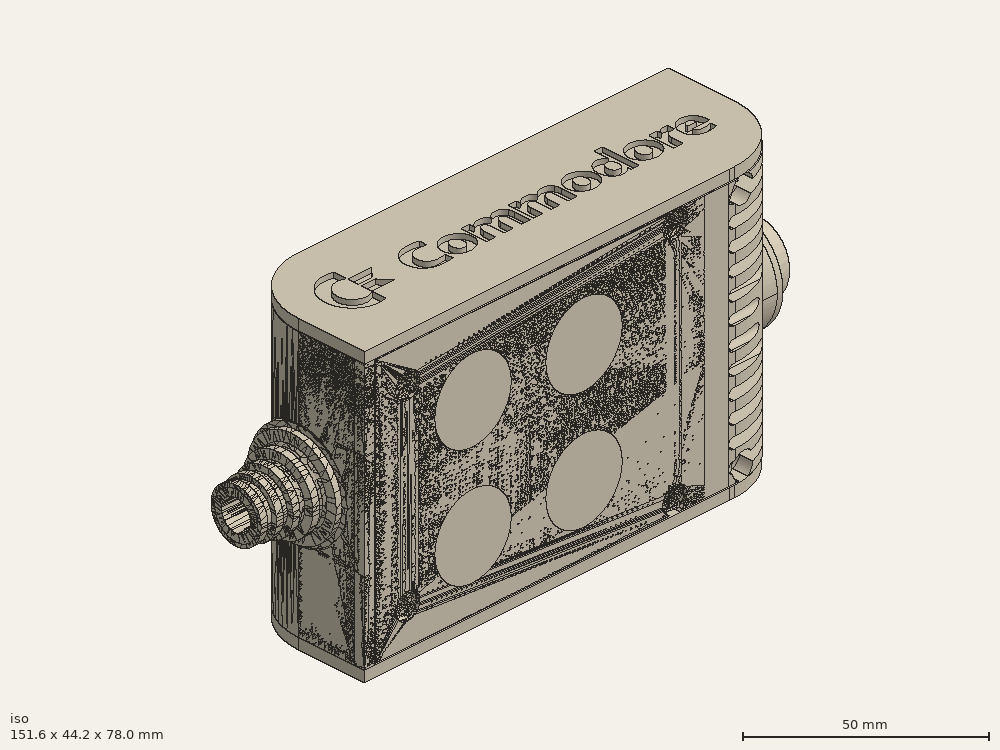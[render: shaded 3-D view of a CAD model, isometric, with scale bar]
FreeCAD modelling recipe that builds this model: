
FCSTD DOCUMENT  (FreeCAD 0.19R0.19.2)
Label: enclosure_214FCStd
License: All rights reserved
LicenseURL: http://en.wikipedia.org/wiki/All_rights_reserved
objects: Part::Revolution×152, Part::MultiFuse×146, Part::Feature×146, Sketcher::SketchObject×88, Part::Extrusion×73, Part::Cut×72, Part::Cylinder×70, Part::Fillet×58, Part::Box×36, App::MeasureDistance×4, Part::FeaturePython×2, Image::ImagePlane×1, PartDesign::Body×1, Part::Mirroring×1
note: 845 computed .brp shape members not serialized (recipe doc carries the construction recipe); baked Part::Feature solids carry a one-line shape summary decoded from their .brp

FEATURE [Sketcher::SketchObject] Sketch  label="topSketch"
  FullyConstrained = true
  sketch-geometry (20):
    g0: LineSegment StartX=5.21097e-06 StartY=3 StartZ=0 EndX=5.21097e-06 EndY=19 EndZ=0
    g1: ArcOfCircle CenterX=19 CenterY=19 CenterZ=0 NormalX=0 NormalY=0 NormalZ=1 AngleXU=0 Radius=19 StartAngle=1.5708 EndAngle=3.14159
    g2: ArcOfCircle CenterX=19 CenterY=19 CenterZ=0 NormalX=0 NormalY=0 NormalZ=1 AngleXU=0 Radius=16 StartAngle=1.5708 EndAngle=3.14159
    g3: LineSegment StartX=114 StartY=35 StartZ=0 EndX=19 EndY=35 EndZ=0
    g4: LineSegment StartX=5.21097e-06 StartY=3 StartZ=0 EndX=5.21097e-06 EndY=0 EndZ=0
    g5: LineSegment StartX=3 StartY=0 StartZ=0 EndX=5.21097e-06 EndY=0 EndZ=0
    g6: LineSegment StartX=3 StartY=19 StartZ=0 EndX=3 EndY=0 EndZ=0
    g7: LineSegment StartX=19 StartY=38 StartZ=0 EndX=124 EndY=38 EndZ=0
    g8: Circle CenterX=119 CenterY=35 CenterZ=0 NormalX=0 NormalY=0 NormalZ=1 AngleXU=0 Radius=1
    g9: Circle CenterX=121 CenterY=35 CenterZ=0 NormalX=0 NormalY=0 NormalZ=1 AngleXU=0 Radius=1
    g10: Circle CenterX=121 CenterY=33 CenterZ=0 NormalX=0 NormalY=0 NormalZ=1 AngleXU=0 Radius=1
    g11: BSplineCurve PolesCount=3 KnotsCount=2 Degree=2 IsPeriodic=0
    g12: GeomPoint X=119 Y=35 Z=0
    g13: GeomPoint X=121 Y=33 Z=0
    g14: LineSegment StartX=119 StartY=35 StartZ=0 EndX=114 EndY=35 EndZ=0
    g15: ArcOfCircle CenterX=105 CenterY=19 CenterZ=0 NormalX=0 NormalY=0 NormalZ=1 AngleXU=0 Radius=19 StartAngle=5.7297 EndAngle=6.28319
    g16: ArcOfCircle CenterX=105 CenterY=19 CenterZ=0 NormalX=0 NormalY=0 NormalZ=1 AngleXU=0 Radius=16 StartAngle=5.60905 EndAngle=6.28319
    g17: LineSegment StartX=121 StartY=33 StartZ=0 EndX=121 EndY=19 EndZ=0
    g18: LineSegment StartX=124 StartY=38 StartZ=0 EndX=124 EndY=19 EndZ=0
    g19: LineSegment StartX=117.5 StartY=9.01251 StartZ=0 EndX=121.163 EndY=9.0125 EndZ=0
  constraints (46):
    c: Vertical(g0)
    c: Block(g0)
    c: Coincident(g1,g0)
    c: Block(g1)
    c: Coincident(g2,g1)
    c: Block(g2)
    c: Coincident(g3,g2)
    c: Horizontal(g3)
    c: Tangent(g3,g2)
    c: Coincident(g4,g0)
    c: Distance(g4) = 3
    c: Vertical(g4)
    c: Coincident(g5,g4)
    c: Horizontal(g5)
    c: Coincident(g6,g2)
    c: Coincident(g6,g5)
    c: Vertical(g6)
    c: Horizontal(g7)
    c: Distance(g7) = 105
    c: Coincident(g7,g1)
    c: Block(g3)
    c: Weight(g8) = 1
    c: Equal(g8,g9)
    c: Equal(g8,g10)
    c: InternalAlignment(g8,g11)
    c: InternalAlignment(g9,g11)
    c: InternalAlignment(g10,g11)
    c: InternalAlignment(g12,g11)
    c: InternalAlignment(g13,g11)
    c: Block(g11)
    c: Coincident(g14,g11)
    c: Coincident(g14,g3)
    c: Horizontal(g14)
    c: Block(g15)
    c: Coincident(g16,g15)
    c: Block(g16)
    c: Coincident(g17,g11)
    c: Coincident(g17,g16)
    c: Vertical(g17)
    c: Distance(g17) = 14
    c: Coincident(g18,g7)
    c: Coincident(g18,g15)
    c: Vertical(g18)
    c: Distance(g18) = 19
    c: Coincident(g19,g16)
    c: Coincident(g19,g15)
FEATURE [Sketcher::SketchObject] Sketch001  label="bottomSketch"
  FullyConstrained = true
  sketch-geometry (32):
    g0: LineSegment StartX=3.3 StartY=-6.03275e-07 StartZ=0 EndX=98 EndY=-6.03275e-07 EndZ=0
    g1: ArcOfCircle CenterX=98 CenterY=19 CenterZ=0 NormalX=0 NormalY=0 NormalZ=1 AngleXU=0 Radius=19 StartAngle=4.71239 EndAngle=5.71103
    g2: LineSegment StartX=6.3 StartY=8 StartZ=0 EndX=3.3 EndY=8 EndZ=0
    g3: LineSegment StartX=3.3 StartY=8 StartZ=0 EndX=3.3 EndY=-6.03275e-07 EndZ=0
    g4: ArcOfCircle CenterX=8.3 CenterY=5 CenterZ=0 NormalX=0 NormalY=0 NormalZ=1 AngleXU=0 Radius=2 StartAngle=3.14159 EndAngle=4.71239
    g5: LineSegment StartX=6.3 StartY=8 StartZ=0 EndX=6.3 EndY=5 EndZ=0
    g6: ArcOfCircle CenterX=98 CenterY=19 CenterZ=0 NormalX=0 NormalY=0 NormalZ=1 AngleXU=0 Radius=12.7 StartAngle=4.71239 EndAngle=6.28319
    g7: LineSegment StartX=94.7 StartY=3 StartZ=0 EndX=8.3 EndY=3 EndZ=0
    g8-g12: Circle x5 (B-spline internal-alignment scaffolding for g13; pole/knot coordinates omitted)
    g13: BSplineCurve PolesCount=5 KnotsCount=3 Degree=3 IsPeriodic=0
    g14: GeomPoint X=98 Y=6.3 Z=0
    g15: GeomPoint X=96.3938 Y=4.71946 Z=0
    g16: GeomPoint X=94.7 Y=3 Z=0
    g17-g23: Circle x7 (B-spline internal-alignment scaffolding for g24; pole/knot coordinates omitted)
    g24: BSplineCurve PolesCount=7 KnotsCount=5 Degree=3 IsPeriodic=0
    g25-g29: GeomPoint x5 (B-spline internal-alignment scaffolding for g24; pole/knot coordinates omitted)
    g30: ArcOfCircle CenterX=98 CenterY=19 CenterZ=0 NormalX=0 NormalY=0 NormalZ=1 AngleXU=0 Radius=15.7 StartAngle=5.81226 EndAngle=6.28319
    g31: LineSegment StartX=110.7 StartY=19 StartZ=0 EndX=113.7 EndY=19 EndZ=0
  constraints (41):
    c: Horizontal(g0)
    c: Coincident(g1,g0)
    c: Block(g1)
    c: Horizontal(g2)
    c: Distance(g2) = 3
    c: Coincident(g3,g2)
    c: Vertical(g3)
    c: Coincident(g3,g0)
    c: Block(g4)
    c: Block(g2)
    c: Coincident(g5,g2)
    c: Coincident(g5,g4)
    c: Vertical(g5)
    c: Coincident(g6,g1)
    c: Block(g6)
    c: Coincident(g7,g4)
    c: Horizontal(g7)
    c: Block(g0)
    c: Block(g7)
    c: Block(g3)
    c: Coincident(g13,g6)
    c: Weight(g8) = 1
    c: Equal(g8, g9-g12) x4
    c: Coincident(g13,g7)
    c: InternalAlignment(g8-g12 -> g13) x5
    c: InternalAlignment(g14,g13)
    c: InternalAlignment(g15,g13)
    c: InternalAlignment(g16,g13)
    c: Block(g13)
    c: Weight(g17) = 1
    c: Equal(g17, g18-g23) x6
    c: Coincident(g24,g1)
    c: InternalAlignment(g17-g23 -> g24) x7
    c: InternalAlignment(g25-g29 -> g24) x5
    c: Block(g24)
    c: Coincident(g30,g24)
    c: Coincident(g31,g6)
    c: Coincident(g31,g30)
    c: Horizontal(g31)
    c: Block(g31)
    c: Block(g30)
FEATURE [Part::Extrusion] Extrude  label="top"
  Base = -> Sketch
  Dir = (0,0,1)
  DirMode = 2
  FaceMakerClass = Part::FaceMakerBullseye
  LengthFwd = 72
  LengthRev = 0
  Solid = true
  Symmetric = false
FEATURE [Part::Extrusion] Extrude001  label="bottom"
  Base = -> Sketch001
  Dir = (0,0,1)
  DirMode = 2
  FaceMakerClass = Part::FaceMakerBullseye
  LengthFwd = 71.4
  LengthRev = 0
  Placement = pos=(0,0,0.3) rot=(0,0,1;0rad)
  Solid = true
  Symmetric = false
FEATURE [Sketcher::SketchObject] Sketch002  label="topSketch001"
  FullyConstrained = true
  sketch-geometry (8):
    g0: ArcOfCircle CenterX=19 CenterY=19.0975 CenterZ=0 NormalX=0 NormalY=0 NormalZ=1 AngleXU=0 Radius=18.9025 StartAngle=1.5708 EndAngle=3.14674
    g1: LineSegment StartX=0.0977805 StartY=19.0003 StartZ=0 EndX=0.0977805 EndY=0.000251602 EndZ=0
    g2: LineSegment StartX=19 StartY=38 StartZ=0 EndX=124 EndY=38 EndZ=0
    g3: LineSegment StartX=0.0977805 StartY=0.000251602 StartZ=0 EndX=105.098 EndY=0.000251602 EndZ=0
    g4: LineSegment StartX=124 StartY=38 StartZ=0 EndX=125.616 EndY=38 EndZ=0
    g5: LineSegment StartX=105.098 StartY=0.000251602 StartZ=0 EndX=106.713 EndY=0.000251602 EndZ=0
    g6: ArcOfCircle CenterX=106.616 CenterY=19 CenterZ=0 NormalX=0 NormalY=0 NormalZ=1 AngleXU=0 Radius=19 StartAngle=4.71754 EndAngle=6.28319
    g7: LineSegment StartX=125.616 StartY=38 StartZ=0 EndX=125.616 EndY=19 EndZ=0
  constraints (21):
    c: Block(g0)
    c: Coincident(g1,g0)
    c: Vertical(g1)
    c: Horizontal(g2)
    c: Distance(g2) = 105
    c: Coincident(g2,g0)
    c: Distance(g1) = 19
    c: Coincident(g3,g1)
    c: Horizontal(g3)
    c: Distance(g3) = 105
    c: Coincident(g4,g2)
    c: Horizontal(g4)
    c: Distance(g4) = 1.61553
    c: Horizontal(g5)
    c: Equal(g4,g5) = 1.61553
    c: Coincident(g5,g3)
    c: Block(g6)
    c: Coincident(g6,g5)
    c: Coincident(g7,g4)
    c: Coincident(g7,g6)
    c: Vertical(g7)
FEATURE [Part::Extrusion] Extrude002  label="sideA"
  Base = -> Sketch002
  Dir = (0,0,1)
  DirMode = 2
  FaceMakerClass = Part::FaceMakerBullseye
  LengthFwd = 3
  LengthRev = 0
  Placement = pos=(0,0,-3) rot=(0,0,1;0rad)
  Solid = true
  Symmetric = false
FEATURE [Sketcher::SketchObject] Sketch003  label="topSketch002"
  FullyConstrained = true
  sketch-geometry (6):
    g0: LineSegment StartX=19 StartY=38 StartZ=0 EndX=117 EndY=38 EndZ=0
    g1: ArcOfCircle CenterX=19 CenterY=19 CenterZ=0 NormalX=0 NormalY=0 NormalZ=1 AngleXU=0 Radius=19 StartAngle=1.5708 EndAngle=3.14159
    g2: LineSegment StartX=117 StartY=38 StartZ=0 EndX=117 EndY=19 EndZ=0
    g3: LineSegment StartX=98 StartY=1.0161e-12 StartZ=0 EndX=5.22862e-06 EndY=1.0161e-12 EndZ=0
    g4: LineSegment StartX=5.22862e-06 StartY=19 StartZ=0 EndX=5.22862e-06 EndY=1.0161e-12 EndZ=0
    g5: ArcOfCircle CenterX=98 CenterY=19 CenterZ=0 NormalX=0 NormalY=0 NormalZ=1 AngleXU=0 Radius=19 StartAngle=4.71239 EndAngle=6.28319
  constraints (16):
    c: Horizontal(g0)
    c: Distance(g0) = 98
    c: Coincident(g1,g0)
    c: Block(g1)
    c: Coincident(g2,g0)
    c: Vertical(g2)
    c: Distance(g2) = 19
    c: Horizontal(g3)
    c: Coincident(g4,g1)
    c: Vertical(g4)
    c: Coincident(g3,g4)
    c: Block(g3)
    c: Coincident(g5,g2)
    c: Coincident(g5,g3)
    c: Block(g0)
    c: Block(g5)
FEATURE [Sketcher::SketchObject] Sketch004
  FullyConstrained = true
  MapMode = 3
  Placement = pos=(0,0,0) rot=(1,0,0;1.5708rad)
  Support = -> [Extrude]
  sketch-geometry (8):
    g0: Circle CenterX=80.351 CenterY=-67.6202 CenterZ=0 NormalX=0 NormalY=0 NormalZ=1 AngleXU=0 Radius=2
    g1: Circle CenterX=80.351 CenterY=-67.6202 CenterZ=0 NormalX=0 NormalY=0 NormalZ=1 AngleXU=0 Radius=3
    g2: Circle CenterX=80.351 CenterY=-4.92017 CenterZ=0 NormalX=0 NormalY=0 NormalZ=1 AngleXU=0 Radius=2
    g3: Circle CenterX=80.351 CenterY=-4.92017 CenterZ=0 NormalX=0 NormalY=0 NormalZ=1 AngleXU=0 Radius=3
    g4: Circle CenterX=23.851 CenterY=-4.92017 CenterZ=0 NormalX=0 NormalY=0 NormalZ=1 AngleXU=0 Radius=2
    g5: Circle CenterX=23.851 CenterY=-4.92017 CenterZ=0 NormalX=0 NormalY=0 NormalZ=1 AngleXU=0 Radius=3
    g6: Circle CenterX=23.851 CenterY=-67.6202 CenterZ=0 NormalX=0 NormalY=0 NormalZ=1 AngleXU=0 Radius=2
    g7: Circle CenterX=23.851 CenterY=-67.6202 CenterZ=0 NormalX=0 NormalY=0 NormalZ=1 AngleXU=0 Radius=3
  constraints (8):
    c: Block(g3)
    c: Block(g2)
    c: Block(g1)
    c: Block(g0)
    c: Block(g6)
    c: Block(g7)
    c: Block(g4)
    c: Block(g5)
FEATURE [Part::Extrusion] Extrude004
  Base = -> Sketch004
  Dir = (0,-1,2e-16)
  DirMode = 2
  FaceMakerClass = Part::FaceMakerBullseye
  LengthFwd = 6
  LengthRev = 0
  Placement = pos=(0,9,0) rot=(0,0,1;0rad)
  Solid = true
  Symmetric = false
FEATURE [Sketcher::SketchObject] Sketch005
  FullyConstrained = true
  MapMode = 3
  Placement = pos=(0,0,0) rot=(1,0,0;1.5708rad)
  Support = -> [Extrude]
  sketch-geometry (8):
    g0: Circle CenterX=80.351 CenterY=-67.6202 CenterZ=0 NormalX=0 NormalY=0 NormalZ=1 AngleXU=0 Radius=3
    g1: Circle CenterX=80.351 CenterY=-4.92017 CenterZ=0 NormalX=0 NormalY=0 NormalZ=1 AngleXU=0 Radius=3
    g2: Circle CenterX=23.851 CenterY=-4.92017 CenterZ=0 NormalX=0 NormalY=0 NormalZ=1 AngleXU=0 Radius=3
    g3: Circle CenterX=23.851 CenterY=-67.6202 CenterZ=0 NormalX=0 NormalY=0 NormalZ=1 AngleXU=0 Radius=3
    g4: Circle CenterX=23.851 CenterY=-67.6202 CenterZ=0 NormalX=0 NormalY=0 NormalZ=1 AngleXU=0 Radius=5
    g5: Circle CenterX=80.351 CenterY=-67.6202 CenterZ=0 NormalX=0 NormalY=0 NormalZ=1 AngleXU=0 Radius=5
    g6: Circle CenterX=23.851 CenterY=-4.92017 CenterZ=0 NormalX=0 NormalY=0 NormalZ=1 AngleXU=0 Radius=5
    g7: Circle CenterX=80.351 CenterY=-4.92017 CenterZ=0 NormalX=0 NormalY=0 NormalZ=1 AngleXU=0 Radius=5
  constraints (8):
    c: Block(g1)
    c: Block(g0)
    c: Block(g3)
    c: Block(g2)
    c: Block(g5)
    c: Block(g4)
    c: Block(g6)
    c: Block(g7)
FEATURE [Part::Extrusion] Extrude005
  Base = -> Sketch005
  Dir = (0,-1,2e-16)
  DirMode = 2
  FaceMakerClass = Part::FaceMakerBullseye
  LengthFwd = 2
  LengthRev = 0
  Solid = true
  Symmetric = false
FEATURE [Sketcher::SketchObject] Sketch006
  FullyConstrained = true
  MapMode = 3
  Placement = pos=(0,0,0) rot=(1,0,0;1.5708rad)
  sketch-geometry (8):
    g0: Circle CenterX=80.351 CenterY=-67.6202 CenterZ=0 NormalX=0 NormalY=0 NormalZ=1 AngleXU=0 Radius=3
    g1: Circle CenterX=80.351 CenterY=-4.92017 CenterZ=0 NormalX=0 NormalY=0 NormalZ=1 AngleXU=0 Radius=3
    g2: Circle CenterX=23.851 CenterY=-4.92017 CenterZ=0 NormalX=0 NormalY=0 NormalZ=1 AngleXU=0 Radius=3
    g3: Circle CenterX=23.851 CenterY=-67.6202 CenterZ=0 NormalX=0 NormalY=0 NormalZ=1 AngleXU=0 Radius=3
    g4: Circle CenterX=23.851 CenterY=-67.6202 CenterZ=0 NormalX=0 NormalY=0 NormalZ=1 AngleXU=0 Radius=5
    g5: Circle CenterX=80.351 CenterY=-67.6202 CenterZ=0 NormalX=0 NormalY=0 NormalZ=1 AngleXU=0 Radius=5
    g6: Circle CenterX=23.851 CenterY=-4.92017 CenterZ=0 NormalX=0 NormalY=0 NormalZ=1 AngleXU=0 Radius=5
    g7: Circle CenterX=80.351 CenterY=-4.92017 CenterZ=0 NormalX=0 NormalY=0 NormalZ=1 AngleXU=0 Radius=5
  constraints (8):
    c: Block(g1)
    c: Block(g0)
    c: Block(g3)
    c: Block(g2)
    c: Block(g5)
    c: Block(g4)
    c: Block(g6)
    c: Block(g7)
FEATURE [Part::Extrusion] Extrude007
  Base = -> Sketch006
  Dir = (0,-1,2e-16)
  DirMode = 2
  FaceMakerClass = Part::FaceMakerBullseye
  LengthFwd = 2
  LengthRev = 0
  Solid = true
  Symmetric = false
FEATURE [Part::Fillet] Fillet
  Base = -> Extrude007
  Edges = 4 edges r=1.99: [Edge6,Edge12,Edge18,Edge24]
FEATURE [Part::Cut] Cut
  Base = -> Extrude005
  Placement = pos=(0,5,0) rot=(0,0,1;0rad)
  Tool = -> Fillet
FEATURE [Part::MultiFuse] Fusion  label="pCBScrews"
  Placement = pos=(-2.5,0,72.3) rot=(0,0,1;0rad)
  Shapes = -> [Extrude004,Cut]
FEATURE [App::MeasureDistance] Distance  label="Distance: 0.69 mm"
  Distance = 0.685967
  P1 = (24.0138,2.9647,0.3)
  P2 = (23.8901,3,-0.373787)
FEATURE [App::MeasureDistance] Distance001  label="Distance: 0.53 mm"
  Distance = 0.533607
  P1 = (80.2939,3,72.2334)
  P2 = (80.281,2.99661,71.7)
FEATURE [Part::Fillet] Fillet001
  Base = -> Extrude001
  Edges = 1 edges r=2.4: [Edge17]
FEATURE [Part::Fillet] Fillet002  label="bottom001"
  Base = -> Fillet001
  Edges = 1 edges r=2.4: [Edge36]
FEATURE [Part::Fillet] Fillet003  label="top001"
  Base = -> Extrude
  Edges = 1 edges r=2: [Edge1]
FEATURE [Sketcher::SketchObject] Sketch007
  FullyConstrained = true
  sketch-geometry (16):
    g0: LineSegment StartX=4 StartY=0 StartZ=0 EndX=4 EndY=2.4 EndZ=0
    g1: LineSegment StartX=4 StartY=2.4 StartZ=0 EndX=7 EndY=2.4 EndZ=0
    g2: LineSegment StartX=4 StartY=0 StartZ=0 EndX=5.7 EndY=0 EndZ=0
    g3: LineSegment StartX=5.7 StartY=0 StartZ=0 EndX=5.7 EndY=-5.6 EndZ=0
    g4-g8: Circle x5 (B-spline internal-alignment scaffolding for g9; pole/knot coordinates omitted)
    g9: BSplineCurve PolesCount=5 KnotsCount=3 Degree=3 IsPeriodic=0
    g10: GeomPoint X=7 Y=2.4 Z=0
    g11: GeomPoint X=10.4582 Y=-1.55472 Z=0
    g12: GeomPoint X=14 Y=-5.6 Z=0
    g13: LineSegment StartX=14 StartY=-5.6 StartZ=0 EndX=14 EndY=-14.1 EndZ=0
    g14: LineSegment StartX=14 StartY=-14.1 StartZ=0 EndX=6.5 EndY=-14.1 EndZ=0
    g15: LineSegment StartX=5.7 StartY=-5.6 StartZ=0 EndX=6.5 EndY=-14.1 EndZ=0
  constraints (28):
    c: Distance(g0) = 2.4
    c: Vertical(g0)
    c: Block(g0)
    c: Coincident(g1,g0)
    c: Horizontal(g1)
    c: Distance(g1) = 3
    c: Coincident(g2,g0)
    c: Horizontal(g2)
    c: Distance(g2) = 1.7
    c: Coincident(g3,g2)
    c: Vertical(g3)
    c: Distance(g3) = 5.6
    c: Coincident(g9,g1)
    c: Weight(g4) = 1
    c: Equal(g4, g5-g8) x4
    c: InternalAlignment(g4-g8 -> g9) x5
    c: InternalAlignment(g10,g9)
    c: InternalAlignment(g11,g9)
    c: InternalAlignment(g12,g9)
    c: Block(g9)
    c: Coincident(g13,g9)
    c: Vertical(g13)
    c: Distance(g13) = 8.5
    c: Coincident(g14,g13)
    c: Horizontal(g14)
    c: Distance(g14) = 7.5
    c: Coincident(g15,g3)
    c: Coincident(g15,g14)
FEATURE [Part::Feature] Face
  shape: bbox 10 x 16.5 x 2e-07 mm, 1 faces, 0 solids (baked)
FEATURE [Part::Revolution] Revolve  label="plugHousing"
  Angle = 360
  Axis = (0,1,0)
  Base = (0,0,0)
  FaceMakerClass = Part::FaceMakerBullseye
  Placement = pos=(0,0,36.15) rot=(0,0,1;0rad)
  Solid = false
  Source = -> Face
  Symmetric = false
FEATURE [Part::Feature] Face001
  shape: bbox 10 x 16.5 x 2e-07 mm, 1 faces, 0 solids (baked)
FEATURE [Part::Revolution] Revolve001  label="plugHousing001"
  Angle = 360
  Axis = (0,1,0)
  Base = (0,0,0)
  FaceMakerClass = Part::FaceMakerBullseye
  Placement = pos=(0,0,36.15) rot=(0,0,1;0rad)
  Solid = false
  Source = -> Face001
  Symmetric = false
FEATURE [Part::MultiFuse] Fusion001  label="plugHousing002"
  Placement = pos=(0,0,0) rot=(0,0,1;1.5708rad)
  Shapes = -> [Revolve001,Revolve]
FEATURE [Part::Feature] Face002
  shape: bbox 10 x 16.5 x 2e-07 mm, 1 faces, 0 solids (baked)
FEATURE [Part::Revolution] Revolve003  label="plugHousing005"
  Angle = 360
  Axis = (0,1,0)
  Base = (0,0,0)
  FaceMakerClass = Part::FaceMakerBullseye
  Placement = pos=(0,0,36.15) rot=(0,0,1;0rad)
  Solid = false
  Source = -> Face002
  Symmetric = false
FEATURE [Part::Feature] Face003
  shape: bbox 10 x 16.5 x 2e-07 mm, 1 faces, 0 solids (baked)
FEATURE [Part::Revolution] Revolve002  label="plugHousing003"
  Angle = 360
  Axis = (0,1,0)
  Base = (0,0,0)
  FaceMakerClass = Part::FaceMakerBullseye
  Placement = pos=(0,0,36.15) rot=(0,0,1;0rad)
  Solid = false
  Source = -> Face003
  Symmetric = false
FEATURE [Part::MultiFuse] Fusion002  label="plugHousing004"
  Placement = pos=(0,0,0) rot=(0,0,1;1.5708rad)
  Shapes = -> [Revolve002,Revolve003]
FEATURE [Part::MultiFuse] Fusion003  label="plugHousing006"
  Placement = pos=(0,19,0) rot=(0,0,1;3.14159rad)
  Shapes = -> [Fusion002,Fusion001]
FEATURE [Part::Feature] Face004
  shape: bbox 10 x 16.5 x 2e-07 mm, 1 faces, 0 solids (baked)
FEATURE [Part::Revolution] Revolve006  label="plugHousing010"
  Angle = 360
  Axis = (0,1,0)
  Base = (0,0,0)
  FaceMakerClass = Part::FaceMakerBullseye
  Placement = pos=(0,0,36.15) rot=(0,0,1;0rad)
  Solid = false
  Source = -> Face004
  Symmetric = false
FEATURE [Part::Feature] Face005
  shape: bbox 10 x 16.5 x 2e-07 mm, 1 faces, 0 solids (baked)
FEATURE [Part::Revolution] Revolve007  label="plugHousing011"
  Angle = 360
  Axis = (0,1,0)
  Base = (0,0,0)
  FaceMakerClass = Part::FaceMakerBullseye
  Placement = pos=(0,0,36.15) rot=(0,0,1;0rad)
  Solid = false
  Source = -> Face005
  Symmetric = false
FEATURE [Part::Feature] Face006
  shape: bbox 10 x 16.5 x 2e-07 mm, 1 faces, 0 solids (baked)
FEATURE [Part::Revolution] Revolve004  label="plugHousing007"
  Angle = 360
  Axis = (0,1,0)
  Base = (0,0,0)
  FaceMakerClass = Part::FaceMakerBullseye
  Placement = pos=(0,0,36.15) rot=(0,0,1;0rad)
  Solid = false
  Source = -> Face006
  Symmetric = false
FEATURE [Part::MultiFuse] Fusion004  label="plugHousing009"
  Placement = pos=(0,0,0) rot=(0,0,1;1.5708rad)
  Shapes = -> [Revolve004,Revolve007]
FEATURE [Part::Feature] Face007
  shape: bbox 10 x 16.5 x 2e-07 mm, 1 faces, 0 solids (baked)
FEATURE [Part::Revolution] Revolve005  label="plugHousing008"
  Angle = 360
  Axis = (0,1,0)
  Base = (0,0,0)
  FaceMakerClass = Part::FaceMakerBullseye
  Placement = pos=(0,0,36.15) rot=(0,0,1;0rad)
  Solid = false
  Source = -> Face007
  Symmetric = false
FEATURE [Part::MultiFuse] Fusion005  label="plugHousing012"
  Placement = pos=(0,0,0) rot=(0,0,1;1.5708rad)
  Shapes = -> [Revolve006,Revolve005]
FEATURE [Part::MultiFuse] Fusion006  label="plugHousing013"
  Placement = pos=(0,19,0) rot=(0,0,1;3.14159rad)
  Shapes = -> [Fusion005,Fusion004]
FEATURE [Part::MultiFuse] Fusion007  label="plugHousing014"
  Placement = pos=(122.621,0,-0.15) rot=(0,0,1;0rad)
  Shapes = -> [Fusion003,Fusion006]
FEATURE [Part::Cylinder] Cylinder002
  Angle = 360
  AttacherType = Attacher::AttachEngine3D
  Height = 20
  Placement = pos=(0,0,36.15) rot=(0,0,1;0rad)
  Radius = 4
FEATURE [Part::Cylinder] Cylinder003
  Angle = 360
  AttacherType = Attacher::AttachEngine3D
  Height = 10
  Placement = pos=(0,0,36.15) rot=(0,0,1;0rad)
  Radius = 4
FEATURE [Part::MultiFuse] Fusion009  label="removeToCreateHoleForPlugHousing"
  Placement = pos=(70,19,36.15) rot=(0,1,0;1.5708rad)
  Shapes = -> [Cylinder002,Cylinder003]
FEATURE [Part::Cylinder] Cylinder004
  Angle = 360
  AttacherType = Attacher::AttachEngine3D
  Height = 20
  Placement = pos=(0,0,36.15) rot=(0,0,1;0rad)
  Radius = 4
FEATURE [Part::Cylinder] Cylinder005
  Angle = 360
  AttacherType = Attacher::AttachEngine3D
  Height = 10
  Placement = pos=(0,0,36.15) rot=(0,0,1;0rad)
  Radius = 4
FEATURE [Part::MultiFuse] Fusion010  label="removeToCreateHoleForPlugHousing001"
  Placement = pos=(70,19,36.15) rot=(0,1,0;1.5708rad)
  Shapes = -> [Cylinder004,Cylinder005]
FEATURE [Part::Cut] Cut001
  Base = -> Fillet003
  Tool = -> Fusion010
FEATURE [Part::Cut] Cut002  label="Bottom"
  Base = -> Fillet002
  Tool = -> Fusion009
FEATURE [Part::Feature] Face008
  shape: bbox 10 x 16.5 x 2e-07 mm, 1 faces, 0 solids (baked)
FEATURE [Part::Revolution] Revolve011  label="plugHousing021"
  Angle = 360
  Axis = (0,1,0)
  Base = (0,0,0)
  FaceMakerClass = Part::FaceMakerBullseye
  Placement = pos=(0,0,36.15) rot=(0,0,1;0rad)
  Solid = false
  Source = -> Face008
  Symmetric = false
FEATURE [Part::Feature] Face009
  shape: bbox 10 x 16.5 x 2e-07 mm, 1 faces, 0 solids (baked)
FEATURE [Part::Revolution] Revolve012  label="plugHousing022"
  Angle = 360
  Axis = (0,1,0)
  Base = (0,0,0)
  FaceMakerClass = Part::FaceMakerBullseye
  Placement = pos=(0,0,36.15) rot=(0,0,1;0rad)
  Solid = false
  Source = -> Face009
  Symmetric = false
FEATURE [Part::Feature] Face010 .. Face013  x4 (patterned run collapsed; names and placements below)
  shape: bbox 10 x 16.5 x 2e-07 mm, 1 faces, 0 solids (baked)
FEATURE [Part::Revolution] Revolve015  label="plugHousing027"
  Angle = 360
  Axis = (0,1,0)
  Base = (0,0,0)
  FaceMakerClass = Part::FaceMakerBullseye
  Placement = pos=(0,0,36.15) rot=(0,0,1;0rad)
  Solid = false
  Source = -> Face013
  Symmetric = false
FEATURE [Part::Feature] Face014
  shape: bbox 10 x 16.5 x 2e-07 mm, 1 faces, 0 solids (baked)
FEATURE [Part::Feature] Face015
  shape: bbox 10 x 16.5 x 2e-07 mm, 1 faces, 0 solids (baked)
FEATURE [Part::Feature] Face016
  shape: bbox 10 x 16.5 x 2e-07 mm, 1 faces, 0 solids (baked)
FEATURE [Part::Revolution] Revolve019  label="plugHousing033"
  Angle = 360
  Axis = (0,1,0)
  Base = (0,0,0)
  FaceMakerClass = Part::FaceMakerBullseye
  Placement = pos=(0,0,36.15) rot=(0,0,1;0rad)
  Solid = false
  Source = -> Face016
  Symmetric = false
FEATURE [Part::Feature] Face017
  shape: bbox 10 x 16.5 x 2e-07 mm, 1 faces, 0 solids (baked)
FEATURE [Part::Revolution] Revolve020  label="plugHousing034"
  Angle = 360
  Axis = (0,1,0)
  Base = (0,0,0)
  FaceMakerClass = Part::FaceMakerBullseye
  Placement = pos=(0,0,36.15) rot=(0,0,1;0rad)
  Solid = false
  Source = -> Face017
  Symmetric = false
FEATURE [Part::Feature] Face018
  shape: bbox 10 x 16.5 x 2e-07 mm, 1 faces, 0 solids (baked)
FEATURE [Part::Revolution] Revolve016  label="plugHousing030"
  Angle = 360
  Axis = (0,1,0)
  Base = (0,0,0)
  FaceMakerClass = Part::FaceMakerBullseye
  Placement = pos=(0,0,36.15) rot=(0,0,1;0rad)
  Solid = false
  Source = -> Face018
  Symmetric = false
FEATURE [Part::MultiFuse] Fusion020  label="plugHousing038"
  Placement = pos=(0,0,0) rot=(0,0,1;1.5708rad)
  Shapes = -> [Revolve016,Revolve020]
FEATURE [Part::Feature] Face019
  shape: bbox 10 x 16.5 x 2e-07 mm, 1 faces, 0 solids (baked)
FEATURE [Part::Feature] Face020
  shape: bbox 10 x 16.5 x 2e-07 mm, 1 faces, 0 solids (baked)
FEATURE [Part::Revolution] Revolve017  label="plugHousing031"
  Angle = 360
  Axis = (0,1,0)
  Base = (0,0,0)
  FaceMakerClass = Part::FaceMakerBullseye
  Placement = pos=(0,0,36.15) rot=(0,0,1;0rad)
  Solid = false
  Source = -> Face020
  Symmetric = false
FEATURE [Part::MultiFuse] Fusion021  label="plugHousing039"
  Placement = pos=(0,0,0) rot=(0,0,1;1.5708rad)
  Shapes = -> [Revolve019,Revolve017]
FEATURE [Part::MultiFuse] Fusion023  label="plugHousing041"
  Placement = pos=(0,19,0) rot=(0,0,1;3.14159rad)
  Shapes = -> [Fusion021,Fusion020]
FEATURE [Part::Revolution] Revolve022  label="plugHousing043"
  Angle = 360
  Axis = (0,1,0)
  Base = (0,0,0)
  FaceMakerClass = Part::FaceMakerBullseye
  Placement = pos=(0,0,36.15) rot=(0,0,1;0rad)
  Solid = false
  Source = -> Face019
  Symmetric = false
FEATURE [Part::Feature] Face021
  shape: bbox 10 x 16.5 x 2e-07 mm, 1 faces, 0 solids (baked)
FEATURE [Part::Revolution] Revolve023  label="plugHousing044"
  Angle = 360
  Axis = (0,1,0)
  Base = (0,0,0)
  FaceMakerClass = Part::FaceMakerBullseye
  Placement = pos=(0,0,36.15) rot=(0,0,1;0rad)
  Solid = false
  Source = -> Face021
  Symmetric = false
FEATURE [Part::Feature] Face022
  shape: bbox 10 x 16.5 x 2e-07 mm, 1 faces, 0 solids (baked)
FEATURE [Part::Revolution] Revolve018  label="plugHousing032"
  Angle = 360
  Axis = (0,1,0)
  Base = (0,0,0)
  FaceMakerClass = Part::FaceMakerBullseye
  Placement = pos=(0,0,36.15) rot=(0,0,1;0rad)
  Solid = false
  Source = -> Face022
  Symmetric = false
FEATURE [Part::MultiFuse] Fusion022  label="plugHousing040"
  Placement = pos=(0,0,0) rot=(0,0,1;1.5708rad)
  Shapes = -> [Revolve018,Revolve023]
FEATURE [Part::Feature] Face023
  shape: bbox 10 x 16.5 x 2e-07 mm, 1 faces, 0 solids (baked)
FEATURE [Part::Revolution] Revolve021  label="plugHousing035"
  Angle = 360
  Axis = (0,1,0)
  Base = (0,0,0)
  FaceMakerClass = Part::FaceMakerBullseye
  Placement = pos=(0,0,36.15) rot=(0,0,1;0rad)
  Solid = false
  Source = -> Face023
  Symmetric = false
FEATURE [Part::MultiFuse] Fusion018  label="plugHousing036"
  Placement = pos=(0,0,0) rot=(0,0,1;1.5708rad)
  Shapes = -> [Revolve022,Revolve021]
FEATURE [Part::MultiFuse] Fusion019  label="plugHousing037"
  Placement = pos=(0,19,0) rot=(0,0,1;3.14159rad)
  Shapes = -> [Fusion018,Fusion022]
FEATURE [Part::MultiFuse] Fusion024  label="plugHousing042"
  Placement = pos=(122.621,0,-0.15) rot=(0,0,1;0rad)
  Shapes = -> [Fusion023,Fusion019]
FEATURE [Part::Cylinder] Cylinder006
  Angle = 360
  AttacherType = Attacher::AttachEngine3D
  Height = 20
  Placement = pos=(0,0,36.15) rot=(0,0,1;0rad)
  Radius = 14.3
FEATURE [Part::Cylinder] Cylinder007
  Angle = 360
  AttacherType = Attacher::AttachEngine3D
  Height = 10
  Placement = pos=(0,0,36.15) rot=(0,0,1;0rad)
  Radius = 4
FEATURE [Part::MultiFuse] Fusion026  label="removeToCreteHoleForPlugHousing"
  Placement = pos=(70,19,36) rot=(0,1,0;1.5708rad)
  Shapes = -> [Cylinder006,Cylinder007]
FEATURE [Part::Box] Box001  label="Cube001"
  AttacherType = Attacher::AttachEngine3D
  Height = 28
  Length = 3
  Placement = pos=(110.7,19,22) rot=(0,0,1;0rad)
  Width = 15.7
FEATURE [Part::Cut] Cut003  label="top002"
  Base = -> Cut001
  Tool = -> Fusion007
FEATURE [Part::Revolution] Revolve008  label="plugHousing015"
  Angle = 360
  Axis = (0,1,0)
  Base = (0,0,0)
  FaceMakerClass = Part::FaceMakerBullseye
  Placement = pos=(0,0,36.15) rot=(0,0,1;0rad)
  Solid = false
  Source = -> Face010
  Symmetric = false
FEATURE [Part::MultiFuse] Fusion013  label="plugHousing020"
  Placement = pos=(0,0,0) rot=(0,0,1;1.5708rad)
  Shapes = -> [Revolve008,Revolve012]
FEATURE [Part::Cut] Cut004  label="top003"
  Base = -> Cut003
  Placement = pos=(1,0,0) rot=(0,0,1;0rad)
  Tool = -> Fusion026
FEATURE [Part::Cylinder] Cylinder008
  Angle = 360
  AttacherType = Attacher::AttachEngine3D
  Height = 20
  Placement = pos=(0,0,36.15) rot=(0,0,1;0rad)
  Radius = 10.3
FEATURE [Part::Cylinder] Cylinder009
  Angle = 360
  AttacherType = Attacher::AttachEngine3D
  Height = 10
  Placement = pos=(0,0,36.15) rot=(0,0,1;0rad)
  Radius = 4
FEATURE [Part::MultiFuse] Fusion027  label="removeToCreteHoleForPlugHousing001"
  Placement = pos=(70,19,36) rot=(0,1,0;1.5708rad)
  Shapes = -> [Cylinder008,Cylinder009]
FEATURE [Part::Cut] Cut005  label="plugHousingTab"
  Base = -> Box001
  Tool = -> Fusion027
FEATURE [Part::MultiFuse] Fusion028  label="plugHousing045"
  Shapes = -> [Fusion024,Cut005]
FEATURE [Part::Box] Box002  label="Cube002"
  AttacherType = Attacher::AttachEngine3D
  Height = 28.8
  Length = 3
  Placement = pos=(107.3,28,21.6) rot=(0,0,1;0rad)
  Width = 7
FEATURE [Part::Box] Box003  label="Cube003"
  AttacherType = Attacher::AttachEngine3D
  Height = 3
  Length = 6.4
  Placement = pos=(107.3,28,18.6) rot=(0,0,1;0rad)
  Width = 7
FEATURE [Part::Box] Box004  label="Cube004"
  AttacherType = Attacher::AttachEngine3D
  Height = 3
  Length = 6.4
  Placement = pos=(107.3,28,50.4) rot=(0,0,1;0rad)
  Width = 7
FEATURE [Part::MultiFuse] Fusion029  label="plugHousingBracketHolder"
  Shapes = -> [Box004,Box002,Box003]
FEATURE [Part::Cylinder] Cylinder010
  Angle = 360
  AttacherType = Attacher::AttachEngine3D
  Height = 20
  Placement = pos=(0,0,36.15) rot=(0,0,1;0rad)
  Radius = 14.3
FEATURE [Part::Cylinder] Cylinder011
  Angle = 360
  AttacherType = Attacher::AttachEngine3D
  Height = 10
  Placement = pos=(0,0,36.15) rot=(0,0,1;0rad)
  Radius = 4
FEATURE [Part::MultiFuse] Fusion030  label="removeToCreteHoleForPlugHousing002"
  Placement = pos=(70,19,36) rot=(0,1,0;1.5708rad)
  Shapes = -> [Cylinder010,Cylinder011]
FEATURE [Part::Cut] Cut006  label="plugHousingBracketHolder001"
  Base = -> Fusion029
  Tool = -> Fusion030
FEATURE [Part::Cylinder] Cylinder012
  Angle = 360
  AttacherType = Attacher::AttachEngine3D
  Height = 20
  Placement = pos=(0,0,36.15) rot=(0,0,1;0rad)
  Radius = 7
FEATURE [Part::Cylinder] Cylinder013
  Angle = 360
  AttacherType = Attacher::AttachEngine3D
  Height = 10
  Placement = pos=(0,0,36.15) rot=(0,0,1;0rad)
  Radius = 4
FEATURE [Part::MultiFuse] Fusion032  label="removeToCreteHoleForPlugHousing003"
  Placement = pos=(70,19,36) rot=(0,1,0;1.5708rad)
  Shapes = -> [Cylinder012,Cylinder013]
FEATURE [Part::Cut] Cut007  label="bottom002"
  Base = -> Cut002
  Tool = -> Fusion032
FEATURE [Sketcher::SketchObject] Sketch008
  FullyConstrained = true
  sketch-geometry (54):
    g0: LineSegment StartX=-4.2 StartY=0 StartZ=0 EndX=-6.2 EndY=0 EndZ=0
    g1: LineSegment StartX=-14 StartY=-18 StartZ=0 EndX=-14 EndY=-26.5 EndZ=0
    g2: LineSegment StartX=-4.2 StartY=0 StartZ=0 EndX=-4.2 EndY=-13.4877 EndZ=0
    g3: Circle CenterX=-4.2 CenterY=-13.4877 CenterZ=0 NormalX=0 NormalY=0 NormalZ=1 AngleXU=0 Radius=1
    g4: Circle CenterX=-4.2 CenterY=-26.5 CenterZ=0 NormalX=0 NormalY=0 NormalZ=1 AngleXU=0 Radius=1
    g5: Circle CenterX=-8.2 CenterY=-26.5 CenterZ=0 NormalX=0 NormalY=0 NormalZ=1 AngleXU=0 Radius=1
    g6: BSplineCurve PolesCount=3 KnotsCount=2 Degree=2 IsPeriodic=0
    g7: GeomPoint X=-4.2 Y=-13.4877 Z=0
    g8: GeomPoint X=-8.2 Y=-26.5 Z=0
    g9: LineSegment StartX=-14 StartY=-26.5 StartZ=0 EndX=-8.2 EndY=-26.5 EndZ=0
    g10: LineSegment StartX=-10.15 StartY=-12 StartZ=0 EndX=-10.15 EndY=-14 EndZ=0
    g11: LineSegment StartX=-12.8401 StartY=-16 StartZ=0 EndX=-10.1571 EndY=-16 EndZ=0
    g12: LineSegment StartX=-10.15 StartY=-14 StartZ=0 EndX=-8.70761 EndY=-14 EndZ=0
    g13: LineSegment StartX=-12.8401 StartY=-16 StartZ=0 EndX=-12.8401 EndY=-17.6958 EndZ=0
    g14: LineSegment StartX=-10.15 StartY=-12 StartZ=0 EndX=-7.79258 EndY=-12 EndZ=0
    g15: Circle CenterX=-6.2215 CenterY=-2 CenterZ=0 NormalX=0 NormalY=0 NormalZ=1 AngleXU=0 Radius=1
    g16: Circle CenterX=-6.22762 CenterY=-2.58724 CenterZ=0 NormalX=0 NormalY=0 NormalZ=1 AngleXU=0 Radius=1
    g17: Circle CenterX=-6.32538 CenterY=-4 CenterZ=0 NormalX=0 NormalY=0 NormalZ=1 AngleXU=0 Radius=1
    g18: BSplineCurve PolesCount=3 KnotsCount=2 Degree=2 IsPeriodic=0
    g19: GeomPoint X=-6.2215 Y=-2 Z=0
    g20: GeomPoint X=-6.32538 Y=-4 Z=0
    g21: Circle CenterX=-6.48644 CenterY=-5.99526 CenterZ=0 NormalX=0 NormalY=0 NormalZ=1 AngleXU=0 Radius=1
    g22: Circle CenterX=-6.58486 CenterY=-6.99526 CenterZ=0 NormalX=0 NormalY=0 NormalZ=1 AngleXU=0 Radius=1
    g23: Circle CenterX=-6.77343 CenterY=-8 CenterZ=0 NormalX=0 NormalY=0 NormalZ=1 AngleXU=0 Radius=1
    g24: BSplineCurve PolesCount=3 KnotsCount=2 Degree=2 IsPeriodic=0
    g25: GeomPoint X=-6.48644 Y=-5.99526 Z=0
    g26: GeomPoint X=-6.77343 Y=-8 Z=0
    g27: Circle CenterX=-7.19003 CenterY=-10 CenterZ=0 NormalX=0 NormalY=0 NormalZ=1 AngleXU=0 Radius=1
    g28: Circle CenterX=-7.44407 CenterY=-11.0915 CenterZ=0 NormalX=0 NormalY=0 NormalZ=1 AngleXU=0 Radius=1
    g29: Circle CenterX=-7.79258 CenterY=-12 CenterZ=0 NormalX=0 NormalY=0 NormalZ=1 AngleXU=0 Radius=1
    g30: BSplineCurve PolesCount=3 KnotsCount=2 Degree=2 IsPeriodic=0
    g31: GeomPoint X=-7.19003 Y=-10 Z=0
    g32: GeomPoint X=-7.79258 Y=-12 Z=0
    g33: Circle CenterX=-8.70761 CenterY=-14 CenterZ=0 NormalX=0 NormalY=0 NormalZ=1 AngleXU=0 Radius=1
    g34: Circle CenterX=-9.33087 CenterY=-15.1837 CenterZ=0 NormalX=0 NormalY=0 NormalZ=1 AngleXU=0 Radius=1
    g35: Circle CenterX=-10.1571 CenterY=-16 CenterZ=0 NormalX=0 NormalY=0 NormalZ=1 AngleXU=0 Radius=1
    g36: BSplineCurve PolesCount=3 KnotsCount=2 Degree=2 IsPeriodic=0
    g37: GeomPoint X=-8.70761 Y=-14 Z=0
    g38: GeomPoint X=-10.1571 Y=-16 Z=0
    g39: Circle CenterX=-12.8401 CenterY=-17.6958 CenterZ=0 NormalX=0 NormalY=0 NormalZ=1 AngleXU=0 Radius=1
    g40: Circle CenterX=-13.3521 CenterY=-17.9027 CenterZ=0 NormalX=0 NormalY=0 NormalZ=1 AngleXU=0 Radius=1
    g41: Circle CenterX=-14 CenterY=-18 CenterZ=0 NormalX=0 NormalY=0 NormalZ=1 AngleXU=0 Radius=1
    g42: BSplineCurve PolesCount=3 KnotsCount=2 Degree=2 IsPeriodic=0
    g43: GeomPoint X=-12.8401 Y=-17.6958 Z=0
    g44: GeomPoint X=-14 Y=-18 Z=0
    g45: LineSegment StartX=-6.2 StartY=0 StartZ=0 EndX=-7.2 EndY=0 EndZ=0
    g46: LineSegment StartX=-7.2 StartY=0 StartZ=0 EndX=-7.2 EndY=-2 EndZ=0
    g47: LineSegment StartX=-7.2 StartY=-2 StartZ=0 EndX=-6.2215 EndY=-2 EndZ=0
    g48: LineSegment StartX=-6.32538 StartY=-4 StartZ=0 EndX=-7.65538 EndY=-4 EndZ=0
    g49: LineSegment StartX=-7.65538 StartY=-4 StartZ=0 EndX=-7.65538 EndY=-5.99526 EndZ=0
    g50: LineSegment StartX=-7.65538 StartY=-5.99526 StartZ=0 EndX=-6.48644 EndY=-5.99526 EndZ=0
    g51: LineSegment StartX=-6.77343 StartY=-8 StartZ=0 EndX=-8.43343 EndY=-8 EndZ=0
    g52: LineSegment StartX=-8.43343 StartY=-8 StartZ=0 EndX=-8.43343 EndY=-10 EndZ=0
    g53: LineSegment StartX=-8.43343 StartY=-10 StartZ=0 EndX=-7.19003 EndY=-10 EndZ=0
  constraints (112):
    c: Horizontal(g0)
    c: Distance(g0) = 2
    c: Block(g0)
    c: Vertical(g1)
    c: Coincident(g2,g0)
    c: Vertical(g2)
    c: Block(g2)
    c: Coincident(g6,g2)
    c: Weight(g3) = 1
    c: Equal(g3,g4)
    c: Equal(g3,g5)
    c: InternalAlignment(g3,g6)
    c: InternalAlignment(g4,g6)
    c: InternalAlignment(g5,g6)
    c: InternalAlignment(g7,g6)
    c: InternalAlignment(g8,g6)
    c: Block(g6)
    c: Coincident(g9,g1)
    c: Coincident(g9,g6)
    c: Horizontal(g9)
    c: Vertical(g10)
    c: Block(g10)
    c: Horizontal(g11)
    c: Block(g11)
    c: Coincident(g12,g10)
    c: Horizontal(g12)
    c: Block(g12)
    c: Coincident(g13,g11)
    c: Vertical(g13)
    c: Block(g13)
    c: Coincident(g14,g10)
    c: Horizontal(g14)
    c: Block(g14)
    c: Block(g9)
    c: Block(g1)
    c: Weight(g15) = 1
    c: Equal(g15,g16)
    c: Equal(g15,g17)
    c: InternalAlignment(g15,g18)
    c: InternalAlignment(g16,g18)
    c: InternalAlignment(g17,g18)
    c: InternalAlignment(g19,g18)
    c: InternalAlignment(g20,g18)
    c: Weight(g21) = 1
    c: Equal(g21,g22)
    c: Equal(g21,g23)
    c: InternalAlignment(g21,g24)
    c: InternalAlignment(g22,g24)
    c: InternalAlignment(g23,g24)
    c: InternalAlignment(g25,g24)
    c: InternalAlignment(g26,g24)
    c: Weight(g27) = 1
    c: Equal(g27,g28)
    c: Equal(g27,g29)
    c: Coincident(g30,g14)
    c: InternalAlignment(g27,g30)
    c: InternalAlignment(g28,g30)
    c: InternalAlignment(g29,g30)
    c: InternalAlignment(g31,g30)
    c: InternalAlignment(g32,g30)
    c: Coincident(g36,g12)
    c: Weight(g33) = 1
    c: Equal(g33,g34)
    c: Equal(g33,g35)
    c: Coincident(g36,g11)
    c: InternalAlignment(g33,g36)
    c: InternalAlignment(g34,g36)
    c: InternalAlignment(g35,g36)
    c: InternalAlignment(g37,g36)
    c: InternalAlignment(g38,g36)
    c: Coincident(g42,g13)
    c: Weight(g39) = 1
    c: Equal(g39,g40)
    c: Equal(g39,g41)
    c: Coincident(g42,g1)
    c: InternalAlignment(g39,g42)
    c: InternalAlignment(g40,g42)
    c: InternalAlignment(g41,g42)
    c: InternalAlignment(g43,g42)
    c: InternalAlignment(g44,g42)
    c: Block(g18)
    c: Block(g24)
    c: Block(g30)
    c: Block(g36)
    c: Block(g42)
    c: Horizontal(g45)
    c: Coincident(g45,g0)
    c: Vertical(g46)
    c: Coincident(g46,g45)
    c: Coincident(g47,g46)
    c: Coincident(g47,g18)
    c: Horizontal(g47)
    c: Block(g46)
    c: Coincident(g48,g18)
    c: Horizontal(g48)
    c: Distance(g48) = 1.33
    c: Vertical(g49)
    c: Coincident(g49,g48)
    c: Coincident(g50,g49)
    c: Coincident(g50,g24)
    c: Horizontal(g50)
    c: Tangent(g50,g22)
    c: Horizontal(g51)
    c: Coincident(g51,g24)
    c: Block(g51)
    c: Vertical(g52)
    c: Block(g52)
    c: Coincident(g52,g51)
    c: Coincident(g53,g52)
    c: Coincident(g53,g30)
    c: Horizontal(g53)
    c: Distance(g1) = 8.5
FEATURE [Part::Feature] Face024
  shape: bbox 9.8 x 26.5 x 2e-07 mm, 1 faces, 0 solids (baked)
FEATURE [Part::Revolution] Revolve024
  Angle = 360
  Axis = (0,1,0)
  Base = (0,0,0)
  FaceMakerClass = Part::FaceMakerBullseye
  Placement = pos=(0,0,0) rot=(0,0,1;1.5708rad)
  Solid = false
  Source = -> Face024
  Symmetric = false
FEATURE [Part::Feature] Face025
  shape: bbox 9.8 x 26.5 x 2e-07 mm, 1 faces, 0 solids (baked)
FEATURE [Part::Revolution] Revolve025
  Angle = 360
  Axis = (0,1,0)
  Base = (0,0,0)
  FaceMakerClass = Part::FaceMakerBullseye
  Placement = pos=(0,0,0) rot=(0,0,1;1.5708rad)
  Solid = false
  Source = -> Face025
  Symmetric = false
FEATURE [Part::MultiFuse] Fusion033
  Placement = pos=(-18,19,36) rot=(0,0,1;0rad)
  Shapes = -> [Revolve025,Revolve024]
FEATURE [Part::Cylinder] Cylinder014
  Angle = 360
  AttacherType = Attacher::AttachEngine3D
  Height = 20
  Placement = pos=(0,0,36.15) rot=(0,0,1;0rad)
  Radius = 14.3
FEATURE [Part::Cylinder] Cylinder015
  Angle = 360
  AttacherType = Attacher::AttachEngine3D
  Height = 10
  Placement = pos=(0,0,36.15) rot=(0,0,1;0rad)
  Radius = 4
FEATURE [Part::MultiFuse] Fusion034  label="removeToCreteHoleForPlugHousing004"
  Placement = pos=(-42,19,36) rot=(0,1,0;1.5708rad)
  Shapes = -> [Cylinder014,Cylinder015]
FEATURE [Part::Cut] Cut008  label="top004"
  Base = -> Cut004
  Placement = pos=(-1,0,0) rot=(0,0,1;0rad)
  Tool = -> Fusion034
FEATURE [Part::Box] Box005  label="Cube005"
  AttacherType = Attacher::AttachEngine3D
  Height = 28
  Length = 3
  Placement = pos=(110.7,19,22) rot=(0,0,1;0rad)
  Width = 15.7
FEATURE [Part::Cylinder] Cylinder016
  Angle = 360
  AttacherType = Attacher::AttachEngine3D
  Height = 10
  Placement = pos=(0,0,36.15) rot=(0,0,1;0rad)
  Radius = 4
FEATURE [Part::Cylinder] Cylinder017
  Angle = 360
  AttacherType = Attacher::AttachEngine3D
  Height = 20
  Placement = pos=(0,0,36.15) rot=(0,0,1;0rad)
  Radius = 10.3
FEATURE [Part::MultiFuse] Fusion035  label="removeToCreteHoleForPlugHousing005"
  Placement = pos=(70,19,36) rot=(0,1,0;1.5708rad)
  Shapes = -> [Cylinder017,Cylinder016]
FEATURE [Part::Cut] Cut009  label="plugHousingTab001"
  Base = -> Box005
  Placement = pos=(-107.4,-14,0) rot=(0,0,1;0rad)
  Tool = -> Fusion035
FEATURE [Part::Box] Box006  label="Cube006"
  AttacherType = Attacher::AttachEngine3D
  Height = 28
  Length = 3
  Placement = pos=(110.7,19,22) rot=(0,0,1;0rad)
  Width = 15.7
FEATURE [Part::Cylinder] Cylinder018
  Angle = 360
  AttacherType = Attacher::AttachEngine3D
  Height = 10
  Placement = pos=(0,0,36.15) rot=(0,0,1;0rad)
  Radius = 4
FEATURE [Part::Cylinder] Cylinder019
  Angle = 360
  AttacherType = Attacher::AttachEngine3D
  Height = 20
  Placement = pos=(0,0,36.15) rot=(0,0,1;0rad)
  Radius = 10.3
FEATURE [Part::MultiFuse] Fusion036  label="removeToCreteHoleForPlugHousing006"
  Placement = pos=(70,19,36) rot=(0,1,0;1.5708rad)
  Shapes = -> [Cylinder019,Cylinder018]
FEATURE [Part::Cut] Cut010  label="plugHousingTab002"
  Base = -> Box006
  Placement = pos=(-107.4,-14,0) rot=(0,0,1;0rad)
  Tool = -> Fusion036
FEATURE [Part::MultiFuse] Fusion037
  Placement = pos=(9.6,23,0) rot=(0,0,1;3.14159rad)
  Shapes = -> [Cut009,Cut010]
FEATURE [Part::Box] Box  label="Cube"
  AttacherType = Attacher::AttachEngine3D
  Height = 10
  Length = 3
  Placement = pos=(3.3,4,12) rot=(0,0,1;0rad)
  Width = 10
FEATURE [Part::Fillet] Fillet004
  Base = -> Fusion028
  Edges = 1 edges r=2: [Edge25]
FEATURE [Part::Fillet] Fillet005  label="plugHousing046"
  Base = -> Fillet004
  Edges = 1 edges r=2: [Edge8]
FEATURE [Part::Fillet] Fillet006
  Base = -> Box
  Edges = 1 edges r=2: [Edge11]
FEATURE [Part::Box] Box007  label="Cube007"
  AttacherType = Attacher::AttachEngine3D
  Height = 10
  Length = 3
  Placement = pos=(3.3,4,50) rot=(0,0,1;0rad)
  Width = 10
FEATURE [Part::Fillet] Fillet007
  Base = -> Box007
  Edges = 1 edges r=2: [Edge12]
FEATURE [Part::Box] Box008  label="Cube008"
  AttacherType = Attacher::AttachEngine3D
  Height = 28
  Length = 4
  Placement = pos=(5,0,22) rot=(0,0,1;0rad)
  Width = 10
FEATURE [Part::Fillet] Fillet008
  Base = -> Box008
  Edges = 1 edges r=1: [Edge7]
FEATURE [Part::Fillet] Fillet009
  Base = -> Fillet008
  Edges = 1 edges r=2: [Edge5]
FEATURE [Part::Fillet] Fillet010
  Base = -> Fillet009
  Edges = 1 edges r=2: [Edge2]
FEATURE [Sketcher::SketchObject] Sketch009  label="topSketch003"
  FullyConstrained = true
  sketch-geometry (4):
    g0: LineSegment StartX=16.8446 StartY=31.512 StartZ=0 EndX=16.3251 EndY=34.4666 EndZ=0
    g1: ArcOfCircle CenterX=19 CenterY=19.2524 CenterZ=0 NormalX=0 NormalY=0 NormalZ=1 AngleXU=0 Radius=15.4476 StartAngle=1.74483 EndAngle=2.72717
    g2: ArcOfCircle CenterX=19 CenterY=19.2524 CenterZ=0 NormalX=0 NormalY=0 NormalZ=1 AngleXU=0 Radius=12.4476 StartAngle=1.74483 EndAngle=2.73189
    g3: LineSegment StartX=4.86004 StartY=25.4725 StartZ=0 EndX=7.58253 EndY=24.2107 EndZ=0
  constraints (7):
    c: Block(g0)
    c: Coincident(g1,g0)
    c: Coincident(g2,g0)
    c: Coincident(g3,g1)
    c: Coincident(g3,g2)
    c: Block(g1)
    c: Block(g2)
FEATURE [Part::Extrusion] Extrude008
  Base = -> Sketch009
  Dir = (0,0,1)
  DirMode = 2
  FaceMakerClass = Part::FaceMakerBullseye
  LengthFwd = 10
  LengthRev = 0
  Placement = pos=(0,0,31) rot=(0,0,1;0rad)
  Solid = true
  Symmetric = false
FEATURE [Part::Cylinder] Cylinder020
  Angle = 360
  AttacherType = Attacher::AttachEngine3D
  Height = 20
  Placement = pos=(0,0,36.15) rot=(0,0,1;0rad)
  Radius = 8.2
FEATURE [Part::Cylinder] Cylinder021
  Angle = 360
  AttacherType = Attacher::AttachEngine3D
  Height = 10
  Placement = pos=(0,0,36.15) rot=(0,0,1;0rad)
  Radius = 4
FEATURE [Part::MultiFuse] Fusion038  label="removeToCreteHoleForPlugHousing007"
  Placement = pos=(-42,19,36) rot=(0,1,0;1.5708rad)
  Shapes = -> [Cylinder020,Cylinder021]
FEATURE [Part::Cut] Cut011
  Base = -> Extrude008
  Tool = -> Fusion038
FEATURE [Part::Fillet] Fillet011
  Base = -> Cut011
  Edges = 1 edges r=2: [Edge1]
FEATURE [Part::Fillet] Fillet012
  Base = -> Fillet011
  Edges = 1 edges r=2.5: [Edge1]
FEATURE [Part::Fillet] Fillet013
  Base = -> Fillet012
  Edges = 1 edges r=2.5: [Edge2]
FEATURE [Part::Box] Box010  label="Cube010"
  AttacherType = Attacher::AttachEngine3D
  Height = 16
  Length = 8
  Placement = pos=(12.7,31.52,28) rot=(0,0,1;0rad)
  Width = 4
FEATURE [Sketcher::SketchObject] Sketch010  label="topSketch004"
  FullyConstrained = true
  sketch-geometry (4):
    g0: LineSegment StartX=16.8446 StartY=31.512 StartZ=0 EndX=16.3251 EndY=34.4666 EndZ=0
    g1: ArcOfCircle CenterX=19 CenterY=19.2524 CenterZ=0 NormalX=0 NormalY=0 NormalZ=1 AngleXU=0 Radius=15.4476 StartAngle=1.74483 EndAngle=2.72717
    g2: ArcOfCircle CenterX=19 CenterY=19.2524 CenterZ=0 NormalX=0 NormalY=0 NormalZ=1 AngleXU=0 Radius=12.4476 StartAngle=1.74483 EndAngle=2.73189
    g3: LineSegment StartX=4.86004 StartY=25.4725 StartZ=0 EndX=7.58253 EndY=24.2107 EndZ=0
  constraints (7):
    c: Block(g0)
    c: Coincident(g1,g0)
    c: Coincident(g2,g0)
    c: Coincident(g3,g1)
    c: Coincident(g3,g2)
    c: Block(g1)
    c: Block(g2)
FEATURE [Part::Cylinder] Cylinder022
  Angle = 360
  AttacherType = Attacher::AttachEngine3D
  Height = 10
  Placement = pos=(0,0,36.15) rot=(0,0,1;0rad)
  Radius = 4
FEATURE [Sketcher::SketchObject] Sketch011  label="topSketch005"
  FullyConstrained = true
  sketch-geometry (4):
    g0: LineSegment StartX=16.8446 StartY=31.512 StartZ=0 EndX=16.3251 EndY=34.4666 EndZ=0
    g1: ArcOfCircle CenterX=19 CenterY=19.2524 CenterZ=0 NormalX=0 NormalY=0 NormalZ=1 AngleXU=0 Radius=15.4476 StartAngle=1.74483 EndAngle=2.72717
    g2: ArcOfCircle CenterX=19 CenterY=19.2524 CenterZ=0 NormalX=0 NormalY=0 NormalZ=1 AngleXU=0 Radius=12.4476 StartAngle=1.74483 EndAngle=2.73189
    g3: LineSegment StartX=4.86004 StartY=25.4725 StartZ=0 EndX=7.58253 EndY=24.2107 EndZ=0
  constraints (7):
    c: Block(g0)
    c: Coincident(g1,g0)
    c: Coincident(g2,g0)
    c: Coincident(g3,g1)
    c: Coincident(g3,g2)
    c: Block(g1)
    c: Block(g2)
FEATURE [Part::Extrusion] Extrude010
  Base = -> Sketch011
  Dir = (0,0,1)
  DirMode = 2
  FaceMakerClass = Part::FaceMakerBullseye
  LengthFwd = 10.6
  LengthRev = 0
  Placement = pos=(0,0,31) rot=(0,0,1;0rad)
  Solid = true
  Symmetric = false
FEATURE [Part::Cylinder] Cylinder023
  Angle = 360
  AttacherType = Attacher::AttachEngine3D
  Height = 20
  Placement = pos=(0,0,36.15) rot=(0,0,1;0rad)
  Radius = 8.2
FEATURE [Part::MultiFuse] Fusion039  label="removeToCreteHoleForPlugHousing008"
  Placement = pos=(-42,19,36) rot=(0,1,0;1.5708rad)
  Shapes = -> [Cylinder023,Cylinder022]
FEATURE [Part::Cut] Cut012
  Base = -> Extrude010
  Placement = pos=(0,0,-0.3) rot=(0,0,1;0rad)
  Tool = -> Fusion039
FEATURE [Part::Cut] Cut013
  Base = -> Box010
  Tool = -> Cut012
FEATURE [Part::Fillet] Fillet014
  Base = -> Cut013
  Edges = 1 edges r=0.7: [Edge13]
FEATURE [Part::Fillet] Fillet015
  Base = -> Fillet014
  Edges = 1 edges r=0.7: [Edge13]
FEATURE [Part::Fillet] Fillet016
  Base = -> Fillet015
  Edges = 1 edges r=0.7: [Edge16]
FEATURE [Part::Fillet] Fillet017
  Base = -> Fillet016
  Edges = 1 edges r=0.7: [Edge11]
FEATURE [Part::Fillet] Fillet018
  Base = -> Fillet017
  Edges = 1 edges r=0.7: [Edge10]
FEATURE [Part::Fillet] Fillet019
  Base = -> Fillet018
  Edges = 1 edges r=1.2: [Edge5]
FEATURE [Part::Fillet] Fillet020
  Base = -> Fillet019
  Edges = 1 edges r=1.2: [Edge12]
FEATURE [Part::Fillet] Fillet021
  Base = -> Fillet020
  Edges = 1 edges r=2: [Edge1]
  Placement = pos=(0.3,0,0) rot=(0,0,1;0rad)
FEATURE [Part::MultiFuse] Fusion040  label="top005"
  Shapes = -> [Cut008,Fillet021]
FEATURE [Part::MultiFuse] Fusion041  label="wireHolder"
  Shapes = -> [Fusion033,Fillet013]
FEATURE [Part::MultiFuse] Fusion042
  Shapes = -> [Fillet007,Fusion041]
FEATURE [Part::MultiFuse] Fusion043  label="wireHolder001"
  Shapes = -> [Fusion042,Fillet010]
FEATURE [Part::MultiFuse] Fusion044  label="wireHolder002"
  Shapes = -> [Fillet006,Fusion037,Fusion043]
FEATURE [Part::Feature] Face026
  shape: bbox 11 x 6 x 2e-07 mm, 1 faces, 0 solids (baked)
FEATURE [Part::Revolution] Revolve026
  Angle = 360
  Axis = (0,1,0)
  Base = (0,0,0)
  FaceMakerClass = Part::FaceMakerBullseye
  Placement = pos=(30.3,-1,19.7) rot=(0,0,1;0rad)
  Solid = false
  Source = -> Face026
  Symmetric = false
FEATURE [Sketcher::SketchObject] Sketch013  label="topSketch006"
  FullyConstrained = true
  sketch-geometry (13):
    g0: LineSegment StartX=117 StartY=19 StartZ=0 EndX=117 EndY=38 EndZ=0
    g1: ArcOfCircle CenterX=98 CenterY=19 CenterZ=0 NormalX=0 NormalY=0 NormalZ=1 AngleXU=0 Radius=19 StartAngle=5.7297 EndAngle=6.28319
    g2: LineSegment StartX=0 StartY=3 StartZ=0 EndX=0 EndY=19 EndZ=0
    g3: LineSegment StartX=19 StartY=38 StartZ=0 EndX=117 EndY=38 EndZ=0
    g4: ArcOfCircle CenterX=19 CenterY=19 CenterZ=0 NormalX=0 NormalY=0 NormalZ=1 AngleXU=0 Radius=19 StartAngle=1.5708 EndAngle=3.14159
    g5: ArcOfCircle CenterX=19 CenterY=19 CenterZ=0 NormalX=0 NormalY=0 NormalZ=1 AngleXU=0 Radius=16 StartAngle=1.5708 EndAngle=3.14159
    g6: ArcOfCircle CenterX=98 CenterY=19 CenterZ=0 NormalX=0 NormalY=0 NormalZ=1 AngleXU=0 Radius=16 StartAngle=5.60905 EndAngle=6.28319
    g7: LineSegment StartX=114 StartY=19 StartZ=0 EndX=114 EndY=35 EndZ=0
    g8: LineSegment StartX=110.5 StartY=9.01251 StartZ=0 EndX=114.163 EndY=9.01251 EndZ=0
    g9: LineSegment StartX=114 StartY=35 StartZ=0 EndX=19 EndY=35 EndZ=0
    g10: LineSegment StartX=0 StartY=3 StartZ=0 EndX=0 EndY=0 EndZ=0
    g11: LineSegment StartX=3 StartY=0 StartZ=0 EndX=0 EndY=0 EndZ=0
    g12: LineSegment StartX=3 StartY=19 StartZ=0 EndX=3 EndY=0 EndZ=0
  constraints (33):
    c: Vertical(g0)
    c: Distance(g0) = 19
    c: Block(g0)
    c: Coincident(g1,g0)
    c: Block(g1)
    c: Vertical(g2)
    c: Block(g2)
    c: Coincident(g3,g0)
    c: Horizontal(g3)
    c: Distance(g3) = 98
    c: Coincident(g4,g3)
    c: Coincident(g4,g2)
    c: Block(g4)
    c: Coincident(g5,g4)
    c: Coincident(g6,g1)
    c: Block(g6)
    c: Block(g5)
    c: Coincident(g7,g6)
    c: Vertical(g7)
    c: Coincident(g8,g6)
    c: Coincident(g8,g1)
    c: Coincident(g9,g7)
    c: Coincident(g9,g5)
    c: Horizontal(g9)
    c: Tangent(g9,g5)
    c: Coincident(g10,g2)
    c: Distance(g10) = 3
    c: Vertical(g10)
    c: Coincident(g11,g10)
    c: Horizontal(g11)
    c: Coincident(g12,g5)
    c: Coincident(g12,g11)
    c: Vertical(g12)
FEATURE [Part::Extrusion] Extrude011  label="top006"
  Base = -> Sketch013
  Dir = (0,0,1)
  DirMode = 2
  FaceMakerClass = Part::FaceMakerBullseye
  LengthFwd = 72
  LengthRev = 0
  Solid = true
  Symmetric = false
FEATURE [Sketcher::SketchObject] Sketch014
  FullyConstrained = true
  MapMode = 3
  Placement = pos=(0,0,0) rot=(1,0,0;1.5708rad)
  Support = -> [Extrude011]
  sketch-geometry (8):
    g0: Circle CenterX=80.351 CenterY=-67.6202 CenterZ=0 NormalX=0 NormalY=0 NormalZ=1 AngleXU=0 Radius=2
    g1: Circle CenterX=80.351 CenterY=-67.6202 CenterZ=0 NormalX=0 NormalY=0 NormalZ=1 AngleXU=0 Radius=3
    g2: Circle CenterX=80.351 CenterY=-4.92017 CenterZ=0 NormalX=0 NormalY=0 NormalZ=1 AngleXU=0 Radius=2
    g3: Circle CenterX=80.351 CenterY=-4.92017 CenterZ=0 NormalX=0 NormalY=0 NormalZ=1 AngleXU=0 Radius=3
    g4: Circle CenterX=23.851 CenterY=-4.92017 CenterZ=0 NormalX=0 NormalY=0 NormalZ=1 AngleXU=0 Radius=2
    g5: Circle CenterX=23.851 CenterY=-4.92017 CenterZ=0 NormalX=0 NormalY=0 NormalZ=1 AngleXU=0 Radius=3
    g6: Circle CenterX=23.851 CenterY=-67.6202 CenterZ=0 NormalX=0 NormalY=0 NormalZ=1 AngleXU=0 Radius=2
    g7: Circle CenterX=23.851 CenterY=-67.6202 CenterZ=0 NormalX=0 NormalY=0 NormalZ=1 AngleXU=0 Radius=3
  constraints (8):
    c: Block(g3)
    c: Block(g2)
    c: Block(g1)
    c: Block(g0)
    c: Block(g6)
    c: Block(g7)
    c: Block(g4)
    c: Block(g5)
FEATURE [Part::Feature] Face027
  shape: bbox 11 x 6 x 2e-07 mm, 1 faces, 0 solids (baked)
FEATURE [Part::Revolution] Revolve027
  Angle = 360
  Axis = (0,1,0)
  Base = (0,0,0)
  FaceMakerClass = Part::FaceMakerBullseye
  Placement = pos=(30.3,-1,51.7) rot=(0,0,1;0rad)
  Solid = false
  Source = -> Face027
  Symmetric = false
FEATURE [Part::Feature] Face028
  shape: bbox 11 x 6 x 2e-07 mm, 1 faces, 0 solids (baked)
FEATURE [Part::Revolution] Revolve028
  Angle = 360
  Axis = (0,1,0)
  Base = (0,0,0)
  FaceMakerClass = Part::FaceMakerBullseye
  Placement = pos=(62.3,-1,19.7) rot=(0,0,1;0rad)
  Solid = false
  Source = -> Face028
  Symmetric = false
FEATURE [Part::Feature] Face029
  shape: bbox 11 x 6 x 2e-07 mm, 1 faces, 0 solids (baked)
FEATURE [Part::Revolution] Revolve029
  Angle = 360
  Axis = (0,1,0)
  Base = (0,0,0)
  FaceMakerClass = Part::FaceMakerBullseye
  Placement = pos=(62.3,-1,51.7) rot=(0,0,1;0rad)
  Solid = false
  Source = -> Face029
  Symmetric = false
FEATURE [Part::Feature] Wire
  shape: bbox 11 x 5.2 x 2e-07 mm, 0 faces, 0 solids (baked)
FEATURE [Part::Revolution] Revolve030
  Angle = 360
  Axis = (0,1,0)
  Base = (0,0,0)
  FaceMakerClass = Part::FaceMakerBullseye
  Placement = pos=(30.3,38,19.7) rot=(0,0,1;0rad)
  Solid = true
  Source = -> Wire
  Symmetric = false
FEATURE [Part::Feature] Wire001
  shape: bbox 11 x 5.2 x 2e-07 mm, 0 faces, 0 solids (baked)
FEATURE [Part::Revolution] Revolve031
  Angle = 360
  Axis = (0,1,0)
  Base = (0,0,0)
  FaceMakerClass = Part::FaceMakerBullseye
  Placement = pos=(30.3,38,51.7) rot=(0,0,1;0rad)
  Solid = true
  Source = -> Wire001
  Symmetric = false
FEATURE [Part::Feature] Wire002
  shape: bbox 11 x 5.2 x 2e-07 mm, 0 faces, 0 solids (baked)
FEATURE [Part::Revolution] Revolve032
  Angle = 360
  Axis = (0,1,0)
  Base = (0,0,0)
  FaceMakerClass = Part::FaceMakerBullseye
  Placement = pos=(62.3,38,51.7) rot=(0,0,1;0rad)
  Solid = true
  Source = -> Wire002
  Symmetric = false
FEATURE [Part::Feature] Wire003
  shape: bbox 11 x 5.2 x 2e-07 mm, 0 faces, 0 solids (baked)
FEATURE [Part::Revolution] Revolve033
  Angle = 360
  Axis = (0,1,0)
  Base = (0,0,0)
  FaceMakerClass = Part::FaceMakerBullseye
  Placement = pos=(62.3,38,19.7) rot=(0,0,1;0rad)
  Solid = true
  Source = -> Wire003
  Symmetric = false
FEATURE [Part::MultiFuse] Fusion045  label="altRandScrewHousing"
  Shapes = -> [Revolve029,Revolve027,Revolve028,Revolve026]
FEATURE [Part::MultiFuse] Fusion046  label="fanScrewHousing"
  Shapes = -> [Revolve033,Revolve032,Revolve031,Revolve030]
FEATURE [Sketcher::SketchObject] Sketch015
  FullyConstrained = true
  sketch-geometry (17):
    g0: Circle CenterX=-3.5 CenterY=23.5 CenterZ=0 NormalX=0 NormalY=0 NormalZ=1 AngleXU=0 Radius=1
    g1: Circle CenterX=-1 CenterY=15.25 CenterZ=0 NormalX=0 NormalY=0 NormalZ=1 AngleXU=0 Radius=1
    g2: Circle CenterX=-3.5 CenterY=7 CenterZ=0 NormalX=0 NormalY=0 NormalZ=1 AngleXU=0 Radius=1
    g3: BSplineCurve PolesCount=3 KnotsCount=2 Degree=2 IsPeriodic=0
    g4: GeomPoint X=-3.5 Y=23.5 Z=0
    g5: GeomPoint X=-3.5 Y=7 Z=0
    g6: Circle CenterX=-4.8 CenterY=30.5 CenterZ=0 NormalX=0 NormalY=0 NormalZ=1 AngleXU=0 Radius=1
    g7: Circle CenterX=-3.5 CenterY=30.5 CenterZ=0 NormalX=0 NormalY=0 NormalZ=1 AngleXU=0 Radius=1
    g8: Circle CenterX=-3.5 CenterY=29.2 CenterZ=0 NormalX=0 NormalY=0 NormalZ=1 AngleXU=0 Radius=1
    g9: BSplineCurve PolesCount=3 KnotsCount=2 Degree=2 IsPeriodic=0
    g10: GeomPoint X=-4.8 Y=30.5 Z=0
    g11: GeomPoint X=-3.5 Y=29.2 Z=0
    g12: LineSegment StartX=-3.5 StartY=29.2 StartZ=0 EndX=-3.5 EndY=23.5 EndZ=0
    g13: LineSegment StartX=-4.8 StartY=30.5 StartZ=0 EndX=0 EndY=30.5 EndZ=0
    g14: LineSegment StartX=-3.5 StartY=0.3 StartZ=0 EndX=0 EndY=0.3 EndZ=0
    g15: LineSegment StartX=-3.5 StartY=0.3 StartZ=0 EndX=-3.5 EndY=7 EndZ=0
    g16: LineSegment StartX=0 StartY=0.3 StartZ=0 EndX=0 EndY=30.5 EndZ=0
  constraints (34):
    c: Weight(g0) = 1
    c: Equal(g0,g1)
    c: Equal(g0,g2)
    c: InternalAlignment(g0,g3)
    c: InternalAlignment(g1,g3)
    c: InternalAlignment(g2,g3)
    c: InternalAlignment(g4,g3)
    c: InternalAlignment(g5,g3)
    c: Block(g3)
    c: Weight(g6) = 1
    c: Equal(g6,g7)
    c: Equal(g6,g8)
    c: InternalAlignment(g6,g9)
    c: InternalAlignment(g7,g9)
    c: InternalAlignment(g8,g9)
    c: InternalAlignment(g10,g9)
    c: InternalAlignment(g11,g9)
    c: Block(g9)
    c: Coincident(g12,g9)
    c: Coincident(g12,g3)
    c: Vertical(g12)
    c: Coincident(g13,g9)
    c: Horizontal(g13)
    c: Distance(g13) = 4.8
    c: Horizontal(g14)
    c: Block(g14)
    c: Coincident(g15,g14)
    c: Coincident(g15,g3)
    c: Vertical(g15)
    c: Coincident(g16,g14)
    c: Coincident(g16,g13)
    c: Vertical(g16)
    c: Tangent(g16,g1)
    c: Distance(g14) = 3.5
FEATURE [Sketcher::SketchObject] Sketch016
  FullyConstrained = true
  sketch-geometry (16):
    g0: Circle CenterX=-3.5 CenterY=23.5 CenterZ=0 NormalX=0 NormalY=0 NormalZ=1 AngleXU=0 Radius=1
    g1: Circle CenterX=-1 CenterY=15.25 CenterZ=0 NormalX=0 NormalY=0 NormalZ=1 AngleXU=0 Radius=1
    g2: Circle CenterX=-3.5 CenterY=7 CenterZ=0 NormalX=0 NormalY=0 NormalZ=1 AngleXU=0 Radius=1
    g3: BSplineCurve PolesCount=3 KnotsCount=2 Degree=2 IsPeriodic=0
    g4: GeomPoint X=-3.5 Y=23.5 Z=0
    g5: GeomPoint X=-3.5 Y=7 Z=0
    g6: LineSegment StartX=-3.5 StartY=28.2 StartZ=0 EndX=-3.5 EndY=23.5 EndZ=0
    g7: LineSegment StartX=0 StartY=29.5 StartZ=0 EndX=0 EndY=30 EndZ=0
    g8: LineSegment StartX=-3.5 StartY=28.2 StartZ=0 EndX=-3.5 EndY=30 EndZ=0
    g9: LineSegment StartX=0 StartY=30 StartZ=0 EndX=0 EndY=30.5 EndZ=0
    g10: LineSegment StartX=0 StartY=30.5 StartZ=0 EndX=-3.5 EndY=30.5 EndZ=0
    g11: LineSegment StartX=-3.5 StartY=30.5 StartZ=0 EndX=-3.5 EndY=30 EndZ=0
    g12: LineSegment StartX=0 StartY=29.5 StartZ=0 EndX=0 EndY=5 EndZ=0
    g13: LineSegment StartX=-3.5 StartY=0.3 StartZ=0 EndX=-3.5 EndY=7 EndZ=0
    g14: LineSegment StartX=-3.5 StartY=0.3 StartZ=0 EndX=0 EndY=0.3 EndZ=0
    g15: LineSegment StartX=0 StartY=5 StartZ=0 EndX=0 EndY=0.3 EndZ=0
  constraints (39):
    c: Weight(g0) = 1
    c: Equal(g0,g1)
    c: Equal(g0,g2)
    c: InternalAlignment(g0,g3)
    c: InternalAlignment(g1,g3)
    c: InternalAlignment(g2,g3)
    c: InternalAlignment(g4,g3)
    c: InternalAlignment(g5,g3)
    c: Block(g3)
    c: Coincident(g6,g3)
    c: Vertical(g6)
    c: Vertical(g7)
    c: Distance(g7) = 0.5
    c: Coincident(g8,g6)
    c: Vertical(g8)
    c: Block(g6)
    c: Block(g7)
    c: Vertical(g9)
    c: Equal(g7,g9) = 0.5
    c: Block(g9)
    c: Coincident(g9,g7)
    c: Horizontal(g10)
    c: Coincident(g10,g9)
    c: Coincident(g11,g10)
    c: Coincident(g11,g8)
    c: Vertical(g11)
    c: Block(g11)
    c: Coincident(g12,g7)
    c: Vertical(g12)
    c: Coincident(g13,g3)
    c: Vertical(g13)
    c: Distance(g13) = 6.7
    c: Coincident(g14,g13)
    c: Horizontal(g14)
    c: Block(g14)
    c: Coincident(g15,g12)
    c: Coincident(g15,g14)
    c: Vertical(g15)
    c: Block(g15)
FEATURE [Sketcher::SketchObject] Sketch017
  FullyConstrained = true
  sketch-geometry (11):
    g0: LineSegment StartX=-3.5 StartY=1e-16 StartZ=0 EndX=-1.6 EndY=1e-16 EndZ=0
    g1: LineSegment StartX=-1.6 StartY=1e-16 StartZ=0 EndX=-1.6 EndY=1.5 EndZ=0
    g2: LineSegment StartX=-3.5 StartY=1.5 StartZ=0 EndX=-1.6 EndY=1.5 EndZ=0
    g3: LineSegment StartX=-3.5 StartY=1e-16 StartZ=0 EndX=-4.8 EndY=1e-16 EndZ=0
    g4: Circle CenterX=-3.5 CenterY=1.3 CenterZ=0 NormalX=0 NormalY=0 NormalZ=1 AngleXU=0 Radius=1
    g5: Circle CenterX=-3.5 CenterY=1e-16 CenterZ=0 NormalX=0 NormalY=0 NormalZ=1 AngleXU=0 Radius=1
    g6: Circle CenterX=-4.8 CenterY=1e-16 CenterZ=0 NormalX=0 NormalY=0 NormalZ=1 AngleXU=0 Radius=1
    g7: BSplineCurve PolesCount=3 KnotsCount=2 Degree=2 IsPeriodic=0
    g8: GeomPoint X=-3.5 Y=1.3 Z=0
    g9: GeomPoint X=-4.8 Y=1e-16 Z=0
    g10: LineSegment StartX=-3.5 StartY=1.3 StartZ=0 EndX=-3.5 EndY=1.5 EndZ=0
  constraints (24):
    c: Horizontal(g0)
    c: Distance(g0) = 1.9
    c: Block(g0)
    c: Coincident(g1,g0)
    c: Vertical(g1)
    c: Coincident(g2,g1)
    c: Horizontal(g2)
    c: Coincident(g3,g0)
    c: Horizontal(g3)
    c: Distance(g3) = 1.3
    c: Weight(g4) = 1
    c: Equal(g4,g5)
    c: Coincident(g5,g0)
    c: Equal(g4,g6)
    c: Coincident(g7,g3)
    c: InternalAlignment(g4,g7)
    c: InternalAlignment(g5,g7)
    c: InternalAlignment(g6,g7)
    c: InternalAlignment(g8,g7)
    c: InternalAlignment(g9,g7)
    c: Coincident(g10,g7)
    c: Coincident(g10,g2)
    c: Vertical(g10)
    c: Block(g10)
FEATURE [Part::Feature] Face035
  shape: bbox 3.2 x 1.5 x 2e-07 mm, 1 faces, 0 solids (baked)
FEATURE [Part::Revolution] Revolve039  label="backCaseScrewRetainer"
  Angle = 360
  Axis = (0,1,0)
  Base = (0,0,0)
  FaceMakerClass = Part::FaceMakerBullseye
  Placement = pos=(12.5,3,62) rot=(0,0,1;0rad)
  Solid = false
  Source = -> Face035
  Symmetric = false
FEATURE [Part::Feature] Face036
  shape: bbox 3.2 x 1.5 x 2e-07 mm, 1 faces, 0 solids (baked)
FEATURE [Part::Feature] Face039
  shape: bbox 4.8 x 30.2 x 2e-07 mm, 1 faces, 0 solids (baked)
FEATURE [Part::Revolution] Revolve043  label="frontCaseScrewPost002"
  Angle = 360
  Axis = (0,1,0)
  Base = (0,0,0)
  FaceMakerClass = Part::FaceMakerBullseye
  Placement = pos=(89.5,4.5,3.5) rot=(0,0,1;0rad)
  Solid = false
  Source = -> Face039
  Symmetric = false
FEATURE [Part::Feature] Face042
  shape: bbox 4.8 x 30.2 x 2e-07 mm, 1 faces, 0 solids (baked)
FEATURE [Part::Revolution] Revolve046  label="frontCaseScrewPost003"
  Angle = 360
  Axis = (0,1,0)
  Base = (0,0,0)
  FaceMakerClass = Part::FaceMakerBullseye
  Placement = pos=(89.5,4.5,68.5) rot=(0,0,1;0rad)
  Solid = false
  Source = -> Face042
  Symmetric = false
FEATURE [Part::Feature] Face043
  shape: bbox 3.2 x 1.5 x 2e-07 mm, 1 faces, 0 solids (baked)
FEATURE [Part::Revolution] Revolve047  label="frontCaseScrewRetainer002"
  Angle = 360
  Axis = (0,1,0)
  Base = (0,0,0)
  FaceMakerClass = Part::FaceMakerBullseye
  Placement = pos=(89.5,3,68.5) rot=(0,0,1;0rad)
  Solid = false
  Source = -> Face043
  Symmetric = false
FEATURE [Part::Feature] Face044
  shape: bbox 3.2 x 1.5 x 2e-07 mm, 1 faces, 0 solids (baked)
FEATURE [Part::Revolution] Revolve048  label="frontCaseScrewRetainer003"
  Angle = 360
  Axis = (0,1,0)
  Base = (0,0,0)
  FaceMakerClass = Part::FaceMakerBullseye
  Placement = pos=(89.5,3,3.5) rot=(0,0,1;0rad)
  Solid = false
  Source = -> Face044
  Symmetric = false
FEATURE [App::MeasureDistance] Distance002  label="Distance: 1.67 mm"
  Distance = 1.66921
  P1 = (99.2361,4.7524,71.7)
  P2 = (99.2347,6.42161,71.7)
FEATURE [Sketcher::SketchObject] Sketch018
  FullyConstrained = true
  sketch-geometry (7):
    g0: LineSegment StartX=0 StartY=0 StartZ=0 EndX=0 EndY=6 EndZ=0
    g1: Circle CenterX=0 CenterY=0 CenterZ=0 NormalX=0 NormalY=0 NormalZ=1 AngleXU=0 Radius=1
    g2: Circle CenterX=8 CenterY=6 CenterZ=0 NormalX=0 NormalY=0 NormalZ=1 AngleXU=0 Radius=1
    g3: BSplineCurve PolesCount=3 KnotsCount=2 Degree=2 IsPeriodic=0
    g4: GeomPoint X=0 Y=0 Z=0
    g5: GeomPoint X=8 Y=6 Z=0
    g6: LineSegment StartX=0 StartY=6 StartZ=0 EndX=8 EndY=6 EndZ=0
  constraints (14):
    c: Coincident(g0,g-1)
    c: Distance(g0) = 6
    c: Vertical(g0)
    c: Coincident(g3,g0)
    c: Weight(g1) = 1
    c: Equal(g1,g2)
    c: InternalAlignment(g1,g3)
    c: InternalAlignment(g2,g3)
    c: InternalAlignment(g4,g3)
    c: InternalAlignment(g5,g3)
    c: Block(g3)
    c: Coincident(g6,g0)
    c: Coincident(g6,g3)
    c: Horizontal(g6)
FEATURE [Part::Extrusion] Extrude012  label="caseScrewPillarBracket"
  Base = -> Sketch018
  Dir = (0,0,1)
  DirMode = 2
  FaceMakerClass = Part::FaceMakerBullseye
  LengthFwd = 2.4
  LengthRev = 0
  Placement = pos=(15.76,29,8.8) rot=(0,1,0;0rad)
  Solid = true
  Symmetric = false
FEATURE [Sketcher::SketchObject] Sketch019
  FullyConstrained = true
  sketch-geometry (7):
    g0: LineSegment StartX=0 StartY=0 StartZ=0 EndX=0 EndY=6 EndZ=0
    g1: Circle CenterX=0 CenterY=0 CenterZ=0 NormalX=0 NormalY=0 NormalZ=1 AngleXU=0 Radius=1
    g2: Circle CenterX=8 CenterY=6 CenterZ=0 NormalX=0 NormalY=0 NormalZ=1 AngleXU=0 Radius=1
    g3: BSplineCurve PolesCount=3 KnotsCount=2 Degree=2 IsPeriodic=0
    g4: GeomPoint X=0 Y=0 Z=0
    g5: GeomPoint X=8 Y=6 Z=0
    g6: LineSegment StartX=0 StartY=6 StartZ=0 EndX=8 EndY=6 EndZ=0
  constraints (14):
    c: Coincident(g0,g-1)
    c: Distance(g0) = 6
    c: Vertical(g0)
    c: Coincident(g3,g0)
    c: Weight(g1) = 1
    c: Equal(g1,g2)
    c: InternalAlignment(g1,g3)
    c: InternalAlignment(g2,g3)
    c: InternalAlignment(g4,g3)
    c: InternalAlignment(g5,g3)
    c: Block(g3)
    c: Coincident(g6,g0)
    c: Coincident(g6,g3)
    c: Horizontal(g6)
FEATURE [Part::Extrusion] Extrude013  label="caseScrewPillarBracket001"
  Base = -> Sketch019
  Dir = (0,0,1)
  DirMode = 2
  FaceMakerClass = Part::FaceMakerBullseye
  LengthFwd = 2.4
  LengthRev = 0
  Placement = pos=(15.76,29,60.8) rot=(0,0,1;0rad)
  Solid = true
  Symmetric = false
FEATURE [Sketcher::SketchObject] Sketch020
  FullyConstrained = true
  sketch-geometry (7):
    g0: LineSegment StartX=0 StartY=0 StartZ=0 EndX=0 EndY=6 EndZ=0
    g1: Circle CenterX=0 CenterY=0 CenterZ=0 NormalX=0 NormalY=0 NormalZ=1 AngleXU=0 Radius=1
    g2: Circle CenterX=8 CenterY=6 CenterZ=0 NormalX=0 NormalY=0 NormalZ=1 AngleXU=0 Radius=1
    g3: BSplineCurve PolesCount=3 KnotsCount=2 Degree=2 IsPeriodic=0
    g4: GeomPoint X=0 Y=0 Z=0
    g5: GeomPoint X=8 Y=6 Z=0
    g6: LineSegment StartX=0 StartY=6 StartZ=0 EndX=8 EndY=6 EndZ=0
  constraints (14):
    c: Coincident(g0,g-1)
    c: Distance(g0) = 6
    c: Vertical(g0)
    c: Coincident(g3,g0)
    c: Weight(g1) = 1
    c: Equal(g1,g2)
    c: InternalAlignment(g1,g3)
    c: InternalAlignment(g2,g3)
    c: InternalAlignment(g4,g3)
    c: InternalAlignment(g5,g3)
    c: Block(g3)
    c: Coincident(g6,g0)
    c: Coincident(g6,g3)
    c: Horizontal(g6)
FEATURE [Part::Extrusion] Extrude014  label="caseScrewPillarBracket002"
  Base = -> Sketch020
  Dir = (0,0,1)
  DirMode = 2
  FaceMakerClass = Part::FaceMakerBullseye
  LengthFwd = 2.4
  LengthRev = 0
  Placement = pos=(13.7,29,13.26) rot=(0,-1,0;1.5708rad)
  Solid = true
  Symmetric = false
FEATURE [Sketcher::SketchObject] Sketch021
  FullyConstrained = true
  sketch-geometry (7):
    g0: LineSegment StartX=0 StartY=0 StartZ=0 EndX=0 EndY=6 EndZ=0
    g1: Circle CenterX=0 CenterY=0 CenterZ=0 NormalX=0 NormalY=0 NormalZ=1 AngleXU=0 Radius=1
    g2: Circle CenterX=8 CenterY=6 CenterZ=0 NormalX=0 NormalY=0 NormalZ=1 AngleXU=0 Radius=1
    g3: BSplineCurve PolesCount=3 KnotsCount=2 Degree=2 IsPeriodic=0
    g4: GeomPoint X=0 Y=0 Z=0
    g5: GeomPoint X=8 Y=6 Z=0
    g6: LineSegment StartX=0 StartY=6 StartZ=0 EndX=8 EndY=6 EndZ=0
  constraints (14):
    c: Coincident(g0,g-1)
    c: Distance(g0) = 6
    c: Vertical(g0)
    c: Coincident(g3,g0)
    c: Weight(g1) = 1
    c: Equal(g1,g2)
    c: InternalAlignment(g1,g3)
    c: InternalAlignment(g2,g3)
    c: InternalAlignment(g4,g3)
    c: InternalAlignment(g5,g3)
    c: Block(g3)
    c: Coincident(g6,g0)
    c: Coincident(g6,g3)
    c: Horizontal(g6)
FEATURE [Part::Extrusion] Extrude015  label="caseScrewPillarBracket003"
  Base = -> Sketch021
  Dir = (0,0,1)
  DirMode = 2
  FaceMakerClass = Part::FaceMakerBullseye
  LengthFwd = 2.4
  LengthRev = 0
  Placement = pos=(11.3,29,58.74) rot=(0,1,0;1.5708rad)
  Solid = true
  Symmetric = false
FEATURE [Sketcher::SketchObject] Sketch022
  FullyConstrained = true
  sketch-geometry (7):
    g0: LineSegment StartX=0 StartY=0 StartZ=0 EndX=0 EndY=6 EndZ=0
    g1: Circle CenterX=0 CenterY=0 CenterZ=0 NormalX=0 NormalY=0 NormalZ=1 AngleXU=0 Radius=1
    g2: Circle CenterX=8 CenterY=6 CenterZ=0 NormalX=0 NormalY=0 NormalZ=1 AngleXU=0 Radius=1
    g3: BSplineCurve PolesCount=3 KnotsCount=2 Degree=2 IsPeriodic=0
    g4: GeomPoint X=0 Y=0 Z=0
    g5: GeomPoint X=8 Y=6 Z=0
    g6: LineSegment StartX=0 StartY=6 StartZ=0 EndX=8 EndY=6 EndZ=0
  constraints (14):
    c: Coincident(g0,g-1)
    c: Distance(g0) = 6
    c: Vertical(g0)
    c: Coincident(g3,g0)
    c: Weight(g1) = 1
    c: Equal(g1,g2)
    c: InternalAlignment(g1,g3)
    c: InternalAlignment(g2,g3)
    c: InternalAlignment(g4,g3)
    c: InternalAlignment(g5,g3)
    c: Block(g3)
    c: Coincident(g6,g0)
    c: Coincident(g6,g3)
    c: Horizontal(g6)
FEATURE [Part::Extrusion] Extrude016  label="caseScrewPillarBracket004"
  Base = -> Sketch022
  Dir = (0,0,1)
  DirMode = 2
  FaceMakerClass = Part::FaceMakerBullseye
  LengthFwd = 2.4
  LengthRev = 0
  Placement = pos=(88.3,29,65.23) rot=(0,1,0;1.5708rad)
  Solid = true
  Symmetric = false
FEATURE [Sketcher::SketchObject] Sketch023
  FullyConstrained = true
  sketch-geometry (7):
    g0: LineSegment StartX=0 StartY=0 StartZ=0 EndX=0 EndY=6 EndZ=0
    g1: Circle CenterX=0 CenterY=0 CenterZ=0 NormalX=0 NormalY=0 NormalZ=1 AngleXU=0 Radius=1
    g2: Circle CenterX=8 CenterY=6 CenterZ=0 NormalX=0 NormalY=0 NormalZ=1 AngleXU=0 Radius=1
    g3: BSplineCurve PolesCount=3 KnotsCount=2 Degree=2 IsPeriodic=0
    g4: GeomPoint X=0 Y=0 Z=0
    g5: GeomPoint X=8 Y=6 Z=0
    g6: LineSegment StartX=0 StartY=6 StartZ=0 EndX=8 EndY=6 EndZ=0
  constraints (14):
    c: Coincident(g0,g-1)
    c: Distance(g0) = 6
    c: Vertical(g0)
    c: Coincident(g3,g0)
    c: Weight(g1) = 1
    c: Equal(g1,g2)
    c: InternalAlignment(g1,g3)
    c: InternalAlignment(g2,g3)
    c: InternalAlignment(g4,g3)
    c: InternalAlignment(g5,g3)
    c: Block(g3)
    c: Coincident(g6,g0)
    c: Coincident(g6,g3)
    c: Horizontal(g6)
FEATURE [Part::Extrusion] Extrude017  label="caseScrewPillarBracket005"
  Base = -> Sketch023
  Dir = (0,0,1)
  DirMode = 2
  FaceMakerClass = Part::FaceMakerBullseye
  LengthFwd = 2.4
  LengthRev = 0
  Placement = pos=(90.7,29,6.77) rot=(0,-1,0;1.5708rad)
  Solid = true
  Symmetric = false
FEATURE [Sketcher::SketchObject] Sketch024
  FullyConstrained = true
  sketch-geometry (7):
    g0: LineSegment StartX=0 StartY=0 StartZ=0 EndX=0 EndY=6 EndZ=0
    g1: Circle CenterX=0 CenterY=0 CenterZ=0 NormalX=0 NormalY=0 NormalZ=1 AngleXU=0 Radius=1
    g2: Circle CenterX=8 CenterY=6 CenterZ=0 NormalX=0 NormalY=0 NormalZ=1 AngleXU=0 Radius=1
    g3: BSplineCurve PolesCount=3 KnotsCount=2 Degree=2 IsPeriodic=0
    g4: GeomPoint X=0 Y=0 Z=0
    g5: GeomPoint X=8 Y=6 Z=0
    g6: LineSegment StartX=0 StartY=6 StartZ=0 EndX=8 EndY=6 EndZ=0
  constraints (14):
    c: Coincident(g0,g-1)
    c: Distance(g0) = 6
    c: Vertical(g0)
    c: Coincident(g3,g0)
    c: Weight(g1) = 1
    c: Equal(g1,g2)
    c: InternalAlignment(g1,g3)
    c: InternalAlignment(g2,g3)
    c: InternalAlignment(g4,g3)
    c: InternalAlignment(g5,g3)
    c: Block(g3)
    c: Coincident(g6,g0)
    c: Coincident(g6,g3)
    c: Horizontal(g6)
FEATURE [Part::Extrusion] Extrude018  label="caseScrewPillarBracket006"
  Base = -> Sketch024
  Dir = (0,0,1)
  DirMode = 2
  FaceMakerClass = Part::FaceMakerBullseye
  LengthFwd = 2.4
  LengthRev = 0
  Placement = pos=(103.7,29,6.77) rot=(0,-1,0;1.5708rad)
  Solid = true
  Symmetric = false
FEATURE [Sketcher::SketchObject] Sketch025
  FullyConstrained = true
  sketch-geometry (7):
    g0: LineSegment StartX=0 StartY=0 StartZ=0 EndX=0 EndY=6 EndZ=0
    g1: Circle CenterX=0 CenterY=0 CenterZ=0 NormalX=0 NormalY=0 NormalZ=1 AngleXU=0 Radius=1
    g2: Circle CenterX=8 CenterY=6 CenterZ=0 NormalX=0 NormalY=0 NormalZ=1 AngleXU=0 Radius=1
    g3: BSplineCurve PolesCount=3 KnotsCount=2 Degree=2 IsPeriodic=0
    g4: GeomPoint X=0 Y=0 Z=0
    g5: GeomPoint X=8 Y=6 Z=0
    g6: LineSegment StartX=0 StartY=6 StartZ=0 EndX=8 EndY=6 EndZ=0
  constraints (14):
    c: Coincident(g0,g-1)
    c: Distance(g0) = 6
    c: Vertical(g0)
    c: Coincident(g3,g0)
    c: Weight(g1) = 1
    c: Equal(g1,g2)
    c: InternalAlignment(g1,g3)
    c: InternalAlignment(g2,g3)
    c: InternalAlignment(g4,g3)
    c: InternalAlignment(g5,g3)
    c: Block(g3)
    c: Coincident(g6,g0)
    c: Coincident(g6,g3)
    c: Horizontal(g6)
FEATURE [Part::Extrusion] Extrude019  label="caseScrewPillarBracket007"
  Base = -> Sketch025
  Dir = (0,0,1)
  DirMode = 2
  FaceMakerClass = Part::FaceMakerBullseye
  LengthFwd = 2.4
  LengthRev = 0
  Placement = pos=(101.3,29,65.23) rot=(0,1,0;1.5708rad)
  Solid = true
  Symmetric = false
FEATURE [Part::Box] Box011  label="frontCaseScrewPillarBracket"
  AttacherType = Attacher::AttachEngine3D
  Height = 2.4
  Length = 16
  Placement = pos=(87,28,2.3) rot=(0,0,1;0rad)
  Width = 7
FEATURE [Part::Box] Box012  label="frontCaseScrewPillarBracket001"
  AttacherType = Attacher::AttachEngine3D
  Height = 2.4
  Length = 16
  Placement = pos=(87,28,67.3) rot=(0,0,1;0rad)
  Width = 7
FEATURE [Sketcher::SketchObject] Sketch026
  FullyConstrained = true
  sketch-geometry (17):
    g0: Circle CenterX=-3.5 CenterY=23.5 CenterZ=0 NormalX=0 NormalY=0 NormalZ=1 AngleXU=0 Radius=1
    g1: Circle CenterX=-1 CenterY=15.25 CenterZ=0 NormalX=0 NormalY=0 NormalZ=1 AngleXU=0 Radius=1
    g2: Circle CenterX=-3.5 CenterY=7 CenterZ=0 NormalX=0 NormalY=0 NormalZ=1 AngleXU=0 Radius=1
    g3: BSplineCurve PolesCount=3 KnotsCount=2 Degree=2 IsPeriodic=0
    g4: GeomPoint X=-3.5 Y=23.5 Z=0
    g5: GeomPoint X=-3.5 Y=7 Z=0
    g6: Circle CenterX=-4.8 CenterY=30.5 CenterZ=0 NormalX=0 NormalY=0 NormalZ=1 AngleXU=0 Radius=1
    g7: Circle CenterX=-3.5 CenterY=30.5 CenterZ=0 NormalX=0 NormalY=0 NormalZ=1 AngleXU=0 Radius=1
    g8: Circle CenterX=-3.5 CenterY=29.2 CenterZ=0 NormalX=0 NormalY=0 NormalZ=1 AngleXU=0 Radius=1
    g9: BSplineCurve PolesCount=3 KnotsCount=2 Degree=2 IsPeriodic=0
    g10: GeomPoint X=-4.8 Y=30.5 Z=0
    g11: GeomPoint X=-3.5 Y=29.2 Z=0
    g12: LineSegment StartX=-3.5 StartY=29.2 StartZ=0 EndX=-3.5 EndY=23.5 EndZ=0
    g13: LineSegment StartX=-4.8 StartY=30.5 StartZ=0 EndX=0 EndY=30.5 EndZ=0
    g14: LineSegment StartX=-3.5 StartY=5 StartZ=0 EndX=-3.5 EndY=7 EndZ=0
    g15: LineSegment StartX=0 StartY=5 StartZ=0 EndX=0 EndY=30.5 EndZ=0
    g16: LineSegment StartX=-3.5 StartY=5 StartZ=0 EndX=0 EndY=5 EndZ=0
  constraints (33):
    c: Weight(g0) = 1
    c: Equal(g0,g1)
    c: Equal(g0,g2)
    c: InternalAlignment(g0,g3)
    c: InternalAlignment(g1,g3)
    c: InternalAlignment(g2,g3)
    c: InternalAlignment(g4,g3)
    c: InternalAlignment(g5,g3)
    c: Block(g3)
    c: Weight(g6) = 1
    c: Equal(g6,g7)
    c: Equal(g6,g8)
    c: InternalAlignment(g6,g9)
    c: InternalAlignment(g7,g9)
    c: InternalAlignment(g8,g9)
    c: InternalAlignment(g10,g9)
    c: InternalAlignment(g11,g9)
    c: Block(g9)
    c: Coincident(g12,g9)
    c: Coincident(g12,g3)
    c: Vertical(g12)
    c: Coincident(g13,g9)
    c: Horizontal(g13)
    c: Distance(g13) = 4.8
    c: Coincident(g14,g3)
    c: Vertical(g14)
    c: Coincident(g15,g13)
    c: Vertical(g15)
    c: Tangent(g15,g1)
    c: Distance(g14) = 2
    c: Coincident(g16,g14)
    c: Horizontal(g16)
    c: Coincident(g15,g16)
FEATURE [Part::Feature] Face050
  shape: bbox 4.8 x 25.5 x 2e-07 mm, 1 faces, 0 solids (baked)
FEATURE [Part::Revolution] Revolve054  label="moreFrontCaseScrewPost001"
  Angle = 360
  Axis = (0,1,0)
  Base = (0,0,0)
  FaceMakerClass = Part::FaceMakerBullseye
  Placement = pos=(102.5,4.5,3.5) rot=(0,0,1;0rad)
  Solid = false
  Source = -> Face050
  Symmetric = false
FEATURE [Part::Feature] Face051
  shape: bbox 4.8 x 25.5 x 2e-07 mm, 1 faces, 0 solids (baked)
FEATURE [Part::Revolution] Revolve055  label="moreFrontCaseScrewPost002"
  Angle = 360
  Axis = (0,1,0)
  Base = (0,0,0)
  FaceMakerClass = Part::FaceMakerBullseye
  Placement = pos=(102.5,4.5,68.5) rot=(0,0,1;0rad)
  Solid = false
  Source = -> Face051
  Symmetric = false
FEATURE [Sketcher::SketchObject] Sketch027
  FullyConstrained = true
  sketch-geometry (10):
    g0: LineSegment StartX=-1.6 StartY=4.7 StartZ=0 EndX=-1.6 EndY=1.7 EndZ=0
    g1: LineSegment StartX=-3.5 StartY=4.7 StartZ=0 EndX=-1.6 EndY=4.7 EndZ=0
    g2: LineSegment StartX=-1.6 StartY=1.7 StartZ=0 EndX=-1.6 EndY=1.5 EndZ=0
    g3: LineSegment StartX=-1.6 StartY=1.5 StartZ=0 EndX=-5.2 EndY=1.5 EndZ=0
    g4: Circle CenterX=-3.5 CenterY=4.7 CenterZ=0 NormalX=0 NormalY=0 NormalZ=1 AngleXU=0 Radius=1
    g5: Circle CenterX=-3.59627 CenterY=2.99743 CenterZ=0 NormalX=0 NormalY=0 NormalZ=1 AngleXU=0 Radius=1
    g6: Circle CenterX=-5.2 CenterY=1.5 CenterZ=0 NormalX=0 NormalY=0 NormalZ=1 AngleXU=0 Radius=1
    g7: BSplineCurve PolesCount=3 KnotsCount=2 Degree=2 IsPeriodic=0
    g8: GeomPoint X=-3.5 Y=4.7 Z=0
    g9: GeomPoint X=-5.2 Y=1.5 Z=0
  constraints (23):
    c: Vertical(g0)
    c: Distance(g0) = 3
    c: Coincident(g1,g0)
    c: Horizontal(g1)
    c: Block(g0)
    c: Block(g1)
    c: Coincident(g2,g0)
    c: Vertical(g2)
    c: Distance(g2) = 0.2
    c: Coincident(g3,g2)
    c: Horizontal(g3)
    c: Block(g3)
    c: Coincident(g7,g1)
    c: Weight(g4) = 1
    c: Equal(g4,g5)
    c: Equal(g4,g6)
    c: Coincident(g7,g3)
    c: InternalAlignment(g4,g7)
    c: InternalAlignment(g5,g7)
    c: InternalAlignment(g6,g7)
    c: InternalAlignment(g8,g7)
    c: InternalAlignment(g9,g7)
    c: Block(g7)
FEATURE [Sketcher::SketchObject] Sketch028
  FullyConstrained = true
  sketch-geometry (18):
    g0: LineSegment StartX=0 StartY=3e-16 StartZ=0 EndX=0 EndY=1.7 EndZ=0
    g1: LineSegment StartX=-3.5 StartY=0 StartZ=0 EndX=-3.5 EndY=0.9 EndZ=0
    g2: Circle CenterX=-2.7 CenterY=1.7 CenterZ=0 NormalX=0 NormalY=0 NormalZ=1 AngleXU=0 Radius=1
    g3: Circle CenterX=-3.5 CenterY=1.7 CenterZ=0 NormalX=0 NormalY=0 NormalZ=1 AngleXU=0 Radius=1
    g4: Circle CenterX=-3.5 CenterY=0.9 CenterZ=0 NormalX=0 NormalY=0 NormalZ=1 AngleXU=0 Radius=1
    g5: BSplineCurve PolesCount=3 KnotsCount=2 Degree=2 IsPeriodic=0
    g6: GeomPoint X=-2.7 Y=1.7 Z=0
    g7: GeomPoint X=-3.5 Y=0.9 Z=0
    g8: LineSegment StartX=-3.5 StartY=0 StartZ=0 EndX=-3.5 EndY=-7 EndZ=0
    g9: LineSegment StartX=0 StartY=3e-16 StartZ=0 EndX=0 EndY=-7 EndZ=0
    g10: LineSegment StartX=-3.5 StartY=-7 StartZ=0 EndX=0 EndY=-7 EndZ=0
    g11: LineSegment StartX=-2.7 StartY=1.7 StartZ=0 EndX=-1.6 EndY=1.7 EndZ=0
    g12: LineSegment StartX=0 StartY=1.7 StartZ=0 EndX=0 EndY=4.5 EndZ=0
    g13: LineSegment StartX=0 StartY=4.5 StartZ=0 EndX=0 EndY=10.8 EndZ=0
    g14: LineSegment StartX=0 StartY=10.8 StartZ=0 EndX=-2 EndY=10.8 EndZ=0
    g15: LineSegment StartX=-1.6 StartY=4.7 StartZ=0 EndX=-1.6 EndY=1.7 EndZ=0
    g16: LineSegment StartX=-1.6 StartY=4.7 StartZ=0 EndX=-2 EndY=4.7 EndZ=0
    g17: LineSegment StartX=-2 StartY=4.7 StartZ=0 EndX=-2 EndY=10.8 EndZ=0
  constraints (44):
    c: Vertical(g0)
    c: Vertical(g1)
    c: Distance(g1) = 0.9
    c: Block(g0)
    c: Distance(g0) = 1.7
    c: Weight(g2) = 1
    c: Equal(g2,g3)
    c: Equal(g2,g4)
    c: Coincident(g5,g1)
    c: InternalAlignment(g2,g5)
    c: InternalAlignment(g3,g5)
    c: InternalAlignment(g4,g5)
    c: InternalAlignment(g6,g5)
    c: InternalAlignment(g7,g5)
    c: Block(g5)
    c: Coincident(g8,g1)
    c: Vertical(g8)
    c: Distance(g8) = 7
    c: Vertical(g9)
    c: Equal(g8,g9) = 7
    c: Coincident(g9,g0)
    c: Coincident(g10,g8)
    c: Coincident(g10,g9)
    c: Horizontal(g10)
    c: Coincident(g11,g5)
    c: Horizontal(g11)
    c: Coincident(g12,g0)
    c: Vertical(g12)
    c: Distance(g12) = 2.8
    c: Coincident(g13,g12)
    c: Vertical(g13)
    c: Distance(g13) = 6.3
    c: Coincident(g14,g13)
    c: Horizontal(g14)
    c: Distance(g14) = 2
    c: Vertical(g15)
    c: Distance(g15) = 3
    c: Block(g11)
    c: Coincident(g15,g11)
    c: Coincident(g16,g15)
    c: Horizontal(g16)
    c: Coincident(g17,g16)
    c: Coincident(g17,g14)
    c: Vertical(g17)
FEATURE [Part::Revolution] Revolve040  label="backCaseScrewRetainer001"
  Angle = 360
  Axis = (0,1,0)
  Base = (0,0,0)
  FaceMakerClass = Part::FaceMakerBullseye
  Placement = pos=(12.5,3,10) rot=(0,0,1;0rad)
  Solid = false
  Source = -> Face036
  Symmetric = false
FEATURE [Part::Feature] Face055
  shape: bbox 3.5 x 30.2 x 2e-07 mm, 1 faces, 0 solids (baked)
FEATURE [Part::Revolution] Revolve059  label="backCaseScrewPost"
  Angle = 360
  Axis = (0,1,0)
  Base = (0,0,0)
  FaceMakerClass = Part::FaceMakerBullseye
  Placement = pos=(12.5,4.5,10) rot=(0,0,1;0rad)
  Solid = false
  Source = -> Face055
  Symmetric = false
FEATURE [Part::Feature] Face056
  shape: bbox 3.5 x 30.2 x 2e-07 mm, 1 faces, 0 solids (baked)
FEATURE [Part::Revolution] Revolve060  label="backCaseScrewPost001"
  Angle = 360
  Axis = (0,1,0)
  Base = (0,0,0)
  FaceMakerClass = Part::FaceMakerBullseye
  Placement = pos=(12.5,4.5,62) rot=(0,0,1;0rad)
  Solid = false
  Source = -> Face056
  Symmetric = false
FEATURE [Part::Feature] Face057
  shape: bbox 3.5 x 17.8 x 2e-07 mm, 1 faces, 0 solids (baked)
FEATURE [Part::Revolution] Revolve061  label="removeToCreateScrewAndThreadedInsertHole"
  Angle = 360
  Axis = (0,1,0)
  Base = (0,0,0)
  FaceMakerClass = Part::FaceMakerBullseye
  Placement = pos=(12.5,0,10) rot=(0,0,1;0rad)
  Solid = false
  Source = -> Face057
  Symmetric = false
FEATURE [Part::Feature] Face058
  shape: bbox 3.5 x 17.8 x 2e-07 mm, 1 faces, 0 solids (baked)
FEATURE [Part::Revolution] Revolve062  label="removeToCreateScrewAndThreadedInsertHole001"
  Angle = 360
  Axis = (0,1,0)
  Base = (0,0,0)
  FaceMakerClass = Part::FaceMakerBullseye
  Placement = pos=(12.5,0,62) rot=(0,0,1;0rad)
  Solid = false
  Source = -> Face058
  Symmetric = false
FEATURE [Part::Feature] Face059
  shape: bbox 3.5 x 17.8 x 2e-07 mm, 1 faces, 0 solids (baked)
FEATURE [Part::Revolution] Revolve063  label="removeToCreateScrewAndThreadedInsertHole002"
  Angle = 360
  Axis = (0,1,0)
  Base = (0,0,0)
  FaceMakerClass = Part::FaceMakerBullseye
  Placement = pos=(89.5,0,68.5) rot=(0,0,1;0rad)
  Solid = false
  Source = -> Face059
  Symmetric = false
FEATURE [Part::Feature] Face060
  shape: bbox 3.5 x 17.8 x 2e-07 mm, 1 faces, 0 solids (baked)
FEATURE [Part::Revolution] Revolve064  label="removeToCreateScrewAndThreadedInsertHole003"
  Angle = 360
  Axis = (0,1,0)
  Base = (0,0,0)
  FaceMakerClass = Part::FaceMakerBullseye
  Placement = pos=(89.5,0,3.5) rot=(0,0,1;0rad)
  Solid = false
  Source = -> Face060
  Symmetric = false
FEATURE [Part::Feature] Face061
  shape: bbox 3.5 x 17.8 x 2e-07 mm, 1 faces, 0 solids (baked)
FEATURE [Part::Revolution] Revolve065  label="removeToCreateScrewAndThreadedInsertHole004"
  Angle = 360
  Axis = (0,1,0)
  Base = (0,0,0)
  FaceMakerClass = Part::FaceMakerBullseye
  Placement = pos=(102.5,4.7,3.5) rot=(0,0,1;0rad)
  Solid = false
  Source = -> Face061
  Symmetric = false
FEATURE [Part::Feature] Face062
  shape: bbox 3.5 x 17.8 x 2e-07 mm, 1 faces, 0 solids (baked)
FEATURE [Part::Revolution] Revolve066  label="removeToCreateScrewAndThreadedInsertHole005"
  Angle = 360
  Axis = (0,1,0)
  Base = (0,0,0)
  FaceMakerClass = Part::FaceMakerBullseye
  Placement = pos=(102.5,4.7,68.5) rot=(0,0,1;0rad)
  Solid = false
  Source = -> Face062
  Symmetric = false
FEATURE [Part::MultiFuse] Fusion047  label="makeHoles"
  Shapes = -> [Revolve066,Revolve065,Revolve064,Revolve063,Revolve062,Revolve061]
FEATURE [Part::Feature] Face063
  shape: bbox 3.6 x 3.2 x 2e-07 mm, 1 faces, 0 solids (baked)
FEATURE [Part::Revolution] Revolve067  label="moreFrontCaseScrewRetainer002"
  Angle = 360
  Axis = (0,1,0)
  Base = (0,0,0)
  FaceMakerClass = Part::FaceMakerBullseye
  Placement = pos=(102.5,4.5,68.5) rot=(0,0,1;0rad)
  Solid = false
  Source = -> Face063
  Symmetric = false
FEATURE [Part::Feature] Face064
  shape: bbox 3.6 x 3.2 x 2e-07 mm, 1 faces, 0 solids (baked)
FEATURE [Part::Revolution] Revolve068  label="moreFrontCaseScrewRetainer003"
  Angle = 360
  Axis = (0,1,0)
  Base = (0,0,0)
  FaceMakerClass = Part::FaceMakerBullseye
  Placement = pos=(102.5,4.5,3.5) rot=(0,0,1;0rad)
  Solid = false
  Source = -> Face064
  Symmetric = false
FEATURE [Part::Feature] Face065
  shape: bbox 3.5 x 17.8 x 2e-07 mm, 1 faces, 0 solids (baked)
FEATURE [Part::Revolution] Revolve069  label="removeToCreateScrewAndThreadedInsertHole006"
  Angle = 360
  Axis = (0,1,0)
  Base = (0,0,0)
  FaceMakerClass = Part::FaceMakerBullseye
  Placement = pos=(12.5,0,10) rot=(0,0,1;0rad)
  Solid = false
  Source = -> Face065
  Symmetric = false
FEATURE [Part::Feature] Face066
  shape: bbox 3.5 x 17.8 x 2e-07 mm, 1 faces, 0 solids (baked)
FEATURE [Part::Revolution] Revolve070  label="removeToCreateScrewAndThreadedInsertHole007"
  Angle = 360
  Axis = (0,1,0)
  Base = (0,0,0)
  FaceMakerClass = Part::FaceMakerBullseye
  Placement = pos=(12.5,0,62) rot=(0,0,1;0rad)
  Solid = false
  Source = -> Face066
  Symmetric = false
FEATURE [Part::Feature] Face067
  shape: bbox 3.5 x 17.8 x 2e-07 mm, 1 faces, 0 solids (baked)
FEATURE [Part::Revolution] Revolve071  label="removeToCreateScrewAndThreadedInsertHole008"
  Angle = 360
  Axis = (0,1,0)
  Base = (0,0,0)
  FaceMakerClass = Part::FaceMakerBullseye
  Placement = pos=(89.5,0,68.5) rot=(0,0,1;0rad)
  Solid = false
  Source = -> Face067
  Symmetric = false
FEATURE [Part::Feature] Face068
  shape: bbox 3.5 x 17.8 x 2e-07 mm, 1 faces, 0 solids (baked)
FEATURE [Part::Revolution] Revolve072  label="removeToCreateScrewAndThreadedInsertHole009"
  Angle = 360
  Axis = (0,1,0)
  Base = (0,0,0)
  FaceMakerClass = Part::FaceMakerBullseye
  Placement = pos=(89.5,0,3.5) rot=(0,0,1;0rad)
  Solid = false
  Source = -> Face068
  Symmetric = false
FEATURE [Part::Feature] Face069
  shape: bbox 3.5 x 17.8 x 2e-07 mm, 1 faces, 0 solids (baked)
FEATURE [Part::Feature] Face070
  shape: bbox 3.5 x 17.8 x 2e-07 mm, 1 faces, 0 solids (baked)
FEATURE [Part::Revolution] Revolve073  label="removeToCreateScrewAndThreadedInsertHole010"
  Angle = 360
  Axis = (0,1,0)
  Base = (0,0,0)
  FaceMakerClass = Part::FaceMakerBullseye
  Placement = pos=(102.5,4.7,3.5) rot=(0,0,1;0rad)
  Solid = false
  Source = -> Face069
  Symmetric = false
FEATURE [Part::Revolution] Revolve074  label="removeToCreateScrewAndThreadedInsertHole011"
  Angle = 360
  Axis = (0,1,0)
  Base = (0,0,0)
  FaceMakerClass = Part::FaceMakerBullseye
  Placement = pos=(102.5,4.7,68.5) rot=(0,0,1;0rad)
  Solid = false
  Source = -> Face070
  Symmetric = false
FEATURE [Part::MultiFuse] Fusion048  label="makeHoles001"
  Shapes = -> [Revolve074,Revolve073,Revolve072,Revolve071,Revolve070,Revolve069]
FEATURE [Part::MultiFuse] Fusion049  label="caseScrewRetainers"
  Shapes = -> [Revolve067,Revolve068,Revolve048,Revolve047,Revolve039,Revolve040]
FEATURE [Part::Cut] Cut015  label="caseScrewRetainers001"
  Base = -> Fusion049
  Tool = -> Fusion048
FEATURE [Part::MultiFuse] Fusion050  label="casePillars"
  Shapes = -> [Revolve055,Revolve054,Revolve043,Revolve046,Revolve059,Revolve060]
FEATURE [Part::Feature] Face071 .. Face076  x6 (patterned run collapsed; names and placements below)
  shape: bbox 3.5 x 17.8 x 2e-07 mm, 1 faces, 0 solids (baked)
FEATURE [Part::Revolution] Revolve075  label="removeToCreateScrewAndThreadedInsertHole012"
  Angle = 360
  Axis = (0,1,0)
  Base = (0,0,0)
  FaceMakerClass = Part::FaceMakerBullseye
  Placement = pos=(12.5,0,10) rot=(0,0,1;0rad)
  Solid = false
  Source = -> Face071
  Symmetric = false
FEATURE [Part::Revolution] Revolve076  label="removeToCreateScrewAndThreadedInsertHole013"
  Angle = 360
  Axis = (0,1,0)
  Base = (0,0,0)
  FaceMakerClass = Part::FaceMakerBullseye
  Placement = pos=(12.5,0,62) rot=(0,0,1;0rad)
  Solid = false
  Source = -> Face072
  Symmetric = false
FEATURE [Part::Revolution] Revolve077  label="removeToCreateScrewAndThreadedInsertHole014"
  Angle = 360
  Axis = (0,1,0)
  Base = (0,0,0)
  FaceMakerClass = Part::FaceMakerBullseye
  Placement = pos=(89.5,0,68.5) rot=(0,0,1;0rad)
  Solid = false
  Source = -> Face073
  Symmetric = false
FEATURE [Part::Revolution] Revolve078  label="removeToCreateScrewAndThreadedInsertHole015"
  Angle = 360
  Axis = (0,1,0)
  Base = (0,0,0)
  FaceMakerClass = Part::FaceMakerBullseye
  Placement = pos=(89.5,0,3.5) rot=(0,0,1;0rad)
  Solid = false
  Source = -> Face074
  Symmetric = false
FEATURE [Part::Revolution] Revolve079  label="removeToCreateScrewAndThreadedInsertHole016"
  Angle = 360
  Axis = (0,1,0)
  Base = (0,0,0)
  FaceMakerClass = Part::FaceMakerBullseye
  Placement = pos=(102.5,4.7,3.5) rot=(0,0,1;0rad)
  Solid = false
  Source = -> Face075
  Symmetric = false
FEATURE [Part::Revolution] Revolve080  label="removeToCreateScrewAndThreadedInsertHole017"
  Angle = 360
  Axis = (0,1,0)
  Base = (0,0,0)
  FaceMakerClass = Part::FaceMakerBullseye
  Placement = pos=(102.5,4.7,68.5) rot=(0,0,1;0rad)
  Solid = false
  Source = -> Face076
  Symmetric = false
FEATURE [Part::MultiFuse] Fusion051  label="makeHoles002"
  Shapes = -> [Revolve080,Revolve079,Revolve078,Revolve077,Revolve076,Revolve075]
FEATURE [Part::Cut] Cut016  label="caesPillars"
  Base = -> Fusion050
  Tool = -> Fusion051
FEATURE [Part::Revolution] Revolve009  label="plugHousing016"
  Angle = 360
  Axis = (0,1,0)
  Base = (0,0,0)
  FaceMakerClass = Part::FaceMakerBullseye
  Placement = pos=(0,0,36.15) rot=(0,0,1;0rad)
  Solid = false
  Source = -> Face012
  Symmetric = false
FEATURE [Part::MultiFuse] Fusion014  label="plugHousing023"
  Placement = pos=(0,0,0) rot=(0,0,1;1.5708rad)
  Shapes = -> [Revolve011,Revolve009]
FEATURE [Part::Revolution] Revolve010  label="plugHousing017"
  Angle = 360
  Axis = (0,1,0)
  Base = (0,0,0)
  FaceMakerClass = Part::FaceMakerBullseye
  Placement = pos=(0,0,36.15) rot=(0,0,1;0rad)
  Solid = false
  Source = -> Face014
  Symmetric = false
FEATURE [Part::MultiFuse] Fusion015  label="plugHousing024"
  Placement = pos=(0,0,0) rot=(0,0,1;1.5708rad)
  Shapes = -> [Revolve010,Revolve015]
FEATURE [Part::Revolution] Revolve014  label="plugHousing026"
  Angle = 360
  Axis = (0,1,0)
  Base = (0,0,0)
  FaceMakerClass = Part::FaceMakerBullseye
  Placement = pos=(0,0,36.15) rot=(0,0,1;0rad)
  Solid = false
  Source = -> Face011
  Symmetric = false
FEATURE [Part::Revolution] Revolve013  label="plugHousing025"
  Angle = 360
  Axis = (0,1,0)
  Base = (0,0,0)
  FaceMakerClass = Part::FaceMakerBullseye
  Placement = pos=(0,0,36.15) rot=(0,0,1;0rad)
  Solid = false
  Source = -> Face015
  Symmetric = false
FEATURE [Part::MultiFuse] Fusion016  label="plugHousing028"
  Placement = pos=(0,19,0) rot=(0,0,1;3.14159rad)
  Shapes = -> [Fusion014,Fusion013]
FEATURE [Part::MultiFuse] Fusion011  label="plugHousing018"
  Placement = pos=(0,0,0) rot=(0,0,1;1.5708rad)
  Shapes = -> [Revolve014,Revolve013]
FEATURE [Part::MultiFuse] Fusion012  label="plugHousing019"
  Placement = pos=(0,19,0) rot=(0,0,1;3.14159rad)
  Shapes = -> [Fusion011,Fusion015]
FEATURE [Part::MultiFuse] Fusion017  label="plugHousing029"
  Placement = pos=(122.621,0,-0.15) rot=(0,0,1;0rad)
  Shapes = -> [Fusion016,Fusion012]
FEATURE [Part::MultiFuse] Fusion052  label="casePillarRetainers"
  Shapes = -> [Extrude012,Extrude013,Extrude014,Extrude015,Extrude016,Extrude017,Extrude018,Extrude019,Box011,Box012]
FEATURE [Part::Feature] Face077
  shape: bbox 3.5 x 17.8 x 2e-07 mm, 1 faces, 0 solids (baked)
FEATURE [Part::Revolution] Revolve081  label="removeToCreateScrewAndThreadedInsertHole018"
  Angle = 360
  Axis = (0,1,0)
  Base = (0,0,0)
  FaceMakerClass = Part::FaceMakerBullseye
  Placement = pos=(62.3,30.3,19.7) rot=(0,0,1;0rad)
  Solid = false
  Source = -> Face077
  Symmetric = false
FEATURE [Part::Feature] Face078
  shape: bbox 3.5 x 17.8 x 2e-07 mm, 1 faces, 0 solids (baked)
FEATURE [Part::Revolution] Revolve082  label="removeToCreateScrewAndThreadedInsertHole019"
  Angle = 360
  Axis = (0,1,0)
  Base = (0,0,0)
  FaceMakerClass = Part::FaceMakerBullseye
  Placement = pos=(62.3,30.3,51.7) rot=(0,0,1;0rad)
  Solid = false
  Source = -> Face078
  Symmetric = false
FEATURE [Part::Feature] Face079
  shape: bbox 3.5 x 17.8 x 2e-07 mm, 1 faces, 0 solids (baked)
FEATURE [Part::Revolution] Revolve083  label="removeToCreateScrewAndThreadedInsertHole020"
  Angle = 360
  Axis = (0,1,0)
  Base = (0,0,0)
  FaceMakerClass = Part::FaceMakerBullseye
  Placement = pos=(30.3,30.3,19.7) rot=(0,0,1;0rad)
  Solid = false
  Source = -> Face079
  Symmetric = false
FEATURE [Part::Feature] Face080
  shape: bbox 3.5 x 17.8 x 2e-07 mm, 1 faces, 0 solids (baked)
FEATURE [Part::Revolution] Revolve084  label="removeToCreateScrewAndThreadedInsertHole021"
  Angle = 360
  Axis = (0,1,0)
  Base = (0,0,0)
  FaceMakerClass = Part::FaceMakerBullseye
  Placement = pos=(30.3,30.3,51.7) rot=(0,0,1;0rad)
  Solid = false
  Source = -> Face080
  Symmetric = false
FEATURE [Part::MultiFuse] Fusion053  label="createThreadedInsertHolesForFan"
  Shapes = -> [Revolve081,Revolve082,Revolve083,Revolve084]
FEATURE [Part::Cut] Cut017  label="fanScrewHousing001"
  Base = -> Fusion046
  Tool = -> Fusion053
FEATURE [Part::Feature] Face081
  shape: bbox 3.5 x 17.8 x 2e-07 mm, 1 faces, 0 solids (baked)
FEATURE [Part::Revolution] Revolve085  label="removeToCreateScrewAndThreadedInsertHole022"
  Angle = 360
  Axis = (0,1,0)
  Base = (0,0,0)
  FaceMakerClass = Part::FaceMakerBullseye
  Placement = pos=(62.3,30.3,19.7) rot=(0,0,1;0rad)
  Solid = false
  Source = -> Face081
  Symmetric = false
FEATURE [Part::Feature] Face082
  shape: bbox 3.5 x 17.8 x 2e-07 mm, 1 faces, 0 solids (baked)
FEATURE [Part::Revolution] Revolve086  label="removeToCreateScrewAndThreadedInsertHole023"
  Angle = 360
  Axis = (0,1,0)
  Base = (0,0,0)
  FaceMakerClass = Part::FaceMakerBullseye
  Placement = pos=(62.3,30.3,51.7) rot=(0,0,1;0rad)
  Solid = false
  Source = -> Face082
  Symmetric = false
FEATURE [Part::Feature] Face083
  shape: bbox 3.5 x 17.8 x 2e-07 mm, 1 faces, 0 solids (baked)
FEATURE [Part::Revolution] Revolve087  label="removeToCreateScrewAndThreadedInsertHole024"
  Angle = 360
  Axis = (0,1,0)
  Base = (0,0,0)
  FaceMakerClass = Part::FaceMakerBullseye
  Placement = pos=(30.3,30.3,19.7) rot=(0,0,1;0rad)
  Solid = false
  Source = -> Face083
  Symmetric = false
FEATURE [Part::Feature] Face084
  shape: bbox 3.5 x 17.8 x 2e-07 mm, 1 faces, 0 solids (baked)
FEATURE [Part::Revolution] Revolve088  label="removeToCreateScrewAndThreadedInsertHole025"
  Angle = 360
  Axis = (0,1,0)
  Base = (0,0,0)
  FaceMakerClass = Part::FaceMakerBullseye
  Placement = pos=(30.3,30.3,51.7) rot=(0,0,1;0rad)
  Solid = false
  Source = -> Face084
  Symmetric = false
FEATURE [Part::MultiFuse] Fusion054  label="createThreadedInsertHolesForFan001"
  Shapes = -> [Revolve085,Revolve086,Revolve087,Revolve088]
FEATURE [Part::Cut] Cut018  label="top007"
  Base = -> Fusion040
  Tool = -> Fusion054
FEATURE [Sketcher::SketchObject] Sketch029
  FullyConstrained = false
  Placement = pos=(0,0,0) rot=(1,0,0;1.5708rad)
  sketch-geometry (24):
    g0: ArcOfCircle CenterX=-4 CenterY=-10.5 CenterZ=0 NormalX=0 NormalY=0 NormalZ=1 AngleXU=0 Radius=1.5 StartAngle=6e-16 EndAngle=3.14159
    g1: ArcOfCircle CenterX=-34.2 CenterY=-10.5 CenterZ=0 NormalX=0 NormalY=0 NormalZ=1 AngleXU=0 Radius=1.5 StartAngle=0 EndAngle=3.14159
    g2: ArcOfCircle CenterX=-34.2 CenterY=-27.7 CenterZ=0 NormalX=0 NormalY=0 NormalZ=1 AngleXU=0 Radius=1.5 StartAngle=3.14159 EndAngle=6.28319
    g3: ArcOfCircle CenterX=-4 CenterY=-27.7 CenterZ=0 NormalX=0 NormalY=0 NormalZ=1 AngleXU=0 Radius=1.5 StartAngle=3.1416 EndAngle=6.28319
    g4: ArcOfCircle CenterX=-10 CenterY=-4.3 CenterZ=0 NormalX=0 NormalY=0 NormalZ=1 AngleXU=0 Radius=1.5 StartAngle=2e-16 EndAngle=3.14159
    g5: ArcOfCircle CenterX=-16.1 CenterY=-1.8 CenterZ=0 NormalX=0 NormalY=0 NormalZ=1 AngleXU=0 Radius=1.5 StartAngle=5e-16 EndAngle=3.14159
    g6: ArcOfCircle CenterX=-22.1 CenterY=-1.8 CenterZ=0 NormalX=0 NormalY=0 NormalZ=1 AngleXU=0 Radius=1.5 StartAngle=5e-16 EndAngle=3.14159
    g7: ArcOfCircle CenterX=-28.2 CenterY=-4.3 CenterZ=0 NormalX=0 NormalY=0 NormalZ=1 AngleXU=0 Radius=1.5 StartAngle=2e-16 EndAngle=3.14159
    g8: ArcOfCircle CenterX=-10 CenterY=-33.9 CenterZ=0 NormalX=0 NormalY=0 NormalZ=1 AngleXU=0 Radius=1.5 StartAngle=3.14159 EndAngle=6.28319
    g9: ArcOfCircle CenterX=-16.1 CenterY=-36.4 CenterZ=0 NormalX=0 NormalY=0 NormalZ=1 AngleXU=0 Radius=1.5 StartAngle=3.14159 EndAngle=6.28319
    g10: ArcOfCircle CenterX=-22.1 CenterY=-36.4 CenterZ=0 NormalX=0 NormalY=0 NormalZ=1 AngleXU=0 Radius=1.5 StartAngle=3.14159 EndAngle=6.28319
    g11: ArcOfCircle CenterX=-28.2 CenterY=-33.9 CenterZ=0 NormalX=0 NormalY=0 NormalZ=1 AngleXU=0 Radius=1.5 StartAngle=3.14159 EndAngle=6.28319
    g12: LineSegment StartX=-35.7 StartY=-10.5 StartZ=0 EndX=-35.7 EndY=-27.7 EndZ=0
    g13: LineSegment StartX=-32.7 StartY=-10.5 StartZ=0 EndX=-32.7 EndY=-27.7 EndZ=0
    g14: LineSegment StartX=-29.7 StartY=-33.9 StartZ=0 EndX=-29.7 EndY=-4.3 EndZ=0
    g15: LineSegment StartX=-26.7 StartY=-33.9 StartZ=0 EndX=-26.7 EndY=-4.3 EndZ=0
    g16: LineSegment StartX=-2.5 StartY=-10.5 StartZ=0 EndX=-2.5 EndY=-27.7 EndZ=0
    g17: LineSegment StartX=-8.5 StartY=-4.3 StartZ=0 EndX=-8.5 EndY=-33.9 EndZ=0
    g18: LineSegment StartX=-5.5 StartY=-10.5 StartZ=0 EndX=-5.5 EndY=-27.7 EndZ=0
    g19: LineSegment StartX=-11.5 StartY=-4.3 StartZ=0 EndX=-11.5 EndY=-33.9 EndZ=0
    g20: LineSegment StartX=-14.6 StartY=-1.8 StartZ=0 EndX=-14.6 EndY=-36.4 EndZ=0
    g21: LineSegment StartX=-17.6 StartY=-1.8 StartZ=0 EndX=-17.6 EndY=-36.4 EndZ=0
    g22: LineSegment StartX=-20.6 StartY=-36.4 StartZ=0 EndX=-20.6 EndY=-1.8 EndZ=0
    g23: LineSegment StartX=-23.6 StartY=-1.8 StartZ=0 EndX=-23.6 EndY=-36.4 EndZ=0
  constraints (48):
    c: Block(g0)
    c: Block(g1)
    c: Block(g2)
    c: Block(g3)
    c: Block(g4)
    c: Block(g5)
    c: Block(g6)
    c: Block(g7)
    c: Block(g8)
    c: Block(g9)
    c: Block(g10)
    c: Block(g11)
    c: Coincident(g12,g1)
    c: Coincident(g12,g2)
    c: Vertical(g12)
    c: Coincident(g13,g1)
    c: Coincident(g13,g2)
    c: Vertical(g13)
    c: Coincident(g14,g11)
    c: Coincident(g14,g7)
    c: Vertical(g14)
    c: Coincident(g15,g11)
    c: Coincident(g15,g7)
    c: Vertical(g15)
    c: Coincident(g16,g0)
    c: Coincident(g16,g3)
    c: Vertical(g16)
    c: Coincident(g17,g4)
    c: Coincident(g17,g8)
    c: Vertical(g17)
    c: Coincident(g18,g0)
    c: Coincident(g18,g3)
    c: Vertical(g18)
    c: Coincident(g19,g4)
    c: Coincident(g19,g8)
    c: Vertical(g19)
    c: Coincident(g20,g5)
    c: Coincident(g20,g9)
    c: Vertical(g20)
    c: Coincident(g21,g5)
    c: Coincident(g21,g9)
    c: Vertical(g21)
    c: Coincident(g22,g10)
    c: Coincident(g22,g6)
    c: Vertical(g22)
    c: Coincident(g23,g6)
    c: Coincident(g23,g10)
    c: Vertical(g23)
FEATURE [Part::Extrusion] Extrude020  label="removeToCreateFanGrillHoles"
  Base = -> Sketch029
  Dir = (0,-1,6e-16)
  DirMode = 2
  FaceMakerClass = Part::FaceMakerBullseye
  LengthFwd = 10
  LengthRev = 0
  Placement = pos=(65.4,44,54.82) rot=(0,0,1;0rad)
  Solid = true
  Symmetric = false
FEATURE [Part::MultiFuse] Fusion055  label="top008"
  Shapes = -> [Cut017,Cut018]
FEATURE [Part::Cut] Cut019  label="top009"
  Base = -> Fusion055
  Tool = -> Extrude020
FEATURE [App::MeasureDistance] Distance003  label="Distance: 71.95 mm"
  Distance = 71.9513
  P1 = (117,38,72)
  P2 = (117,38,0.0487319)
FEATURE [Sketcher::SketchObject] Sketch030
  FullyConstrained = true
  Placement = pos=(117,19,0) rot=(0.57735,0.57735,0.57735;2.0944rad)
  sketch-geometry (48):
    g0: LineSegment StartX=-49.19 StartY=69.25 StartZ=0 EndX=-49.19 EndY=66.25 EndZ=0
    g1: LineSegment StartX=-49.19 StartY=63.5 StartZ=0 EndX=-49.19 EndY=60.5 EndZ=0
    g2: LineSegment StartX=-49.19 StartY=57.75 StartZ=0 EndX=-49.19 EndY=54.75 EndZ=0
    g3: LineSegment StartX=-49.19 StartY=52 StartZ=0 EndX=-49.19 EndY=49 EndZ=0
    g4: LineSegment StartX=-49.19 StartY=46.25 StartZ=0 EndX=-49.19 EndY=43.25 EndZ=0
    g5: LineSegment StartX=-49.19 StartY=40.5 StartZ=0 EndX=-49.19 EndY=37.5 EndZ=0
    g6: LineSegment StartX=-49.19 StartY=34.5 StartZ=0 EndX=-49.19 EndY=31.5 EndZ=0
    g7: LineSegment StartX=-49.19 StartY=28.75 StartZ=0 EndX=-49.19 EndY=25.75 EndZ=0
    g8: LineSegment StartX=-49.19 StartY=23 StartZ=0 EndX=-49.19 EndY=20 EndZ=0
    g9: LineSegment StartX=-49.19 StartY=17.25 StartZ=0 EndX=-49.19 EndY=14.25 EndZ=0
    g10: LineSegment StartX=-49.19 StartY=11.5 StartZ=0 EndX=-49.19 EndY=8.5 EndZ=0
    g11: LineSegment StartX=-49.19 StartY=5.75 StartZ=0 EndX=-49.19 EndY=2.75 EndZ=0
    g12: ArcOfCircle CenterX=-1.5 CenterY=67.75 CenterZ=0 NormalX=0 NormalY=0 NormalZ=1 AngleXU=0 Radius=1.5 StartAngle=4.71239 EndAngle=7.85398
    g13: ArcOfCircle CenterX=-1.5 CenterY=62 CenterZ=0 NormalX=0 NormalY=0 NormalZ=1 AngleXU=0 Radius=1.5 StartAngle=4.71239 EndAngle=7.85398
    g14: ArcOfCircle CenterX=-1.5 CenterY=56.25 CenterZ=0 NormalX=0 NormalY=0 NormalZ=1 AngleXU=0 Radius=1.5 StartAngle=4.71239 EndAngle=7.85398
    g15: ArcOfCircle CenterX=-11.49 CenterY=50.5 CenterZ=0 NormalX=0 NormalY=0 NormalZ=1 AngleXU=0 Radius=1.5 StartAngle=4.71239 EndAngle=7.85398
    g16: ArcOfCircle CenterX=-16.28 CenterY=44.75 CenterZ=0 NormalX=0 NormalY=0 NormalZ=1 AngleXU=0 Radius=1.5 StartAngle=4.71239 EndAngle=7.85398
    g17: ArcOfCircle CenterX=-18.2337 CenterY=39 CenterZ=0 NormalX=0 NormalY=0 NormalZ=1 AngleXU=0 Radius=1.5 StartAngle=4.71485 EndAngle=7.85398
    g18: ArcOfCircle CenterX=-16.2837 CenterY=27.25 CenterZ=0 NormalX=0 NormalY=0 NormalZ=1 AngleXU=0 Radius=1.5 StartAngle=4.71485 EndAngle=7.85398
    g19: ArcOfCircle CenterX=-18.2337 CenterY=33 CenterZ=0 NormalX=0 NormalY=0 NormalZ=1 AngleXU=0 Radius=1.5 StartAngle=4.71485 EndAngle=7.85398
    g20: ArcOfCircle CenterX=-11.49 CenterY=21.5 CenterZ=0 NormalX=0 NormalY=0 NormalZ=1 AngleXU=0 Radius=1.5 StartAngle=4.71239 EndAngle=7.85398
    g21: ArcOfCircle CenterX=-1.5 CenterY=4.25 CenterZ=0 NormalX=0 NormalY=0 NormalZ=1 AngleXU=0 Radius=1.5 StartAngle=4.71239 EndAngle=7.85398
    g22: ArcOfCircle CenterX=-1.5 CenterY=10 CenterZ=0 NormalX=0 NormalY=0 NormalZ=1 AngleXU=0 Radius=1.5 StartAngle=4.71239 EndAngle=7.85398
    g23: ArcOfCircle CenterX=-1.5 CenterY=15.75 CenterZ=0 NormalX=0 NormalY=0 NormalZ=1 AngleXU=0 Radius=1.5 StartAngle=4.71239 EndAngle=7.85398
    g24: LineSegment StartX=-49.19 StartY=69.25 StartZ=0 EndX=-1.5 EndY=69.25 EndZ=0
    g25: LineSegment StartX=-49.19 StartY=66.25 StartZ=0 EndX=-1.5 EndY=66.25 EndZ=0
    g26: LineSegment StartX=-49.19 StartY=63.5 StartZ=0 EndX=-1.5 EndY=63.5 EndZ=0
    g27: LineSegment StartX=-49.19 StartY=60.5 StartZ=0 EndX=-1.5 EndY=60.5 EndZ=0
    g28: LineSegment StartX=-49.19 StartY=57.75 StartZ=0 EndX=-1.5 EndY=57.75 EndZ=0
    g29: LineSegment StartX=-49.19 StartY=54.75 StartZ=0 EndX=-1.5 EndY=54.75 EndZ=0
    g30: LineSegment StartX=-49.19 StartY=52 StartZ=0 EndX=-11.49 EndY=52 EndZ=0
    g31: LineSegment StartX=-49.19 StartY=49 StartZ=0 EndX=-11.49 EndY=49 EndZ=0
    g32: LineSegment StartX=-49.19 StartY=46.25 StartZ=0 EndX=-16.28 EndY=46.25 EndZ=0
    g33: LineSegment StartX=-49.19 StartY=43.25 StartZ=0 EndX=-16.28 EndY=43.25 EndZ=0
    g34: LineSegment StartX=-49.19 StartY=40.5 StartZ=0 EndX=-18.2337 EndY=40.5 EndZ=0
    g35: LineSegment StartX=-49.19 StartY=37.5 StartZ=0 EndX=-18.23 EndY=37.5 EndZ=0
    g36: LineSegment StartX=-49.19 StartY=34.5 StartZ=0 EndX=-18.2337 EndY=34.5 EndZ=0
    g37: LineSegment StartX=-49.19 StartY=31.5 StartZ=0 EndX=-18.23 EndY=31.5 EndZ=0
    g38: LineSegment StartX=-49.19 StartY=28.75 StartZ=0 EndX=-16.2837 EndY=28.75 EndZ=0
    g39: LineSegment StartX=-49.19 StartY=25.75 StartZ=0 EndX=-16.28 EndY=25.75 EndZ=0
    g40: LineSegment StartX=-49.19 StartY=23 StartZ=0 EndX=-11.49 EndY=23 EndZ=0
    g41: LineSegment StartX=-49.19 StartY=20 StartZ=0 EndX=-11.49 EndY=20 EndZ=0
    g42: LineSegment StartX=-49.19 StartY=17.25 StartZ=0 EndX=-1.5 EndY=17.25 EndZ=0
    g43: LineSegment StartX=-49.19 StartY=14.25 StartZ=0 EndX=-1.5 EndY=14.25 EndZ=0
    g44: LineSegment StartX=-49.19 StartY=11.5 StartZ=0 EndX=-1.5 EndY=11.5 EndZ=0
    g45: LineSegment StartX=-49.19 StartY=8.5 StartZ=0 EndX=-1.5 EndY=8.5 EndZ=0
    g46: LineSegment StartX=-49.19 StartY=5.75 StartZ=0 EndX=-1.5 EndY=5.75 EndZ=0
    g47: LineSegment StartX=-49.19 StartY=2.75 StartZ=0 EndX=-1.5 EndY=2.75 EndZ=0
  constraints (120):
    c: Vertical(g0)
    c: Distance(g0) = 3
    c: Block(g0)
    c: Vertical(g1)
    c: Distance(g1) = 3
    c: Vertical(g2)
    c: Equal(g0,g2) = 3
    c: Block(g2)
    c: Vertical(g3)
    c: Equal(g1,g3) = 3
    c: Vertical(g4)
    c: Equal(g0,g4) = 3
    c: Block(g4)
    c: Vertical(g5)
    c: Equal(g1,g5) = 3
    c: Vertical(g6)
    c: Equal(g0,g6) = 3
    c: Block(g6)
    c: Vertical(g7)
    c: Equal(g1,g7) = 3
    c: Vertical(g8)
    c: Equal(g0,g8) = 3
    c: Block(g8)
    c: Vertical(g9)
    c: Equal(g1,g9) = 3
    c: Vertical(g10)
    c: Equal(g0,g10) = 3
    c: Block(g10)
    c: Vertical(g11)
    c: Equal(g1,g11) = 3
    c: Block(g12)
    c: Block(g13)
    c: Block(g14)
    c: Block(g15)
    c: Block(g16)
    c: Block(g17)
    c: Block(g18)
    c: Block(g19)
    c: Block(g20)
    c: Block(g21)
    c: Block(g22)
    c: Block(g23)
    c: Block(g11)
    c: Block(g9)
    c: Block(g7)
    c: Block(g5)
    c: Block(g3)
    c: Block(g1)
    c: Coincident(g24,g0)
    c: Coincident(g24,g12)
    c: Horizontal(g24)
    c: Coincident(g25,g0)
    c: Coincident(g25,g12)
    c: Horizontal(g25)
    c: Coincident(g26,g1)
    c: Coincident(g26,g13)
    c: Horizontal(g26)
    c: Coincident(g27,g1)
    c: Coincident(g27,g13)
    c: Horizontal(g27)
    c: Coincident(g28,g2)
    c: Coincident(g28,g14)
    c: Horizontal(g28)
    c: Coincident(g29,g2)
    c: Coincident(g29,g14)
    c: Horizontal(g29)
    c: Coincident(g30,g3)
    c: Coincident(g30,g15)
    c: Horizontal(g30)
    c: Coincident(g31,g3)
    c: Coincident(g31,g15)
    c: Horizontal(g31)
    c: Coincident(g32,g4)
    c: Coincident(g32,g16)
    c: Horizontal(g32)
    c: Coincident(g33,g4)
    c: Coincident(g33,g16)
    c: Horizontal(g33)
    c: Coincident(g34,g5)
    c: Coincident(g34,g17)
    c: Horizontal(g34)
    c: Coincident(g35,g5)
    c: Coincident(g35,g17)
    c: Horizontal(g35)
    c: Coincident(g36,g6)
    c: Coincident(g36,g19)
    c: Horizontal(g36)
    c: Coincident(g37,g6)
    c: Coincident(g37,g19)
    c: Horizontal(g37)
    c: Coincident(g38,g7)
    c: Coincident(g38,g18)
    c: Horizontal(g38)
    c: Coincident(g39,g7)
    c: Coincident(g39,g18)
    c: Horizontal(g39)
    c: Coincident(g40,g8)
    c: Coincident(g40,g20)
    c: Horizontal(g40)
    c: Coincident(g41,g8)
    c: Coincident(g41,g20)
    c: Horizontal(g41)
    c: Coincident(g42,g9)
    c: Coincident(g42,g23)
    c: Horizontal(g42)
    c: Coincident(g43,g9)
    c: Coincident(g43,g23)
    c: Horizontal(g43)
    c: Coincident(g44,g10)
    c: Coincident(g44,g22)
    c: Horizontal(g44)
    c: Coincident(g45,g10)
    c: Coincident(g45,g22)
    c: Horizontal(g45)
    c: Coincident(g46,g11)
    c: Coincident(g46,g21)
    c: Horizontal(g46)
    c: Coincident(g47,g11)
    c: Coincident(g47,g21)
    c: Horizontal(g47)
FEATURE [Sketcher::SketchObject] Sketch031
  FullyConstrained = true
  Placement = pos=(117,19,0) rot=(0.57735,0.57735,0.57735;2.0944rad)
  sketch-geometry (24):
    g0: ArcOfCircle CenterX=-49.19 CenterY=67.75 CenterZ=0 NormalX=0 NormalY=0 NormalZ=1 AngleXU=0 Radius=1.5 StartAngle=1.5708 EndAngle=4.71239
    g1: ArcOfCircle CenterX=-49.19 CenterY=62 CenterZ=0 NormalX=0 NormalY=0 NormalZ=1 AngleXU=0 Radius=1.5 StartAngle=1.5708 EndAngle=4.71239
    g2: ArcOfCircle CenterX=-49.19 CenterY=56.25 CenterZ=0 NormalX=0 NormalY=0 NormalZ=1 AngleXU=0 Radius=1.5 StartAngle=1.5708 EndAngle=4.71239
    g3: ArcOfCircle CenterX=-49.19 CenterY=50.5 CenterZ=0 NormalX=0 NormalY=0 NormalZ=1 AngleXU=0 Radius=1.5 StartAngle=1.5708 EndAngle=4.71239
    g4: ArcOfCircle CenterX=-49.19 CenterY=44.75 CenterZ=0 NormalX=0 NormalY=0 NormalZ=1 AngleXU=0 Radius=1.5 StartAngle=1.5708 EndAngle=4.71239
    g5: ArcOfCircle CenterX=-49.19 CenterY=39 CenterZ=0 NormalX=0 NormalY=0 NormalZ=1 AngleXU=0 Radius=1.5 StartAngle=1.5708 EndAngle=4.71239
    g6: ArcOfCircle CenterX=-49.19 CenterY=33 CenterZ=0 NormalX=0 NormalY=0 NormalZ=1 AngleXU=0 Radius=1.5 StartAngle=1.5708 EndAngle=4.71239
    g7: ArcOfCircle CenterX=-49.19 CenterY=27.25 CenterZ=0 NormalX=0 NormalY=0 NormalZ=1 AngleXU=0 Radius=1.5 StartAngle=1.5708 EndAngle=4.71239
    g8: ArcOfCircle CenterX=-49.19 CenterY=21.5 CenterZ=0 NormalX=0 NormalY=0 NormalZ=1 AngleXU=0 Radius=1.5 StartAngle=1.5708 EndAngle=4.71239
    g9: ArcOfCircle CenterX=-49.19 CenterY=15.75 CenterZ=0 NormalX=0 NormalY=0 NormalZ=1 AngleXU=0 Radius=1.5 StartAngle=1.5708 EndAngle=4.71239
    g10: ArcOfCircle CenterX=-49.19 CenterY=10 CenterZ=0 NormalX=0 NormalY=0 NormalZ=1 AngleXU=0 Radius=1.5 StartAngle=1.5708 EndAngle=4.71239
    g11: ArcOfCircle CenterX=-49.19 CenterY=4.25 CenterZ=0 NormalX=0 NormalY=0 NormalZ=1 AngleXU=0 Radius=1.5 StartAngle=1.5708 EndAngle=4.71239
    g12: LineSegment StartX=-49.19 StartY=69.25 StartZ=0 EndX=-49.19 EndY=66.25 EndZ=0
    g13: LineSegment StartX=-49.19 StartY=63.5 StartZ=0 EndX=-49.19 EndY=60.5 EndZ=0
    g14: LineSegment StartX=-49.19 StartY=57.75 StartZ=0 EndX=-49.19 EndY=54.75 EndZ=0
    g15: LineSegment StartX=-49.19 StartY=52 StartZ=0 EndX=-49.19 EndY=49 EndZ=0
    g16: LineSegment StartX=-49.19 StartY=46.25 StartZ=0 EndX=-49.19 EndY=43.25 EndZ=0
    g17: LineSegment StartX=-49.19 StartY=40.5 StartZ=0 EndX=-49.19 EndY=37.5 EndZ=0
    g18: LineSegment StartX=-49.19 StartY=34.5 StartZ=0 EndX=-49.19 EndY=31.5 EndZ=0
    g19: LineSegment StartX=-49.19 StartY=28.75 StartZ=0 EndX=-49.19 EndY=25.75 EndZ=0
    g20: LineSegment StartX=-49.19 StartY=23 StartZ=0 EndX=-49.19 EndY=20 EndZ=0
    g21: LineSegment StartX=-49.19 StartY=17.25 StartZ=0 EndX=-49.19 EndY=14.25 EndZ=0
    g22: LineSegment StartX=-49.19 StartY=11.5 StartZ=0 EndX=-49.19 EndY=8.5 EndZ=0
    g23: LineSegment StartX=-49.19 StartY=5.75 StartZ=0 EndX=-49.19 EndY=2.75 EndZ=0
  constraints (48):
    c: Block(g0)
    c: Block(g1)
    c: Block(g2)
    c: Block(g3)
    c: Block(g4)
    c: Block(g5)
    c: Block(g6)
    c: Block(g7)
    c: Block(g8)
    c: Block(g9)
    c: Block(g10)
    c: Block(g11)
    c: Coincident(g12,g0)
    c: Coincident(g12,g0)
    c: Vertical(g12)
    c: Vertical(g13)
    c: Coincident(g13,g1)
    c: Vertical(g14)
    c: Coincident(g14,g2)
    c: Vertical(g15)
    c: Coincident(g15,g3)
    c: Vertical(g16)
    c: Coincident(g16,g4)
    c: Vertical(g17)
    c: Coincident(g17,g5)
    c: Vertical(g18)
    c: Coincident(g18,g6)
    c: Vertical(g19)
    c: Coincident(g19,g7)
    c: Vertical(g20)
    c: Coincident(g20,g8)
    c: Vertical(g21)
    c: Coincident(g21,g9)
    c: Vertical(g22)
    c: Coincident(g22,g10)
    c: Vertical(g23)
    c: Coincident(g23,g11)
    c: Block(g23)
    c: Block(g22)
    c: Block(g21)
    c: Block(g20)
    c: Block(g13)
    c: Block(g14)
    c: Block(g15)
    c: Block(g16)
    c: Block(g17)
    c: Block(g18)
    c: Block(g19)
FEATURE [Part::Extrusion] Extrude022
  Base = -> Sketch030
  Dir = (1,-2e-16,2e-16)
  DirMode = 2
  FaceMakerClass = Part::FaceMakerBullseye
  LengthFwd = 19
  LengthRev = 0
  Placement = pos=(-19,0,0) rot=(0,0,1;0rad)
  Solid = true
  Symmetric = false
FEATURE [Part::Fillet] Fillet022
  Base = -> Extrude022
  Edges = 24 edges r=1.49: [Edge6,Edge11,Edge18,Edge23,Edge30,Edge35,Edge42,Edge47,Edge54,Edge59,Edge66,Edge71,Edge78,Edge83,Edge90,Edge95,Edge102,Edge107,Edge114,Edge119,Edge126,Edge131,Edge138,Edge143]
FEATURE [Part::Cut] Cut020  label="top010"
  Base = -> Cut019
  Tool = -> Fillet022
FEATURE [Sketcher::SketchObject] Sketch032
  FullyConstrained = true
  Placement = pos=(117,19,0) rot=(0.57735,0.57735,0.57735;2.0944rad)
  sketch-geometry (48):
    g0: LineSegment StartX=-49.19 StartY=69.25 StartZ=0 EndX=-49.19 EndY=66.25 EndZ=0
    g1: LineSegment StartX=-49.19 StartY=63.5 StartZ=0 EndX=-49.19 EndY=60.5 EndZ=0
    g2: LineSegment StartX=-49.19 StartY=57.75 StartZ=0 EndX=-49.19 EndY=54.75 EndZ=0
    g3: LineSegment StartX=-49.19 StartY=52 StartZ=0 EndX=-49.19 EndY=49 EndZ=0
    g4: LineSegment StartX=-49.19 StartY=46.25 StartZ=0 EndX=-49.19 EndY=43.25 EndZ=0
    g5: LineSegment StartX=-49.19 StartY=40.5 StartZ=0 EndX=-49.19 EndY=37.5 EndZ=0
    g6: LineSegment StartX=-49.19 StartY=34.5 StartZ=0 EndX=-49.19 EndY=31.5 EndZ=0
    g7: LineSegment StartX=-49.19 StartY=28.75 StartZ=0 EndX=-49.19 EndY=25.75 EndZ=0
    g8: LineSegment StartX=-49.19 StartY=23 StartZ=0 EndX=-49.19 EndY=20 EndZ=0
    g9: LineSegment StartX=-49.19 StartY=17.25 StartZ=0 EndX=-49.19 EndY=14.25 EndZ=0
    g10: LineSegment StartX=-49.19 StartY=11.5 StartZ=0 EndX=-49.19 EndY=8.5 EndZ=0
    g11: LineSegment StartX=-49.19 StartY=5.75 StartZ=0 EndX=-49.19 EndY=2.75 EndZ=0
    g12: ArcOfCircle CenterX=-1.5 CenterY=67.75 CenterZ=0 NormalX=0 NormalY=0 NormalZ=1 AngleXU=0 Radius=1.5 StartAngle=4.71239 EndAngle=7.85398
    g13: ArcOfCircle CenterX=-1.5 CenterY=62 CenterZ=0 NormalX=0 NormalY=0 NormalZ=1 AngleXU=0 Radius=1.5 StartAngle=4.71239 EndAngle=7.85398
    g14: ArcOfCircle CenterX=-1.5 CenterY=56.25 CenterZ=0 NormalX=0 NormalY=0 NormalZ=1 AngleXU=0 Radius=1.5 StartAngle=4.71239 EndAngle=7.85398
    g15: ArcOfCircle CenterX=-11.49 CenterY=50.5 CenterZ=0 NormalX=0 NormalY=0 NormalZ=1 AngleXU=0 Radius=1.5 StartAngle=4.71239 EndAngle=7.85398
    g16: ArcOfCircle CenterX=-16.28 CenterY=44.75 CenterZ=0 NormalX=0 NormalY=0 NormalZ=1 AngleXU=0 Radius=1.5 StartAngle=4.71239 EndAngle=7.85398
    g17: ArcOfCircle CenterX=-18.2337 CenterY=39 CenterZ=0 NormalX=0 NormalY=0 NormalZ=1 AngleXU=0 Radius=1.5 StartAngle=4.71485 EndAngle=7.85398
    g18: ArcOfCircle CenterX=-16.2837 CenterY=27.25 CenterZ=0 NormalX=0 NormalY=0 NormalZ=1 AngleXU=0 Radius=1.5 StartAngle=4.71485 EndAngle=7.85398
    g19: ArcOfCircle CenterX=-18.2337 CenterY=33 CenterZ=0 NormalX=0 NormalY=0 NormalZ=1 AngleXU=0 Radius=1.5 StartAngle=4.71485 EndAngle=7.85398
    g20: ArcOfCircle CenterX=-11.49 CenterY=21.5 CenterZ=0 NormalX=0 NormalY=0 NormalZ=1 AngleXU=0 Radius=1.5 StartAngle=4.71239 EndAngle=7.85398
    g21: ArcOfCircle CenterX=-1.5 CenterY=4.25 CenterZ=0 NormalX=0 NormalY=0 NormalZ=1 AngleXU=0 Radius=1.5 StartAngle=4.71239 EndAngle=7.85398
    g22: ArcOfCircle CenterX=-1.5 CenterY=10 CenterZ=0 NormalX=0 NormalY=0 NormalZ=1 AngleXU=0 Radius=1.5 StartAngle=4.71239 EndAngle=7.85398
    g23: ArcOfCircle CenterX=-1.5 CenterY=15.75 CenterZ=0 NormalX=0 NormalY=0 NormalZ=1 AngleXU=0 Radius=1.5 StartAngle=4.71239 EndAngle=7.85398
    g24: LineSegment StartX=-49.19 StartY=69.25 StartZ=0 EndX=-1.5 EndY=69.25 EndZ=0
    g25: LineSegment StartX=-49.19 StartY=66.25 StartZ=0 EndX=-1.5 EndY=66.25 EndZ=0
    g26: LineSegment StartX=-49.19 StartY=63.5 StartZ=0 EndX=-1.5 EndY=63.5 EndZ=0
    g27: LineSegment StartX=-49.19 StartY=60.5 StartZ=0 EndX=-1.5 EndY=60.5 EndZ=0
    g28: LineSegment StartX=-49.19 StartY=57.75 StartZ=0 EndX=-1.5 EndY=57.75 EndZ=0
    g29: LineSegment StartX=-49.19 StartY=54.75 StartZ=0 EndX=-1.5 EndY=54.75 EndZ=0
    g30: LineSegment StartX=-49.19 StartY=52 StartZ=0 EndX=-11.49 EndY=52 EndZ=0
    g31: LineSegment StartX=-49.19 StartY=49 StartZ=0 EndX=-11.49 EndY=49 EndZ=0
    g32: LineSegment StartX=-49.19 StartY=46.25 StartZ=0 EndX=-16.28 EndY=46.25 EndZ=0
    g33: LineSegment StartX=-49.19 StartY=43.25 StartZ=0 EndX=-16.28 EndY=43.25 EndZ=0
    g34: LineSegment StartX=-49.19 StartY=40.5 StartZ=0 EndX=-18.2337 EndY=40.5 EndZ=0
    g35: LineSegment StartX=-49.19 StartY=37.5 StartZ=0 EndX=-18.23 EndY=37.5 EndZ=0
    g36: LineSegment StartX=-49.19 StartY=34.5 StartZ=0 EndX=-18.2337 EndY=34.5 EndZ=0
    g37: LineSegment StartX=-49.19 StartY=31.5 StartZ=0 EndX=-18.23 EndY=31.5 EndZ=0
    g38: LineSegment StartX=-49.19 StartY=28.75 StartZ=0 EndX=-16.2837 EndY=28.75 EndZ=0
    g39: LineSegment StartX=-49.19 StartY=25.75 StartZ=0 EndX=-16.28 EndY=25.75 EndZ=0
    g40: LineSegment StartX=-49.19 StartY=23 StartZ=0 EndX=-11.49 EndY=23 EndZ=0
    g41: LineSegment StartX=-49.19 StartY=20 StartZ=0 EndX=-11.49 EndY=20 EndZ=0
    g42: LineSegment StartX=-49.19 StartY=17.25 StartZ=0 EndX=-1.5 EndY=17.25 EndZ=0
    g43: LineSegment StartX=-49.19 StartY=14.25 StartZ=0 EndX=-1.5 EndY=14.25 EndZ=0
    g44: LineSegment StartX=-49.19 StartY=11.5 StartZ=0 EndX=-1.5 EndY=11.5 EndZ=0
    g45: LineSegment StartX=-49.19 StartY=8.5 StartZ=0 EndX=-1.5 EndY=8.5 EndZ=0
    g46: LineSegment StartX=-49.19 StartY=5.75 StartZ=0 EndX=-1.5 EndY=5.75 EndZ=0
    g47: LineSegment StartX=-49.19 StartY=2.75 StartZ=0 EndX=-1.5 EndY=2.75 EndZ=0
  constraints (120):
    c: Vertical(g0)
    c: Distance(g0) = 3
    c: Block(g0)
    c: Vertical(g1)
    c: Distance(g1) = 3
    c: Vertical(g2)
    c: Equal(g0,g2) = 3
    c: Block(g2)
    c: Vertical(g3)
    c: Equal(g1,g3) = 3
    c: Vertical(g4)
    c: Equal(g0,g4) = 3
    c: Block(g4)
    c: Vertical(g5)
    c: Equal(g1,g5) = 3
    c: Vertical(g6)
    c: Equal(g0,g6) = 3
    c: Block(g6)
    c: Vertical(g7)
    c: Equal(g1,g7) = 3
    c: Vertical(g8)
    c: Equal(g0,g8) = 3
    c: Block(g8)
    c: Vertical(g9)
    c: Equal(g1,g9) = 3
    c: Vertical(g10)
    c: Equal(g0,g10) = 3
    c: Block(g10)
    c: Vertical(g11)
    c: Equal(g1,g11) = 3
    c: Block(g12)
    c: Block(g13)
    c: Block(g14)
    c: Block(g15)
    c: Block(g16)
    c: Block(g17)
    c: Block(g18)
    c: Block(g19)
    c: Block(g20)
    c: Block(g21)
    c: Block(g22)
    c: Block(g23)
    c: Block(g11)
    c: Block(g9)
    c: Block(g7)
    c: Block(g5)
    c: Block(g3)
    c: Block(g1)
    c: Coincident(g24,g0)
    c: Coincident(g24,g12)
    c: Horizontal(g24)
    c: Coincident(g25,g0)
    c: Coincident(g25,g12)
    c: Horizontal(g25)
    c: Coincident(g26,g1)
    c: Coincident(g26,g13)
    c: Horizontal(g26)
    c: Coincident(g27,g1)
    c: Coincident(g27,g13)
    c: Horizontal(g27)
    c: Coincident(g28,g2)
    c: Coincident(g28,g14)
    c: Horizontal(g28)
    c: Coincident(g29,g2)
    c: Coincident(g29,g14)
    c: Horizontal(g29)
    c: Coincident(g30,g3)
    c: Coincident(g30,g15)
    c: Horizontal(g30)
    c: Coincident(g31,g3)
    c: Coincident(g31,g15)
    c: Horizontal(g31)
    c: Coincident(g32,g4)
    c: Coincident(g32,g16)
    c: Horizontal(g32)
    c: Coincident(g33,g4)
    c: Coincident(g33,g16)
    c: Horizontal(g33)
    c: Coincident(g34,g5)
    c: Coincident(g34,g17)
    c: Horizontal(g34)
    c: Coincident(g35,g5)
    c: Coincident(g35,g17)
    c: Horizontal(g35)
    c: Coincident(g36,g6)
    c: Coincident(g36,g19)
    c: Horizontal(g36)
    c: Coincident(g37,g6)
    c: Coincident(g37,g19)
    c: Horizontal(g37)
    c: Coincident(g38,g7)
    c: Coincident(g38,g18)
    c: Horizontal(g38)
    c: Coincident(g39,g7)
    c: Coincident(g39,g18)
    c: Horizontal(g39)
    c: Coincident(g40,g8)
    c: Coincident(g40,g20)
    c: Horizontal(g40)
    c: Coincident(g41,g8)
    c: Coincident(g41,g20)
    c: Horizontal(g41)
    c: Coincident(g42,g9)
    c: Coincident(g42,g23)
    c: Horizontal(g42)
    c: Coincident(g43,g9)
    c: Coincident(g43,g23)
    c: Horizontal(g43)
    c: Coincident(g44,g10)
    c: Coincident(g44,g22)
    c: Horizontal(g44)
    c: Coincident(g45,g10)
    c: Coincident(g45,g22)
    c: Horizontal(g45)
    c: Coincident(g46,g11)
    c: Coincident(g46,g21)
    c: Horizontal(g46)
    c: Coincident(g47,g11)
    c: Coincident(g47,g21)
    c: Horizontal(g47)
FEATURE [Part::Extrusion] Extrude023
  Base = -> Sketch032
  Dir = (1,-2e-16,2e-16)
  DirMode = 2
  FaceMakerClass = Part::FaceMakerBullseye
  LengthFwd = 19
  LengthRev = 0
  Placement = pos=(-19,0,0) rot=(0,0,1;0rad)
  Solid = true
  Symmetric = false
FEATURE [Part::Fillet] Fillet023
  Base = -> Extrude023
  Edges = <same value as first occurrence — deduplicated (x6 in doc)>
  Placement = pos=(0,0.05,0) rot=(0,0,1;0rad)
FEATURE [Part::Cut] Cut014  label="bottom003"
  Base = -> Cut007
  Tool = -> Fusion047
FEATURE [Part::Cut] Cut021  label="bottom004"
  Base = -> Cut014
  Tool = -> Fillet023
FEATURE [Sketcher::SketchObject] Sketch033
  FullyConstrained = true
  Placement = pos=(117,19,0) rot=(0.57735,0.57735,0.57735;2.0944rad)
  sketch-geometry (8):
    g0: LineSegment StartX=-49.19 StartY=69.25 StartZ=0 EndX=-49.19 EndY=66.25 EndZ=0
    g1: LineSegment StartX=-49.19 StartY=5.75 StartZ=0 EndX=-49.19 EndY=2.75 EndZ=0
    g2: ArcOfCircle CenterX=-1.5 CenterY=67.75 CenterZ=0 NormalX=0 NormalY=0 NormalZ=1 AngleXU=0 Radius=1.5 StartAngle=4.71239 EndAngle=7.85398
    g3: ArcOfCircle CenterX=-1.5 CenterY=4.25 CenterZ=0 NormalX=0 NormalY=0 NormalZ=1 AngleXU=0 Radius=1.5 StartAngle=4.71239 EndAngle=7.85398
    g4: LineSegment StartX=-49.19 StartY=69.25 StartZ=0 EndX=-1.5 EndY=69.25 EndZ=0
    g5: LineSegment StartX=-49.19 StartY=66.25 StartZ=0 EndX=-1.5 EndY=66.25 EndZ=0
    g6: LineSegment StartX=-49.19 StartY=5.75 StartZ=0 EndX=-1.5 EndY=5.75 EndZ=0
    g7: LineSegment StartX=-49.19 StartY=2.75 StartZ=0 EndX=-1.5 EndY=2.75 EndZ=0
  constraints (19):
    c: Vertical(g0)
    c: Distance(g0) = 3
    c: Block(g0)
    c: Vertical(g1)
    c: Block(g2)
    c: Block(g3)
    c: Block(g1)
    c: Coincident(g4,g0)
    c: Coincident(g4,g2)
    c: Horizontal(g4)
    c: Coincident(g5,g0)
    c: Coincident(g5,g2)
    c: Horizontal(g5)
    c: Coincident(g6,g1)
    c: Coincident(g6,g3)
    c: Horizontal(g6)
    c: Coincident(g7,g1)
    c: Coincident(g7,g3)
    c: Horizontal(g7)
FEATURE [Sketcher::SketchObject] Sketch034
  FullyConstrained = true
  Placement = pos=(117,19,0) rot=(0.57735,0.57735,0.57735;2.0944rad)
  sketch-geometry (8):
    g0: LineSegment StartX=-49.19 StartY=63.5 StartZ=0 EndX=-49.19 EndY=60.5 EndZ=0
    g1: LineSegment StartX=-49.19 StartY=11.5 StartZ=0 EndX=-49.19 EndY=8.5 EndZ=0
    g2: ArcOfCircle CenterX=-1.5 CenterY=62 CenterZ=0 NormalX=0 NormalY=0 NormalZ=1 AngleXU=0 Radius=1.5 StartAngle=4.71239 EndAngle=7.85398
    g3: ArcOfCircle CenterX=-1.5 CenterY=10 CenterZ=0 NormalX=0 NormalY=0 NormalZ=1 AngleXU=0 Radius=1.5 StartAngle=4.71239 EndAngle=7.85398
    g4: LineSegment StartX=-49.19 StartY=63.5 StartZ=0 EndX=-1.5 EndY=63.5 EndZ=0
    g5: LineSegment StartX=-49.19 StartY=60.5 StartZ=0 EndX=-1.5 EndY=60.5 EndZ=0
    g6: LineSegment StartX=-49.19 StartY=11.5 StartZ=0 EndX=-1.5 EndY=11.5 EndZ=0
    g7: LineSegment StartX=-49.19 StartY=8.5 StartZ=0 EndX=-1.5 EndY=8.5 EndZ=0
  constraints (19):
    c: Vertical(g0)
    c: Distance(g0) = 3
    c: Vertical(g1)
    c: Block(g1)
    c: Block(g2)
    c: Block(g3)
    c: Block(g0)
    c: Coincident(g4,g0)
    c: Coincident(g4,g2)
    c: Horizontal(g4)
    c: Coincident(g5,g0)
    c: Coincident(g5,g2)
    c: Horizontal(g5)
    c: Coincident(g6,g1)
    c: Coincident(g6,g3)
    c: Horizontal(g6)
    c: Coincident(g7,g1)
    c: Coincident(g7,g3)
    c: Horizontal(g7)
FEATURE [Part::Extrusion] Extrude024
  Base = -> Sketch033
  Dir = (1,0,0)
  DirMode = 2
  FaceMakerClass = Part::FaceMakerBullseye
  LengthFwd = 10
  LengthRev = 0
  Solid = true
  Symmetric = false
FEATURE [Part::Extrusion] Extrude025
  Base = -> Sketch034
  Dir = (1,0,0)
  DirMode = 2
  FaceMakerClass = Part::FaceMakerBullseye
  LengthFwd = 10
  LengthRev = 0
  Solid = true
  Symmetric = false
FEATURE [Part::Fillet] Fillet024  label="removeFromtMoreFrontCaseScrewRetainers"
  Base = -> Extrude024
  Edges = 4 edges r=1.49: [Edge6,Edge11,Edge18,Edge23]
  Placement = pos=(-11,0,0) rot=(0,0,1;0rad)
FEATURE [Part::Fillet] Fillet025  label="removeFromtMoreFrontCaseScrewRetainers001"
  Base = -> Extrude025
  Edges = 4 edges r=1.49: [Edge6,Edge11,Edge18,Edge23]
  Placement = pos=(-19,0,0) rot=(0,0,1;0rad)
FEATURE [Part::Cut] Cut022
  Base = -> Cut015
  Tool = -> Fillet025
FEATURE [Part::Cut] Cut023  label="screwRetainers"
  Base = -> Cut022
  Tool = -> Fillet024
FEATURE [Part::MultiFuse] Fusion056  label="bottom005"
  Shapes = -> [Fusion044,Cut021]
FEATURE [Part::MultiFuse] Fusion057  label="casePillars001"
  Shapes = -> [Cut016,Fusion052]
FEATURE [Part::MultiFuse] Fusion058  label="bottom006"
  Shapes = -> [Fusion056,Cut023]
FEATURE [Part::MultiFuse] Fusion059  label="bottom007"
  Shapes = -> [Fusion058,Fillet005]
FEATURE [Part::MultiFuse] Fusion060  label="bottom008"
  Shapes = -> [Fusion059,Fusion]
FEATURE [Part::MultiFuse] Fusion061  label="top011"
  Shapes = -> [Cut006,Cut020]
FEATURE [Part::MultiFuse] Fusion062  label="top012"
  Shapes = -> [Fusion057,Fusion061]
FEATURE [Sketcher::SketchObject] Sketch035  label="topSketch007"
  FullyConstrained = true
  sketch-geometry (6):
    g0: LineSegment StartX=19 StartY=38 StartZ=0 EndX=117 EndY=38 EndZ=0
    g1: ArcOfCircle CenterX=19 CenterY=19 CenterZ=0 NormalX=0 NormalY=0 NormalZ=1 AngleXU=0 Radius=19 StartAngle=1.5708 EndAngle=3.14159
    g2: LineSegment StartX=117 StartY=38 StartZ=0 EndX=117 EndY=19 EndZ=0
    g3: LineSegment StartX=98 StartY=1.0161e-12 StartZ=0 EndX=5.22862e-06 EndY=1.0161e-12 EndZ=0
    g4: LineSegment StartX=5.22862e-06 StartY=19 StartZ=0 EndX=5.22862e-06 EndY=1.0161e-12 EndZ=0
    g5: ArcOfCircle CenterX=98 CenterY=19 CenterZ=0 NormalX=0 NormalY=0 NormalZ=1 AngleXU=0 Radius=19 StartAngle=4.71239 EndAngle=6.28319
  constraints (16):
    c: Horizontal(g0)
    c: Distance(g0) = 98
    c: Coincident(g1,g0)
    c: Block(g1)
    c: Coincident(g2,g0)
    c: Vertical(g2)
    c: Distance(g2) = 19
    c: Horizontal(g3)
    c: Coincident(g4,g1)
    c: Vertical(g4)
    c: Coincident(g3,g4)
    c: Block(g3)
    c: Coincident(g5,g2)
    c: Coincident(g5,g3)
    c: Block(g0)
    c: Block(g5)
FEATURE [Part::Extrusion] Extrude026  label="sideA001"
  Base = -> Sketch035
  Dir = (0,0,1)
  DirMode = 2
  FaceMakerClass = Part::FaceMakerBullseye
  LengthFwd = 3
  LengthRev = 0
  Placement = pos=(0,0,-2.7) rot=(0,0,1;0rad)
  Solid = true
  Symmetric = false
FEATURE [Sketcher::SketchObject] Sketch036  label="topSketch008"
  FullyConstrained = true
  sketch-geometry (6):
    g0: LineSegment StartX=19 StartY=38 StartZ=0 EndX=117 EndY=38 EndZ=0
    g1: ArcOfCircle CenterX=19 CenterY=19 CenterZ=0 NormalX=0 NormalY=0 NormalZ=1 AngleXU=0 Radius=19 StartAngle=1.5708 EndAngle=3.14159
    g2: LineSegment StartX=117 StartY=38 StartZ=0 EndX=117 EndY=19 EndZ=0
    g3: LineSegment StartX=98 StartY=1.0161e-12 StartZ=0 EndX=5.22862e-06 EndY=1.0161e-12 EndZ=0
    g4: LineSegment StartX=5.22862e-06 StartY=19 StartZ=0 EndX=5.22862e-06 EndY=1.0161e-12 EndZ=0
    g5: ArcOfCircle CenterX=98 CenterY=19 CenterZ=0 NormalX=0 NormalY=0 NormalZ=1 AngleXU=0 Radius=19 StartAngle=4.71239 EndAngle=6.28319
  constraints (16):
    c: Horizontal(g0)
    c: Distance(g0) = 98
    c: Coincident(g1,g0)
    c: Block(g1)
    c: Coincident(g2,g0)
    c: Vertical(g2)
    c: Distance(g2) = 19
    c: Horizontal(g3)
    c: Coincident(g4,g1)
    c: Vertical(g4)
    c: Coincident(g3,g4)
    c: Block(g3)
    c: Coincident(g5,g2)
    c: Coincident(g5,g3)
    c: Block(g0)
    c: Block(g5)
FEATURE [Part::Extrusion] Extrude027  label="sideB001"
  Base = -> Sketch036
  Dir = (0,0,1)
  DirMode = 2
  FaceMakerClass = Part::FaceMakerBullseye
  LengthFwd = 3
  LengthRev = 0
  Placement = pos=(0,0,71.7) rot=(0,0,1;0rad)
  Solid = true
  Symmetric = false
FEATURE [Part::MultiFuse] Fusion064  label="removeFromBottom"
  Shapes = -> [Extrude026,Extrude027]
FEATURE [Part::Cut] Cut024  label="bottom009"
  Base = -> Fusion060
  Tool = -> Fusion064
FEATURE [Sketcher::SketchObject] Sketch037  label="topSketch009"
  FullyConstrained = true
  sketch-geometry (8):
    g0: ArcOfCircle CenterX=19 CenterY=19.1201 CenterZ=0 NormalX=0 NormalY=0 NormalZ=1 AngleXU=0 Radius=18.8799 StartAngle=1.5708 EndAngle=3.14793
    g1: LineSegment StartX=0.120501 StartY=19.0004 StartZ=0 EndX=0.120501 EndY=0.000382114 EndZ=0
    g2: LineSegment StartX=19 StartY=38 StartZ=0 EndX=124 EndY=38 EndZ=0
    g3: LineSegment StartX=0.120501 StartY=0.000382114 StartZ=0 EndX=105.121 EndY=0.000382114 EndZ=0
    g4: LineSegment StartX=124 StartY=38 StartZ=0 EndX=125.616 EndY=38 EndZ=0
    g5: LineSegment StartX=105.121 StartY=0.000382114 StartZ=0 EndX=106.736 EndY=0.000382114 EndZ=0
    g6: ArcOfCircle CenterX=106.616 CenterY=19 CenterZ=0 NormalX=0 NormalY=0 NormalZ=1 AngleXU=0 Radius=19 StartAngle=4.71873 EndAngle=6.28319
    g7: LineSegment StartX=125.616 StartY=38 StartZ=0 EndX=125.616 EndY=19 EndZ=0
  constraints (21):
    c: Block(g0)
    c: Coincident(g1,g0)
    c: Vertical(g1)
    c: Horizontal(g2)
    c: Distance(g2) = 105
    c: Coincident(g2,g0)
    c: Distance(g1) = 19
    c: Coincident(g3,g1)
    c: Horizontal(g3)
    c: Distance(g3) = 105
    c: Coincident(g4,g2)
    c: Horizontal(g4)
    c: Distance(g4) = 1.61553
    c: Horizontal(g5)
    c: Equal(g4,g5) = 1.61553
    c: Coincident(g5,g3)
    c: Block(g6)
    c: Coincident(g6,g5)
    c: Coincident(g7,g4)
    c: Coincident(g7,g6)
    c: Vertical(g7)
FEATURE [Part::Extrusion] Extrude028  label="sideB"
  Base = -> Sketch037
  Dir = (0,0,1)
  DirMode = 2
  FaceMakerClass = Part::FaceMakerBullseye
  LengthFwd = 3
  LengthRev = 0
  Placement = pos=(0,0,72) rot=(0,0,1;0rad)
  Solid = true
  Symmetric = false
FEATURE [Sketcher::SketchObject] Sketch038  label="topSketch010"
  FullyConstrained = true
  sketch-geometry (22):
    g0: LineSegment StartX=5.21097e-06 StartY=3 StartZ=0 EndX=5.21097e-06 EndY=19 EndZ=0
    g1: ArcOfCircle CenterX=19 CenterY=19 CenterZ=0 NormalX=0 NormalY=0 NormalZ=1 AngleXU=0 Radius=19 StartAngle=1.5708 EndAngle=3.14159
    g2: ArcOfCircle CenterX=19 CenterY=19 CenterZ=0 NormalX=0 NormalY=0 NormalZ=1 AngleXU=0 Radius=16 StartAngle=1.5708 EndAngle=3.14159
    g3: LineSegment StartX=114 StartY=35 StartZ=0 EndX=19 EndY=35 EndZ=0
    g4: LineSegment StartX=5.21097e-06 StartY=3 StartZ=0 EndX=5.21097e-06 EndY=0 EndZ=0
    g5: LineSegment StartX=3 StartY=0 StartZ=0 EndX=5.21097e-06 EndY=0 EndZ=0
    g6: LineSegment StartX=3 StartY=19 StartZ=0 EndX=3 EndY=0 EndZ=0
    g7: LineSegment StartX=19 StartY=38 StartZ=0 EndX=124 EndY=38 EndZ=0
    g8: Circle CenterX=119 CenterY=35 CenterZ=0 NormalX=0 NormalY=0 NormalZ=1 AngleXU=0 Radius=1
    g9: Circle CenterX=121 CenterY=35 CenterZ=0 NormalX=0 NormalY=0 NormalZ=1 AngleXU=0 Radius=1
    g10: Circle CenterX=121 CenterY=33 CenterZ=0 NormalX=0 NormalY=0 NormalZ=1 AngleXU=0 Radius=1
    g11: BSplineCurve PolesCount=3 KnotsCount=2 Degree=2 IsPeriodic=0
    g12: GeomPoint X=119 Y=35 Z=0
    g13: GeomPoint X=121 Y=33 Z=0
    g14: LineSegment StartX=119 StartY=35 StartZ=0 EndX=114 EndY=35 EndZ=0
    g15: ArcOfCircle CenterX=105 CenterY=19 CenterZ=0 NormalX=0 NormalY=0 NormalZ=1 AngleXU=0 Radius=16 StartAngle=5.60905 EndAngle=6.28319
    g16: LineSegment StartX=121 StartY=33 StartZ=0 EndX=121 EndY=19 EndZ=0
    g17: LineSegment StartX=117.5 StartY=9.01251 StartZ=0 EndX=121.163 EndY=9.0125 EndZ=0
    g18: ArcOfCircle CenterX=105 CenterY=19 CenterZ=0 NormalX=0 NormalY=0 NormalZ=1 AngleXU=0 Radius=20.6155 StartAngle=5.7297 EndAngle=6.28319
    g19: LineSegment StartX=121.163 StartY=9.0125 StartZ=0 EndX=122.538 EndY=8.16329 EndZ=0
    g20: LineSegment StartX=124 StartY=38 StartZ=0 EndX=125.616 EndY=38 EndZ=0
    g21: LineSegment StartX=125.616 StartY=19 StartZ=0 EndX=125.616 EndY=38 EndZ=0
  constraints (49):
    c: Vertical(g0)
    c: Block(g0)
    c: Coincident(g1,g0)
    c: Block(g1)
    c: Coincident(g2,g1)
    c: Block(g2)
    c: Coincident(g3,g2)
    c: Horizontal(g3)
    c: Tangent(g3,g2)
    c: Coincident(g4,g0)
    c: Distance(g4) = 3
    c: Vertical(g4)
    c: Coincident(g5,g4)
    c: Horizontal(g5)
    c: Coincident(g6,g2)
    c: Coincident(g6,g5)
    c: Vertical(g6)
    c: Horizontal(g7)
    c: Distance(g7) = 105
    c: Coincident(g7,g1)
    c: Block(g3)
    c: Weight(g8) = 1
    c: Equal(g8,g9)
    c: Equal(g8,g10)
    c: InternalAlignment(g8,g11)
    c: InternalAlignment(g9,g11)
    c: InternalAlignment(g10,g11)
    c: InternalAlignment(g12,g11)
    c: InternalAlignment(g13,g11)
    c: Block(g11)
    c: Coincident(g14,g11)
    c: Coincident(g14,g3)
    c: Horizontal(g14)
    c: Block(g15)
    c: Coincident(g16,g11)
    c: Coincident(g16,g15)
    c: Vertical(g16)
    c: Distance(g16) = 14
    c: Coincident(g17,g15)
    c: Block(g18)
    c: Coincident(g19,g18)
    c: Coincident(g20,g7)
    c: Horizontal(g20)
    c: Vertical(g21)
    c: Coincident(g20,g21)
    c: Block(g20)
    c: Block(g21)
    c: Block(g19)
    c: Block(g17)
FEATURE [Part::Extrusion] Extrude029
  Base = -> Sketch038
  Dir = (0,0,1)
  DirMode = 2
  FaceMakerClass = Part::FaceMakerBullseye
  LengthFwd = 72
  LengthRev = 0
  Solid = true
  Symmetric = false
FEATURE [Part::Feature] Face085
  shape: bbox 4.8 x 25.5 x 2e-07 mm, 1 faces, 0 solids (baked)
FEATURE [Part::Revolution] Revolve089  label="moreFrontCaseScrewPost003"
  Angle = 360
  Axis = (0,1,0)
  Base = (0,0,0)
  FaceMakerClass = Part::FaceMakerBullseye
  Placement = pos=(109.5,4.5,3.5) rot=(0,0,1;0rad)
  Solid = false
  Source = -> Face085
  Symmetric = false
FEATURE [Part::Feature] Face086
  shape: bbox 4.8 x 25.5 x 2e-07 mm, 1 faces, 0 solids (baked)
FEATURE [Part::Revolution] Revolve090  label="moreFrontCaseScrewPost004"
  Angle = 360
  Axis = (0,1,0)
  Base = (0,0,0)
  FaceMakerClass = Part::FaceMakerBullseye
  Placement = pos=(109.5,4.5,68.5) rot=(0,0,1;0rad)
  Solid = false
  Source = -> Face086
  Symmetric = false
FEATURE [Part::Fillet] Fillet026  label="top013"
  Base = -> Extrude029
  Edges = 1 edges r=2: [Edge35]
FEATURE [Sketcher::SketchObject] Sketch039
  FullyConstrained = true
  sketch-geometry (7):
    g0: LineSegment StartX=0 StartY=0 StartZ=0 EndX=0 EndY=6 EndZ=0
    g1: Circle CenterX=0 CenterY=0 CenterZ=0 NormalX=0 NormalY=0 NormalZ=1 AngleXU=0 Radius=1
    g2: Circle CenterX=8 CenterY=6 CenterZ=0 NormalX=0 NormalY=0 NormalZ=1 AngleXU=0 Radius=1
    g3: BSplineCurve PolesCount=3 KnotsCount=2 Degree=2 IsPeriodic=0
    g4: GeomPoint X=0 Y=0 Z=0
    g5: GeomPoint X=8 Y=6 Z=0
    g6: LineSegment StartX=0 StartY=6 StartZ=0 EndX=8 EndY=6 EndZ=0
  constraints (14):
    c: Coincident(g0,g-1)
    c: Distance(g0) = 6
    c: Vertical(g0)
    c: Coincident(g3,g0)
    c: Weight(g1) = 1
    c: Equal(g1,g2)
    c: InternalAlignment(g1,g3)
    c: InternalAlignment(g2,g3)
    c: InternalAlignment(g4,g3)
    c: InternalAlignment(g5,g3)
    c: Block(g3)
    c: Coincident(g6,g0)
    c: Coincident(g6,g3)
    c: Horizontal(g6)
FEATURE [Sketcher::SketchObject] Sketch040
  FullyConstrained = true
  sketch-geometry (7):
    g0: LineSegment StartX=0 StartY=0 StartZ=0 EndX=0 EndY=6 EndZ=0
    g1: Circle CenterX=0 CenterY=0 CenterZ=0 NormalX=0 NormalY=0 NormalZ=1 AngleXU=0 Radius=1
    g2: Circle CenterX=8 CenterY=6 CenterZ=0 NormalX=0 NormalY=0 NormalZ=1 AngleXU=0 Radius=1
    g3: BSplineCurve PolesCount=3 KnotsCount=2 Degree=2 IsPeriodic=0
    g4: GeomPoint X=0 Y=0 Z=0
    g5: GeomPoint X=8 Y=6 Z=0
    g6: LineSegment StartX=0 StartY=6 StartZ=0 EndX=8 EndY=6 EndZ=0
  constraints (14):
    c: Coincident(g0,g-1)
    c: Distance(g0) = 6
    c: Vertical(g0)
    c: Coincident(g3,g0)
    c: Weight(g1) = 1
    c: Equal(g1,g2)
    c: InternalAlignment(g1,g3)
    c: InternalAlignment(g2,g3)
    c: InternalAlignment(g4,g3)
    c: InternalAlignment(g5,g3)
    c: Block(g3)
    c: Coincident(g6,g0)
    c: Coincident(g6,g3)
    c: Horizontal(g6)
FEATURE [Sketcher::SketchObject] Sketch041
  FullyConstrained = true
  sketch-geometry (7):
    g0: LineSegment StartX=0 StartY=0 StartZ=0 EndX=0 EndY=6 EndZ=0
    g1: Circle CenterX=0 CenterY=0 CenterZ=0 NormalX=0 NormalY=0 NormalZ=1 AngleXU=0 Radius=1
    g2: Circle CenterX=8 CenterY=6 CenterZ=0 NormalX=0 NormalY=0 NormalZ=1 AngleXU=0 Radius=1
    g3: BSplineCurve PolesCount=3 KnotsCount=2 Degree=2 IsPeriodic=0
    g4: GeomPoint X=0 Y=0 Z=0
    g5: GeomPoint X=8 Y=6 Z=0
    g6: LineSegment StartX=0 StartY=6 StartZ=0 EndX=8 EndY=6 EndZ=0
  constraints (14):
    c: Coincident(g0,g-1)
    c: Distance(g0) = 6
    c: Vertical(g0)
    c: Coincident(g3,g0)
    c: Weight(g1) = 1
    c: Equal(g1,g2)
    c: InternalAlignment(g1,g3)
    c: InternalAlignment(g2,g3)
    c: InternalAlignment(g4,g3)
    c: InternalAlignment(g5,g3)
    c: Block(g3)
    c: Coincident(g6,g0)
    c: Coincident(g6,g3)
    c: Horizontal(g6)
FEATURE [Sketcher::SketchObject] Sketch042
  FullyConstrained = true
  sketch-geometry (7):
    g0: LineSegment StartX=0 StartY=0 StartZ=0 EndX=0 EndY=6 EndZ=0
    g1: Circle CenterX=0 CenterY=0 CenterZ=0 NormalX=0 NormalY=0 NormalZ=1 AngleXU=0 Radius=1
    g2: Circle CenterX=8 CenterY=6 CenterZ=0 NormalX=0 NormalY=0 NormalZ=1 AngleXU=0 Radius=1
    g3: BSplineCurve PolesCount=3 KnotsCount=2 Degree=2 IsPeriodic=0
    g4: GeomPoint X=0 Y=0 Z=0
    g5: GeomPoint X=8 Y=6 Z=0
    g6: LineSegment StartX=0 StartY=6 StartZ=0 EndX=8 EndY=6 EndZ=0
  constraints (14):
    c: Coincident(g0,g-1)
    c: Distance(g0) = 6
    c: Vertical(g0)
    c: Coincident(g3,g0)
    c: Weight(g1) = 1
    c: Equal(g1,g2)
    c: InternalAlignment(g1,g3)
    c: InternalAlignment(g2,g3)
    c: InternalAlignment(g4,g3)
    c: InternalAlignment(g5,g3)
    c: Block(g3)
    c: Coincident(g6,g0)
    c: Coincident(g6,g3)
    c: Horizontal(g6)
FEATURE [Part::Extrusion] Extrude030  label="caseScrewPillarBracket008"
  Base = -> Sketch039
  Dir = (0,0,1)
  DirMode = 2
  FaceMakerClass = Part::FaceMakerBullseye
  LengthFwd = 2.4
  LengthRev = 0
  Placement = pos=(15.76,29,8.8) rot=(0,1,0;0rad)
  Solid = true
  Symmetric = false
FEATURE [Part::Extrusion] Extrude031  label="caseScrewPillarBracket009"
  Base = -> Sketch040
  Dir = (0,0,1)
  DirMode = 2
  FaceMakerClass = Part::FaceMakerBullseye
  LengthFwd = 2.4
  LengthRev = 0
  Placement = pos=(15.76,29,60.8) rot=(0,0,1;0rad)
  Solid = true
  Symmetric = false
FEATURE [Part::Extrusion] Extrude032  label="caseScrewPillarBracket010"
  Base = -> Sketch041
  Dir = (0,0,1)
  DirMode = 2
  FaceMakerClass = Part::FaceMakerBullseye
  LengthFwd = 2.4
  LengthRev = 0
  Placement = pos=(13.7,29,13.26) rot=(0,-1,0;1.5708rad)
  Solid = true
  Symmetric = false
FEATURE [Part::Extrusion] Extrude033  label="caseScrewPillarBracket011"
  Base = -> Sketch042
  Dir = (0,0,1)
  DirMode = 2
  FaceMakerClass = Part::FaceMakerBullseye
  LengthFwd = 2.4
  LengthRev = 0
  Placement = pos=(11.3,29,58.74) rot=(0,1,0;1.5708rad)
  Solid = true
  Symmetric = false
FEATURE [Sketcher::SketchObject] Sketch043
  FullyConstrained = true
  sketch-geometry (7):
    g0: LineSegment StartX=0 StartY=0 StartZ=0 EndX=0 EndY=6 EndZ=0
    g1: Circle CenterX=0 CenterY=0 CenterZ=0 NormalX=0 NormalY=0 NormalZ=1 AngleXU=0 Radius=1
    g2: Circle CenterX=8 CenterY=6 CenterZ=0 NormalX=0 NormalY=0 NormalZ=1 AngleXU=0 Radius=1
    g3: BSplineCurve PolesCount=3 KnotsCount=2 Degree=2 IsPeriodic=0
    g4: GeomPoint X=0 Y=0 Z=0
    g5: GeomPoint X=8 Y=6 Z=0
    g6: LineSegment StartX=0 StartY=6 StartZ=0 EndX=8 EndY=6 EndZ=0
  constraints (14):
    c: Coincident(g0,g-1)
    c: Distance(g0) = 6
    c: Vertical(g0)
    c: Coincident(g3,g0)
    c: Weight(g1) = 1
    c: Equal(g1,g2)
    c: InternalAlignment(g1,g3)
    c: InternalAlignment(g2,g3)
    c: InternalAlignment(g4,g3)
    c: InternalAlignment(g5,g3)
    c: Block(g3)
    c: Coincident(g6,g0)
    c: Coincident(g6,g3)
    c: Horizontal(g6)
FEATURE [Part::Extrusion] Extrude034  label="caseScrewPillarBracket012"
  Base = -> Sketch043
  Dir = (0,0,1)
  DirMode = 2
  FaceMakerClass = Part::FaceMakerBullseye
  LengthFwd = 2.4
  LengthRev = 0
  Placement = pos=(88.3,29,65.23) rot=(0,1,0;1.5708rad)
  Solid = true
  Symmetric = false
FEATURE [Sketcher::SketchObject] Sketch044
  FullyConstrained = true
  sketch-geometry (7):
    g0: LineSegment StartX=0 StartY=0 StartZ=0 EndX=0 EndY=6 EndZ=0
    g1: Circle CenterX=0 CenterY=0 CenterZ=0 NormalX=0 NormalY=0 NormalZ=1 AngleXU=0 Radius=1
    g2: Circle CenterX=8 CenterY=6 CenterZ=0 NormalX=0 NormalY=0 NormalZ=1 AngleXU=0 Radius=1
    g3: BSplineCurve PolesCount=3 KnotsCount=2 Degree=2 IsPeriodic=0
    g4: GeomPoint X=0 Y=0 Z=0
    g5: GeomPoint X=8 Y=6 Z=0
    g6: LineSegment StartX=0 StartY=6 StartZ=0 EndX=8 EndY=6 EndZ=0
  constraints (14):
    c: Coincident(g0,g-1)
    c: Distance(g0) = 6
    c: Vertical(g0)
    c: Coincident(g3,g0)
    c: Weight(g1) = 1
    c: Equal(g1,g2)
    c: InternalAlignment(g1,g3)
    c: InternalAlignment(g2,g3)
    c: InternalAlignment(g4,g3)
    c: InternalAlignment(g5,g3)
    c: Block(g3)
    c: Coincident(g6,g0)
    c: Coincident(g6,g3)
    c: Horizontal(g6)
FEATURE [Part::Extrusion] Extrude035  label="caseScrewPillarBracket013"
  Base = -> Sketch044
  Dir = (0,0,1)
  DirMode = 2
  FaceMakerClass = Part::FaceMakerBullseye
  LengthFwd = 2.4
  LengthRev = 0
  Placement = pos=(90.7,29,6.77) rot=(0,-1,0;1.5708rad)
  Solid = true
  Symmetric = false
FEATURE [Sketcher::SketchObject] Sketch045
  FullyConstrained = true
  sketch-geometry (7):
    g0: LineSegment StartX=0 StartY=0 StartZ=0 EndX=0 EndY=6 EndZ=0
    g1: Circle CenterX=0 CenterY=0 CenterZ=0 NormalX=0 NormalY=0 NormalZ=1 AngleXU=0 Radius=1
    g2: Circle CenterX=8 CenterY=6 CenterZ=0 NormalX=0 NormalY=0 NormalZ=1 AngleXU=0 Radius=1
    g3: BSplineCurve PolesCount=3 KnotsCount=2 Degree=2 IsPeriodic=0
    g4: GeomPoint X=0 Y=0 Z=0
    g5: GeomPoint X=8 Y=6 Z=0
    g6: LineSegment StartX=0 StartY=6 StartZ=0 EndX=8 EndY=6 EndZ=0
  constraints (14):
    c: Coincident(g0,g-1)
    c: Distance(g0) = 6
    c: Vertical(g0)
    c: Coincident(g3,g0)
    c: Weight(g1) = 1
    c: Equal(g1,g2)
    c: InternalAlignment(g1,g3)
    c: InternalAlignment(g2,g3)
    c: InternalAlignment(g4,g3)
    c: InternalAlignment(g5,g3)
    c: Block(g3)
    c: Coincident(g6,g0)
    c: Coincident(g6,g3)
    c: Horizontal(g6)
FEATURE [Sketcher::SketchObject] Sketch046
  FullyConstrained = true
  sketch-geometry (7):
    g0: LineSegment StartX=0 StartY=0 StartZ=0 EndX=0 EndY=6 EndZ=0
    g1: Circle CenterX=0 CenterY=0 CenterZ=0 NormalX=0 NormalY=0 NormalZ=1 AngleXU=0 Radius=1
    g2: Circle CenterX=8 CenterY=6 CenterZ=0 NormalX=0 NormalY=0 NormalZ=1 AngleXU=0 Radius=1
    g3: BSplineCurve PolesCount=3 KnotsCount=2 Degree=2 IsPeriodic=0
    g4: GeomPoint X=0 Y=0 Z=0
    g5: GeomPoint X=8 Y=6 Z=0
    g6: LineSegment StartX=0 StartY=6 StartZ=0 EndX=8 EndY=6 EndZ=0
  constraints (14):
    c: Coincident(g0,g-1)
    c: Distance(g0) = 6
    c: Vertical(g0)
    c: Coincident(g3,g0)
    c: Weight(g1) = 1
    c: Equal(g1,g2)
    c: InternalAlignment(g1,g3)
    c: InternalAlignment(g2,g3)
    c: InternalAlignment(g4,g3)
    c: InternalAlignment(g5,g3)
    c: Block(g3)
    c: Coincident(g6,g0)
    c: Coincident(g6,g3)
    c: Horizontal(g6)
FEATURE [Part::Extrusion] Extrude036  label="caseScrewPillarBracket014"
  Base = -> Sketch045
  Dir = (0,0,1)
  DirMode = 2
  FaceMakerClass = Part::FaceMakerBullseye
  LengthFwd = 2.4
  LengthRev = 0
  Placement = pos=(110.7,29,6.77) rot=(0,-1,0;1.5708rad)
  Solid = true
  Symmetric = false
FEATURE [Part::Extrusion] Extrude037  label="caseScrewPillarBracket015"
  Base = -> Sketch046
  Dir = (0,0,1)
  DirMode = 2
  FaceMakerClass = Part::FaceMakerBullseye
  LengthFwd = 2.4
  LengthRev = 0
  Placement = pos=(108.3,29,65.23) rot=(0,1,0;1.5708rad)
  Solid = true
  Symmetric = false
FEATURE [Part::Box] Box013  label="frontCaseScrewPillarBracket002"
  AttacherType = Attacher::AttachEngine3D
  Height = 2.4
  Length = 22
  Placement = pos=(87,28,2.3) rot=(0,0,1;0rad)
  Width = 7
FEATURE [Part::Box] Box014  label="frontCaseScrewPillarBracket003"
  AttacherType = Attacher::AttachEngine3D
  Height = 2.4
  Length = 22
  Placement = pos=(87,28,67.3) rot=(0,0,1;0rad)
  Width = 7
FEATURE [Part::Feature] Face087
  shape: bbox 4.8 x 30.2 x 2e-07 mm, 1 faces, 0 solids (baked)
FEATURE [Part::Revolution] Revolve091  label="frontCaseScrewPost004"
  Angle = 360
  Axis = (0,1,0)
  Base = (0,0,0)
  FaceMakerClass = Part::FaceMakerBullseye
  Placement = pos=(89.5,4.5,3.5) rot=(0,0,1;0rad)
  Solid = false
  Source = -> Face087
  Symmetric = false
FEATURE [Part::Feature] Face088
  shape: bbox 4.8 x 30.2 x 2e-07 mm, 1 faces, 0 solids (baked)
FEATURE [Part::Revolution] Revolve092  label="frontCaseScrewPost005"
  Angle = 360
  Axis = (0,1,0)
  Base = (0,0,0)
  FaceMakerClass = Part::FaceMakerBullseye
  Placement = pos=(89.5,4.5,68.5) rot=(0,0,1;0rad)
  Solid = false
  Source = -> Face088
  Symmetric = false
FEATURE [Part::Feature] Face089
  shape: bbox 3.5 x 30.2 x 2e-07 mm, 1 faces, 0 solids (baked)
FEATURE [Part::Revolution] Revolve093  label="backCaseScrewPost002"
  Angle = 360
  Axis = (0,1,0)
  Base = (0,0,0)
  FaceMakerClass = Part::FaceMakerBullseye
  Placement = pos=(12.5,4.5,10) rot=(0,0,1;0rad)
  Solid = false
  Source = -> Face089
  Symmetric = false
FEATURE [Part::Feature] Face090
  shape: bbox 3.5 x 30.2 x 2e-07 mm, 1 faces, 0 solids (baked)
FEATURE [Part::Revolution] Revolve094  label="backCaseScrewPost003"
  Angle = 360
  Axis = (0,1,0)
  Base = (0,0,0)
  FaceMakerClass = Part::FaceMakerBullseye
  Placement = pos=(12.5,4.5,62) rot=(0,0,1;0rad)
  Solid = false
  Source = -> Face090
  Symmetric = false
FEATURE [Part::Box] Box015  label="Cube011"
  AttacherType = Attacher::AttachEngine3D
  Height = 28.8
  Length = 3
  Placement = pos=(107.3,28,21.6) rot=(0,0,1;0rad)
  Width = 7
FEATURE [Part::Box] Box016  label="Cube012"
  AttacherType = Attacher::AttachEngine3D
  Height = 3
  Length = 7.4
  Placement = pos=(107.3,28,18.6) rot=(0,0,1;0rad)
  Width = 7
FEATURE [Part::Box] Box017  label="Cube013"
  AttacherType = Attacher::AttachEngine3D
  Height = 3
  Length = 7.4
  Placement = pos=(107.3,28,50.4) rot=(0,0,1;0rad)
  Width = 7
FEATURE [Part::Cylinder] Cylinder024
  Angle = 360
  AttacherType = Attacher::AttachEngine3D
  Height = 20
  Placement = pos=(0,0,36.15) rot=(0,0,1;0rad)
  Radius = 14.3
FEATURE [Part::Cylinder] Cylinder025
  Angle = 360
  AttacherType = Attacher::AttachEngine3D
  Height = 10
  Placement = pos=(0,0,36.15) rot=(0,0,1;0rad)
  Radius = 4
FEATURE [Part::MultiFuse] Fusion066  label="removeToCreteHoleForPlugHousing009"
  Placement = pos=(70,19,36) rot=(0,1,0;1.5708rad)
  Shapes = -> [Cylinder024,Cylinder025]
FEATURE [Part::MultiFuse] Fusion065  label="plugHousingBracketHolder002"
  Shapes = -> [Box017,Box015,Box016]
FEATURE [Part::Cut] Cut025  label="plugHousingBracketHolder003"
  Base = -> Fusion065
  Placement = pos=(7,0,0) rot=(0,0,1;0rad)
  Tool = -> Fusion066
FEATURE [Sketcher::SketchObject] Sketch047
  FullyConstrained = false
  Placement = pos=(0,0,0) rot=(1,0,0;1.5708rad)
  sketch-geometry (24):
    g0: ArcOfCircle CenterX=-4 CenterY=-10.5 CenterZ=0 NormalX=0 NormalY=0 NormalZ=1 AngleXU=0 Radius=1.5 StartAngle=6e-16 EndAngle=3.14159
    g1: ArcOfCircle CenterX=-34.2 CenterY=-10.5 CenterZ=0 NormalX=0 NormalY=0 NormalZ=1 AngleXU=0 Radius=1.5 StartAngle=0 EndAngle=3.14159
    g2: ArcOfCircle CenterX=-34.2 CenterY=-27.7 CenterZ=0 NormalX=0 NormalY=0 NormalZ=1 AngleXU=0 Radius=1.5 StartAngle=3.14159 EndAngle=6.28319
    g3: ArcOfCircle CenterX=-4 CenterY=-27.7 CenterZ=0 NormalX=0 NormalY=0 NormalZ=1 AngleXU=0 Radius=1.5 StartAngle=3.1416 EndAngle=6.28319
    g4: ArcOfCircle CenterX=-10 CenterY=-4.3 CenterZ=0 NormalX=0 NormalY=0 NormalZ=1 AngleXU=0 Radius=1.5 StartAngle=2e-16 EndAngle=3.14159
    g5: ArcOfCircle CenterX=-16.1 CenterY=-1.8 CenterZ=0 NormalX=0 NormalY=0 NormalZ=1 AngleXU=0 Radius=1.5 StartAngle=5e-16 EndAngle=3.14159
    g6: ArcOfCircle CenterX=-22.1 CenterY=-1.8 CenterZ=0 NormalX=0 NormalY=0 NormalZ=1 AngleXU=0 Radius=1.5 StartAngle=5e-16 EndAngle=3.14159
    g7: ArcOfCircle CenterX=-28.2 CenterY=-4.3 CenterZ=0 NormalX=0 NormalY=0 NormalZ=1 AngleXU=0 Radius=1.5 StartAngle=2e-16 EndAngle=3.14159
    g8: ArcOfCircle CenterX=-10 CenterY=-33.9 CenterZ=0 NormalX=0 NormalY=0 NormalZ=1 AngleXU=0 Radius=1.5 StartAngle=3.14159 EndAngle=6.28319
    g9: ArcOfCircle CenterX=-16.1 CenterY=-36.4 CenterZ=0 NormalX=0 NormalY=0 NormalZ=1 AngleXU=0 Radius=1.5 StartAngle=3.14159 EndAngle=6.28319
    g10: ArcOfCircle CenterX=-22.1 CenterY=-36.4 CenterZ=0 NormalX=0 NormalY=0 NormalZ=1 AngleXU=0 Radius=1.5 StartAngle=3.14159 EndAngle=6.28319
    g11: ArcOfCircle CenterX=-28.2 CenterY=-33.9 CenterZ=0 NormalX=0 NormalY=0 NormalZ=1 AngleXU=0 Radius=1.5 StartAngle=3.14159 EndAngle=6.28319
    g12: LineSegment StartX=-35.7 StartY=-10.5 StartZ=0 EndX=-35.7 EndY=-27.7 EndZ=0
    g13: LineSegment StartX=-32.7 StartY=-10.5 StartZ=0 EndX=-32.7 EndY=-27.7 EndZ=0
    g14: LineSegment StartX=-29.7 StartY=-33.9 StartZ=0 EndX=-29.7 EndY=-4.3 EndZ=0
    g15: LineSegment StartX=-26.7 StartY=-33.9 StartZ=0 EndX=-26.7 EndY=-4.3 EndZ=0
    g16: LineSegment StartX=-2.5 StartY=-10.5 StartZ=0 EndX=-2.5 EndY=-27.7 EndZ=0
    g17: LineSegment StartX=-8.5 StartY=-4.3 StartZ=0 EndX=-8.5 EndY=-33.9 EndZ=0
    g18: LineSegment StartX=-5.5 StartY=-10.5 StartZ=0 EndX=-5.5 EndY=-27.7 EndZ=0
    g19: LineSegment StartX=-11.5 StartY=-4.3 StartZ=0 EndX=-11.5 EndY=-33.9 EndZ=0
    g20: LineSegment StartX=-14.6 StartY=-1.8 StartZ=0 EndX=-14.6 EndY=-36.4 EndZ=0
    g21: LineSegment StartX=-17.6 StartY=-1.8 StartZ=0 EndX=-17.6 EndY=-36.4 EndZ=0
    g22: LineSegment StartX=-20.6 StartY=-36.4 StartZ=0 EndX=-20.6 EndY=-1.8 EndZ=0
    g23: LineSegment StartX=-23.6 StartY=-1.8 StartZ=0 EndX=-23.6 EndY=-36.4 EndZ=0
  constraints (48):
    c: Block(g0)
    c: Block(g1)
    c: Block(g2)
    c: Block(g3)
    c: Block(g4)
    c: Block(g5)
    c: Block(g6)
    c: Block(g7)
    c: Block(g8)
    c: Block(g9)
    c: Block(g10)
    c: Block(g11)
    c: Coincident(g12,g1)
    c: Coincident(g12,g2)
    c: Vertical(g12)
    c: Coincident(g13,g1)
    c: Coincident(g13,g2)
    c: Vertical(g13)
    c: Coincident(g14,g11)
    c: Coincident(g14,g7)
    c: Vertical(g14)
    c: Coincident(g15,g11)
    c: Coincident(g15,g7)
    c: Vertical(g15)
    c: Coincident(g16,g0)
    c: Coincident(g16,g3)
    c: Vertical(g16)
    c: Coincident(g17,g4)
    c: Coincident(g17,g8)
    c: Vertical(g17)
    c: Coincident(g18,g0)
    c: Coincident(g18,g3)
    c: Vertical(g18)
    c: Coincident(g19,g4)
    c: Coincident(g19,g8)
    c: Vertical(g19)
    c: Coincident(g20,g5)
    c: Coincident(g20,g9)
    c: Vertical(g20)
    c: Coincident(g21,g5)
    c: Coincident(g21,g9)
    c: Vertical(g21)
    c: Coincident(g22,g10)
    c: Coincident(g22,g6)
    c: Vertical(g22)
    c: Coincident(g23,g6)
    c: Coincident(g23,g10)
    c: Vertical(g23)
FEATURE [Part::Extrusion] Extrude038  label="removeToCreateFanGrillHoles001"
  Base = -> Sketch047
  Dir = (0,-1,6e-16)
  DirMode = 2
  FaceMakerClass = Part::FaceMakerBullseye
  LengthFwd = 10
  LengthRev = 0
  Placement = pos=(65.4,44,54.82) rot=(0,0,1;0rad)
  Solid = true
  Symmetric = false
FEATURE [Part::Feature] Wire004
  shape: bbox 11 x 5.2 x 2e-07 mm, 0 faces, 0 solids (baked)
FEATURE [Part::Revolution] Revolve095
  Angle = 360
  Axis = (0,1,0)
  Base = (0,0,0)
  FaceMakerClass = Part::FaceMakerBullseye
  Placement = pos=(30.3,38,19.7) rot=(0,0,1;0rad)
  Solid = true
  Source = -> Wire004
  Symmetric = false
FEATURE [Part::Feature] Wire005
  shape: bbox 11 x 5.2 x 2e-07 mm, 0 faces, 0 solids (baked)
FEATURE [Part::Revolution] Revolve096
  Angle = 360
  Axis = (0,1,0)
  Base = (0,0,0)
  FaceMakerClass = Part::FaceMakerBullseye
  Placement = pos=(30.3,38,51.7) rot=(0,0,1;0rad)
  Solid = true
  Source = -> Wire005
  Symmetric = false
FEATURE [Part::Feature] Wire006
  shape: bbox 11 x 5.2 x 2e-07 mm, 0 faces, 0 solids (baked)
FEATURE [Part::Revolution] Revolve097
  Angle = 360
  Axis = (0,1,0)
  Base = (0,0,0)
  FaceMakerClass = Part::FaceMakerBullseye
  Placement = pos=(62.3,38,51.7) rot=(0,0,1;0rad)
  Solid = true
  Source = -> Wire006
  Symmetric = false
FEATURE [Part::Feature] Wire007
  shape: bbox 11 x 5.2 x 2e-07 mm, 0 faces, 0 solids (baked)
FEATURE [Part::Revolution] Revolve098
  Angle = 360
  Axis = (0,1,0)
  Base = (0,0,0)
  FaceMakerClass = Part::FaceMakerBullseye
  Placement = pos=(62.3,38,19.7) rot=(0,0,1;0rad)
  Solid = true
  Source = -> Wire007
  Symmetric = false
FEATURE [Part::MultiFuse] Fusion067  label="fanScrewHousing002"
  Shapes = -> [Revolve098,Revolve097,Revolve096,Revolve095]
FEATURE [Part::Feature] Face091 .. Face094  x4 (patterned run collapsed; names and placements below)
  shape: bbox 3.5 x 17.8 x 2e-07 mm, 1 faces, 0 solids (baked)
FEATURE [Part::Revolution] Revolve099  label="removeToCreateScrewAndThreadedInsertHole026"
  Angle = 360
  Axis = (0,1,0)
  Base = (0,0,0)
  FaceMakerClass = Part::FaceMakerBullseye
  Placement = pos=(62.3,30.3,19.7) rot=(0,0,1;0rad)
  Solid = false
  Source = -> Face091
  Symmetric = false
FEATURE [Part::Revolution] Revolve100  label="removeToCreateScrewAndThreadedInsertHole027"
  Angle = 360
  Axis = (0,1,0)
  Base = (0,0,0)
  FaceMakerClass = Part::FaceMakerBullseye
  Placement = pos=(62.3,30.3,51.7) rot=(0,0,1;0rad)
  Solid = false
  Source = -> Face092
  Symmetric = false
FEATURE [Part::Revolution] Revolve101  label="removeToCreateScrewAndThreadedInsertHole028"
  Angle = 360
  Axis = (0,1,0)
  Base = (0,0,0)
  FaceMakerClass = Part::FaceMakerBullseye
  Placement = pos=(30.3,30.3,19.7) rot=(0,0,1;0rad)
  Solid = false
  Source = -> Face093
  Symmetric = false
FEATURE [Part::Revolution] Revolve102  label="removeToCreateScrewAndThreadedInsertHole029"
  Angle = 360
  Axis = (0,1,0)
  Base = (0,0,0)
  FaceMakerClass = Part::FaceMakerBullseye
  Placement = pos=(30.3,30.3,51.7) rot=(0,0,1;0rad)
  Solid = false
  Source = -> Face094
  Symmetric = false
FEATURE [Part::MultiFuse] Fusion068  label="createThreadedInsertHolesForFan002"
  Shapes = -> [Revolve099,Revolve100,Revolve101,Revolve102]
FEATURE [Part::Cut] Cut026  label="fanScrewHousing003"
  Base = -> Fusion067
  Tool = -> Fusion068
FEATURE [Sketcher::SketchObject] Sketch048
  FullyConstrained = false
  Placement = pos=(0,0,0) rot=(1,0,0;1.5708rad)
  sketch-geometry (24):
    g0: ArcOfCircle CenterX=-4 CenterY=-10.5 CenterZ=0 NormalX=0 NormalY=0 NormalZ=1 AngleXU=0 Radius=1.5 StartAngle=6e-16 EndAngle=3.14159
    g1: ArcOfCircle CenterX=-34.2 CenterY=-10.5 CenterZ=0 NormalX=0 NormalY=0 NormalZ=1 AngleXU=0 Radius=1.5 StartAngle=0 EndAngle=3.14159
    g2: ArcOfCircle CenterX=-34.2 CenterY=-27.7 CenterZ=0 NormalX=0 NormalY=0 NormalZ=1 AngleXU=0 Radius=1.5 StartAngle=3.14159 EndAngle=6.28319
    g3: ArcOfCircle CenterX=-4 CenterY=-27.7 CenterZ=0 NormalX=0 NormalY=0 NormalZ=1 AngleXU=0 Radius=1.5 StartAngle=3.1416 EndAngle=6.28319
    g4: ArcOfCircle CenterX=-10 CenterY=-4.3 CenterZ=0 NormalX=0 NormalY=0 NormalZ=1 AngleXU=0 Radius=1.5 StartAngle=2e-16 EndAngle=3.14159
    g5: ArcOfCircle CenterX=-16.1 CenterY=-1.8 CenterZ=0 NormalX=0 NormalY=0 NormalZ=1 AngleXU=0 Radius=1.5 StartAngle=5e-16 EndAngle=3.14159
    g6: ArcOfCircle CenterX=-22.1 CenterY=-1.8 CenterZ=0 NormalX=0 NormalY=0 NormalZ=1 AngleXU=0 Radius=1.5 StartAngle=5e-16 EndAngle=3.14159
    g7: ArcOfCircle CenterX=-28.2 CenterY=-4.3 CenterZ=0 NormalX=0 NormalY=0 NormalZ=1 AngleXU=0 Radius=1.5 StartAngle=2e-16 EndAngle=3.14159
    g8: ArcOfCircle CenterX=-10 CenterY=-33.9 CenterZ=0 NormalX=0 NormalY=0 NormalZ=1 AngleXU=0 Radius=1.5 StartAngle=3.14159 EndAngle=6.28319
    g9: ArcOfCircle CenterX=-16.1 CenterY=-36.4 CenterZ=0 NormalX=0 NormalY=0 NormalZ=1 AngleXU=0 Radius=1.5 StartAngle=3.14159 EndAngle=6.28319
    g10: ArcOfCircle CenterX=-22.1 CenterY=-36.4 CenterZ=0 NormalX=0 NormalY=0 NormalZ=1 AngleXU=0 Radius=1.5 StartAngle=3.14159 EndAngle=6.28319
    g11: ArcOfCircle CenterX=-28.2 CenterY=-33.9 CenterZ=0 NormalX=0 NormalY=0 NormalZ=1 AngleXU=0 Radius=1.5 StartAngle=3.14159 EndAngle=6.28319
    g12: LineSegment StartX=-35.7 StartY=-10.5 StartZ=0 EndX=-35.7 EndY=-27.7 EndZ=0
    g13: LineSegment StartX=-32.7 StartY=-10.5 StartZ=0 EndX=-32.7 EndY=-27.7 EndZ=0
    g14: LineSegment StartX=-29.7 StartY=-33.9 StartZ=0 EndX=-29.7 EndY=-4.3 EndZ=0
    g15: LineSegment StartX=-26.7 StartY=-33.9 StartZ=0 EndX=-26.7 EndY=-4.3 EndZ=0
    g16: LineSegment StartX=-2.5 StartY=-10.5 StartZ=0 EndX=-2.5 EndY=-27.7 EndZ=0
    g17: LineSegment StartX=-8.5 StartY=-4.3 StartZ=0 EndX=-8.5 EndY=-33.9 EndZ=0
    g18: LineSegment StartX=-5.5 StartY=-10.5 StartZ=0 EndX=-5.5 EndY=-27.7 EndZ=0
    g19: LineSegment StartX=-11.5 StartY=-4.3 StartZ=0 EndX=-11.5 EndY=-33.9 EndZ=0
    g20: LineSegment StartX=-14.6 StartY=-1.8 StartZ=0 EndX=-14.6 EndY=-36.4 EndZ=0
    g21: LineSegment StartX=-17.6 StartY=-1.8 StartZ=0 EndX=-17.6 EndY=-36.4 EndZ=0
    g22: LineSegment StartX=-20.6 StartY=-36.4 StartZ=0 EndX=-20.6 EndY=-1.8 EndZ=0
    g23: LineSegment StartX=-23.6 StartY=-1.8 StartZ=0 EndX=-23.6 EndY=-36.4 EndZ=0
  constraints (48):
    c: Block(g0)
    c: Block(g1)
    c: Block(g2)
    c: Block(g3)
    c: Block(g4)
    c: Block(g5)
    c: Block(g6)
    c: Block(g7)
    c: Block(g8)
    c: Block(g9)
    c: Block(g10)
    c: Block(g11)
    c: Coincident(g12,g1)
    c: Coincident(g12,g2)
    c: Vertical(g12)
    c: Coincident(g13,g1)
    c: Coincident(g13,g2)
    c: Vertical(g13)
    c: Coincident(g14,g11)
    c: Coincident(g14,g7)
    c: Vertical(g14)
    c: Coincident(g15,g11)
    c: Coincident(g15,g7)
    c: Vertical(g15)
    c: Coincident(g16,g0)
    c: Coincident(g16,g3)
    c: Vertical(g16)
    c: Coincident(g17,g4)
    c: Coincident(g17,g8)
    c: Vertical(g17)
    c: Coincident(g18,g0)
    c: Coincident(g18,g3)
    c: Vertical(g18)
    c: Coincident(g19,g4)
    c: Coincident(g19,g8)
    c: Vertical(g19)
    c: Coincident(g20,g5)
    c: Coincident(g20,g9)
    c: Vertical(g20)
    c: Coincident(g21,g5)
    c: Coincident(g21,g9)
    c: Vertical(g21)
    c: Coincident(g22,g10)
    c: Coincident(g22,g6)
    c: Vertical(g22)
    c: Coincident(g23,g6)
    c: Coincident(g23,g10)
    c: Vertical(g23)
FEATURE [Part::Extrusion] Extrude039  label="removeToCreateFanGrillHoles002"
  Base = -> Sketch048
  Dir = (0,-1,6e-16)
  DirMode = 2
  FaceMakerClass = Part::FaceMakerBullseye
  LengthFwd = 10
  LengthRev = 0
  Placement = pos=(65.4,44,54.82) rot=(0,0,1;0rad)
  Solid = true
  Symmetric = false
FEATURE [Part::Cut] Cut027  label="fanScrewHousing004"
  Base = -> Cut026
  Tool = -> Extrude038
FEATURE [Part::Cut] Cut028  label="top014"
  Base = -> Fillet026
  Tool = -> Extrude039
FEATURE [Part::Feature] Face095 .. Face098  x4 (patterned run collapsed; names and placements below)
  shape: bbox 3.5 x 17.8 x 2e-07 mm, 1 faces, 0 solids (baked)
FEATURE [Part::Revolution] Revolve103  label="removeToCreateScrewAndThreadedInsertHole030"
  Angle = 360
  Axis = (0,1,0)
  Base = (0,0,0)
  FaceMakerClass = Part::FaceMakerBullseye
  Placement = pos=(62.3,30.3,19.7) rot=(0,0,1;0rad)
  Solid = false
  Source = -> Face095
  Symmetric = false
FEATURE [Part::Revolution] Revolve104  label="removeToCreateScrewAndThreadedInsertHole031"
  Angle = 360
  Axis = (0,1,0)
  Base = (0,0,0)
  FaceMakerClass = Part::FaceMakerBullseye
  Placement = pos=(62.3,30.3,51.7) rot=(0,0,1;0rad)
  Solid = false
  Source = -> Face096
  Symmetric = false
FEATURE [Part::Revolution] Revolve105  label="removeToCreateScrewAndThreadedInsertHole032"
  Angle = 360
  Axis = (0,1,0)
  Base = (0,0,0)
  FaceMakerClass = Part::FaceMakerBullseye
  Placement = pos=(30.3,30.3,19.7) rot=(0,0,1;0rad)
  Solid = false
  Source = -> Face097
  Symmetric = false
FEATURE [Part::Revolution] Revolve106  label="removeToCreateScrewAndThreadedInsertHole033"
  Angle = 360
  Axis = (0,1,0)
  Base = (0,0,0)
  FaceMakerClass = Part::FaceMakerBullseye
  Placement = pos=(30.3,30.3,51.7) rot=(0,0,1;0rad)
  Solid = false
  Source = -> Face098
  Symmetric = false
FEATURE [Part::MultiFuse] Fusion069  label="createThreadedInsertHolesForFan003"
  Shapes = -> [Revolve103,Revolve104,Revolve105,Revolve106]
FEATURE [Part::Cut] Cut029  label="top015"
  Base = -> Cut028
  Tool = -> Fusion054
FEATURE [Part::Cut] Cut030  label="fanScrewHousing005"
  Base = -> Cut027
  Tool = -> Fusion069
FEATURE [Part::Cylinder] Cylinder026  label="removeToCreteHoleForPlugHousing010"
  Angle = 360
  AttacherType = Attacher::AttachEngine3D
  Height = 20
  Placement = pos=(-2,19,36) rot=(0,1,0;1.5708rad)
  Radius = 14.3
FEATURE [Part::Box] Box018  label="removeToCreteHoleForPlugHousing011"
  AttacherType = Attacher::AttachEngine3D
  Height = 28.6
  Length = 10
  Placement = pos=(-2,0,21.7) rot=(0,0,1;0rad)
  Width = 19
FEATURE [Part::Box] Box019  label="wireHolderBottomCaseBit"
  AttacherType = Attacher::AttachEngine3D
  Height = 28
  Length = 3
  Placement = pos=(0,0,22) rot=(0,0,1;0rad)
  Width = 21
FEATURE [Part::Cylinder] Cylinder027  label="removeToCreteHoleForPlugHousing012"
  Angle = 360
  AttacherType = Attacher::AttachEngine3D
  Height = 20
  Placement = pos=(-2,19,36) rot=(0,1,0;1.5708rad)
  Radius = 14.3
FEATURE [Part::Cut] Cut031  label="wireHolderBottomCaseBit001"
  Base = -> Box019
  Tool = -> Cylinder027
FEATURE [Part::MultiFuse] Fusion070  label="removeToCreteHoleForPlugHousing013"
  Shapes = -> [Box018,Cylinder026]
FEATURE [Part::Cut] Cut032  label="top016"
  Base = -> Cut029
  Tool = -> Fusion070
FEATURE [Part::Cylinder] Cylinder028
  Angle = 360
  AttacherType = Attacher::AttachEngine3D
  Height = 20
  Placement = pos=(0,0,36.15) rot=(0,0,1;0rad)
  Radius = 14.3
FEATURE [Part::Cylinder] Cylinder029
  Angle = 360
  AttacherType = Attacher::AttachEngine3D
  Height = 10
  Placement = pos=(0,0,36.15) rot=(0,0,1;0rad)
  Radius = 4
FEATURE [Part::MultiFuse] Fusion071  label="removeToCreteHoleForPlugHousing014"
  Placement = pos=(70,19,36) rot=(0,1,0;1.5708rad)
  Shapes = -> [Cylinder028,Cylinder029]
FEATURE [Sketcher::SketchObject] Sketch049  label="topSketch011"
  FullyConstrained = true
  sketch-geometry (4):
    g0: ArcOfCircle CenterX=105 CenterY=19 CenterZ=0 NormalX=0 NormalY=0 NormalZ=1 AngleXU=0 Radius=20.6155 StartAngle=5.54125 EndAngle=6.28319
    g1: ArcOfCircle CenterX=105 CenterY=19 CenterZ=0 NormalX=0 NormalY=0 NormalZ=1 AngleXU=0 Radius=13 StartAngle=5.54125 EndAngle=6.28319
    g2: LineSegment StartX=118 StartY=19 StartZ=0 EndX=125.616 EndY=19 EndZ=0
    g3: LineSegment StartX=114.583 StartY=10.2157 StartZ=0 EndX=120.197 EndY=5.06982 EndZ=0
  constraints (7):
    c: Block(g0)
    c: Block(g1)
    c: Coincident(g2,g1)
    c: Coincident(g2,g0)
    c: Horizontal(g2)
    c: Coincident(g3,g1)
    c: Coincident(g3,g0)
FEATURE [Part::Box] Box020  label="removeToCreteHoleForPlugHousing015"
  AttacherType = Attacher::AttachEngine3D
  Height = 28.6
  Length = 20
  Placement = pos=(106.15,0,21.7) rot=(0,0,1;0rad)
  Width = 19
FEATURE [Part::MultiFuse] Fusion072  label="removeToCreteHoleForPlugHousing016"
  Shapes = -> [Box020,Fusion071]
FEATURE [Part::Cut] Cut033  label="removeToCreteHoleForPlugHousing017"
  Base = -> Cut032
  Tool = -> Fusion072
FEATURE [Part::Cylinder] Cylinder030
  Angle = 360
  AttacherType = Attacher::AttachEngine3D
  Height = 20
  Placement = pos=(0,0,36.15) rot=(0,0,1;0rad)
  Radius = 14.3
FEATURE [Part::Cylinder] Cylinder031
  Angle = 360
  AttacherType = Attacher::AttachEngine3D
  Height = 10
  Placement = pos=(0,0,36.15) rot=(0,0,1;0rad)
  Radius = 4
FEATURE [Part::Box] Box021  label="removeToCreteHoleForPlugHousing019"
  AttacherType = Attacher::AttachEngine3D
  Height = 28.6
  Length = 20
  Placement = pos=(106.15,0,21.7) rot=(0,0,1;0rad)
  Width = 19
FEATURE [Part::MultiFuse] Fusion074  label="removeToCreteHoleForPlugHousing020"
  Placement = pos=(70,19,36) rot=(0,1,0;1.5708rad)
  Shapes = -> [Cylinder030,Cylinder031]
FEATURE [Part::MultiFuse] Fusion073  label="removeToCreteHoleForPlugHousing018"
  Placement = pos=(0,0,28.3) rot=(0,0,1;0rad)
  Shapes = -> [Box021,Fusion074]
FEATURE [Part::Cylinder] Cylinder032
  Angle = 360
  AttacherType = Attacher::AttachEngine3D
  Height = 20
  Placement = pos=(0,0,36.15) rot=(0,0,1;0rad)
  Radius = 14.3
FEATURE [Part::Cylinder] Cylinder033
  Angle = 360
  AttacherType = Attacher::AttachEngine3D
  Height = 10
  Placement = pos=(0,0,36.15) rot=(0,0,1;0rad)
  Radius = 4
FEATURE [Part::Box] Box022  label="removeToCreteHoleForPlugHousing021"
  AttacherType = Attacher::AttachEngine3D
  Height = 28.6
  Length = 20
  Placement = pos=(106.15,0,21.7) rot=(0,0,1;0rad)
  Width = 19
FEATURE [Part::MultiFuse] Fusion076  label="removeToCreteHoleForPlugHousing023"
  Placement = pos=(70,19,36) rot=(0,1,0;1.5708rad)
  Shapes = -> [Cylinder032,Cylinder033]
FEATURE [Part::MultiFuse] Fusion075  label="removeToCreteHoleForPlugHousing022"
  Placement = pos=(0,0,-28.3) rot=(0,0,1;0rad)
  Shapes = -> [Box022,Fusion076]
FEATURE [Part::MultiFuse] Fusion077  label="removeToCreatePlugHousingBottomBit"
  Shapes = -> [Fusion075,Fusion073]
FEATURE [Part::Cylinder] Cylinder034
  Angle = 360
  AttacherType = Attacher::AttachEngine3D
  Height = 20
  Placement = pos=(0,0,36.15) rot=(0,0,1;0rad)
  Radius = 14
FEATURE [Part::Cylinder] Cylinder035
  Angle = 360
  AttacherType = Attacher::AttachEngine3D
  Height = 10
  Placement = pos=(0,0,36.15) rot=(0,0,1;0rad)
  Radius = 4
FEATURE [Part::MultiFuse] Fusion078  label="removeToCreteHoleForPlugHousing024"
  Placement = pos=(70,19,36) rot=(0,1,0;1.5708rad)
  Shapes = -> [Cylinder034,Cylinder035]
FEATURE [Part::MultiFuse] Fusion079  label="removeToCreatePlugHousingBottomBit001"
  Shapes = -> [Fusion078,Fusion077]
FEATURE [Part::Extrusion] Extrude040  label="bottomPlugHousingBit"
  Base = -> Sketch049
  Dir = (0,0,1)
  DirMode = 2
  FaceMakerClass = Part::FaceMakerBullseye
  LengthFwd = 72
  LengthRev = 0
  Solid = true
  Symmetric = false
FEATURE [Part::Cut] Cut034  label="bottomPlugHousingBit001"
  Base = -> Extrude040
  Placement = pos=(-0.09,0,0) rot=(0,0,1;0rad)
  Tool = -> Fusion079
FEATURE [Part::Box] Box023  label="Cube014"
  AttacherType = Attacher::AttachEngine3D
  Height = 16
  Length = 8
  Placement = pos=(12.7,31.52,28) rot=(0,0,1;0rad)
  Width = 4
FEATURE [Part::Cylinder] Cylinder036
  Angle = 360
  AttacherType = Attacher::AttachEngine3D
  Height = 10
  Placement = pos=(0,0,36.15) rot=(0,0,1;0rad)
  Radius = 4
FEATURE [Part::Cylinder] Cylinder037
  Angle = 360
  AttacherType = Attacher::AttachEngine3D
  Height = 20
  Placement = pos=(0,0,36.15) rot=(0,0,1;0rad)
  Radius = 8.2
FEATURE [Part::MultiFuse] Fusion080  label="removeToCreteHoleForPlugHousing025"
  Placement = pos=(-42,19,36) rot=(0,1,0;1.5708rad)
  Shapes = -> [Cylinder037,Cylinder036]
FEATURE [Sketcher::SketchObject] Sketch050  label="topSketch012"
  FullyConstrained = true
  sketch-geometry (4):
    g0: LineSegment StartX=16.8446 StartY=31.512 StartZ=0 EndX=16.3251 EndY=34.4666 EndZ=0
    g1: ArcOfCircle CenterX=19 CenterY=19.2524 CenterZ=0 NormalX=0 NormalY=0 NormalZ=1 AngleXU=0 Radius=15.4476 StartAngle=1.74483 EndAngle=2.72717
    g2: ArcOfCircle CenterX=19 CenterY=19.2524 CenterZ=0 NormalX=0 NormalY=0 NormalZ=1 AngleXU=0 Radius=12.4476 StartAngle=1.74483 EndAngle=2.73189
    g3: LineSegment StartX=4.86004 StartY=25.4725 StartZ=0 EndX=7.58253 EndY=24.2107 EndZ=0
  constraints (7):
    c: Block(g0)
    c: Coincident(g1,g0)
    c: Coincident(g2,g0)
    c: Coincident(g3,g1)
    c: Coincident(g3,g2)
    c: Block(g1)
    c: Block(g2)
FEATURE [Part::Extrusion] Extrude041
  Base = -> Sketch050
  Dir = (0,0,1)
  DirMode = 2
  FaceMakerClass = Part::FaceMakerBullseye
  LengthFwd = 10.6
  LengthRev = 0
  Placement = pos=(0,0,31) rot=(0,0,1;0rad)
  Solid = true
  Symmetric = false
FEATURE [Part::Cut] Cut035
  Base = -> Extrude041
  Placement = pos=(0,0,-0.3) rot=(0,0,1;0rad)
  Tool = -> Fusion080
FEATURE [Part::Cut] Cut036
  Base = -> Box023
  Tool = -> Cut035
FEATURE [Part::Fillet] Fillet027
  Base = -> Cut036
  Edges = 1 edges r=0.7: [Edge13]
FEATURE [Part::Fillet] Fillet028
  Base = -> Fillet027
  Edges = 1 edges r=0.7: [Edge13]
FEATURE [Part::Fillet] Fillet029
  Base = -> Fillet028
  Edges = 1 edges r=0.7: [Edge16]
FEATURE [Part::Fillet] Fillet030
  Base = -> Fillet029
  Edges = 1 edges r=0.7: [Edge11]
FEATURE [Part::Fillet] Fillet031
  Base = -> Fillet030
  Edges = 1 edges r=0.7: [Edge10]
FEATURE [Part::Fillet] Fillet032
  Base = -> Fillet031
  Edges = 1 edges r=1.2: [Edge5]
FEATURE [Part::Fillet] Fillet033
  Base = -> Fillet032
  Edges = 1 edges r=1.2: [Edge12]
FEATURE [Part::Fillet] Fillet034  label="wireHousingRetainer"
  Base = -> Fillet033
  Edges = 1 edges r=2: [Edge1]
  Placement = pos=(0.3,0,0) rot=(0,0,1;0rad)
FEATURE [Part::Feature] Face099
  shape: bbox 3.5 x 17.8 x 2e-07 mm, 1 faces, 0 solids (baked)
FEATURE [Part::Revolution] Revolve107  label="removeToCreateScrewAndThreadedInsertHole034"
  Angle = 360
  Axis = (0,1,0)
  Base = (0,0,0)
  FaceMakerClass = Part::FaceMakerBullseye
  Placement = pos=(12.5,0,10) rot=(0,0,1;0rad)
  Solid = false
  Source = -> Face099
  Symmetric = false
FEATURE [Part::Feature] Face100
  shape: bbox 3.5 x 17.8 x 2e-07 mm, 1 faces, 0 solids (baked)
FEATURE [Part::Revolution] Revolve108  label="removeToCreateScrewAndThreadedInsertHole035"
  Angle = 360
  Axis = (0,1,0)
  Base = (0,0,0)
  FaceMakerClass = Part::FaceMakerBullseye
  Placement = pos=(12.5,0,62) rot=(0,0,1;0rad)
  Solid = false
  Source = -> Face100
  Symmetric = false
FEATURE [Part::Feature] Face101
  shape: bbox 3.5 x 17.8 x 2e-07 mm, 1 faces, 0 solids (baked)
FEATURE [Part::Revolution] Revolve109  label="removeToCreateScrewAndThreadedInsertHole036"
  Angle = 360
  Axis = (0,1,0)
  Base = (0,0,0)
  FaceMakerClass = Part::FaceMakerBullseye
  Placement = pos=(89.5,0,68.5) rot=(0,0,1;0rad)
  Solid = false
  Source = -> Face101
  Symmetric = false
FEATURE [Part::Feature] Face102
  shape: bbox 3.5 x 17.8 x 2e-07 mm, 1 faces, 0 solids (baked)
FEATURE [Part::Revolution] Revolve110  label="removeToCreateScrewAndThreadedInsertHole037"
  Angle = 360
  Axis = (0,1,0)
  Base = (0,0,0)
  FaceMakerClass = Part::FaceMakerBullseye
  Placement = pos=(89.5,0,3.5) rot=(0,0,1;0rad)
  Solid = false
  Source = -> Face102
  Symmetric = false
FEATURE [Part::Feature] Face103
  shape: bbox 3.5 x 17.8 x 2e-07 mm, 1 faces, 0 solids (baked)
FEATURE [Part::Revolution] Revolve111  label="removeToCreateScrewAndThreadedInsertHole038"
  Angle = 360
  Axis = (0,1,0)
  Base = (0,0,0)
  FaceMakerClass = Part::FaceMakerBullseye
  Placement = pos=(109.5,4.7,3.5) rot=(0,0,1;0rad)
  Solid = false
  Source = -> Face103
  Symmetric = false
FEATURE [Part::Feature] Face104
  shape: bbox 3.5 x 17.8 x 2e-07 mm, 1 faces, 0 solids (baked)
FEATURE [Part::Revolution] Revolve112  label="removeToCreateScrewAndThreadedInsertHole039"
  Angle = 360
  Axis = (0,1,0)
  Base = (0,0,0)
  FaceMakerClass = Part::FaceMakerBullseye
  Placement = pos=(109.5,4.7,68.5) rot=(0,0,1;0rad)
  Solid = false
  Source = -> Face104
  Symmetric = false
FEATURE [Part::MultiFuse] Fusion081  label="removeToCreateScrewAndThreadedInsertHole040"
  Shapes = -> [Revolve107,Revolve108,Revolve109,Revolve110,Revolve111,Revolve112]
FEATURE [Part::MultiFuse] Fusion082  label="casePillars002"
  Shapes = -> [Revolve094,Revolve092,Revolve090,Revolve089,Revolve091,Revolve093]
FEATURE [Part::Cut] Cut037  label="casePillars003"
  Base = -> Fusion082
  Tool = -> Fusion081
FEATURE [Sketcher::SketchObject] Sketch051
  FullyConstrained = true
  Placement = pos=(117,19,0) rot=(0.57735,0.57735,0.57735;2.0944rad)
  sketch-geometry (48):
    g0: LineSegment StartX=-49.19 StartY=69.25 StartZ=0 EndX=-49.19 EndY=66.25 EndZ=0
    g1: LineSegment StartX=-49.19 StartY=63.5 StartZ=0 EndX=-49.19 EndY=60.5 EndZ=0
    g2: LineSegment StartX=-49.19 StartY=57.75 StartZ=0 EndX=-49.19 EndY=54.75 EndZ=0
    g3: LineSegment StartX=-49.19 StartY=52 StartZ=0 EndX=-49.19 EndY=49 EndZ=0
    g4: LineSegment StartX=-49.19 StartY=46.25 StartZ=0 EndX=-49.19 EndY=43.25 EndZ=0
    g5: LineSegment StartX=-49.19 StartY=40.5 StartZ=0 EndX=-49.19 EndY=37.5 EndZ=0
    g6: LineSegment StartX=-49.19 StartY=34.5 StartZ=0 EndX=-49.19 EndY=31.5 EndZ=0
    g7: LineSegment StartX=-49.19 StartY=28.75 StartZ=0 EndX=-49.19 EndY=25.75 EndZ=0
    g8: LineSegment StartX=-49.19 StartY=23 StartZ=0 EndX=-49.19 EndY=20 EndZ=0
    g9: LineSegment StartX=-49.19 StartY=17.25 StartZ=0 EndX=-49.19 EndY=14.25 EndZ=0
    g10: LineSegment StartX=-49.19 StartY=11.5 StartZ=0 EndX=-49.19 EndY=8.5 EndZ=0
    g11: LineSegment StartX=-49.19 StartY=5.75 StartZ=0 EndX=-49.19 EndY=2.75 EndZ=0
    g12: ArcOfCircle CenterX=-1.5 CenterY=67.75 CenterZ=0 NormalX=0 NormalY=0 NormalZ=1 AngleXU=0 Radius=1.5 StartAngle=4.71239 EndAngle=7.85398
    g13: ArcOfCircle CenterX=-1.5 CenterY=62 CenterZ=0 NormalX=0 NormalY=0 NormalZ=1 AngleXU=0 Radius=1.5 StartAngle=4.71239 EndAngle=7.85398
    g14: ArcOfCircle CenterX=-1.5 CenterY=56.25 CenterZ=0 NormalX=0 NormalY=0 NormalZ=1 AngleXU=0 Radius=1.5 StartAngle=4.71239 EndAngle=7.85398
    g15: ArcOfCircle CenterX=-11.49 CenterY=50.5 CenterZ=0 NormalX=0 NormalY=0 NormalZ=1 AngleXU=0 Radius=1.5 StartAngle=4.71239 EndAngle=7.85398
    g16: ArcOfCircle CenterX=-16.28 CenterY=44.75 CenterZ=0 NormalX=0 NormalY=0 NormalZ=1 AngleXU=0 Radius=1.5 StartAngle=4.71239 EndAngle=7.85398
    g17: ArcOfCircle CenterX=-18.2337 CenterY=39 CenterZ=0 NormalX=0 NormalY=0 NormalZ=1 AngleXU=0 Radius=1.5 StartAngle=4.71485 EndAngle=7.85398
    g18: ArcOfCircle CenterX=-16.2837 CenterY=27.25 CenterZ=0 NormalX=0 NormalY=0 NormalZ=1 AngleXU=0 Radius=1.5 StartAngle=4.71485 EndAngle=7.85398
    g19: ArcOfCircle CenterX=-18.2337 CenterY=33 CenterZ=0 NormalX=0 NormalY=0 NormalZ=1 AngleXU=0 Radius=1.5 StartAngle=4.71485 EndAngle=7.85398
    g20: ArcOfCircle CenterX=-11.49 CenterY=21.5 CenterZ=0 NormalX=0 NormalY=0 NormalZ=1 AngleXU=0 Radius=1.5 StartAngle=4.71239 EndAngle=7.85398
    g21: ArcOfCircle CenterX=-1.5 CenterY=4.25 CenterZ=0 NormalX=0 NormalY=0 NormalZ=1 AngleXU=0 Radius=1.5 StartAngle=4.71239 EndAngle=7.85398
    g22: ArcOfCircle CenterX=-1.5 CenterY=10 CenterZ=0 NormalX=0 NormalY=0 NormalZ=1 AngleXU=0 Radius=1.5 StartAngle=4.71239 EndAngle=7.85398
    g23: ArcOfCircle CenterX=-1.5 CenterY=15.75 CenterZ=0 NormalX=0 NormalY=0 NormalZ=1 AngleXU=0 Radius=1.5 StartAngle=4.71239 EndAngle=7.85398
    g24: LineSegment StartX=-49.19 StartY=69.25 StartZ=0 EndX=-1.5 EndY=69.25 EndZ=0
    g25: LineSegment StartX=-49.19 StartY=66.25 StartZ=0 EndX=-1.5 EndY=66.25 EndZ=0
    g26: LineSegment StartX=-49.19 StartY=63.5 StartZ=0 EndX=-1.5 EndY=63.5 EndZ=0
    g27: LineSegment StartX=-49.19 StartY=60.5 StartZ=0 EndX=-1.5 EndY=60.5 EndZ=0
    g28: LineSegment StartX=-49.19 StartY=57.75 StartZ=0 EndX=-1.5 EndY=57.75 EndZ=0
    g29: LineSegment StartX=-49.19 StartY=54.75 StartZ=0 EndX=-1.5 EndY=54.75 EndZ=0
    g30: LineSegment StartX=-49.19 StartY=52 StartZ=0 EndX=-11.49 EndY=52 EndZ=0
    g31: LineSegment StartX=-49.19 StartY=49 StartZ=0 EndX=-11.49 EndY=49 EndZ=0
    g32: LineSegment StartX=-49.19 StartY=46.25 StartZ=0 EndX=-16.28 EndY=46.25 EndZ=0
    g33: LineSegment StartX=-49.19 StartY=43.25 StartZ=0 EndX=-16.28 EndY=43.25 EndZ=0
    g34: LineSegment StartX=-49.19 StartY=40.5 StartZ=0 EndX=-18.2337 EndY=40.5 EndZ=0
    g35: LineSegment StartX=-49.19 StartY=37.5 StartZ=0 EndX=-18.23 EndY=37.5 EndZ=0
    g36: LineSegment StartX=-49.19 StartY=34.5 StartZ=0 EndX=-18.2337 EndY=34.5 EndZ=0
    g37: LineSegment StartX=-49.19 StartY=31.5 StartZ=0 EndX=-18.23 EndY=31.5 EndZ=0
    g38: LineSegment StartX=-49.19 StartY=28.75 StartZ=0 EndX=-16.2837 EndY=28.75 EndZ=0
    g39: LineSegment StartX=-49.19 StartY=25.75 StartZ=0 EndX=-16.28 EndY=25.75 EndZ=0
    g40: LineSegment StartX=-49.19 StartY=23 StartZ=0 EndX=-11.49 EndY=23 EndZ=0
    g41: LineSegment StartX=-49.19 StartY=20 StartZ=0 EndX=-11.49 EndY=20 EndZ=0
    g42: LineSegment StartX=-49.19 StartY=17.25 StartZ=0 EndX=-1.5 EndY=17.25 EndZ=0
    g43: LineSegment StartX=-49.19 StartY=14.25 StartZ=0 EndX=-1.5 EndY=14.25 EndZ=0
    g44: LineSegment StartX=-49.19 StartY=11.5 StartZ=0 EndX=-1.5 EndY=11.5 EndZ=0
    g45: LineSegment StartX=-49.19 StartY=8.5 StartZ=0 EndX=-1.5 EndY=8.5 EndZ=0
    g46: LineSegment StartX=-49.19 StartY=5.75 StartZ=0 EndX=-1.5 EndY=5.75 EndZ=0
    g47: LineSegment StartX=-49.19 StartY=2.75 StartZ=0 EndX=-1.5 EndY=2.75 EndZ=0
  constraints (120):
    c: Vertical(g0)
    c: Distance(g0) = 3
    c: Block(g0)
    c: Vertical(g1)
    c: Distance(g1) = 3
    c: Vertical(g2)
    c: Equal(g0,g2) = 3
    c: Block(g2)
    c: Vertical(g3)
    c: Equal(g1,g3) = 3
    c: Vertical(g4)
    c: Equal(g0,g4) = 3
    c: Block(g4)
    c: Vertical(g5)
    c: Equal(g1,g5) = 3
    c: Vertical(g6)
    c: Equal(g0,g6) = 3
    c: Block(g6)
    c: Vertical(g7)
    c: Equal(g1,g7) = 3
    c: Vertical(g8)
    c: Equal(g0,g8) = 3
    c: Block(g8)
    c: Vertical(g9)
    c: Equal(g1,g9) = 3
    c: Vertical(g10)
    c: Equal(g0,g10) = 3
    c: Block(g10)
    c: Vertical(g11)
    c: Equal(g1,g11) = 3
    c: Block(g12)
    c: Block(g13)
    c: Block(g14)
    c: Block(g15)
    c: Block(g16)
    c: Block(g17)
    c: Block(g18)
    c: Block(g19)
    c: Block(g20)
    c: Block(g21)
    c: Block(g22)
    c: Block(g23)
    c: Block(g11)
    c: Block(g9)
    c: Block(g7)
    c: Block(g5)
    c: Block(g3)
    c: Block(g1)
    c: Coincident(g24,g0)
    c: Coincident(g24,g12)
    c: Horizontal(g24)
    c: Coincident(g25,g0)
    c: Coincident(g25,g12)
    c: Horizontal(g25)
    c: Coincident(g26,g1)
    c: Coincident(g26,g13)
    c: Horizontal(g26)
    c: Coincident(g27,g1)
    c: Coincident(g27,g13)
    c: Horizontal(g27)
    c: Coincident(g28,g2)
    c: Coincident(g28,g14)
    c: Horizontal(g28)
    c: Coincident(g29,g2)
    c: Coincident(g29,g14)
    c: Horizontal(g29)
    c: Coincident(g30,g3)
    c: Coincident(g30,g15)
    c: Horizontal(g30)
    c: Coincident(g31,g3)
    c: Coincident(g31,g15)
    c: Horizontal(g31)
    c: Coincident(g32,g4)
    c: Coincident(g32,g16)
    c: Horizontal(g32)
    c: Coincident(g33,g4)
    c: Coincident(g33,g16)
    c: Horizontal(g33)
    c: Coincident(g34,g5)
    c: Coincident(g34,g17)
    c: Horizontal(g34)
    c: Coincident(g35,g5)
    c: Coincident(g35,g17)
    c: Horizontal(g35)
    c: Coincident(g36,g6)
    c: Coincident(g36,g19)
    c: Horizontal(g36)
    c: Coincident(g37,g6)
    c: Coincident(g37,g19)
    c: Horizontal(g37)
    c: Coincident(g38,g7)
    c: Coincident(g38,g18)
    c: Horizontal(g38)
    c: Coincident(g39,g7)
    c: Coincident(g39,g18)
    c: Horizontal(g39)
    c: Coincident(g40,g8)
    c: Coincident(g40,g20)
    c: Horizontal(g40)
    c: Coincident(g41,g8)
    c: Coincident(g41,g20)
    c: Horizontal(g41)
    c: Coincident(g42,g9)
    c: Coincident(g42,g23)
    c: Horizontal(g42)
    c: Coincident(g43,g9)
    c: Coincident(g43,g23)
    c: Horizontal(g43)
    c: Coincident(g44,g10)
    c: Coincident(g44,g22)
    c: Horizontal(g44)
    c: Coincident(g45,g10)
    c: Coincident(g45,g22)
    c: Horizontal(g45)
    c: Coincident(g46,g11)
    c: Coincident(g46,g21)
    c: Horizontal(g46)
    c: Coincident(g47,g11)
    c: Coincident(g47,g21)
    c: Horizontal(g47)
FEATURE [Part::Extrusion] Extrude042
  Base = -> Sketch051
  Dir = (1,-2e-16,2e-16)
  DirMode = 2
  FaceMakerClass = Part::FaceMakerBullseye
  LengthFwd = 19
  LengthRev = 0
  Placement = pos=(-19,0,0) rot=(0,0,1;0rad)
  Solid = true
  Symmetric = false
FEATURE [Part::Fillet] Fillet035  label="removeToCreateVentalationHoles"
  Base = -> Extrude042
  Edges = <same value as first occurrence — deduplicated (x6 in doc)>
  Placement = pos=(7,0,0) rot=(0,0,1;0rad)
FEATURE [Part::Cut] Cut038  label="top017"
  Base = -> Cut033
  Tool = -> Fillet035
FEATURE [Sketcher::SketchObject] Sketch052  label="bottomSketch001"
  FullyConstrained = true
  sketch-geometry (45):
    g0: LineSegment StartX=6.29999 StartY=8 StartZ=0 EndX=3.29999 EndY=8 EndZ=0
    g1: LineSegment StartX=3.29999 StartY=8 StartZ=0 EndX=3.29999 EndY=-6.03275e-07 EndZ=0
    g2: ArcOfCircle CenterX=8.29999 CenterY=5 CenterZ=0 NormalX=0 NormalY=0 NormalZ=1 AngleXU=0 Radius=2 StartAngle=3.14159 EndAngle=4.71239
    g3: LineSegment StartX=6.29999 StartY=8 StartZ=0 EndX=6.29999 EndY=5 EndZ=0
    g4: ArcOfCircle CenterX=105 CenterY=19 CenterZ=0 NormalX=0 NormalY=0 NormalZ=1 AngleXU=0 Radius=12.7 StartAngle=4.71239 EndAngle=5.94289
    g5-g11: Circle x7 (B-spline internal-alignment scaffolding for g12; pole/knot coordinates omitted)
    g12: BSplineCurve PolesCount=7 KnotsCount=5 Degree=3 IsPeriodic=0
    g13-g17: GeomPoint x5 (B-spline internal-alignment scaffolding for g12; pole/knot coordinates omitted)
    g18: ArcOfCircle CenterX=105 CenterY=19 CenterZ=0 NormalX=0 NormalY=0 NormalZ=1 AngleXU=0 Radius=15.7 StartAngle=5.81226 EndAngle=6.28319
    g19: BSplineCurve PolesCount=5 KnotsCount=3 Degree=3 IsPeriodic=0
    g20: LineSegment StartX=8.29999 StartY=3 StartZ=0 EndX=101.7 EndY=3 EndZ=0
    g21: LineSegment StartX=3.29999 StartY=-6.03275e-07 StartZ=0 EndX=105 EndY=-6.03275e-07 EndZ=0
    g22: LineSegment StartX=120.974 StartY=8.71251 StartZ=0 EndX=122.332 EndY=7.83778 EndZ=0
    g23: LineSegment StartX=105 StartY=-6.03274e-07 StartZ=0 EndX=113 EndY=-6.03274e-07 EndZ=0
    g24: ArcOfCircle CenterX=105 CenterY=19 CenterZ=0 NormalX=0 NormalY=0 NormalZ=1 AngleXU=0 Radius=20.6155 StartAngle=5.11091 EndAngle=5.71103
    g25: ArcOfCircle CenterX=117.7 CenterY=19 CenterZ=0 NormalX=0 NormalY=0 NormalZ=1 AngleXU=0 Radius=3 StartAngle=1.2e-15 EndAngle=2.10468
    g26: Circle CenterX=116.345 CenterY=16.3232 CenterZ=0 NormalX=0 NormalY=0 NormalZ=1 AngleXU=0 Radius=1
    g27: Circle CenterX=117.24 CenterY=15.7584 CenterZ=0 NormalX=0 NormalY=0 NormalZ=1 AngleXU=0 Radius=1
    g28: Circle CenterX=116.972 CenterY=14.7612 CenterZ=0 NormalX=0 NormalY=0 NormalZ=1 AngleXU=0 Radius=1
    g29: BSplineCurve PolesCount=3 KnotsCount=2 Degree=2 IsPeriodic=0
    g30: GeomPoint X=116.345 Y=16.3232 Z=0
    g31: GeomPoint X=116.972 Y=14.7612 Z=0
    g32: Circle CenterX=115.828 CenterY=17.157 CenterZ=0 NormalX=0 NormalY=0 NormalZ=1 AngleXU=0 Radius=1
    g33: Circle CenterX=115.841 CenterY=16.639 CenterZ=0 NormalX=0 NormalY=0 NormalZ=1 AngleXU=0 Radius=1
    g34: Circle CenterX=116.345 CenterY=16.3232 CenterZ=0 NormalX=0 NormalY=0 NormalZ=1 AngleXU=0 Radius=1
    g35: BSplineCurve PolesCount=3 KnotsCount=2 Degree=2 IsPeriodic=0
    g36: GeomPoint X=115.828 Y=17.157 Z=0
    g37: GeomPoint X=116.345 Y=16.3232 Z=0
    g38: LineSegment StartX=115.828 StartY=17.157 StartZ=0 EndX=115.828 EndY=20.8307 EndZ=0
    g39: Circle CenterX=115.828 CenterY=20.8307 CenterZ=0 NormalX=0 NormalY=0 NormalZ=1 AngleXU=0 Radius=1
    g40: Circle CenterX=115.831 CenterY=21.3396 CenterZ=0 NormalX=0 NormalY=0 NormalZ=1 AngleXU=0 Radius=1
    g41: Circle CenterX=116.173 CenterY=21.5825 CenterZ=0 NormalX=0 NormalY=0 NormalZ=1 AngleXU=0 Radius=1
    g42: BSplineCurve PolesCount=3 KnotsCount=2 Degree=2 IsPeriodic=0
    g43: GeomPoint X=115.828 Y=20.8307 Z=0
    g44: GeomPoint X=116.173 Y=21.5825 Z=0
  constraints (70):
    c: Horizontal(g0)
    c: Distance(g0) = 3
    c: Coincident(g1,g0)
    c: Vertical(g1)
    c: Block(g2)
    c: Block(g0)
    c: Coincident(g3,g0)
    c: Coincident(g3,g2)
    c: Vertical(g3)
    c: Block(g1)
    c: Block(g4)
    c: Coincident(g19,g4)
    c: Block(g19)
    c: Equal(g5, g6-g11) x6
    c: InternalAlignment(g5-g11 -> g12) x7
    c: InternalAlignment(g13-g17 -> g12) x5
    c: Block(g12)
    c: Coincident(g18,g12)
    c: Block(g18)
    c: Coincident(g20,g2)
    c: Coincident(g20,g19)
    c: Horizontal(g20)
    c: Distance(g20) = 93.4
    c: Coincident(g21,g1)
    c: Horizontal(g21)
    c: Distance(g21) = 101.7
    c: Horizontal(g23)
    c: Distance(g23) = 8
    c: Coincident(g24,g23)
    c: Block(g23)
    c: Coincident(g22,g24)
    c: Block(g24)
    c: Block(g22)
    c: Distance(g22) = 1.61553
    c: Coincident(g25,g18)
    c: Block(g25)
    c: Weight(g26) = 1
    c: Equal(g26,g27)
    c: Equal(g26,g28)
    c: Coincident(g29,g4)
    c: InternalAlignment(g26,g29)
    c: InternalAlignment(g27,g29)
    c: InternalAlignment(g28,g29)
    c: InternalAlignment(g30,g29)
    c: InternalAlignment(g31,g29)
    c: Block(g29)
    c: Weight(g32) = 1
    c: Equal(g32,g33)
    c: Equal(g32,g34)
    c: Coincident(g35,g29)
    c: InternalAlignment(g32,g35)
    c: InternalAlignment(g33,g35)
    c: InternalAlignment(g34,g35)
    c: InternalAlignment(g36,g35)
    c: InternalAlignment(g37,g35)
    c: Block(g35)
    c: Coincident(g38,g35)
    c: Vertical(g38)
    c: Block(g38)
    c: Coincident(g42,g38)
    c: Weight(g39) = 1
    c: Equal(g39,g40)
    c: Equal(g39,g41)
    c: Coincident(g42,g25)
    c: InternalAlignment(g39,g42)
    c: InternalAlignment(g40,g42)
    c: InternalAlignment(g41,g42)
    c: InternalAlignment(g43,g42)
    c: InternalAlignment(g44,g42)
    c: Block(g42)
FEATURE [Part::Extrusion] Extrude043  label="bottom010"
  Base = -> Sketch052
  Dir = (0,0,1)
  DirMode = 2
  FaceMakerClass = Part::FaceMakerBullseye
  LengthFwd = 71.4
  LengthRev = 0
  Placement = pos=(0,0,0.3) rot=(0,0,1;0rad)
  Solid = true
  Symmetric = false
FEATURE [Sketcher::SketchObject] Sketch053  label="topSketch013"
  FullyConstrained = true
  sketch-geometry (22):
    g0: LineSegment StartX=5.21097e-06 StartY=3 StartZ=0 EndX=5.21097e-06 EndY=19 EndZ=0
    g1: ArcOfCircle CenterX=19 CenterY=19 CenterZ=0 NormalX=0 NormalY=0 NormalZ=1 AngleXU=0 Radius=19 StartAngle=1.5708 EndAngle=3.14159
    g2: ArcOfCircle CenterX=19 CenterY=19 CenterZ=0 NormalX=0 NormalY=0 NormalZ=1 AngleXU=0 Radius=16 StartAngle=1.5708 EndAngle=3.14159
    g3: LineSegment StartX=114 StartY=35 StartZ=0 EndX=19 EndY=35 EndZ=0
    g4: LineSegment StartX=5.21097e-06 StartY=3 StartZ=0 EndX=5.21097e-06 EndY=0 EndZ=0
    g5: LineSegment StartX=3 StartY=0 StartZ=0 EndX=5.21097e-06 EndY=0 EndZ=0
    g6: LineSegment StartX=3 StartY=19 StartZ=0 EndX=3 EndY=0 EndZ=0
    g7: LineSegment StartX=19 StartY=38 StartZ=0 EndX=124 EndY=38 EndZ=0
    g8: Circle CenterX=119 CenterY=35 CenterZ=0 NormalX=0 NormalY=0 NormalZ=1 AngleXU=0 Radius=1
    g9: Circle CenterX=121 CenterY=35 CenterZ=0 NormalX=0 NormalY=0 NormalZ=1 AngleXU=0 Radius=1
    g10: Circle CenterX=121 CenterY=33 CenterZ=0 NormalX=0 NormalY=0 NormalZ=1 AngleXU=0 Radius=1
    g11: BSplineCurve PolesCount=3 KnotsCount=2 Degree=2 IsPeriodic=0
    g12: GeomPoint X=119 Y=35 Z=0
    g13: GeomPoint X=121 Y=33 Z=0
    g14: LineSegment StartX=119 StartY=35 StartZ=0 EndX=114 EndY=35 EndZ=0
    g15: ArcOfCircle CenterX=105 CenterY=19 CenterZ=0 NormalX=0 NormalY=0 NormalZ=1 AngleXU=0 Radius=16 StartAngle=5.60905 EndAngle=6.28319
    g16: LineSegment StartX=121 StartY=33 StartZ=0 EndX=121 EndY=19 EndZ=0
    g17: LineSegment StartX=117.5 StartY=9.01251 StartZ=0 EndX=121.163 EndY=9.0125 EndZ=0
    g18: ArcOfCircle CenterX=105 CenterY=19 CenterZ=0 NormalX=0 NormalY=0 NormalZ=1 AngleXU=0 Radius=20.6155 StartAngle=5.7297 EndAngle=6.28319
    g19: LineSegment StartX=121.163 StartY=9.0125 StartZ=0 EndX=122.538 EndY=8.16329 EndZ=0
    g20: LineSegment StartX=124 StartY=38 StartZ=0 EndX=125.616 EndY=38 EndZ=0
    g21: LineSegment StartX=125.616 StartY=19 StartZ=0 EndX=125.616 EndY=38 EndZ=0
  constraints (50):
    c: Vertical(g0)
    c: Block(g0)
    c: Coincident(g1,g0)
    c: Block(g1)
    c: Coincident(g2,g1)
    c: Block(g2)
    c: Coincident(g3,g2)
    c: Horizontal(g3)
    c: Tangent(g3,g2)
    c: Coincident(g4,g0)
    c: Distance(g4) = 3
    c: Vertical(g4)
    c: Coincident(g5,g4)
    c: Horizontal(g5)
    c: Coincident(g6,g2)
    c: Coincident(g6,g5)
    c: Vertical(g6)
    c: Horizontal(g7)
    c: Distance(g7) = 105
    c: Coincident(g7,g1)
    c: Block(g3)
    c: Weight(g8) = 1
    c: Equal(g8,g9)
    c: Equal(g8,g10)
    c: InternalAlignment(g8,g11)
    c: InternalAlignment(g9,g11)
    c: InternalAlignment(g10,g11)
    c: InternalAlignment(g12,g11)
    c: InternalAlignment(g13,g11)
    c: Block(g11)
    c: Coincident(g14,g11)
    c: Coincident(g14,g3)
    c: Horizontal(g14)
    c: Block(g15)
    c: Coincident(g16,g11)
    c: Coincident(g16,g15)
    c: Vertical(g16)
    c: Distance(g16) = 14
    c: Coincident(g17,g15)
    c: Block(g18)
    c: Coincident(g19,g18)
    c: Coincident(g20,g7)
    c: Horizontal(g20)
    c: Vertical(g21)
    c: Coincident(g20,g21)
    c: Block(g20)
    c: Block(g21)
    c: Block(g19)
    c: Block(g17)
    c: Distance(g20) = 1.61553
FEATURE [Part::Extrusion] Extrude044
  Base = -> Sketch053
  Dir = (0,0,1)
  DirMode = 2
  FaceMakerClass = Part::FaceMakerBullseye
  LengthFwd = 72
  LengthRev = 0
  Solid = true
  Symmetric = false
FEATURE [Part::Fillet] Fillet036  label="top018"
  Base = -> Extrude044
  Edges = 1 edges r=2: [Edge41]
FEATURE [Sketcher::SketchObject] Sketch054
  FullyConstrained = false
  Placement = pos=(0,0,0) rot=(1,0,0;1.5708rad)
  sketch-geometry (24):
    g0: ArcOfCircle CenterX=-4 CenterY=-10.5 CenterZ=0 NormalX=0 NormalY=0 NormalZ=1 AngleXU=0 Radius=1.5 StartAngle=6e-16 EndAngle=3.14159
    g1: ArcOfCircle CenterX=-34.2 CenterY=-10.5 CenterZ=0 NormalX=0 NormalY=0 NormalZ=1 AngleXU=0 Radius=1.5 StartAngle=0 EndAngle=3.14159
    g2: ArcOfCircle CenterX=-34.2 CenterY=-27.7 CenterZ=0 NormalX=0 NormalY=0 NormalZ=1 AngleXU=0 Radius=1.5 StartAngle=3.14159 EndAngle=6.28319
    g3: ArcOfCircle CenterX=-4 CenterY=-27.7 CenterZ=0 NormalX=0 NormalY=0 NormalZ=1 AngleXU=0 Radius=1.5 StartAngle=3.1416 EndAngle=6.28319
    g4: ArcOfCircle CenterX=-10 CenterY=-4.3 CenterZ=0 NormalX=0 NormalY=0 NormalZ=1 AngleXU=0 Radius=1.5 StartAngle=2e-16 EndAngle=3.14159
    g5: ArcOfCircle CenterX=-16.1 CenterY=-1.8 CenterZ=0 NormalX=0 NormalY=0 NormalZ=1 AngleXU=0 Radius=1.5 StartAngle=5e-16 EndAngle=3.14159
    g6: ArcOfCircle CenterX=-22.1 CenterY=-1.8 CenterZ=0 NormalX=0 NormalY=0 NormalZ=1 AngleXU=0 Radius=1.5 StartAngle=5e-16 EndAngle=3.14159
    g7: ArcOfCircle CenterX=-28.2 CenterY=-4.3 CenterZ=0 NormalX=0 NormalY=0 NormalZ=1 AngleXU=0 Radius=1.5 StartAngle=2e-16 EndAngle=3.14159
    g8: ArcOfCircle CenterX=-10 CenterY=-33.9 CenterZ=0 NormalX=0 NormalY=0 NormalZ=1 AngleXU=0 Radius=1.5 StartAngle=3.14159 EndAngle=6.28319
    g9: ArcOfCircle CenterX=-16.1 CenterY=-36.4 CenterZ=0 NormalX=0 NormalY=0 NormalZ=1 AngleXU=0 Radius=1.5 StartAngle=3.14159 EndAngle=6.28319
    g10: ArcOfCircle CenterX=-22.1 CenterY=-36.4 CenterZ=0 NormalX=0 NormalY=0 NormalZ=1 AngleXU=0 Radius=1.5 StartAngle=3.14159 EndAngle=6.28319
    g11: ArcOfCircle CenterX=-28.2 CenterY=-33.9 CenterZ=0 NormalX=0 NormalY=0 NormalZ=1 AngleXU=0 Radius=1.5 StartAngle=3.14159 EndAngle=6.28319
    g12: LineSegment StartX=-35.7 StartY=-10.5 StartZ=0 EndX=-35.7 EndY=-27.7 EndZ=0
    g13: LineSegment StartX=-32.7 StartY=-10.5 StartZ=0 EndX=-32.7 EndY=-27.7 EndZ=0
    g14: LineSegment StartX=-29.7 StartY=-33.9 StartZ=0 EndX=-29.7 EndY=-4.3 EndZ=0
    g15: LineSegment StartX=-26.7 StartY=-33.9 StartZ=0 EndX=-26.7 EndY=-4.3 EndZ=0
    g16: LineSegment StartX=-2.5 StartY=-10.5 StartZ=0 EndX=-2.5 EndY=-27.7 EndZ=0
    g17: LineSegment StartX=-8.5 StartY=-4.3 StartZ=0 EndX=-8.5 EndY=-33.9 EndZ=0
    g18: LineSegment StartX=-5.5 StartY=-10.5 StartZ=0 EndX=-5.5 EndY=-27.7 EndZ=0
    g19: LineSegment StartX=-11.5 StartY=-4.3 StartZ=0 EndX=-11.5 EndY=-33.9 EndZ=0
    g20: LineSegment StartX=-14.6 StartY=-1.8 StartZ=0 EndX=-14.6 EndY=-36.4 EndZ=0
    g21: LineSegment StartX=-17.6 StartY=-1.8 StartZ=0 EndX=-17.6 EndY=-36.4 EndZ=0
    g22: LineSegment StartX=-20.6 StartY=-36.4 StartZ=0 EndX=-20.6 EndY=-1.8 EndZ=0
    g23: LineSegment StartX=-23.6 StartY=-1.8 StartZ=0 EndX=-23.6 EndY=-36.4 EndZ=0
  constraints (48):
    c: Block(g0)
    c: Block(g1)
    c: Block(g2)
    c: Block(g3)
    c: Block(g4)
    c: Block(g5)
    c: Block(g6)
    c: Block(g7)
    c: Block(g8)
    c: Block(g9)
    c: Block(g10)
    c: Block(g11)
    c: Coincident(g12,g1)
    c: Coincident(g12,g2)
    c: Vertical(g12)
    c: Coincident(g13,g1)
    c: Coincident(g13,g2)
    c: Vertical(g13)
    c: Coincident(g14,g11)
    c: Coincident(g14,g7)
    c: Vertical(g14)
    c: Coincident(g15,g11)
    c: Coincident(g15,g7)
    c: Vertical(g15)
    c: Coincident(g16,g0)
    c: Coincident(g16,g3)
    c: Vertical(g16)
    c: Coincident(g17,g4)
    c: Coincident(g17,g8)
    c: Vertical(g17)
    c: Coincident(g18,g0)
    c: Coincident(g18,g3)
    c: Vertical(g18)
    c: Coincident(g19,g4)
    c: Coincident(g19,g8)
    c: Vertical(g19)
    c: Coincident(g20,g5)
    c: Coincident(g20,g9)
    c: Vertical(g20)
    c: Coincident(g21,g5)
    c: Coincident(g21,g9)
    c: Vertical(g21)
    c: Coincident(g22,g10)
    c: Coincident(g22,g6)
    c: Vertical(g22)
    c: Coincident(g23,g6)
    c: Coincident(g23,g10)
    c: Vertical(g23)
FEATURE [Part::Extrusion] Extrude045  label="removeToCreateFanGrillHoles003"
  Base = -> Sketch054
  Dir = (0,-1,6e-16)
  DirMode = 2
  FaceMakerClass = Part::FaceMakerBullseye
  LengthFwd = 10
  LengthRev = 0
  Placement = pos=(65.4,44,54.82) rot=(0,0,1;0rad)
  Solid = true
  Symmetric = false
FEATURE [Part::Feature] Face105 .. Face108  x4 (patterned run collapsed; names and placements below)
  shape: bbox 3.5 x 17.8 x 2e-07 mm, 1 faces, 0 solids (baked)
FEATURE [Part::Revolution] Revolve113  label="removeToCreateScrewAndThreadedInsertHole041"
  Angle = 360
  Axis = (0,1,0)
  Base = (0,0,0)
  FaceMakerClass = Part::FaceMakerBullseye
  Placement = pos=(62.3,30.3,19.7) rot=(0,0,1;0rad)
  Solid = false
  Source = -> Face105
  Symmetric = false
FEATURE [Part::Revolution] Revolve114  label="removeToCreateScrewAndThreadedInsertHole042"
  Angle = 360
  Axis = (0,1,0)
  Base = (0,0,0)
  FaceMakerClass = Part::FaceMakerBullseye
  Placement = pos=(62.3,30.3,51.7) rot=(0,0,1;0rad)
  Solid = false
  Source = -> Face106
  Symmetric = false
FEATURE [Part::Revolution] Revolve115  label="removeToCreateScrewAndThreadedInsertHole043"
  Angle = 360
  Axis = (0,1,0)
  Base = (0,0,0)
  FaceMakerClass = Part::FaceMakerBullseye
  Placement = pos=(30.3,30.3,19.7) rot=(0,0,1;0rad)
  Solid = false
  Source = -> Face107
  Symmetric = false
FEATURE [Part::Revolution] Revolve116  label="removeToCreateScrewAndThreadedInsertHole044"
  Angle = 360
  Axis = (0,1,0)
  Base = (0,0,0)
  FaceMakerClass = Part::FaceMakerBullseye
  Placement = pos=(30.3,30.3,51.7) rot=(0,0,1;0rad)
  Solid = false
  Source = -> Face108
  Symmetric = false
FEATURE [Part::MultiFuse] Fusion083  label="createThreadedInsertHolesForFan004"
  Shapes = -> [Revolve113,Revolve114,Revolve115,Revolve116]
FEATURE [Part::Box] Box024  label="removeToCreteHoleForPlugHousing026"
  AttacherType = Attacher::AttachEngine3D
  Height = 28.6
  Length = 10
  Placement = pos=(-2,0,21.7) rot=(0,0,1;0rad)
  Width = 19
FEATURE [Part::Cylinder] Cylinder038  label="removeToCreteHoleForPlugHousing027"
  Angle = 360
  AttacherType = Attacher::AttachEngine3D
  Height = 20
  Placement = pos=(-2,19,36) rot=(0,1,0;1.5708rad)
  Radius = 14.3
FEATURE [Part::MultiFuse] Fusion084  label="removeToCreteHoleForPlugHousing028"
  Shapes = -> [Box024,Cylinder038]
FEATURE [Part::Cylinder] Cylinder039
  Angle = 360
  AttacherType = Attacher::AttachEngine3D
  Height = 20
  Placement = pos=(0,0,36.15) rot=(0,0,1;0rad)
  Radius = 14.3
FEATURE [Part::Cylinder] Cylinder040
  Angle = 360
  AttacherType = Attacher::AttachEngine3D
  Height = 10
  Placement = pos=(0,0,36.15) rot=(0,0,1;0rad)
  Radius = 4
FEATURE [Part::Box] Box025  label="removeToCreteHoleForPlugHousing030"
  AttacherType = Attacher::AttachEngine3D
  Height = 28.6
  Length = 20
  Placement = pos=(106.15,0,21.7) rot=(0,0,1;0rad)
  Width = 19
FEATURE [Part::MultiFuse] Fusion086  label="removeToCreteHoleForPlugHousing031"
  Placement = pos=(70,19,36) rot=(0,1,0;1.5708rad)
  Shapes = -> [Cylinder039,Cylinder040]
FEATURE [Part::MultiFuse] Fusion085  label="removeToCreteHoleForPlugHousing029"
  Shapes = -> [Box025,Fusion086]
FEATURE [Sketcher::SketchObject] Sketch055
  FullyConstrained = true
  Placement = pos=(117,19,0) rot=(0.57735,0.57735,0.57735;2.0944rad)
  sketch-geometry (48):
    g0: LineSegment StartX=-49.19 StartY=69.25 StartZ=0 EndX=-49.19 EndY=66.25 EndZ=0
    g1: LineSegment StartX=-49.19 StartY=63.5 StartZ=0 EndX=-49.19 EndY=60.5 EndZ=0
    g2: LineSegment StartX=-49.19 StartY=57.75 StartZ=0 EndX=-49.19 EndY=54.75 EndZ=0
    g3: LineSegment StartX=-49.19 StartY=52 StartZ=0 EndX=-49.19 EndY=49 EndZ=0
    g4: LineSegment StartX=-49.19 StartY=46.25 StartZ=0 EndX=-49.19 EndY=43.25 EndZ=0
    g5: LineSegment StartX=-49.19 StartY=40.5 StartZ=0 EndX=-49.19 EndY=37.5 EndZ=0
    g6: LineSegment StartX=-49.19 StartY=34.5 StartZ=0 EndX=-49.19 EndY=31.5 EndZ=0
    g7: LineSegment StartX=-49.19 StartY=28.75 StartZ=0 EndX=-49.19 EndY=25.75 EndZ=0
    g8: LineSegment StartX=-49.19 StartY=23 StartZ=0 EndX=-49.19 EndY=20 EndZ=0
    g9: LineSegment StartX=-49.19 StartY=17.25 StartZ=0 EndX=-49.19 EndY=14.25 EndZ=0
    g10: LineSegment StartX=-49.19 StartY=11.5 StartZ=0 EndX=-49.19 EndY=8.5 EndZ=0
    g11: LineSegment StartX=-49.19 StartY=5.75 StartZ=0 EndX=-49.19 EndY=2.75 EndZ=0
    g12: ArcOfCircle CenterX=-1.5 CenterY=67.75 CenterZ=0 NormalX=0 NormalY=0 NormalZ=1 AngleXU=0 Radius=1.5 StartAngle=4.71239 EndAngle=7.85398
    g13: ArcOfCircle CenterX=-1.5 CenterY=62 CenterZ=0 NormalX=0 NormalY=0 NormalZ=1 AngleXU=0 Radius=1.5 StartAngle=4.71239 EndAngle=7.85398
    g14: ArcOfCircle CenterX=-1.5 CenterY=56.25 CenterZ=0 NormalX=0 NormalY=0 NormalZ=1 AngleXU=0 Radius=1.5 StartAngle=4.71239 EndAngle=7.85398
    g15: ArcOfCircle CenterX=-11.49 CenterY=50.5 CenterZ=0 NormalX=0 NormalY=0 NormalZ=1 AngleXU=0 Radius=1.5 StartAngle=4.71239 EndAngle=7.85398
    g16: ArcOfCircle CenterX=-16.28 CenterY=44.75 CenterZ=0 NormalX=0 NormalY=0 NormalZ=1 AngleXU=0 Radius=1.5 StartAngle=4.71239 EndAngle=7.85398
    g17: ArcOfCircle CenterX=-18.2337 CenterY=39 CenterZ=0 NormalX=0 NormalY=0 NormalZ=1 AngleXU=0 Radius=1.5 StartAngle=4.71485 EndAngle=7.85398
    g18: ArcOfCircle CenterX=-16.2837 CenterY=27.25 CenterZ=0 NormalX=0 NormalY=0 NormalZ=1 AngleXU=0 Radius=1.5 StartAngle=4.71485 EndAngle=7.85398
    g19: ArcOfCircle CenterX=-18.2337 CenterY=33 CenterZ=0 NormalX=0 NormalY=0 NormalZ=1 AngleXU=0 Radius=1.5 StartAngle=4.71485 EndAngle=7.85398
    g20: ArcOfCircle CenterX=-11.49 CenterY=21.5 CenterZ=0 NormalX=0 NormalY=0 NormalZ=1 AngleXU=0 Radius=1.5 StartAngle=4.71239 EndAngle=7.85398
    g21: ArcOfCircle CenterX=-1.5 CenterY=4.25 CenterZ=0 NormalX=0 NormalY=0 NormalZ=1 AngleXU=0 Radius=1.5 StartAngle=4.71239 EndAngle=7.85398
    g22: ArcOfCircle CenterX=-1.5 CenterY=10 CenterZ=0 NormalX=0 NormalY=0 NormalZ=1 AngleXU=0 Radius=1.5 StartAngle=4.71239 EndAngle=7.85398
    g23: ArcOfCircle CenterX=-1.5 CenterY=15.75 CenterZ=0 NormalX=0 NormalY=0 NormalZ=1 AngleXU=0 Radius=1.5 StartAngle=4.71239 EndAngle=7.85398
    g24: LineSegment StartX=-49.19 StartY=69.25 StartZ=0 EndX=-1.5 EndY=69.25 EndZ=0
    g25: LineSegment StartX=-49.19 StartY=66.25 StartZ=0 EndX=-1.5 EndY=66.25 EndZ=0
    g26: LineSegment StartX=-49.19 StartY=63.5 StartZ=0 EndX=-1.5 EndY=63.5 EndZ=0
    g27: LineSegment StartX=-49.19 StartY=60.5 StartZ=0 EndX=-1.5 EndY=60.5 EndZ=0
    g28: LineSegment StartX=-49.19 StartY=57.75 StartZ=0 EndX=-1.5 EndY=57.75 EndZ=0
    g29: LineSegment StartX=-49.19 StartY=54.75 StartZ=0 EndX=-1.5 EndY=54.75 EndZ=0
    g30: LineSegment StartX=-49.19 StartY=52 StartZ=0 EndX=-11.49 EndY=52 EndZ=0
    g31: LineSegment StartX=-49.19 StartY=49 StartZ=0 EndX=-11.49 EndY=49 EndZ=0
    g32: LineSegment StartX=-49.19 StartY=46.25 StartZ=0 EndX=-16.28 EndY=46.25 EndZ=0
    g33: LineSegment StartX=-49.19 StartY=43.25 StartZ=0 EndX=-16.28 EndY=43.25 EndZ=0
    g34: LineSegment StartX=-49.19 StartY=40.5 StartZ=0 EndX=-18.2337 EndY=40.5 EndZ=0
    g35: LineSegment StartX=-49.19 StartY=37.5 StartZ=0 EndX=-18.23 EndY=37.5 EndZ=0
    g36: LineSegment StartX=-49.19 StartY=34.5 StartZ=0 EndX=-18.2337 EndY=34.5 EndZ=0
    g37: LineSegment StartX=-49.19 StartY=31.5 StartZ=0 EndX=-18.23 EndY=31.5 EndZ=0
    g38: LineSegment StartX=-49.19 StartY=28.75 StartZ=0 EndX=-16.2837 EndY=28.75 EndZ=0
    g39: LineSegment StartX=-49.19 StartY=25.75 StartZ=0 EndX=-16.28 EndY=25.75 EndZ=0
    g40: LineSegment StartX=-49.19 StartY=23 StartZ=0 EndX=-11.49 EndY=23 EndZ=0
    g41: LineSegment StartX=-49.19 StartY=20 StartZ=0 EndX=-11.49 EndY=20 EndZ=0
    g42: LineSegment StartX=-49.19 StartY=17.25 StartZ=0 EndX=-1.5 EndY=17.25 EndZ=0
    g43: LineSegment StartX=-49.19 StartY=14.25 StartZ=0 EndX=-1.5 EndY=14.25 EndZ=0
    g44: LineSegment StartX=-49.19 StartY=11.5 StartZ=0 EndX=-1.5 EndY=11.5 EndZ=0
    g45: LineSegment StartX=-49.19 StartY=8.5 StartZ=0 EndX=-1.5 EndY=8.5 EndZ=0
    g46: LineSegment StartX=-49.19 StartY=5.75 StartZ=0 EndX=-1.5 EndY=5.75 EndZ=0
    g47: LineSegment StartX=-49.19 StartY=2.75 StartZ=0 EndX=-1.5 EndY=2.75 EndZ=0
  constraints (120):
    c: Vertical(g0)
    c: Distance(g0) = 3
    c: Block(g0)
    c: Vertical(g1)
    c: Distance(g1) = 3
    c: Vertical(g2)
    c: Equal(g0,g2) = 3
    c: Block(g2)
    c: Vertical(g3)
    c: Equal(g1,g3) = 3
    c: Vertical(g4)
    c: Equal(g0,g4) = 3
    c: Block(g4)
    c: Vertical(g5)
    c: Equal(g1,g5) = 3
    c: Vertical(g6)
    c: Equal(g0,g6) = 3
    c: Block(g6)
    c: Vertical(g7)
    c: Equal(g1,g7) = 3
    c: Vertical(g8)
    c: Equal(g0,g8) = 3
    c: Block(g8)
    c: Vertical(g9)
    c: Equal(g1,g9) = 3
    c: Vertical(g10)
    c: Equal(g0,g10) = 3
    c: Block(g10)
    c: Vertical(g11)
    c: Equal(g1,g11) = 3
    c: Block(g12)
    c: Block(g13)
    c: Block(g14)
    c: Block(g15)
    c: Block(g16)
    c: Block(g17)
    c: Block(g18)
    c: Block(g19)
    c: Block(g20)
    c: Block(g21)
    c: Block(g22)
    c: Block(g23)
    c: Block(g11)
    c: Block(g9)
    c: Block(g7)
    c: Block(g5)
    c: Block(g3)
    c: Block(g1)
    c: Coincident(g24,g0)
    c: Coincident(g24,g12)
    c: Horizontal(g24)
    c: Coincident(g25,g0)
    c: Coincident(g25,g12)
    c: Horizontal(g25)
    c: Coincident(g26,g1)
    c: Coincident(g26,g13)
    c: Horizontal(g26)
    c: Coincident(g27,g1)
    c: Coincident(g27,g13)
    c: Horizontal(g27)
    c: Coincident(g28,g2)
    c: Coincident(g28,g14)
    c: Horizontal(g28)
    c: Coincident(g29,g2)
    c: Coincident(g29,g14)
    c: Horizontal(g29)
    c: Coincident(g30,g3)
    c: Coincident(g30,g15)
    c: Horizontal(g30)
    c: Coincident(g31,g3)
    c: Coincident(g31,g15)
    c: Horizontal(g31)
    c: Coincident(g32,g4)
    c: Coincident(g32,g16)
    c: Horizontal(g32)
    c: Coincident(g33,g4)
    c: Coincident(g33,g16)
    c: Horizontal(g33)
    c: Coincident(g34,g5)
    c: Coincident(g34,g17)
    c: Horizontal(g34)
    c: Coincident(g35,g5)
    c: Coincident(g35,g17)
    c: Horizontal(g35)
    c: Coincident(g36,g6)
    c: Coincident(g36,g19)
    c: Horizontal(g36)
    c: Coincident(g37,g6)
    c: Coincident(g37,g19)
    c: Horizontal(g37)
    c: Coincident(g38,g7)
    c: Coincident(g38,g18)
    c: Horizontal(g38)
    c: Coincident(g39,g7)
    c: Coincident(g39,g18)
    c: Horizontal(g39)
    c: Coincident(g40,g8)
    c: Coincident(g40,g20)
    c: Horizontal(g40)
    c: Coincident(g41,g8)
    c: Coincident(g41,g20)
    c: Horizontal(g41)
    c: Coincident(g42,g9)
    c: Coincident(g42,g23)
    c: Horizontal(g42)
    c: Coincident(g43,g9)
    c: Coincident(g43,g23)
    c: Horizontal(g43)
    c: Coincident(g44,g10)
    c: Coincident(g44,g22)
    c: Horizontal(g44)
    c: Coincident(g45,g10)
    c: Coincident(g45,g22)
    c: Horizontal(g45)
    c: Coincident(g46,g11)
    c: Coincident(g46,g21)
    c: Horizontal(g46)
    c: Coincident(g47,g11)
    c: Coincident(g47,g21)
    c: Horizontal(g47)
FEATURE [Part::Extrusion] Extrude046
  Base = -> Sketch055
  Dir = (1,0,0)
  DirMode = 2
  FaceMakerClass = Part::FaceMakerBullseye
  LengthFwd = 23
  LengthRev = 0
  Placement = pos=(-19,0,0) rot=(0,0,1;0rad)
  Solid = true
  Symmetric = false
FEATURE [Part::Fillet] Fillet038  label="removeToCreateVentalationHoles001"
  Base = -> Extrude046
  Edges = <same value as first occurrence — deduplicated (x6 in doc)>
  Placement = pos=(7,0,0) rot=(0,0,1;0rad)
FEATURE [Sketcher::SketchObject] Sketch056  label="topSketch014"
  FullyConstrained = true
  sketch-geometry (22):
    g0: LineSegment StartX=5.21097e-06 StartY=3 StartZ=0 EndX=5.21097e-06 EndY=19 EndZ=0
    g1: ArcOfCircle CenterX=19 CenterY=19 CenterZ=0 NormalX=0 NormalY=0 NormalZ=1 AngleXU=0 Radius=19 StartAngle=1.5708 EndAngle=3.14159
    g2: ArcOfCircle CenterX=19 CenterY=19 CenterZ=0 NormalX=0 NormalY=0 NormalZ=1 AngleXU=0 Radius=16 StartAngle=1.5708 EndAngle=3.14159
    g3: LineSegment StartX=114 StartY=35 StartZ=0 EndX=19 EndY=35 EndZ=0
    g4: LineSegment StartX=5.21097e-06 StartY=3 StartZ=0 EndX=5.21097e-06 EndY=0 EndZ=0
    g5: LineSegment StartX=3 StartY=0 StartZ=0 EndX=5.21097e-06 EndY=0 EndZ=0
    g6: LineSegment StartX=3 StartY=19 StartZ=0 EndX=3 EndY=0 EndZ=0
    g7: LineSegment StartX=19 StartY=38 StartZ=0 EndX=124 EndY=38 EndZ=0
    g8: Circle CenterX=119 CenterY=35 CenterZ=0 NormalX=0 NormalY=0 NormalZ=1 AngleXU=0 Radius=1
    g9: Circle CenterX=121 CenterY=35 CenterZ=0 NormalX=0 NormalY=0 NormalZ=1 AngleXU=0 Radius=1
    g10: Circle CenterX=121 CenterY=33 CenterZ=0 NormalX=0 NormalY=0 NormalZ=1 AngleXU=0 Radius=1
    g11: BSplineCurve PolesCount=3 KnotsCount=2 Degree=2 IsPeriodic=0
    g12: GeomPoint X=119 Y=35 Z=0
    g13: GeomPoint X=121 Y=33 Z=0
    g14: LineSegment StartX=119 StartY=35 StartZ=0 EndX=114 EndY=35 EndZ=0
    g15: ArcOfCircle CenterX=105 CenterY=19 CenterZ=0 NormalX=0 NormalY=0 NormalZ=1 AngleXU=0 Radius=16 StartAngle=5.60905 EndAngle=6.28319
    g16: LineSegment StartX=121 StartY=33 StartZ=0 EndX=121 EndY=19 EndZ=0
    g17: LineSegment StartX=117.5 StartY=9.01251 StartZ=0 EndX=121.163 EndY=9.0125 EndZ=0
    g18: ArcOfCircle CenterX=105 CenterY=19 CenterZ=0 NormalX=0 NormalY=0 NormalZ=1 AngleXU=0 Radius=20.6155 StartAngle=5.7297 EndAngle=6.28319
    g19: LineSegment StartX=121.163 StartY=9.0125 StartZ=0 EndX=122.538 EndY=8.16329 EndZ=0
    g20: LineSegment StartX=124 StartY=38 StartZ=0 EndX=125.616 EndY=38 EndZ=0
    g21: LineSegment StartX=125.616 StartY=19 StartZ=0 EndX=125.616 EndY=38 EndZ=0
  constraints (49):
    c: Vertical(g0)
    c: Block(g0)
    c: Coincident(g1,g0)
    c: Block(g1)
    c: Coincident(g2,g1)
    c: Block(g2)
    c: Coincident(g3,g2)
    c: Horizontal(g3)
    c: Tangent(g3,g2)
    c: Coincident(g4,g0)
    c: Distance(g4) = 3
    c: Vertical(g4)
    c: Coincident(g5,g4)
    c: Horizontal(g5)
    c: Coincident(g6,g2)
    c: Coincident(g6,g5)
    c: Vertical(g6)
    c: Horizontal(g7)
    c: Distance(g7) = 105
    c: Coincident(g7,g1)
    c: Block(g3)
    c: Weight(g8) = 1
    c: Equal(g8,g9)
    c: Equal(g8,g10)
    c: InternalAlignment(g8,g11)
    c: InternalAlignment(g9,g11)
    c: InternalAlignment(g10,g11)
    c: InternalAlignment(g12,g11)
    c: InternalAlignment(g13,g11)
    c: Block(g11)
    c: Coincident(g14,g11)
    c: Coincident(g14,g3)
    c: Horizontal(g14)
    c: Block(g15)
    c: Coincident(g16,g11)
    c: Coincident(g16,g15)
    c: Vertical(g16)
    c: Distance(g16) = 14
    c: Coincident(g17,g15)
    c: Block(g18)
    c: Coincident(g19,g18)
    c: Coincident(g20,g7)
    c: Horizontal(g20)
    c: Vertical(g21)
    c: Coincident(g20,g21)
    c: Block(g20)
    c: Block(g21)
    c: Block(g19)
    c: Block(g17)
FEATURE [Part::Box] Box026  label="removeToCreteHoleForPlugHousing032"
  AttacherType = Attacher::AttachEngine3D
  Height = 28.6
  Length = 10
  Placement = pos=(-2,0,21.7) rot=(0,0,1;0rad)
  Width = 19
FEATURE [Part::Feature] Face109 .. Face112  x4 (patterned run collapsed; names and placements below)
  shape: bbox 3.5 x 17.8 x 2e-07 mm, 1 faces, 0 solids (baked)
FEATURE [Part::Revolution] Revolve117  label="removeToCreateScrewAndThreadedInsertHole045"
  Angle = 360
  Axis = (0,1,0)
  Base = (0,0,0)
  FaceMakerClass = Part::FaceMakerBullseye
  Placement = pos=(62.3,30.3,19.7) rot=(0,0,1;0rad)
  Solid = false
  Source = -> Face109
  Symmetric = false
FEATURE [Part::Revolution] Revolve118  label="removeToCreateScrewAndThreadedInsertHole046"
  Angle = 360
  Axis = (0,1,0)
  Base = (0,0,0)
  FaceMakerClass = Part::FaceMakerBullseye
  Placement = pos=(62.3,30.3,51.7) rot=(0,0,1;0rad)
  Solid = false
  Source = -> Face110
  Symmetric = false
FEATURE [Part::Revolution] Revolve119  label="removeToCreateScrewAndThreadedInsertHole047"
  Angle = 360
  Axis = (0,1,0)
  Base = (0,0,0)
  FaceMakerClass = Part::FaceMakerBullseye
  Placement = pos=(30.3,30.3,19.7) rot=(0,0,1;0rad)
  Solid = false
  Source = -> Face111
  Symmetric = false
FEATURE [Part::Revolution] Revolve120  label="removeToCreateScrewAndThreadedInsertHole048"
  Angle = 360
  Axis = (0,1,0)
  Base = (0,0,0)
  FaceMakerClass = Part::FaceMakerBullseye
  Placement = pos=(30.3,30.3,51.7) rot=(0,0,1;0rad)
  Solid = false
  Source = -> Face112
  Symmetric = false
FEATURE [Part::MultiFuse] Fusion087  label="createThreadedInsertHolesForFan005"
  Shapes = -> [Revolve117,Revolve118,Revolve119,Revolve120]
FEATURE [Part::Extrusion] Extrude047
  Base = -> Sketch056
  Dir = (0,0,1)
  DirMode = 2
  FaceMakerClass = Part::FaceMakerBullseye
  LengthFwd = 72
  LengthRev = 0
  Solid = true
  Symmetric = false
FEATURE [Part::Fillet] Fillet039  label="top019"
  Base = -> Extrude047
  Edges = 1 edges r=2: [Edge35]
FEATURE [Sketcher::SketchObject] Sketch057
  FullyConstrained = false
  Placement = pos=(0,0,0) rot=(1,0,0;1.5708rad)
  sketch-geometry (24):
    g0: ArcOfCircle CenterX=-4 CenterY=-10.5 CenterZ=0 NormalX=0 NormalY=0 NormalZ=1 AngleXU=0 Radius=1.5 StartAngle=6e-16 EndAngle=3.14159
    g1: ArcOfCircle CenterX=-34.2 CenterY=-10.5 CenterZ=0 NormalX=0 NormalY=0 NormalZ=1 AngleXU=0 Radius=1.5 StartAngle=0 EndAngle=3.14159
    g2: ArcOfCircle CenterX=-34.2 CenterY=-27.7 CenterZ=0 NormalX=0 NormalY=0 NormalZ=1 AngleXU=0 Radius=1.5 StartAngle=3.14159 EndAngle=6.28319
    g3: ArcOfCircle CenterX=-4 CenterY=-27.7 CenterZ=0 NormalX=0 NormalY=0 NormalZ=1 AngleXU=0 Radius=1.5 StartAngle=3.1416 EndAngle=6.28319
    g4: ArcOfCircle CenterX=-10 CenterY=-4.3 CenterZ=0 NormalX=0 NormalY=0 NormalZ=1 AngleXU=0 Radius=1.5 StartAngle=2e-16 EndAngle=3.14159
    g5: ArcOfCircle CenterX=-16.1 CenterY=-1.8 CenterZ=0 NormalX=0 NormalY=0 NormalZ=1 AngleXU=0 Radius=1.5 StartAngle=5e-16 EndAngle=3.14159
    g6: ArcOfCircle CenterX=-22.1 CenterY=-1.8 CenterZ=0 NormalX=0 NormalY=0 NormalZ=1 AngleXU=0 Radius=1.5 StartAngle=5e-16 EndAngle=3.14159
    g7: ArcOfCircle CenterX=-28.2 CenterY=-4.3 CenterZ=0 NormalX=0 NormalY=0 NormalZ=1 AngleXU=0 Radius=1.5 StartAngle=2e-16 EndAngle=3.14159
    g8: ArcOfCircle CenterX=-10 CenterY=-33.9 CenterZ=0 NormalX=0 NormalY=0 NormalZ=1 AngleXU=0 Radius=1.5 StartAngle=3.14159 EndAngle=6.28319
    g9: ArcOfCircle CenterX=-16.1 CenterY=-36.4 CenterZ=0 NormalX=0 NormalY=0 NormalZ=1 AngleXU=0 Radius=1.5 StartAngle=3.14159 EndAngle=6.28319
    g10: ArcOfCircle CenterX=-22.1 CenterY=-36.4 CenterZ=0 NormalX=0 NormalY=0 NormalZ=1 AngleXU=0 Radius=1.5 StartAngle=3.14159 EndAngle=6.28319
    g11: ArcOfCircle CenterX=-28.2 CenterY=-33.9 CenterZ=0 NormalX=0 NormalY=0 NormalZ=1 AngleXU=0 Radius=1.5 StartAngle=3.14159 EndAngle=6.28319
    g12: LineSegment StartX=-35.7 StartY=-10.5 StartZ=0 EndX=-35.7 EndY=-27.7 EndZ=0
    g13: LineSegment StartX=-32.7 StartY=-10.5 StartZ=0 EndX=-32.7 EndY=-27.7 EndZ=0
    g14: LineSegment StartX=-29.7 StartY=-33.9 StartZ=0 EndX=-29.7 EndY=-4.3 EndZ=0
    g15: LineSegment StartX=-26.7 StartY=-33.9 StartZ=0 EndX=-26.7 EndY=-4.3 EndZ=0
    g16: LineSegment StartX=-2.5 StartY=-10.5 StartZ=0 EndX=-2.5 EndY=-27.7 EndZ=0
    g17: LineSegment StartX=-8.5 StartY=-4.3 StartZ=0 EndX=-8.5 EndY=-33.9 EndZ=0
    g18: LineSegment StartX=-5.5 StartY=-10.5 StartZ=0 EndX=-5.5 EndY=-27.7 EndZ=0
    g19: LineSegment StartX=-11.5 StartY=-4.3 StartZ=0 EndX=-11.5 EndY=-33.9 EndZ=0
    g20: LineSegment StartX=-14.6 StartY=-1.8 StartZ=0 EndX=-14.6 EndY=-36.4 EndZ=0
    g21: LineSegment StartX=-17.6 StartY=-1.8 StartZ=0 EndX=-17.6 EndY=-36.4 EndZ=0
    g22: LineSegment StartX=-20.6 StartY=-36.4 StartZ=0 EndX=-20.6 EndY=-1.8 EndZ=0
    g23: LineSegment StartX=-23.6 StartY=-1.8 StartZ=0 EndX=-23.6 EndY=-36.4 EndZ=0
  constraints (48):
    c: Block(g0)
    c: Block(g1)
    c: Block(g2)
    c: Block(g3)
    c: Block(g4)
    c: Block(g5)
    c: Block(g6)
    c: Block(g7)
    c: Block(g8)
    c: Block(g9)
    c: Block(g10)
    c: Block(g11)
    c: Coincident(g12,g1)
    c: Coincident(g12,g2)
    c: Vertical(g12)
    c: Coincident(g13,g1)
    c: Coincident(g13,g2)
    c: Vertical(g13)
    c: Coincident(g14,g11)
    c: Coincident(g14,g7)
    c: Vertical(g14)
    c: Coincident(g15,g11)
    c: Coincident(g15,g7)
    c: Vertical(g15)
    c: Coincident(g16,g0)
    c: Coincident(g16,g3)
    c: Vertical(g16)
    c: Coincident(g17,g4)
    c: Coincident(g17,g8)
    c: Vertical(g17)
    c: Coincident(g18,g0)
    c: Coincident(g18,g3)
    c: Vertical(g18)
    c: Coincident(g19,g4)
    c: Coincident(g19,g8)
    c: Vertical(g19)
    c: Coincident(g20,g5)
    c: Coincident(g20,g9)
    c: Vertical(g20)
    c: Coincident(g21,g5)
    c: Coincident(g21,g9)
    c: Vertical(g21)
    c: Coincident(g22,g10)
    c: Coincident(g22,g6)
    c: Vertical(g22)
    c: Coincident(g23,g6)
    c: Coincident(g23,g10)
    c: Vertical(g23)
FEATURE [Part::Extrusion] Extrude048  label="removeToCreateFanGrillHoles004"
  Base = -> Sketch057
  Dir = (0,-1,6e-16)
  DirMode = 2
  FaceMakerClass = Part::FaceMakerBullseye
  LengthFwd = 10
  LengthRev = 0
  Placement = pos=(65.4,44,54.82) rot=(0,0,1;0rad)
  Solid = true
  Symmetric = false
FEATURE [Part::Cut] Cut040  label="top021"
  Base = -> Fillet039
  Tool = -> Extrude048
FEATURE [Part::Cylinder] Cylinder041  label="removeToCreteHoleForPlugHousing034"
  Angle = 360
  AttacherType = Attacher::AttachEngine3D
  Height = 20
  Placement = pos=(-2,19,36) rot=(0,1,0;1.5708rad)
  Radius = 14.3
FEATURE [Part::MultiFuse] Fusion089  label="removeToCreteHoleForPlugHousing035"
  Shapes = -> [Box026,Cylinder041]
FEATURE [Part::Cylinder] Cylinder042
  Angle = 360
  AttacherType = Attacher::AttachEngine3D
  Height = 20
  Placement = pos=(0,0,36.15) rot=(0,0,1;0rad)
  Radius = 14.3
FEATURE [Part::Cylinder] Cylinder043
  Angle = 360
  AttacherType = Attacher::AttachEngine3D
  Height = 10
  Placement = pos=(0,0,36.15) rot=(0,0,1;0rad)
  Radius = 4
FEATURE [Part::Box] Box027  label="removeToCreteHoleForPlugHousing036"
  AttacherType = Attacher::AttachEngine3D
  Height = 28.6
  Length = 20
  Placement = pos=(106.15,0,21.7) rot=(0,0,1;0rad)
  Width = 19
FEATURE [Part::Cut] Cut041  label="top022"
  Base = -> Cut040
  Tool = -> Fusion087
FEATURE [Part::Cut] Cut039  label="top020"
  Base = -> Cut041
  Tool = -> Fusion089
FEATURE [Part::MultiFuse] Fusion090  label="removeToCreteHoleForPlugHousing037"
  Placement = pos=(70,19,36) rot=(0,1,0;1.5708rad)
  Shapes = -> [Cylinder042,Cylinder043]
FEATURE [Part::MultiFuse] Fusion088  label="removeToCreteHoleForPlugHousing033"
  Shapes = -> [Box027,Fusion090]
FEATURE [Part::Cut] Cut042  label="removeToCreteHoleForPlugHousing038"
  Base = -> Cut039
  Tool = -> Fusion088
FEATURE [Part::MultiFuse] Fusion091  label="removeFromTop"
  Shapes = -> [Fillet038,Fusion085,Fusion084,Fusion083,Extrude045]
FEATURE [Part::Cut] Cut043  label="REAL TOP ====="
  Base = -> Fillet036
  Tool = -> Fusion091
FEATURE [Part::MultiFuse] Fusion092  label="caseScrewPillarBracket016"
  Shapes = -> [Extrude030,Extrude031,Extrude032,Extrude033,Extrude034,Extrude035,Extrude036,Extrude037,Box013,Box014]
FEATURE [Sketcher::SketchObject] Sketch058  label="topSketch015"
  FullyConstrained = true
  sketch-geometry (20):
    g0: LineSegment StartX=5.21097e-06 StartY=3 StartZ=0 EndX=5.21097e-06 EndY=19 EndZ=0
    g1: ArcOfCircle CenterX=19 CenterY=19 CenterZ=0 NormalX=0 NormalY=0 NormalZ=1 AngleXU=0 Radius=19 StartAngle=1.5708 EndAngle=3.14159
    g2: ArcOfCircle CenterX=19 CenterY=19 CenterZ=0 NormalX=0 NormalY=0 NormalZ=1 AngleXU=0 Radius=16 StartAngle=1.5708 EndAngle=3.14159
    g3: LineSegment StartX=114 StartY=35 StartZ=0 EndX=19 EndY=35 EndZ=0
    g4: LineSegment StartX=5.21097e-06 StartY=3 StartZ=0 EndX=5.21097e-06 EndY=0 EndZ=0
    g5: LineSegment StartX=3 StartY=0 StartZ=0 EndX=5.21097e-06 EndY=0 EndZ=0
    g6: LineSegment StartX=3 StartY=19 StartZ=0 EndX=3 EndY=0 EndZ=0
    g7: LineSegment StartX=19 StartY=38 StartZ=0 EndX=124 EndY=38 EndZ=0
    g8: Circle CenterX=119 CenterY=35 CenterZ=0 NormalX=0 NormalY=0 NormalZ=1 AngleXU=0 Radius=1
    g9: Circle CenterX=121 CenterY=35 CenterZ=0 NormalX=0 NormalY=0 NormalZ=1 AngleXU=0 Radius=1
    g10: Circle CenterX=121 CenterY=33 CenterZ=0 NormalX=0 NormalY=0 NormalZ=1 AngleXU=0 Radius=1
    g11: BSplineCurve PolesCount=3 KnotsCount=2 Degree=2 IsPeriodic=0
    g12: GeomPoint X=119 Y=35 Z=0
    g13: GeomPoint X=121 Y=33 Z=0
    g14: LineSegment StartX=119 StartY=35 StartZ=0 EndX=114 EndY=35 EndZ=0
    g15: ArcOfCircle CenterX=105 CenterY=19 CenterZ=0 NormalX=0 NormalY=0 NormalZ=1 AngleXU=0 Radius=19 StartAngle=5.7297 EndAngle=6.28319
    g16: ArcOfCircle CenterX=105 CenterY=19 CenterZ=0 NormalX=0 NormalY=0 NormalZ=1 AngleXU=0 Radius=16 StartAngle=5.60905 EndAngle=6.28319
    g17: LineSegment StartX=121 StartY=33 StartZ=0 EndX=121 EndY=19 EndZ=0
    g18: LineSegment StartX=124 StartY=38 StartZ=0 EndX=124 EndY=19 EndZ=0
    g19: LineSegment StartX=117.5 StartY=9.01251 StartZ=0 EndX=121.163 EndY=9.0125 EndZ=0
  constraints (46):
    c: Vertical(g0)
    c: Block(g0)
    c: Coincident(g1,g0)
    c: Block(g1)
    c: Coincident(g2,g1)
    c: Block(g2)
    c: Coincident(g3,g2)
    c: Horizontal(g3)
    c: Tangent(g3,g2)
    c: Coincident(g4,g0)
    c: Distance(g4) = 3
    c: Vertical(g4)
    c: Coincident(g5,g4)
    c: Horizontal(g5)
    c: Coincident(g6,g2)
    c: Coincident(g6,g5)
    c: Vertical(g6)
    c: Horizontal(g7)
    c: Distance(g7) = 105
    c: Coincident(g7,g1)
    c: Block(g3)
    c: Weight(g8) = 1
    c: Equal(g8,g9)
    c: Equal(g8,g10)
    c: InternalAlignment(g8,g11)
    c: InternalAlignment(g9,g11)
    c: InternalAlignment(g10,g11)
    c: InternalAlignment(g12,g11)
    c: InternalAlignment(g13,g11)
    c: Block(g11)
    c: Coincident(g14,g11)
    c: Coincident(g14,g3)
    c: Horizontal(g14)
    c: Block(g15)
    c: Coincident(g16,g15)
    c: Block(g16)
    c: Coincident(g17,g11)
    c: Coincident(g17,g16)
    c: Vertical(g17)
    c: Distance(g17) = 14
    c: Coincident(g18,g7)
    c: Coincident(g18,g15)
    c: Vertical(g18)
    c: Distance(g18) = 19
    c: Coincident(g19,g16)
    c: Coincident(g19,g15)
FEATURE [Part::Extrusion] Extrude049  label="top023"
  Base = -> Sketch058
  Dir = (0,0,1)
  DirMode = 2
  FaceMakerClass = Part::FaceMakerBullseye
  LengthFwd = 72
  LengthRev = 0
  Solid = true
  Symmetric = false
FEATURE [Sketcher::SketchObject] Sketch059
  FullyConstrained = true
  MapMode = 3
  Placement = pos=(0,0,0) rot=(1,0,0;1.5708rad)
  Support = -> [Extrude049]
  sketch-geometry (8):
    g0: Circle CenterX=80.351 CenterY=-67.6202 CenterZ=0 NormalX=0 NormalY=0 NormalZ=1 AngleXU=0 Radius=2
    g1: Circle CenterX=80.351 CenterY=-67.6202 CenterZ=0 NormalX=0 NormalY=0 NormalZ=1 AngleXU=0 Radius=3
    g2: Circle CenterX=80.351 CenterY=-4.92017 CenterZ=0 NormalX=0 NormalY=0 NormalZ=1 AngleXU=0 Radius=2
    g3: Circle CenterX=80.351 CenterY=-4.92017 CenterZ=0 NormalX=0 NormalY=0 NormalZ=1 AngleXU=0 Radius=3
    g4: Circle CenterX=23.851 CenterY=-4.92017 CenterZ=0 NormalX=0 NormalY=0 NormalZ=1 AngleXU=0 Radius=2
    g5: Circle CenterX=23.851 CenterY=-4.92017 CenterZ=0 NormalX=0 NormalY=0 NormalZ=1 AngleXU=0 Radius=3
    g6: Circle CenterX=23.851 CenterY=-67.6202 CenterZ=0 NormalX=0 NormalY=0 NormalZ=1 AngleXU=0 Radius=2
    g7: Circle CenterX=23.851 CenterY=-67.6202 CenterZ=0 NormalX=0 NormalY=0 NormalZ=1 AngleXU=0 Radius=3
  constraints (8):
    c: Block(g3)
    c: Block(g2)
    c: Block(g1)
    c: Block(g0)
    c: Block(g6)
    c: Block(g7)
    c: Block(g4)
    c: Block(g5)
FEATURE [Sketcher::SketchObject] Sketch060
  FullyConstrained = true
  MapMode = 3
  Placement = pos=(0,0,0) rot=(1,0,0;1.5708rad)
  Support = -> [Extrude049]
  sketch-geometry (8):
    g0: Circle CenterX=80.351 CenterY=-67.6202 CenterZ=0 NormalX=0 NormalY=0 NormalZ=1 AngleXU=0 Radius=3
    g1: Circle CenterX=80.351 CenterY=-4.92017 CenterZ=0 NormalX=0 NormalY=0 NormalZ=1 AngleXU=0 Radius=3
    g2: Circle CenterX=23.851 CenterY=-4.92017 CenterZ=0 NormalX=0 NormalY=0 NormalZ=1 AngleXU=0 Radius=3
    g3: Circle CenterX=23.851 CenterY=-67.6202 CenterZ=0 NormalX=0 NormalY=0 NormalZ=1 AngleXU=0 Radius=3
    g4: Circle CenterX=23.851 CenterY=-67.6202 CenterZ=0 NormalX=0 NormalY=0 NormalZ=1 AngleXU=0 Radius=5
    g5: Circle CenterX=80.351 CenterY=-67.6202 CenterZ=0 NormalX=0 NormalY=0 NormalZ=1 AngleXU=0 Radius=5
    g6: Circle CenterX=23.851 CenterY=-4.92017 CenterZ=0 NormalX=0 NormalY=0 NormalZ=1 AngleXU=0 Radius=5
    g7: Circle CenterX=80.351 CenterY=-4.92017 CenterZ=0 NormalX=0 NormalY=0 NormalZ=1 AngleXU=0 Radius=5
  constraints (8):
    c: Block(g1)
    c: Block(g0)
    c: Block(g3)
    c: Block(g2)
    c: Block(g5)
    c: Block(g4)
    c: Block(g6)
    c: Block(g7)
FEATURE [Sketcher::SketchObject] Sketch061
  FullyConstrained = true
  MapMode = 3
  Placement = pos=(0,0,0) rot=(1,0,0;1.5708rad)
  sketch-geometry (8):
    g0: Circle CenterX=80.351 CenterY=-67.6202 CenterZ=0 NormalX=0 NormalY=0 NormalZ=1 AngleXU=0 Radius=3
    g1: Circle CenterX=80.351 CenterY=-4.92017 CenterZ=0 NormalX=0 NormalY=0 NormalZ=1 AngleXU=0 Radius=3
    g2: Circle CenterX=23.851 CenterY=-4.92017 CenterZ=0 NormalX=0 NormalY=0 NormalZ=1 AngleXU=0 Radius=3
    g3: Circle CenterX=23.851 CenterY=-67.6202 CenterZ=0 NormalX=0 NormalY=0 NormalZ=1 AngleXU=0 Radius=3
    g4: Circle CenterX=23.851 CenterY=-67.6202 CenterZ=0 NormalX=0 NormalY=0 NormalZ=1 AngleXU=0 Radius=5
    g5: Circle CenterX=80.351 CenterY=-67.6202 CenterZ=0 NormalX=0 NormalY=0 NormalZ=1 AngleXU=0 Radius=5
    g6: Circle CenterX=23.851 CenterY=-4.92017 CenterZ=0 NormalX=0 NormalY=0 NormalZ=1 AngleXU=0 Radius=5
    g7: Circle CenterX=80.351 CenterY=-4.92017 CenterZ=0 NormalX=0 NormalY=0 NormalZ=1 AngleXU=0 Radius=5
  constraints (8):
    c: Block(g1)
    c: Block(g0)
    c: Block(g3)
    c: Block(g2)
    c: Block(g5)
    c: Block(g4)
    c: Block(g6)
    c: Block(g7)
FEATURE [Sketcher::SketchObject] Sketch062  label="topSketch016"
  FullyConstrained = true
  sketch-geometry (20):
    g0: LineSegment StartX=5.21097e-06 StartY=3 StartZ=0 EndX=5.21097e-06 EndY=19 EndZ=0
    g1: ArcOfCircle CenterX=19 CenterY=19 CenterZ=0 NormalX=0 NormalY=0 NormalZ=1 AngleXU=0 Radius=19 StartAngle=1.5708 EndAngle=3.14159
    g2: ArcOfCircle CenterX=19 CenterY=19 CenterZ=0 NormalX=0 NormalY=0 NormalZ=1 AngleXU=0 Radius=16 StartAngle=1.5708 EndAngle=3.14159
    g3: LineSegment StartX=114 StartY=35 StartZ=0 EndX=19 EndY=35 EndZ=0
    g4: LineSegment StartX=5.21097e-06 StartY=3 StartZ=0 EndX=5.21097e-06 EndY=0 EndZ=0
    g5: LineSegment StartX=3 StartY=0 StartZ=0 EndX=5.21097e-06 EndY=0 EndZ=0
    g6: LineSegment StartX=3 StartY=19 StartZ=0 EndX=3 EndY=0 EndZ=0
    g7: LineSegment StartX=19 StartY=38 StartZ=0 EndX=124 EndY=38 EndZ=0
    g8: Circle CenterX=119 CenterY=35 CenterZ=0 NormalX=0 NormalY=0 NormalZ=1 AngleXU=0 Radius=1
    g9: Circle CenterX=121 CenterY=35 CenterZ=0 NormalX=0 NormalY=0 NormalZ=1 AngleXU=0 Radius=1
    g10: Circle CenterX=121 CenterY=33 CenterZ=0 NormalX=0 NormalY=0 NormalZ=1 AngleXU=0 Radius=1
    g11: BSplineCurve PolesCount=3 KnotsCount=2 Degree=2 IsPeriodic=0
    g12: GeomPoint X=119 Y=35 Z=0
    g13: GeomPoint X=121 Y=33 Z=0
    g14: LineSegment StartX=119 StartY=35 StartZ=0 EndX=114 EndY=35 EndZ=0
    g15: ArcOfCircle CenterX=105 CenterY=19 CenterZ=0 NormalX=0 NormalY=0 NormalZ=1 AngleXU=0 Radius=19 StartAngle=5.7297 EndAngle=6.28319
    g16: ArcOfCircle CenterX=105 CenterY=19 CenterZ=0 NormalX=0 NormalY=0 NormalZ=1 AngleXU=0 Radius=16 StartAngle=5.60905 EndAngle=6.28319
    g17: LineSegment StartX=121 StartY=33 StartZ=0 EndX=121 EndY=19 EndZ=0
    g18: LineSegment StartX=124 StartY=38 StartZ=0 EndX=124 EndY=19 EndZ=0
    g19: LineSegment StartX=117.5 StartY=9.01251 StartZ=0 EndX=121.163 EndY=9.0125 EndZ=0
  constraints (46):
    c: Vertical(g0)
    c: Block(g0)
    c: Coincident(g1,g0)
    c: Block(g1)
    c: Coincident(g2,g1)
    c: Block(g2)
    c: Coincident(g3,g2)
    c: Horizontal(g3)
    c: Tangent(g3,g2)
    c: Coincident(g4,g0)
    c: Distance(g4) = 3
    c: Vertical(g4)
    c: Coincident(g5,g4)
    c: Horizontal(g5)
    c: Coincident(g6,g2)
    c: Coincident(g6,g5)
    c: Vertical(g6)
    c: Horizontal(g7)
    c: Distance(g7) = 105
    c: Coincident(g7,g1)
    c: Block(g3)
    c: Weight(g8) = 1
    c: Equal(g8,g9)
    c: Equal(g8,g10)
    c: InternalAlignment(g8,g11)
    c: InternalAlignment(g9,g11)
    c: InternalAlignment(g10,g11)
    c: InternalAlignment(g12,g11)
    c: InternalAlignment(g13,g11)
    c: Block(g11)
    c: Coincident(g14,g11)
    c: Coincident(g14,g3)
    c: Horizontal(g14)
    c: Block(g15)
    c: Coincident(g16,g15)
    c: Block(g16)
    c: Coincident(g17,g11)
    c: Coincident(g17,g16)
    c: Vertical(g17)
    c: Distance(g17) = 14
    c: Coincident(g18,g7)
    c: Coincident(g18,g15)
    c: Vertical(g18)
    c: Distance(g18) = 19
    c: Coincident(g19,g16)
    c: Coincident(g19,g15)
FEATURE [Part::Extrusion] Extrude053  label="top024"
  Base = -> Sketch062
  Dir = (0,0,1)
  DirMode = 2
  FaceMakerClass = Part::FaceMakerBullseye
  LengthFwd = 72
  LengthRev = 0
  Solid = true
  Symmetric = false
FEATURE [Sketcher::SketchObject] Sketch063
  FullyConstrained = true
  MapMode = 3
  Placement = pos=(0,0,0) rot=(1,0,0;1.5708rad)
  Support = -> [Extrude053]
  sketch-geometry (8):
    g0: Circle CenterX=80.351 CenterY=-67.6202 CenterZ=0 NormalX=0 NormalY=0 NormalZ=1 AngleXU=0 Radius=2
    g1: Circle CenterX=80.351 CenterY=-67.6202 CenterZ=0 NormalX=0 NormalY=0 NormalZ=1 AngleXU=0 Radius=3
    g2: Circle CenterX=80.351 CenterY=-4.92017 CenterZ=0 NormalX=0 NormalY=0 NormalZ=1 AngleXU=0 Radius=2
    g3: Circle CenterX=80.351 CenterY=-4.92017 CenterZ=0 NormalX=0 NormalY=0 NormalZ=1 AngleXU=0 Radius=3
    g4: Circle CenterX=23.851 CenterY=-4.92017 CenterZ=0 NormalX=0 NormalY=0 NormalZ=1 AngleXU=0 Radius=2
    g5: Circle CenterX=23.851 CenterY=-4.92017 CenterZ=0 NormalX=0 NormalY=0 NormalZ=1 AngleXU=0 Radius=3
    g6: Circle CenterX=23.851 CenterY=-67.6202 CenterZ=0 NormalX=0 NormalY=0 NormalZ=1 AngleXU=0 Radius=2
    g7: Circle CenterX=23.851 CenterY=-67.6202 CenterZ=0 NormalX=0 NormalY=0 NormalZ=1 AngleXU=0 Radius=3
  constraints (8):
    c: Block(g3)
    c: Block(g2)
    c: Block(g1)
    c: Block(g0)
    c: Block(g6)
    c: Block(g7)
    c: Block(g4)
    c: Block(g5)
FEATURE [Part::Extrusion] Extrude054
  Base = -> Sketch063
  Dir = (0,-1,2e-16)
  DirMode = 2
  FaceMakerClass = Part::FaceMakerBullseye
  LengthFwd = 6
  LengthRev = 0
  Placement = pos=(0,9,0) rot=(0,0,1;0rad)
  Solid = true
  Symmetric = false
FEATURE [Sketcher::SketchObject] Sketch064  label="topSketch017"
  FullyConstrained = true
  sketch-geometry (20):
    g0: LineSegment StartX=5.21097e-06 StartY=3 StartZ=0 EndX=5.21097e-06 EndY=19 EndZ=0
    g1: ArcOfCircle CenterX=19 CenterY=19 CenterZ=0 NormalX=0 NormalY=0 NormalZ=1 AngleXU=0 Radius=19 StartAngle=1.5708 EndAngle=3.14159
    g2: ArcOfCircle CenterX=19 CenterY=19 CenterZ=0 NormalX=0 NormalY=0 NormalZ=1 AngleXU=0 Radius=16 StartAngle=1.5708 EndAngle=3.14159
    g3: LineSegment StartX=114 StartY=35 StartZ=0 EndX=19 EndY=35 EndZ=0
    g4: LineSegment StartX=5.21097e-06 StartY=3 StartZ=0 EndX=5.21097e-06 EndY=0 EndZ=0
    g5: LineSegment StartX=3 StartY=0 StartZ=0 EndX=5.21097e-06 EndY=0 EndZ=0
    g6: LineSegment StartX=3 StartY=19 StartZ=0 EndX=3 EndY=0 EndZ=0
    g7: LineSegment StartX=19 StartY=38 StartZ=0 EndX=124 EndY=38 EndZ=0
    g8: Circle CenterX=119 CenterY=35 CenterZ=0 NormalX=0 NormalY=0 NormalZ=1 AngleXU=0 Radius=1
    g9: Circle CenterX=121 CenterY=35 CenterZ=0 NormalX=0 NormalY=0 NormalZ=1 AngleXU=0 Radius=1
    g10: Circle CenterX=121 CenterY=33 CenterZ=0 NormalX=0 NormalY=0 NormalZ=1 AngleXU=0 Radius=1
    g11: BSplineCurve PolesCount=3 KnotsCount=2 Degree=2 IsPeriodic=0
    g12: GeomPoint X=119 Y=35 Z=0
    g13: GeomPoint X=121 Y=33 Z=0
    g14: LineSegment StartX=119 StartY=35 StartZ=0 EndX=114 EndY=35 EndZ=0
    g15: ArcOfCircle CenterX=105 CenterY=19 CenterZ=0 NormalX=0 NormalY=0 NormalZ=1 AngleXU=0 Radius=19 StartAngle=5.7297 EndAngle=6.28319
    g16: ArcOfCircle CenterX=105 CenterY=19 CenterZ=0 NormalX=0 NormalY=0 NormalZ=1 AngleXU=0 Radius=16 StartAngle=5.60905 EndAngle=6.28319
    g17: LineSegment StartX=121 StartY=33 StartZ=0 EndX=121 EndY=19 EndZ=0
    g18: LineSegment StartX=124 StartY=38 StartZ=0 EndX=124 EndY=19 EndZ=0
    g19: LineSegment StartX=117.5 StartY=9.01251 StartZ=0 EndX=121.163 EndY=9.0125 EndZ=0
  constraints (46):
    c: Vertical(g0)
    c: Block(g0)
    c: Coincident(g1,g0)
    c: Block(g1)
    c: Coincident(g2,g1)
    c: Block(g2)
    c: Coincident(g3,g2)
    c: Horizontal(g3)
    c: Tangent(g3,g2)
    c: Coincident(g4,g0)
    c: Distance(g4) = 3
    c: Vertical(g4)
    c: Coincident(g5,g4)
    c: Horizontal(g5)
    c: Coincident(g6,g2)
    c: Coincident(g6,g5)
    c: Vertical(g6)
    c: Horizontal(g7)
    c: Distance(g7) = 105
    c: Coincident(g7,g1)
    c: Block(g3)
    c: Weight(g8) = 1
    c: Equal(g8,g9)
    c: Equal(g8,g10)
    c: InternalAlignment(g8,g11)
    c: InternalAlignment(g9,g11)
    c: InternalAlignment(g10,g11)
    c: InternalAlignment(g12,g11)
    c: InternalAlignment(g13,g11)
    c: Block(g11)
    c: Coincident(g14,g11)
    c: Coincident(g14,g3)
    c: Horizontal(g14)
    c: Block(g15)
    c: Coincident(g16,g15)
    c: Block(g16)
    c: Coincident(g17,g11)
    c: Coincident(g17,g16)
    c: Vertical(g17)
    c: Distance(g17) = 14
    c: Coincident(g18,g7)
    c: Coincident(g18,g15)
    c: Vertical(g18)
    c: Distance(g18) = 19
    c: Coincident(g19,g16)
    c: Coincident(g19,g15)
FEATURE [Sketcher::SketchObject] Sketch065
  FullyConstrained = true
  MapMode = 3
  Placement = pos=(0,0,0) rot=(1,0,0;1.5708rad)
  sketch-geometry (8):
    g0: Circle CenterX=80.351 CenterY=-67.6202 CenterZ=0 NormalX=0 NormalY=0 NormalZ=1 AngleXU=0 Radius=3
    g1: Circle CenterX=80.351 CenterY=-4.92017 CenterZ=0 NormalX=0 NormalY=0 NormalZ=1 AngleXU=0 Radius=3
    g2: Circle CenterX=23.851 CenterY=-4.92017 CenterZ=0 NormalX=0 NormalY=0 NormalZ=1 AngleXU=0 Radius=3
    g3: Circle CenterX=23.851 CenterY=-67.6202 CenterZ=0 NormalX=0 NormalY=0 NormalZ=1 AngleXU=0 Radius=3
    g4: Circle CenterX=23.851 CenterY=-67.6202 CenterZ=0 NormalX=0 NormalY=0 NormalZ=1 AngleXU=0 Radius=5
    g5: Circle CenterX=80.351 CenterY=-67.6202 CenterZ=0 NormalX=0 NormalY=0 NormalZ=1 AngleXU=0 Radius=5
    g6: Circle CenterX=23.851 CenterY=-4.92017 CenterZ=0 NormalX=0 NormalY=0 NormalZ=1 AngleXU=0 Radius=5
    g7: Circle CenterX=80.351 CenterY=-4.92017 CenterZ=0 NormalX=0 NormalY=0 NormalZ=1 AngleXU=0 Radius=5
  constraints (8):
    c: Block(g1)
    c: Block(g0)
    c: Block(g3)
    c: Block(g2)
    c: Block(g5)
    c: Block(g4)
    c: Block(g6)
    c: Block(g7)
FEATURE [Part::Extrusion] Extrude056
  Base = -> Sketch065
  Dir = (0,-1,2e-16)
  DirMode = 2
  FaceMakerClass = Part::FaceMakerBullseye
  LengthFwd = 2
  LengthRev = 0
  Solid = true
  Symmetric = false
FEATURE [Part::Extrusion] Extrude057  label="top025"
  Base = -> Sketch064
  Dir = (0,0,1)
  DirMode = 2
  FaceMakerClass = Part::FaceMakerBullseye
  LengthFwd = 72
  LengthRev = 0
  Solid = true
  Symmetric = false
FEATURE [Sketcher::SketchObject] Sketch066
  FullyConstrained = true
  MapMode = 3
  Placement = pos=(0,0,0) rot=(1,0,0;1.5708rad)
  Support = -> [Extrude057]
  sketch-geometry (8):
    g0: Circle CenterX=80.351 CenterY=-67.6202 CenterZ=0 NormalX=0 NormalY=0 NormalZ=1 AngleXU=0 Radius=3
    g1: Circle CenterX=80.351 CenterY=-4.92017 CenterZ=0 NormalX=0 NormalY=0 NormalZ=1 AngleXU=0 Radius=3
    g2: Circle CenterX=23.851 CenterY=-4.92017 CenterZ=0 NormalX=0 NormalY=0 NormalZ=1 AngleXU=0 Radius=3
    g3: Circle CenterX=23.851 CenterY=-67.6202 CenterZ=0 NormalX=0 NormalY=0 NormalZ=1 AngleXU=0 Radius=3
    g4: Circle CenterX=23.851 CenterY=-67.6202 CenterZ=0 NormalX=0 NormalY=0 NormalZ=1 AngleXU=0 Radius=5
    g5: Circle CenterX=80.351 CenterY=-67.6202 CenterZ=0 NormalX=0 NormalY=0 NormalZ=1 AngleXU=0 Radius=5
    g6: Circle CenterX=23.851 CenterY=-4.92017 CenterZ=0 NormalX=0 NormalY=0 NormalZ=1 AngleXU=0 Radius=5
    g7: Circle CenterX=80.351 CenterY=-4.92017 CenterZ=0 NormalX=0 NormalY=0 NormalZ=1 AngleXU=0 Radius=5
  constraints (8):
    c: Block(g1)
    c: Block(g0)
    c: Block(g3)
    c: Block(g2)
    c: Block(g5)
    c: Block(g4)
    c: Block(g6)
    c: Block(g7)
FEATURE [Part::Extrusion] Extrude055
  Base = -> Sketch066
  Dir = (0,-1,2e-16)
  DirMode = 2
  FaceMakerClass = Part::FaceMakerBullseye
  LengthFwd = 2
  LengthRev = 0
  Solid = true
  Symmetric = false
FEATURE [Part::Fillet] Fillet041
  Base = -> Extrude056
  Edges = 4 edges r=1.99: [Edge6,Edge12,Edge18,Edge24]
FEATURE [Part::Cut] Cut045
  Base = -> Extrude055
  Placement = pos=(0,6,0) rot=(0,0,1;0rad)
  Tool = -> Fillet041
FEATURE [Part::MultiFuse] Fusion095  label="pcbScrewPillars"
  Placement = pos=(-3.2,-1,72.3) rot=(0,0,1;0rad)
  Shapes = -> [Cut045,Extrude054]
FEATURE [Part::Feature] Face113
  shape: bbox 3.2 x 1.5 x 2e-07 mm, 1 faces, 0 solids (baked)
FEATURE [Part::Revolution] Revolve121  label="backCaseScrewRetainer002"
  Angle = 360
  Axis = (0,1,0)
  Base = (0,0,0)
  FaceMakerClass = Part::FaceMakerBullseye
  Placement = pos=(12.5,3,62) rot=(0,0,1;0rad)
  Solid = false
  Source = -> Face113
  Symmetric = false
FEATURE [Part::Feature] Face114
  shape: bbox 3.2 x 1.5 x 2e-07 mm, 1 faces, 0 solids (baked)
FEATURE [Part::Feature] Face115
  shape: bbox 3.2 x 1.5 x 2e-07 mm, 1 faces, 0 solids (baked)
FEATURE [Part::Feature] Face116
  shape: bbox 3.2 x 1.5 x 2e-07 mm, 1 faces, 0 solids (baked)
FEATURE [Part::Revolution] Revolve122  label="frontCaseScrewRetainer004"
  Angle = 360
  Axis = (0,1,0)
  Base = (0,0,0)
  FaceMakerClass = Part::FaceMakerBullseye
  Placement = pos=(89.5,3,68.5) rot=(0,0,1;0rad)
  Solid = false
  Source = -> Face115
  Symmetric = false
FEATURE [Part::Revolution] Revolve123  label="frontCaseScrewRetainer005"
  Angle = 360
  Axis = (0,1,0)
  Base = (0,0,0)
  FaceMakerClass = Part::FaceMakerBullseye
  Placement = pos=(89.5,3,3.5) rot=(0,0,1;0rad)
  Solid = false
  Source = -> Face116
  Symmetric = false
FEATURE [Part::Revolution] Revolve124  label="backCaseScrewRetainer003"
  Angle = 360
  Axis = (0,1,0)
  Base = (0,0,0)
  FaceMakerClass = Part::FaceMakerBullseye
  Placement = pos=(12.5,3,10) rot=(0,0,1;0rad)
  Solid = false
  Source = -> Face114
  Symmetric = false
FEATURE [Part::Feature] Face117
  shape: bbox 3.6 x 3.2 x 2e-07 mm, 1 faces, 0 solids (baked)
FEATURE [Part::Revolution] Revolve125  label="moreFrontCaseScrewRetainer004"
  Angle = 360
  Axis = (0,1,0)
  Base = (0,0,0)
  FaceMakerClass = Part::FaceMakerBullseye
  Placement = pos=(109.5,4.5,68.5) rot=(0,0,1;0rad)
  Solid = false
  Source = -> Face117
  Symmetric = false
FEATURE [Part::Feature] Face118
  shape: bbox 3.6 x 3.2 x 2e-07 mm, 1 faces, 0 solids (baked)
FEATURE [Part::Revolution] Revolve126  label="moreFrontCaseScrewRetainer005"
  Angle = 360
  Axis = (0,1,0)
  Base = (0,0,0)
  FaceMakerClass = Part::FaceMakerBullseye
  Placement = pos=(109.5,4.5,3.5) rot=(0,0,1;0rad)
  Solid = false
  Source = -> Face118
  Symmetric = false
FEATURE [Part::MultiFuse] Fusion096  label="screwRetainers001"
  Shapes = -> [Revolve126,Revolve125,Revolve124,Revolve123,Revolve122,Revolve121]
FEATURE [Part::Feature] Face119
  shape: bbox 10 x 16.5 x 2e-07 mm, 1 faces, 0 solids (baked)
FEATURE [Part::Revolution] Revolve130  label="plugHousing050"
  Angle = 360
  Axis = (0,1,0)
  Base = (0,0,0)
  FaceMakerClass = Part::FaceMakerBullseye
  Placement = pos=(0,0,36.15) rot=(0,0,1;0rad)
  Solid = false
  Source = -> Face119
  Symmetric = false
FEATURE [Part::Feature] Face120
  shape: bbox 10 x 16.5 x 2e-07 mm, 1 faces, 0 solids (baked)
FEATURE [Part::Feature] Face121
  shape: bbox 10 x 16.5 x 2e-07 mm, 1 faces, 0 solids (baked)
FEATURE [Part::Revolution] Revolve127  label="plugHousing047"
  Angle = 360
  Axis = (0,1,0)
  Base = (0,0,0)
  FaceMakerClass = Part::FaceMakerBullseye
  Placement = pos=(0,0,36.15) rot=(0,0,1;0rad)
  Solid = false
  Source = -> Face121
  Symmetric = false
FEATURE [Part::Feature] Face122
  shape: bbox 10 x 16.5 x 2e-07 mm, 1 faces, 0 solids (baked)
FEATURE [Part::Feature] Face123
  shape: bbox 10 x 16.5 x 2e-07 mm, 1 faces, 0 solids (baked)
FEATURE [Part::Revolution] Revolve128  label="plugHousing048"
  Angle = 360
  Axis = (0,1,0)
  Base = (0,0,0)
  FaceMakerClass = Part::FaceMakerBullseye
  Placement = pos=(0,0,36.15) rot=(0,0,1;0rad)
  Solid = false
  Source = -> Face123
  Symmetric = false
FEATURE [Part::MultiFuse] Fusion100  label="plugHousing054"
  Placement = pos=(0,0,0) rot=(0,0,1;1.5708rad)
  Shapes = -> [Revolve130,Revolve128]
FEATURE [Part::Feature] Face124
  shape: bbox 10 x 16.5 x 2e-07 mm, 1 faces, 0 solids (baked)
FEATURE [Part::Feature] Face125
  shape: bbox 10 x 16.5 x 2e-07 mm, 1 faces, 0 solids (baked)
FEATURE [Part::Revolution] Revolve129  label="plugHousing049"
  Angle = 360
  Axis = (0,1,0)
  Base = (0,0,0)
  FaceMakerClass = Part::FaceMakerBullseye
  Placement = pos=(0,0,36.15) rot=(0,0,1;0rad)
  Solid = false
  Source = -> Face125
  Symmetric = false
FEATURE [Part::Feature] Face126
  shape: bbox 10 x 16.5 x 2e-07 mm, 1 faces, 0 solids (baked)
FEATURE [Part::Revolution] Revolve131  label="plugHousing058"
  Angle = 360
  Axis = (0,1,0)
  Base = (0,0,0)
  FaceMakerClass = Part::FaceMakerBullseye
  Placement = pos=(0,0,36.15) rot=(0,0,1;0rad)
  Solid = false
  Source = -> Face120
  Symmetric = false
FEATURE [Part::MultiFuse] Fusion099  label="plugHousing053"
  Placement = pos=(0,0,0) rot=(0,0,1;1.5708rad)
  Shapes = -> [Revolve127,Revolve131]
FEATURE [Part::MultiFuse] Fusion102  label="plugHousing056"
  Placement = pos=(0,19,0) rot=(0,0,1;3.14159rad)
  Shapes = -> [Fusion100,Fusion099]
FEATURE [Part::Revolution] Revolve132  label="plugHousing059"
  Angle = 360
  Axis = (0,1,0)
  Base = (0,0,0)
  FaceMakerClass = Part::FaceMakerBullseye
  Placement = pos=(0,0,36.15) rot=(0,0,1;0rad)
  Solid = false
  Source = -> Face126
  Symmetric = false
FEATURE [Part::Revolution] Revolve133  label="plugHousing060"
  Angle = 360
  Axis = (0,1,0)
  Base = (0,0,0)
  FaceMakerClass = Part::FaceMakerBullseye
  Placement = pos=(0,0,36.15) rot=(0,0,1;0rad)
  Solid = false
  Source = -> Face122
  Symmetric = false
FEATURE [Part::MultiFuse] Fusion097  label="plugHousing051"
  Placement = pos=(0,0,0) rot=(0,0,1;1.5708rad)
  Shapes = -> [Revolve133,Revolve132]
FEATURE [Part::Revolution] Revolve134  label="plugHousing061"
  Angle = 360
  Axis = (0,1,0)
  Base = (0,0,0)
  FaceMakerClass = Part::FaceMakerBullseye
  Placement = pos=(0,0,36.15) rot=(0,0,1;0rad)
  Solid = false
  Source = -> Face124
  Symmetric = false
FEATURE [Part::MultiFuse] Fusion101  label="plugHousing055"
  Placement = pos=(0,0,0) rot=(0,0,1;1.5708rad)
  Shapes = -> [Revolve129,Revolve134]
FEATURE [Part::MultiFuse] Fusion098  label="plugHousing052"
  Placement = pos=(0,19,0) rot=(0,0,1;3.14159rad)
  Shapes = -> [Fusion097,Fusion101]
FEATURE [Part::MultiFuse] Fusion103  label="plugHousing057"
  Placement = pos=(122.621,0,-0.15) rot=(0,0,1;0rad)
  Shapes = -> [Fusion102,Fusion098]
FEATURE [Part::Box] Box028  label="Cube015"
  AttacherType = Attacher::AttachEngine3D
  Height = 28
  Length = 3
  Placement = pos=(110.7,19,22) rot=(0,0,1;0rad)
  Width = 15.7
FEATURE [Part::Cylinder] Cylinder044
  Angle = 360
  AttacherType = Attacher::AttachEngine3D
  Height = 20
  Placement = pos=(0,0,36.15) rot=(0,0,1;0rad)
  Radius = 10.3
FEATURE [Part::Cylinder] Cylinder045
  Angle = 360
  AttacherType = Attacher::AttachEngine3D
  Height = 10
  Placement = pos=(0,0,36.15) rot=(0,0,1;0rad)
  Radius = 4
FEATURE [Part::MultiFuse] Fusion104  label="removeToCreteHoleForPlugHousing040"
  Placement = pos=(70,19,36) rot=(0,1,0;1.5708rad)
  Shapes = -> [Cylinder044,Cylinder045]
FEATURE [Part::Cut] Cut046  label="plugHousingTab003"
  Base = -> Box028
  Tool = -> Fusion104
FEATURE [Part::MultiFuse] Fusion105  label="plugHousing062"
  Shapes = -> [Fusion103,Cut046]
FEATURE [Part::Fillet] Fillet042
  Base = -> Fusion105
  Edges = 1 edges r=2: [Edge25]
FEATURE [Part::Fillet] Fillet043  label="plugHousing063"
  Base = -> Fillet042
  Edges = 1 edges r=2: [Edge8]
  Placement = pos=(7,0,0) rot=(0,0,1;0rad)
FEATURE [Part::Feature] Face127
  shape: bbox 10 x 16.5 x 2e-07 mm, 1 faces, 0 solids (baked)
FEATURE [Part::Feature] Face128
  shape: bbox 10 x 16.5 x 2e-07 mm, 1 faces, 0 solids (baked)
FEATURE [Part::Revolution] Revolve137  label="plugHousing070"
  Angle = 360
  Axis = (0,1,0)
  Base = (0,0,0)
  FaceMakerClass = Part::FaceMakerBullseye
  Placement = pos=(0,0,36.15) rot=(0,0,1;0rad)
  Solid = false
  Source = -> Face127
  Symmetric = false
FEATURE [Part::Revolution] Revolve140  label="plugHousing073"
  Angle = 360
  Axis = (0,1,0)
  Base = (0,0,0)
  FaceMakerClass = Part::FaceMakerBullseye
  Placement = pos=(0,0,36.15) rot=(0,0,1;0rad)
  Solid = false
  Source = -> Face128
  Symmetric = false
FEATURE [Part::Feature] Face129
  shape: bbox 10 x 16.5 x 2e-07 mm, 1 faces, 0 solids (baked)
FEATURE [Part::Revolution] Revolve138  label="plugHousing071"
  Angle = 360
  Axis = (0,1,0)
  Base = (0,0,0)
  FaceMakerClass = Part::FaceMakerBullseye
  Placement = pos=(0,0,36.15) rot=(0,0,1;0rad)
  Solid = false
  Source = -> Face129
  Symmetric = false
FEATURE [Part::Feature] Face130
  shape: bbox 10 x 16.5 x 2e-07 mm, 1 faces, 0 solids (baked)
FEATURE [Part::Revolution] Revolve139  label="plugHousing072"
  Angle = 360
  Axis = (0,1,0)
  Base = (0,0,0)
  FaceMakerClass = Part::FaceMakerBullseye
  Placement = pos=(0,0,36.15) rot=(0,0,1;0rad)
  Solid = false
  Source = -> Face130
  Symmetric = false
FEATURE [Part::Feature] Face131
  shape: bbox 10 x 16.5 x 2e-07 mm, 1 faces, 0 solids (baked)
FEATURE [Part::Revolution] Revolve135  label="plugHousing068"
  Angle = 360
  Axis = (0,1,0)
  Base = (0,0,0)
  FaceMakerClass = Part::FaceMakerBullseye
  Placement = pos=(0,0,36.15) rot=(0,0,1;0rad)
  Solid = false
  Source = -> Face131
  Symmetric = false
FEATURE [Part::MultiFuse] Fusion112  label="plugHousing078"
  Placement = pos=(0,0,0) rot=(0,0,1;1.5708rad)
  Shapes = -> [Revolve135,Revolve139]
FEATURE [Part::Feature] Face132
  shape: bbox 10 x 16.5 x 2e-07 mm, 1 faces, 0 solids (baked)
FEATURE [Part::Revolution] Revolve141  label="plugHousing074"
  Angle = 360
  Axis = (0,1,0)
  Base = (0,0,0)
  FaceMakerClass = Part::FaceMakerBullseye
  Placement = pos=(0,0,36.15) rot=(0,0,1;0rad)
  Solid = false
  Source = -> Face132
  Symmetric = false
FEATURE [Part::MultiFuse] Fusion110  label="plugHousing076"
  Placement = pos=(0,0,0) rot=(0,0,1;1.5708rad)
  Shapes = -> [Revolve141,Revolve140]
FEATURE [Part::Feature] Face133
  shape: bbox 10 x 16.5 x 2e-07 mm, 1 faces, 0 solids (baked)
FEATURE [Part::Revolution] Revolve136  label="plugHousing069"
  Angle = 360
  Axis = (0,1,0)
  Base = (0,0,0)
  FaceMakerClass = Part::FaceMakerBullseye
  Placement = pos=(0,0,36.15) rot=(0,0,1;0rad)
  Solid = false
  Source = -> Face133
  Symmetric = false
FEATURE [Part::MultiFuse] Fusion106  label="plugHousing064"
  Placement = pos=(0,0,0) rot=(0,0,1;1.5708rad)
  Shapes = -> [Revolve138,Revolve136]
FEATURE [Part::MultiFuse] Fusion108  label="plugHousing066"
  Placement = pos=(0,19,0) rot=(0,0,1;3.14159rad)
  Shapes = -> [Fusion106,Fusion112]
FEATURE [Part::Feature] Face134
  shape: bbox 10 x 16.5 x 2e-07 mm, 1 faces, 0 solids (baked)
FEATURE [Part::Revolution] Revolve142  label="plugHousing075"
  Angle = 360
  Axis = (0,1,0)
  Base = (0,0,0)
  FaceMakerClass = Part::FaceMakerBullseye
  Placement = pos=(0,0,36.15) rot=(0,0,1;0rad)
  Solid = false
  Source = -> Face134
  Symmetric = false
FEATURE [Part::MultiFuse] Fusion107  label="plugHousing065"
  Placement = pos=(0,0,0) rot=(0,0,1;1.5708rad)
  Shapes = -> [Revolve137,Revolve142]
FEATURE [Part::MultiFuse] Fusion111  label="plugHousing077"
  Placement = pos=(0,19,0) rot=(0,0,1;3.14159rad)
  Shapes = -> [Fusion110,Fusion107]
FEATURE [Part::MultiFuse] Fusion109  label="plugHousing067"
  Placement = pos=(131.236,0,-0.15) rot=(0,0,1;0rad)
  Shapes = -> [Fusion108,Fusion111]
FEATURE [Part::MultiFuse] Fusion113  label="plugHousing079"
  Shapes = -> [Fillet043,Fusion109]
FEATURE [Part::Feature] Face135
  shape: bbox 3.5 x 17.8 x 2e-07 mm, 1 faces, 0 solids (baked)
FEATURE [Part::Revolution] Revolve143  label="removeToCreateScrewAndThreadedInsertHole049"
  Angle = 360
  Axis = (0,1,0)
  Base = (0,0,0)
  FaceMakerClass = Part::FaceMakerBullseye
  Placement = pos=(12.5,0,10) rot=(0,0,1;0rad)
  Solid = false
  Source = -> Face135
  Symmetric = false
FEATURE [Part::Feature] Face136
  shape: bbox 3.5 x 17.8 x 2e-07 mm, 1 faces, 0 solids (baked)
FEATURE [Part::Revolution] Revolve144  label="removeToCreateScrewAndThreadedInsertHole050"
  Angle = 360
  Axis = (0,1,0)
  Base = (0,0,0)
  FaceMakerClass = Part::FaceMakerBullseye
  Placement = pos=(12.5,0,62) rot=(0,0,1;0rad)
  Solid = false
  Source = -> Face136
  Symmetric = false
FEATURE [Part::Feature] Face137
  shape: bbox 3.5 x 17.8 x 2e-07 mm, 1 faces, 0 solids (baked)
FEATURE [Part::Revolution] Revolve145  label="removeToCreateScrewAndThreadedInsertHole051"
  Angle = 360
  Axis = (0,1,0)
  Base = (0,0,0)
  FaceMakerClass = Part::FaceMakerBullseye
  Placement = pos=(89.5,0,68.5) rot=(0,0,1;0rad)
  Solid = false
  Source = -> Face137
  Symmetric = false
FEATURE [Part::Feature] Face138
  shape: bbox 3.5 x 17.8 x 2e-07 mm, 1 faces, 0 solids (baked)
FEATURE [Part::Revolution] Revolve146  label="removeToCreateScrewAndThreadedInsertHole052"
  Angle = 360
  Axis = (0,1,0)
  Base = (0,0,0)
  FaceMakerClass = Part::FaceMakerBullseye
  Placement = pos=(89.5,0,3.5) rot=(0,0,1;0rad)
  Solid = false
  Source = -> Face138
  Symmetric = false
FEATURE [Part::Feature] Face139
  shape: bbox 3.5 x 17.8 x 2e-07 mm, 1 faces, 0 solids (baked)
FEATURE [Part::Revolution] Revolve147  label="removeToCreateScrewAndThreadedInsertHole053"
  Angle = 360
  Axis = (0,1,0)
  Base = (0,0,0)
  FaceMakerClass = Part::FaceMakerBullseye
  Placement = pos=(109.5,4.7,3.5) rot=(0,0,1;0rad)
  Solid = false
  Source = -> Face139
  Symmetric = false
FEATURE [Part::Feature] Face140
  shape: bbox 3.5 x 17.8 x 2e-07 mm, 1 faces, 0 solids (baked)
FEATURE [Part::Revolution] Revolve148  label="removeToCreateScrewAndThreadedInsertHole054"
  Angle = 360
  Axis = (0,1,0)
  Base = (0,0,0)
  FaceMakerClass = Part::FaceMakerBullseye
  Placement = pos=(109.5,4.7,68.5) rot=(0,0,1;0rad)
  Solid = false
  Source = -> Face140
  Symmetric = false
FEATURE [Part::MultiFuse] Fusion114  label="removeToCreateScrewAndThreadedInsertHole055"
  Shapes = -> [Revolve148,Revolve147,Revolve146,Revolve145,Revolve144,Revolve143]
FEATURE [Part::Cut] Cut047  label="casePillars004"
  Base = -> Cut037
  Tool = -> Fusion114
FEATURE [Part::Feature] Face141
  shape: bbox 3.5 x 17.8 x 2e-07 mm, 1 faces, 0 solids (baked)
FEATURE [Part::Feature] Face142
  shape: bbox 3.5 x 17.8 x 2e-07 mm, 1 faces, 0 solids (baked)
FEATURE [Part::Feature] Face143
  shape: bbox 3.5 x 17.8 x 2e-07 mm, 1 faces, 0 solids (baked)
FEATURE [Part::Revolution] Revolve149  label="removeToCreateScrewAndThreadedInsertHole057"
  Angle = 360
  Axis = (0,1,0)
  Base = (0,0,0)
  FaceMakerClass = Part::FaceMakerBullseye
  Placement = pos=(12.5,0,10) rot=(0,0,1;0rad)
  Solid = false
  Source = -> Face141
  Symmetric = false
FEATURE [Part::Feature] Face144
  shape: bbox 3.5 x 17.8 x 2e-07 mm, 1 faces, 0 solids (baked)
FEATURE [Part::Feature] Face145
  shape: bbox 3.5 x 17.8 x 2e-07 mm, 1 faces, 0 solids (baked)
FEATURE [Part::Feature] Face146
  shape: bbox 3.5 x 17.8 x 2e-07 mm, 1 faces, 0 solids (baked)
FEATURE [Part::Revolution] Revolve150  label="removeToCreateScrewAndThreadedInsertHole058"
  Angle = 360
  Axis = (0,1,0)
  Base = (0,0,0)
  FaceMakerClass = Part::FaceMakerBullseye
  Placement = pos=(12.5,0,62) rot=(0,0,1;0rad)
  Solid = false
  Source = -> Face146
  Symmetric = false
FEATURE [Part::Revolution] Revolve151  label="removeToCreateScrewAndThreadedInsertHole059"
  Angle = 360
  Axis = (0,1,0)
  Base = (0,0,0)
  FaceMakerClass = Part::FaceMakerBullseye
  Placement = pos=(89.5,0,68.5) rot=(0,0,1;0rad)
  Solid = false
  Source = -> Face143
  Symmetric = false
FEATURE [Part::Revolution] Revolve152  label="removeToCreateScrewAndThreadedInsertHole060"
  Angle = 360
  Axis = (0,1,0)
  Base = (0,0,0)
  FaceMakerClass = Part::FaceMakerBullseye
  Placement = pos=(89.5,0,3.5) rot=(0,0,1;0rad)
  Solid = false
  Source = -> Face142
  Symmetric = false
FEATURE [Part::Revolution] Revolve153  label="removeToCreateScrewAndThreadedInsertHole061"
  Angle = 360
  Axis = (0,1,0)
  Base = (0,0,0)
  FaceMakerClass = Part::FaceMakerBullseye
  Placement = pos=(109.5,4.7,3.5) rot=(0,0,1;0rad)
  Solid = false
  Source = -> Face145
  Symmetric = false
FEATURE [Part::Revolution] Revolve154  label="removeToCreateScrewAndThreadedInsertHole062"
  Angle = 360
  Axis = (0,1,0)
  Base = (0,0,0)
  FaceMakerClass = Part::FaceMakerBullseye
  Placement = pos=(109.5,4.7,68.5) rot=(0,0,1;0rad)
  Solid = false
  Source = -> Face144
  Symmetric = false
FEATURE [Part::MultiFuse] Fusion115  label="removeToCreateScrewAndThreadedInsertHole056"
  Shapes = -> [Revolve154,Revolve153,Revolve152,Revolve151,Revolve150,Revolve149]
FEATURE [Part::Feature] Face147
  shape: bbox 9.8 x 26.5 x 2e-07 mm, 1 faces, 0 solids (baked)
FEATURE [Part::Revolution] Revolve155
  Angle = 360
  Axis = (0,1,0)
  Base = (0,0,0)
  FaceMakerClass = Part::FaceMakerBullseye
  Placement = pos=(0,0,0) rot=(0,0,1;1.5708rad)
  Solid = false
  Source = -> Face147
  Symmetric = false
FEATURE [Part::Feature] Face148
  shape: bbox 9.8 x 26.5 x 2e-07 mm, 1 faces, 0 solids (baked)
FEATURE [Part::Revolution] Revolve156
  Angle = 360
  Axis = (0,1,0)
  Base = (0,0,0)
  FaceMakerClass = Part::FaceMakerBullseye
  Placement = pos=(0,0,0) rot=(0,0,1;1.5708rad)
  Solid = false
  Source = -> Face148
  Symmetric = false
FEATURE [Part::MultiFuse] Fusion116
  Placement = pos=(-18,19,36) rot=(0,0,1;0rad)
  Shapes = -> [Revolve156,Revolve155]
FEATURE [Part::Box] Box029  label="Cube016"
  AttacherType = Attacher::AttachEngine3D
  Height = 28
  Length = 3
  Placement = pos=(110.7,19,22) rot=(0,0,1;0rad)
  Width = 15.7
FEATURE [Part::Cylinder] Cylinder046
  Angle = 360
  AttacherType = Attacher::AttachEngine3D
  Height = 10
  Placement = pos=(0,0,36.15) rot=(0,0,1;0rad)
  Radius = 4
FEATURE [Part::Cylinder] Cylinder047
  Angle = 360
  AttacherType = Attacher::AttachEngine3D
  Height = 20
  Placement = pos=(0,0,36.15) rot=(0,0,1;0rad)
  Radius = 10.3
FEATURE [Part::MultiFuse] Fusion117  label="removeToCreteHoleForPlugHousing041"
  Placement = pos=(70,19,36) rot=(0,1,0;1.5708rad)
  Shapes = -> [Cylinder047,Cylinder046]
FEATURE [Part::Cut] Cut049  label="plugHousingTab004"
  Base = -> Box029
  Placement = pos=(-107.4,-14,0) rot=(0,0,1;0rad)
  Tool = -> Fusion117
FEATURE [Part::Box] Box030  label="Cube017"
  AttacherType = Attacher::AttachEngine3D
  Height = 28
  Length = 3
  Placement = pos=(110.7,19,22) rot=(0,0,1;0rad)
  Width = 15.7
FEATURE [Part::Cylinder] Cylinder048
  Angle = 360
  AttacherType = Attacher::AttachEngine3D
  Height = 10
  Placement = pos=(0,0,36.15) rot=(0,0,1;0rad)
  Radius = 4
FEATURE [Part::Cylinder] Cylinder049
  Angle = 360
  AttacherType = Attacher::AttachEngine3D
  Height = 20
  Placement = pos=(0,0,36.15) rot=(0,0,1;0rad)
  Radius = 10.3
FEATURE [Part::MultiFuse] Fusion118  label="removeToCreteHoleForPlugHousing042"
  Placement = pos=(70,19,36) rot=(0,1,0;1.5708rad)
  Shapes = -> [Cylinder049,Cylinder048]
FEATURE [Part::Cut] Cut050  label="plugHousingTab005"
  Base = -> Box030
  Placement = pos=(-107.4,-14,0) rot=(0,0,1;0rad)
  Tool = -> Fusion118
FEATURE [Part::MultiFuse] Fusion119
  Placement = pos=(9.6,23,0) rot=(0,0,1;3.14159rad)
  Shapes = -> [Cut049,Cut050]
FEATURE [Part::Box] Box031  label="Cube018"
  AttacherType = Attacher::AttachEngine3D
  Height = 10
  Length = 3
  Placement = pos=(3.3,4,12) rot=(0,0,1;0rad)
  Width = 10
FEATURE [Part::Fillet] Fillet044
  Base = -> Box031
  Edges = 1 edges r=2: [Edge11]
FEATURE [Part::Box] Box032  label="Cube019"
  AttacherType = Attacher::AttachEngine3D
  Height = 10
  Length = 3
  Placement = pos=(3.3,4,50) rot=(0,0,1;0rad)
  Width = 10
FEATURE [Part::Fillet] Fillet045
  Base = -> Box032
  Edges = 1 edges r=2: [Edge12]
FEATURE [Part::Box] Box033  label="Cube020"
  AttacherType = Attacher::AttachEngine3D
  Height = 28
  Length = 4
  Placement = pos=(5,0,22) rot=(0,0,1;0rad)
  Width = 10
FEATURE [Part::Fillet] Fillet046
  Base = -> Box033
  Edges = 1 edges r=1: [Edge7]
FEATURE [Part::Fillet] Fillet047
  Base = -> Fillet046
  Edges = 1 edges r=2: [Edge5]
FEATURE [Part::Fillet] Fillet048
  Base = -> Fillet047
  Edges = 1 edges r=2: [Edge2]
FEATURE [Part::Cylinder] Cylinder050
  Angle = 360
  AttacherType = Attacher::AttachEngine3D
  Height = 20
  Placement = pos=(0,0,36.15) rot=(0,0,1;0rad)
  Radius = 8.2
FEATURE [Part::Cylinder] Cylinder051
  Angle = 360
  AttacherType = Attacher::AttachEngine3D
  Height = 10
  Placement = pos=(0,0,36.15) rot=(0,0,1;0rad)
  Radius = 4
FEATURE [Part::MultiFuse] Fusion120  label="removeToCreteHoleForPlugHousing043"
  Placement = pos=(-42,19,36) rot=(0,1,0;1.5708rad)
  Shapes = -> [Cylinder050,Cylinder051]
FEATURE [Sketcher::SketchObject] Sketch067  label="topSketch018"
  FullyConstrained = true
  sketch-geometry (4):
    g0: LineSegment StartX=16.8446 StartY=31.512 StartZ=0 EndX=16.3251 EndY=34.4666 EndZ=0
    g1: ArcOfCircle CenterX=19 CenterY=19.2524 CenterZ=0 NormalX=0 NormalY=0 NormalZ=1 AngleXU=0 Radius=15.4476 StartAngle=1.74483 EndAngle=2.72717
    g2: ArcOfCircle CenterX=19 CenterY=19.2524 CenterZ=0 NormalX=0 NormalY=0 NormalZ=1 AngleXU=0 Radius=12.4476 StartAngle=1.74483 EndAngle=2.73189
    g3: LineSegment StartX=4.86004 StartY=25.4725 StartZ=0 EndX=7.58253 EndY=24.2107 EndZ=0
  constraints (7):
    c: Block(g0)
    c: Coincident(g1,g0)
    c: Coincident(g2,g0)
    c: Coincident(g3,g1)
    c: Coincident(g3,g2)
    c: Block(g1)
    c: Block(g2)
FEATURE [Part::Extrusion] Extrude058
  Base = -> Sketch067
  Dir = (0,0,1)
  DirMode = 2
  FaceMakerClass = Part::FaceMakerBullseye
  LengthFwd = 10
  LengthRev = 0
  Placement = pos=(0,0,31) rot=(0,0,1;0rad)
  Solid = true
  Symmetric = false
FEATURE [Part::Cut] Cut051
  Base = -> Extrude058
  Tool = -> Fusion120
FEATURE [Part::Fillet] Fillet049
  Base = -> Cut051
  Edges = 1 edges r=2: [Edge1]
FEATURE [Part::Fillet] Fillet050
  Base = -> Fillet049
  Edges = 1 edges r=2.5: [Edge1]
FEATURE [Part::Fillet] Fillet051
  Base = -> Fillet050
  Edges = 1 edges r=2.5: [Edge2]
FEATURE [Part::MultiFuse] Fusion121  label="wireHolder003"
  Shapes = -> [Fusion116,Fillet051]
FEATURE [Part::MultiFuse] Fusion122
  Shapes = -> [Fillet045,Fusion121]
FEATURE [Part::MultiFuse] Fusion123  label="wireHolder004"
  Shapes = -> [Fusion122,Fillet048]
FEATURE [Part::MultiFuse] Fusion124  label="wireHolder005"
  Shapes = -> [Fillet044,Fusion119,Fusion123]
FEATURE [Sketcher::SketchObject] Sketch068  label="topSketch019"
  FullyConstrained = true
  sketch-geometry (6):
    g0: LineSegment StartX=19 StartY=38 StartZ=0 EndX=117 EndY=38 EndZ=0
    g1: ArcOfCircle CenterX=19 CenterY=19 CenterZ=0 NormalX=0 NormalY=0 NormalZ=1 AngleXU=0 Radius=19 StartAngle=1.5708 EndAngle=3.14159
    g2: LineSegment StartX=117 StartY=38 StartZ=0 EndX=117 EndY=19 EndZ=0
    g3: LineSegment StartX=98 StartY=1.0161e-12 StartZ=0 EndX=5.22862e-06 EndY=1.0161e-12 EndZ=0
    g4: LineSegment StartX=5.22862e-06 StartY=19 StartZ=0 EndX=5.22862e-06 EndY=1.0161e-12 EndZ=0
    g5: ArcOfCircle CenterX=98 CenterY=19 CenterZ=0 NormalX=0 NormalY=0 NormalZ=1 AngleXU=0 Radius=19 StartAngle=4.71239 EndAngle=6.28319
  constraints (16):
    c: Horizontal(g0)
    c: Distance(g0) = 98
    c: Coincident(g1,g0)
    c: Block(g1)
    c: Coincident(g2,g0)
    c: Vertical(g2)
    c: Distance(g2) = 19
    c: Horizontal(g3)
    c: Coincident(g4,g1)
    c: Vertical(g4)
    c: Coincident(g3,g4)
    c: Block(g3)
    c: Coincident(g5,g2)
    c: Coincident(g5,g3)
    c: Block(g0)
    c: Block(g5)
FEATURE [Part::Extrusion] Extrude059  label="sideA002"
  Base = -> Sketch068
  Dir = (0,0,1)
  DirMode = 2
  FaceMakerClass = Part::FaceMakerBullseye
  LengthFwd = 3
  LengthRev = 0
  Placement = pos=(0,0,-2.7) rot=(0,0,1;0rad)
  Solid = true
  Symmetric = false
FEATURE [Sketcher::SketchObject] Sketch069  label="topSketch020"
  FullyConstrained = true
  sketch-geometry (6):
    g0: LineSegment StartX=19 StartY=38 StartZ=0 EndX=117 EndY=38 EndZ=0
    g1: ArcOfCircle CenterX=19 CenterY=19 CenterZ=0 NormalX=0 NormalY=0 NormalZ=1 AngleXU=0 Radius=19 StartAngle=1.5708 EndAngle=3.14159
    g2: LineSegment StartX=117 StartY=38 StartZ=0 EndX=117 EndY=19 EndZ=0
    g3: LineSegment StartX=98 StartY=1.0161e-12 StartZ=0 EndX=5.22862e-06 EndY=1.0161e-12 EndZ=0
    g4: LineSegment StartX=5.22862e-06 StartY=19 StartZ=0 EndX=5.22862e-06 EndY=1.0161e-12 EndZ=0
    g5: ArcOfCircle CenterX=98 CenterY=19 CenterZ=0 NormalX=0 NormalY=0 NormalZ=1 AngleXU=0 Radius=19 StartAngle=4.71239 EndAngle=6.28319
  constraints (16):
    c: Horizontal(g0)
    c: Distance(g0) = 98
    c: Coincident(g1,g0)
    c: Block(g1)
    c: Coincident(g2,g0)
    c: Vertical(g2)
    c: Distance(g2) = 19
    c: Horizontal(g3)
    c: Coincident(g4,g1)
    c: Vertical(g4)
    c: Coincident(g3,g4)
    c: Block(g3)
    c: Coincident(g5,g2)
    c: Coincident(g5,g3)
    c: Block(g0)
    c: Block(g5)
FEATURE [Part::Extrusion] Extrude060  label="sideB002"
  Base = -> Sketch069
  Dir = (0,0,1)
  DirMode = 2
  FaceMakerClass = Part::FaceMakerBullseye
  LengthFwd = 3
  LengthRev = 0
  Placement = pos=(0,0,71.7) rot=(0,0,1;0rad)
  Solid = true
  Symmetric = false
FEATURE [Part::MultiFuse] Fusion127  label="removeFromBottom001"
  Placement = pos=(2,0,0) rot=(0,0,1;0rad)
  Shapes = -> [Extrude059,Extrude060]
FEATURE [Part::Cylinder] Cylinder052
  Angle = 360
  AttacherType = Attacher::AttachEngine3D
  Height = 20
  Placement = pos=(0,0,36.15) rot=(0,0,1;0rad)
  Radius = 14
FEATURE [Part::Cylinder] Cylinder053
  Angle = 360
  AttacherType = Attacher::AttachEngine3D
  Height = 10
  Placement = pos=(0,0,36.15) rot=(0,0,1;0rad)
  Radius = 4
FEATURE [Part::MultiFuse] Fusion128  label="removeToCreteHoleForPlugHousing044"
  Placement = pos=(70,19,36) rot=(0,1,0;1.5708rad)
  Shapes = -> [Cylinder052,Cylinder053]
FEATURE [Part::Cut] Cut052  label="bottom011"
  Base = -> Extrude043
  Tool = -> Fusion128
FEATURE [Part::Cut] Cut054  label="bottom012"
  Base = -> Cut052
  Tool = -> Fusion115
FEATURE [Sketcher::SketchObject] Sketch070
  FullyConstrained = true
  Placement = pos=(117,19,0) rot=(0.57735,0.57735,0.57735;2.0944rad)
  sketch-geometry (48):
    g0: LineSegment StartX=-49.19 StartY=69.25 StartZ=0 EndX=-49.19 EndY=66.25 EndZ=0
    g1: LineSegment StartX=-49.19 StartY=63.5 StartZ=0 EndX=-49.19 EndY=60.5 EndZ=0
    g2: LineSegment StartX=-49.19 StartY=57.75 StartZ=0 EndX=-49.19 EndY=54.75 EndZ=0
    g3: LineSegment StartX=-49.19 StartY=52 StartZ=0 EndX=-49.19 EndY=49 EndZ=0
    g4: LineSegment StartX=-49.19 StartY=46.25 StartZ=0 EndX=-49.19 EndY=43.25 EndZ=0
    g5: LineSegment StartX=-49.19 StartY=40.5 StartZ=0 EndX=-49.19 EndY=37.5 EndZ=0
    g6: LineSegment StartX=-49.19 StartY=34.5 StartZ=0 EndX=-49.19 EndY=31.5 EndZ=0
    g7: LineSegment StartX=-49.19 StartY=28.75 StartZ=0 EndX=-49.19 EndY=25.75 EndZ=0
    g8: LineSegment StartX=-49.19 StartY=23 StartZ=0 EndX=-49.19 EndY=20 EndZ=0
    g9: LineSegment StartX=-49.19 StartY=17.25 StartZ=0 EndX=-49.19 EndY=14.25 EndZ=0
    g10: LineSegment StartX=-49.19 StartY=11.5 StartZ=0 EndX=-49.19 EndY=8.5 EndZ=0
    g11: LineSegment StartX=-49.19 StartY=5.75 StartZ=0 EndX=-49.19 EndY=2.75 EndZ=0
    g12: ArcOfCircle CenterX=-1.5 CenterY=67.75 CenterZ=0 NormalX=0 NormalY=0 NormalZ=1 AngleXU=0 Radius=1.5 StartAngle=4.71239 EndAngle=7.85398
    g13: ArcOfCircle CenterX=-1.5 CenterY=62 CenterZ=0 NormalX=0 NormalY=0 NormalZ=1 AngleXU=0 Radius=1.5 StartAngle=4.71239 EndAngle=7.85398
    g14: ArcOfCircle CenterX=-1.5 CenterY=56.25 CenterZ=0 NormalX=0 NormalY=0 NormalZ=1 AngleXU=0 Radius=1.5 StartAngle=4.71239 EndAngle=7.85398
    g15: ArcOfCircle CenterX=-11.49 CenterY=50.5 CenterZ=0 NormalX=0 NormalY=0 NormalZ=1 AngleXU=0 Radius=1.5 StartAngle=4.71239 EndAngle=7.85398
    g16: ArcOfCircle CenterX=-16.28 CenterY=44.75 CenterZ=0 NormalX=0 NormalY=0 NormalZ=1 AngleXU=0 Radius=1.5 StartAngle=4.71239 EndAngle=7.85398
    g17: ArcOfCircle CenterX=-18.2337 CenterY=39 CenterZ=0 NormalX=0 NormalY=0 NormalZ=1 AngleXU=0 Radius=1.5 StartAngle=4.71485 EndAngle=7.85398
    g18: ArcOfCircle CenterX=-16.2837 CenterY=27.25 CenterZ=0 NormalX=0 NormalY=0 NormalZ=1 AngleXU=0 Radius=1.5 StartAngle=4.71485 EndAngle=7.85398
    g19: ArcOfCircle CenterX=-18.2337 CenterY=33 CenterZ=0 NormalX=0 NormalY=0 NormalZ=1 AngleXU=0 Radius=1.5 StartAngle=4.71485 EndAngle=7.85398
    g20: ArcOfCircle CenterX=-11.49 CenterY=21.5 CenterZ=0 NormalX=0 NormalY=0 NormalZ=1 AngleXU=0 Radius=1.5 StartAngle=4.71239 EndAngle=7.85398
    g21: ArcOfCircle CenterX=-1.5 CenterY=4.25 CenterZ=0 NormalX=0 NormalY=0 NormalZ=1 AngleXU=0 Radius=1.5 StartAngle=4.71239 EndAngle=7.85398
    g22: ArcOfCircle CenterX=-1.5 CenterY=10 CenterZ=0 NormalX=0 NormalY=0 NormalZ=1 AngleXU=0 Radius=1.5 StartAngle=4.71239 EndAngle=7.85398
    g23: ArcOfCircle CenterX=-1.5 CenterY=15.75 CenterZ=0 NormalX=0 NormalY=0 NormalZ=1 AngleXU=0 Radius=1.5 StartAngle=4.71239 EndAngle=7.85398
    g24: LineSegment StartX=-49.19 StartY=69.25 StartZ=0 EndX=-1.5 EndY=69.25 EndZ=0
    g25: LineSegment StartX=-49.19 StartY=66.25 StartZ=0 EndX=-1.5 EndY=66.25 EndZ=0
    g26: LineSegment StartX=-49.19 StartY=63.5 StartZ=0 EndX=-1.5 EndY=63.5 EndZ=0
    g27: LineSegment StartX=-49.19 StartY=60.5 StartZ=0 EndX=-1.5 EndY=60.5 EndZ=0
    g28: LineSegment StartX=-49.19 StartY=57.75 StartZ=0 EndX=-1.5 EndY=57.75 EndZ=0
    g29: LineSegment StartX=-49.19 StartY=54.75 StartZ=0 EndX=-1.5 EndY=54.75 EndZ=0
    g30: LineSegment StartX=-49.19 StartY=52 StartZ=0 EndX=-11.49 EndY=52 EndZ=0
    g31: LineSegment StartX=-49.19 StartY=49 StartZ=0 EndX=-11.49 EndY=49 EndZ=0
    g32: LineSegment StartX=-49.19 StartY=46.25 StartZ=0 EndX=-16.28 EndY=46.25 EndZ=0
    g33: LineSegment StartX=-49.19 StartY=43.25 StartZ=0 EndX=-16.28 EndY=43.25 EndZ=0
    g34: LineSegment StartX=-49.19 StartY=40.5 StartZ=0 EndX=-18.2337 EndY=40.5 EndZ=0
    g35: LineSegment StartX=-49.19 StartY=37.5 StartZ=0 EndX=-18.23 EndY=37.5 EndZ=0
    g36: LineSegment StartX=-49.19 StartY=34.5 StartZ=0 EndX=-18.2337 EndY=34.5 EndZ=0
    g37: LineSegment StartX=-49.19 StartY=31.5 StartZ=0 EndX=-18.23 EndY=31.5 EndZ=0
    g38: LineSegment StartX=-49.19 StartY=28.75 StartZ=0 EndX=-16.2837 EndY=28.75 EndZ=0
    g39: LineSegment StartX=-49.19 StartY=25.75 StartZ=0 EndX=-16.28 EndY=25.75 EndZ=0
    g40: LineSegment StartX=-49.19 StartY=23 StartZ=0 EndX=-11.49 EndY=23 EndZ=0
    g41: LineSegment StartX=-49.19 StartY=20 StartZ=0 EndX=-11.49 EndY=20 EndZ=0
    g42: LineSegment StartX=-49.19 StartY=17.25 StartZ=0 EndX=-1.5 EndY=17.25 EndZ=0
    g43: LineSegment StartX=-49.19 StartY=14.25 StartZ=0 EndX=-1.5 EndY=14.25 EndZ=0
    g44: LineSegment StartX=-49.19 StartY=11.5 StartZ=0 EndX=-1.5 EndY=11.5 EndZ=0
    g45: LineSegment StartX=-49.19 StartY=8.5 StartZ=0 EndX=-1.5 EndY=8.5 EndZ=0
    g46: LineSegment StartX=-49.19 StartY=5.75 StartZ=0 EndX=-1.5 EndY=5.75 EndZ=0
    g47: LineSegment StartX=-49.19 StartY=2.75 StartZ=0 EndX=-1.5 EndY=2.75 EndZ=0
  constraints (120):
    c: Vertical(g0)
    c: Distance(g0) = 3
    c: Block(g0)
    c: Vertical(g1)
    c: Distance(g1) = 3
    c: Vertical(g2)
    c: Equal(g0,g2) = 3
    c: Block(g2)
    c: Vertical(g3)
    c: Equal(g1,g3) = 3
    c: Vertical(g4)
    c: Equal(g0,g4) = 3
    c: Block(g4)
    c: Vertical(g5)
    c: Equal(g1,g5) = 3
    c: Vertical(g6)
    c: Equal(g0,g6) = 3
    c: Block(g6)
    c: Vertical(g7)
    c: Equal(g1,g7) = 3
    c: Vertical(g8)
    c: Equal(g0,g8) = 3
    c: Block(g8)
    c: Vertical(g9)
    c: Equal(g1,g9) = 3
    c: Vertical(g10)
    c: Equal(g0,g10) = 3
    c: Block(g10)
    c: Vertical(g11)
    c: Equal(g1,g11) = 3
    c: Block(g12)
    c: Block(g13)
    c: Block(g14)
    c: Block(g15)
    c: Block(g16)
    c: Block(g17)
    c: Block(g18)
    c: Block(g19)
    c: Block(g20)
    c: Block(g21)
    c: Block(g22)
    c: Block(g23)
    c: Block(g11)
    c: Block(g9)
    c: Block(g7)
    c: Block(g5)
    c: Block(g3)
    c: Block(g1)
    c: Coincident(g24,g0)
    c: Coincident(g24,g12)
    c: Horizontal(g24)
    c: Coincident(g25,g0)
    c: Coincident(g25,g12)
    c: Horizontal(g25)
    c: Coincident(g26,g1)
    c: Coincident(g26,g13)
    c: Horizontal(g26)
    c: Coincident(g27,g1)
    c: Coincident(g27,g13)
    c: Horizontal(g27)
    c: Coincident(g28,g2)
    c: Coincident(g28,g14)
    c: Horizontal(g28)
    c: Coincident(g29,g2)
    c: Coincident(g29,g14)
    c: Horizontal(g29)
    c: Coincident(g30,g3)
    c: Coincident(g30,g15)
    c: Horizontal(g30)
    c: Coincident(g31,g3)
    c: Coincident(g31,g15)
    c: Horizontal(g31)
    c: Coincident(g32,g4)
    c: Coincident(g32,g16)
    c: Horizontal(g32)
    c: Coincident(g33,g4)
    c: Coincident(g33,g16)
    c: Horizontal(g33)
    c: Coincident(g34,g5)
    c: Coincident(g34,g17)
    c: Horizontal(g34)
    c: Coincident(g35,g5)
    c: Coincident(g35,g17)
    c: Horizontal(g35)
    c: Coincident(g36,g6)
    c: Coincident(g36,g19)
    c: Horizontal(g36)
    c: Coincident(g37,g6)
    c: Coincident(g37,g19)
    c: Horizontal(g37)
    c: Coincident(g38,g7)
    c: Coincident(g38,g18)
    c: Horizontal(g38)
    c: Coincident(g39,g7)
    c: Coincident(g39,g18)
    c: Horizontal(g39)
    c: Coincident(g40,g8)
    c: Coincident(g40,g20)
    c: Horizontal(g40)
    c: Coincident(g41,g8)
    c: Coincident(g41,g20)
    c: Horizontal(g41)
    c: Coincident(g42,g9)
    c: Coincident(g42,g23)
    c: Horizontal(g42)
    c: Coincident(g43,g9)
    c: Coincident(g43,g23)
    c: Horizontal(g43)
    c: Coincident(g44,g10)
    c: Coincident(g44,g22)
    c: Horizontal(g44)
    c: Coincident(g45,g10)
    c: Coincident(g45,g22)
    c: Horizontal(g45)
    c: Coincident(g46,g11)
    c: Coincident(g46,g21)
    c: Horizontal(g46)
    c: Coincident(g47,g11)
    c: Coincident(g47,g21)
    c: Horizontal(g47)
FEATURE [Part::Extrusion] Extrude061
  Base = -> Sketch070
  Dir = (1,0,0)
  DirMode = 2
  FaceMakerClass = Part::FaceMakerBullseye
  LengthFwd = 23
  LengthRev = 0
  Placement = pos=(-19,0,0) rot=(0,0,1;0rad)
  Solid = true
  Symmetric = false
FEATURE [Part::Fillet] Fillet052  label="removeToCreateVentalationHoles002"
  Base = -> Extrude061
  Edges = <same value as first occurrence — deduplicated (x6 in doc)>
  Placement = pos=(7,0.02,0) rot=(0,0,1;0rad)
FEATURE [Part::MultiFuse] Fusion130  label="bottom013"
  Shapes = -> [Cut054,Cut034]
FEATURE [Part::Cut] Cut055
  Base = -> Fusion130
  Tool = -> Fillet052
FEATURE [Part::Cylinder] Cylinder054
  Angle = 360
  AttacherType = Attacher::AttachEngine3D
  Height = 20
  Placement = pos=(0,0,36.15) rot=(0,0,1;0rad)
  Radius = 4
FEATURE [Sketcher::SketchObject] Sketch071  label="bottomSketch002"
  FullyConstrained = true
  sketch-geometry (32):
    g0: LineSegment StartX=3.3 StartY=-6.03275e-07 StartZ=0 EndX=98 EndY=-6.03275e-07 EndZ=0
    g1: ArcOfCircle CenterX=98 CenterY=19 CenterZ=0 NormalX=0 NormalY=0 NormalZ=1 AngleXU=0 Radius=19 StartAngle=4.71239 EndAngle=5.71103
    g2: LineSegment StartX=6.3 StartY=8 StartZ=0 EndX=3.3 EndY=8 EndZ=0
    g3: LineSegment StartX=3.3 StartY=8 StartZ=0 EndX=3.3 EndY=-6.03275e-07 EndZ=0
    g4: ArcOfCircle CenterX=8.3 CenterY=5 CenterZ=0 NormalX=0 NormalY=0 NormalZ=1 AngleXU=0 Radius=2 StartAngle=3.14159 EndAngle=4.71239
    g5: LineSegment StartX=6.3 StartY=8 StartZ=0 EndX=6.3 EndY=5 EndZ=0
    g6: ArcOfCircle CenterX=98 CenterY=19 CenterZ=0 NormalX=0 NormalY=0 NormalZ=1 AngleXU=0 Radius=12.7 StartAngle=4.71239 EndAngle=6.28319
    g7: LineSegment StartX=94.7 StartY=3 StartZ=0 EndX=8.3 EndY=3 EndZ=0
    g8-g12: Circle x5 (B-spline internal-alignment scaffolding for g13; pole/knot coordinates omitted)
    g13: BSplineCurve PolesCount=5 KnotsCount=3 Degree=3 IsPeriodic=0
    g14: GeomPoint X=98 Y=6.3 Z=0
    g15: GeomPoint X=96.3938 Y=4.71946 Z=0
    g16: GeomPoint X=94.7 Y=3 Z=0
    g17-g23: Circle x7 (B-spline internal-alignment scaffolding for g24; pole/knot coordinates omitted)
    g24: BSplineCurve PolesCount=7 KnotsCount=5 Degree=3 IsPeriodic=0
    g25-g29: GeomPoint x5 (B-spline internal-alignment scaffolding for g24; pole/knot coordinates omitted)
    g30: ArcOfCircle CenterX=98 CenterY=19 CenterZ=0 NormalX=0 NormalY=0 NormalZ=1 AngleXU=0 Radius=15.7 StartAngle=5.81226 EndAngle=6.28319
    g31: LineSegment StartX=110.7 StartY=19 StartZ=0 EndX=113.7 EndY=19 EndZ=0
  constraints (41):
    c: Horizontal(g0)
    c: Coincident(g1,g0)
    c: Block(g1)
    c: Horizontal(g2)
    c: Distance(g2) = 3
    c: Coincident(g3,g2)
    c: Vertical(g3)
    c: Coincident(g3,g0)
    c: Block(g4)
    c: Block(g2)
    c: Coincident(g5,g2)
    c: Coincident(g5,g4)
    c: Vertical(g5)
    c: Coincident(g6,g1)
    c: Block(g6)
    c: Coincident(g7,g4)
    c: Horizontal(g7)
    c: Block(g0)
    c: Block(g7)
    c: Block(g3)
    c: Coincident(g13,g6)
    c: Weight(g8) = 1
    c: Equal(g8, g9-g12) x4
    c: Coincident(g13,g7)
    c: InternalAlignment(g8-g12 -> g13) x5
    c: InternalAlignment(g14,g13)
    c: InternalAlignment(g15,g13)
    c: InternalAlignment(g16,g13)
    c: Block(g13)
    c: Weight(g17) = 1
    c: Equal(g17, g18-g23) x6
    c: Coincident(g24,g1)
    c: InternalAlignment(g17-g23 -> g24) x7
    c: InternalAlignment(g25-g29 -> g24) x5
    c: Block(g24)
    c: Coincident(g30,g24)
    c: Coincident(g31,g6)
    c: Coincident(g31,g30)
    c: Horizontal(g31)
    c: Block(g31)
    c: Block(g30)
FEATURE [Part::Extrusion] Extrude062  label="bottom014"
  Base = -> Sketch071
  Dir = (0,0,1)
  DirMode = 2
  FaceMakerClass = Part::FaceMakerBullseye
  LengthFwd = 71.4
  LengthRev = 0
  Placement = pos=(0,0,0.3) rot=(0,0,1;0rad)
  Solid = true
  Symmetric = false
FEATURE [Part::Fillet] Fillet054
  Base = -> Extrude062
  Edges = 1 edges r=2.4: [Edge17]
FEATURE [Part::Fillet] Fillet055  label="bottom015"
  Base = -> Fillet054
  Edges = 1 edges r=2.4: [Edge36]
FEATURE [Part::Cylinder] Cylinder055
  Angle = 360
  AttacherType = Attacher::AttachEngine3D
  Height = 10
  Placement = pos=(0,0,36.15) rot=(0,0,1;0rad)
  Radius = 4
FEATURE [Part::MultiFuse] Fusion131  label="removeToCreateHoleForPlugHousing002"
  Placement = pos=(70,19,36.15) rot=(0,1,0;1.5708rad)
  Shapes = -> [Cylinder054,Cylinder055]
FEATURE [Part::Cut] Cut056  label="Bottom001"
  Base = -> Fillet055
  Placement = pos=(9,0,0) rot=(0,0,1;0rad)
  Tool = -> Fusion131
FEATURE [Part::Cut] Cut057
  Base = -> Cut055
  Tool = -> Cut056
FEATURE [Sketcher::SketchObject] Sketch072  label="topSketch021"
  FullyConstrained = true
  sketch-geometry (4):
    g0: ArcOfCircle CenterX=105 CenterY=19 CenterZ=0 NormalX=0 NormalY=0 NormalZ=1 AngleXU=0 Radius=20.6155 StartAngle=5.54125 EndAngle=6.28319
    g1: ArcOfCircle CenterX=105 CenterY=19 CenterZ=0 NormalX=0 NormalY=0 NormalZ=1 AngleXU=0 Radius=13 StartAngle=5.54125 EndAngle=6.28319
    g2: LineSegment StartX=118 StartY=19 StartZ=0 EndX=125.616 EndY=19 EndZ=0
    g3: LineSegment StartX=114.583 StartY=10.2157 StartZ=0 EndX=120.197 EndY=5.06982 EndZ=0
  constraints (7):
    c: Block(g0)
    c: Block(g1)
    c: Coincident(g2,g1)
    c: Coincident(g2,g0)
    c: Horizontal(g2)
    c: Coincident(g3,g1)
    c: Coincident(g3,g0)
FEATURE [Part::Extrusion] Extrude063  label="bottomPlugHousingBit003"
  Base = -> Sketch072
  Dir = (0,0,1)
  DirMode = 2
  FaceMakerClass = Part::FaceMakerBullseye
  LengthFwd = 72
  LengthRev = 0
  Solid = true
  Symmetric = false
FEATURE [Part::Cylinder] Cylinder056
  Angle = 360
  AttacherType = Attacher::AttachEngine3D
  Height = 20
  Placement = pos=(0,0,36.15) rot=(0,0,1;0rad)
  Radius = 14.3
FEATURE [Part::Cylinder] Cylinder057
  Angle = 360
  AttacherType = Attacher::AttachEngine3D
  Height = 10
  Placement = pos=(0,0,36.15) rot=(0,0,1;0rad)
  Radius = 4
FEATURE [Part::Box] Box034  label="removeToCreteHoleForPlugHousing047"
  AttacherType = Attacher::AttachEngine3D
  Height = 28.6
  Length = 20
  Placement = pos=(106.15,0,21.7) rot=(0,0,1;0rad)
  Width = 19
FEATURE [Part::Cylinder] Cylinder058
  Angle = 360
  AttacherType = Attacher::AttachEngine3D
  Height = 20
  Placement = pos=(0,0,36.15) rot=(0,0,1;0rad)
  Radius = 14.3
FEATURE [Part::Cylinder] Cylinder059
  Angle = 360
  AttacherType = Attacher::AttachEngine3D
  Height = 10
  Placement = pos=(0,0,36.15) rot=(0,0,1;0rad)
  Radius = 4
FEATURE [Part::MultiFuse] Fusion134  label="removeToCreteHoleForPlugHousing046"
  Placement = pos=(70,19,36) rot=(0,1,0;1.5708rad)
  Shapes = -> [Cylinder058,Cylinder059]
FEATURE [Part::Cylinder] Cylinder060
  Angle = 360
  AttacherType = Attacher::AttachEngine3D
  Height = 20
  Placement = pos=(0,0,36.15) rot=(0,0,1;0rad)
  Radius = 14
FEATURE [Part::Cylinder] Cylinder061
  Angle = 360
  AttacherType = Attacher::AttachEngine3D
  Height = 10
  Placement = pos=(0,0,36.15) rot=(0,0,1;0rad)
  Radius = 4
FEATURE [Part::MultiFuse] Fusion135  label="removeToCreteHoleForPlugHousing048"
  Placement = pos=(70,19,36) rot=(0,1,0;1.5708rad)
  Shapes = -> [Cylinder060,Cylinder061]
FEATURE [Part::Box] Box035  label="removeToCreteHoleForPlugHousing049"
  AttacherType = Attacher::AttachEngine3D
  Height = 28.6
  Length = 20
  Placement = pos=(106.15,0,21.7) rot=(0,0,1;0rad)
  Width = 19
FEATURE [Part::MultiFuse] Fusion133  label="removeToCreteHoleForPlugHousing045"
  Placement = pos=(0,0,-28.3) rot=(0,0,1;0rad)
  Shapes = -> [Box035,Fusion134]
FEATURE [Part::MultiFuse] Fusion138  label="removeToCreteHoleForPlugHousing051"
  Placement = pos=(70,19,36) rot=(0,1,0;1.5708rad)
  Shapes = -> [Cylinder056,Cylinder057]
FEATURE [Part::MultiFuse] Fusion137  label="removeToCreteHoleForPlugHousing050"
  Placement = pos=(0,0,28.3) rot=(0,0,1;0rad)
  Shapes = -> [Box034,Fusion138]
FEATURE [Part::MultiFuse] Fusion132  label="removeToCreatePlugHousingBottomBit002"
  Shapes = -> [Fusion133,Fusion137]
FEATURE [Part::MultiFuse] Fusion136  label="removeToCreatePlugHousingBottomBit003"
  Shapes = -> [Fusion135,Fusion132]
FEATURE [Part::Cut] Cut058  label="bottomPlugHousingBit002"
  Base = -> Extrude063
  Placement = pos=(-0.09,0,0) rot=(0,0,1;0rad)
  Tool = -> Fusion136
FEATURE [Sketcher::SketchObject] Sketch073  label="bottomSketch003"
  FullyConstrained = true
  sketch-geometry (45):
    g0: LineSegment StartX=6.29999 StartY=8 StartZ=0 EndX=3.29999 EndY=8 EndZ=0
    g1: LineSegment StartX=3.29999 StartY=8 StartZ=0 EndX=3.29999 EndY=-6.03275e-07 EndZ=0
    g2: ArcOfCircle CenterX=8.29999 CenterY=5 CenterZ=0 NormalX=0 NormalY=0 NormalZ=1 AngleXU=0 Radius=2 StartAngle=3.14159 EndAngle=4.71239
    g3: LineSegment StartX=6.29999 StartY=8 StartZ=0 EndX=6.29999 EndY=5 EndZ=0
    g4: ArcOfCircle CenterX=105 CenterY=19 CenterZ=0 NormalX=0 NormalY=0 NormalZ=1 AngleXU=0 Radius=12.7 StartAngle=4.71239 EndAngle=5.94289
    g5-g11: Circle x7 (B-spline internal-alignment scaffolding for g12; pole/knot coordinates omitted)
    g12: BSplineCurve PolesCount=7 KnotsCount=5 Degree=3 IsPeriodic=0
    g13-g17: GeomPoint x5 (B-spline internal-alignment scaffolding for g12; pole/knot coordinates omitted)
    g18: ArcOfCircle CenterX=105 CenterY=19 CenterZ=0 NormalX=0 NormalY=0 NormalZ=1 AngleXU=0 Radius=15.7 StartAngle=5.81226 EndAngle=6.28319
    g19: BSplineCurve PolesCount=5 KnotsCount=3 Degree=3 IsPeriodic=0
    g20: LineSegment StartX=8.29999 StartY=3 StartZ=0 EndX=101.7 EndY=3 EndZ=0
    g21: LineSegment StartX=3.29999 StartY=-6.03275e-07 StartZ=0 EndX=105 EndY=-6.03275e-07 EndZ=0
    g22: LineSegment StartX=120.974 StartY=8.71251 StartZ=0 EndX=122.332 EndY=7.83778 EndZ=0
    g23: LineSegment StartX=105 StartY=-6.03274e-07 StartZ=0 EndX=113 EndY=-6.03274e-07 EndZ=0
    g24: ArcOfCircle CenterX=105 CenterY=19 CenterZ=0 NormalX=0 NormalY=0 NormalZ=1 AngleXU=0 Radius=20.6155 StartAngle=5.11091 EndAngle=5.71103
    g25: ArcOfCircle CenterX=117.7 CenterY=19 CenterZ=0 NormalX=0 NormalY=0 NormalZ=1 AngleXU=0 Radius=3 StartAngle=1.2e-15 EndAngle=2.10468
    g26: Circle CenterX=116.345 CenterY=16.3232 CenterZ=0 NormalX=0 NormalY=0 NormalZ=1 AngleXU=0 Radius=1
    g27: Circle CenterX=117.24 CenterY=15.7584 CenterZ=0 NormalX=0 NormalY=0 NormalZ=1 AngleXU=0 Radius=1
    g28: Circle CenterX=116.972 CenterY=14.7612 CenterZ=0 NormalX=0 NormalY=0 NormalZ=1 AngleXU=0 Radius=1
    g29: BSplineCurve PolesCount=3 KnotsCount=2 Degree=2 IsPeriodic=0
    g30: GeomPoint X=116.345 Y=16.3232 Z=0
    g31: GeomPoint X=116.972 Y=14.7612 Z=0
    g32: Circle CenterX=115.828 CenterY=17.157 CenterZ=0 NormalX=0 NormalY=0 NormalZ=1 AngleXU=0 Radius=1
    g33: Circle CenterX=115.841 CenterY=16.639 CenterZ=0 NormalX=0 NormalY=0 NormalZ=1 AngleXU=0 Radius=1
    g34: Circle CenterX=116.345 CenterY=16.3232 CenterZ=0 NormalX=0 NormalY=0 NormalZ=1 AngleXU=0 Radius=1
    g35: BSplineCurve PolesCount=3 KnotsCount=2 Degree=2 IsPeriodic=0
    g36: GeomPoint X=115.828 Y=17.157 Z=0
    g37: GeomPoint X=116.345 Y=16.3232 Z=0
    g38: LineSegment StartX=115.828 StartY=17.157 StartZ=0 EndX=115.828 EndY=20.8307 EndZ=0
    g39: Circle CenterX=115.828 CenterY=20.8307 CenterZ=0 NormalX=0 NormalY=0 NormalZ=1 AngleXU=0 Radius=1
    g40: Circle CenterX=115.831 CenterY=21.3396 CenterZ=0 NormalX=0 NormalY=0 NormalZ=1 AngleXU=0 Radius=1
    g41: Circle CenterX=116.173 CenterY=21.5825 CenterZ=0 NormalX=0 NormalY=0 NormalZ=1 AngleXU=0 Radius=1
    g42: BSplineCurve PolesCount=3 KnotsCount=2 Degree=2 IsPeriodic=0
    g43: GeomPoint X=115.828 Y=20.8307 Z=0
    g44: GeomPoint X=116.173 Y=21.5825 Z=0
  constraints (70):
    c: Horizontal(g0)
    c: Distance(g0) = 3
    c: Coincident(g1,g0)
    c: Vertical(g1)
    c: Block(g2)
    c: Block(g0)
    c: Coincident(g3,g0)
    c: Coincident(g3,g2)
    c: Vertical(g3)
    c: Block(g1)
    c: Block(g4)
    c: Coincident(g19,g4)
    c: Block(g19)
    c: Equal(g5, g6-g11) x6
    c: InternalAlignment(g5-g11 -> g12) x7
    c: InternalAlignment(g13-g17 -> g12) x5
    c: Block(g12)
    c: Coincident(g18,g12)
    c: Block(g18)
    c: Coincident(g20,g2)
    c: Coincident(g20,g19)
    c: Horizontal(g20)
    c: Distance(g20) = 93.4
    c: Coincident(g21,g1)
    c: Horizontal(g21)
    c: Distance(g21) = 101.7
    c: Horizontal(g23)
    c: Distance(g23) = 8
    c: Coincident(g24,g23)
    c: Block(g23)
    c: Coincident(g22,g24)
    c: Block(g24)
    c: Block(g22)
    c: Distance(g22) = 1.61553
    c: Coincident(g25,g18)
    c: Block(g25)
    c: Weight(g26) = 1
    c: Equal(g26,g27)
    c: Equal(g26,g28)
    c: Coincident(g29,g4)
    c: InternalAlignment(g26,g29)
    c: InternalAlignment(g27,g29)
    c: InternalAlignment(g28,g29)
    c: InternalAlignment(g30,g29)
    c: InternalAlignment(g31,g29)
    c: Block(g29)
    c: Weight(g32) = 1
    c: Equal(g32,g33)
    c: Equal(g32,g34)
    c: Coincident(g35,g29)
    c: InternalAlignment(g32,g35)
    c: InternalAlignment(g33,g35)
    c: InternalAlignment(g34,g35)
    c: InternalAlignment(g36,g35)
    c: InternalAlignment(g37,g35)
    c: Block(g35)
    c: Coincident(g38,g35)
    c: Vertical(g38)
    c: Block(g38)
    c: Coincident(g42,g38)
    c: Weight(g39) = 1
    c: Equal(g39,g40)
    c: Equal(g39,g41)
    c: Coincident(g42,g25)
    c: InternalAlignment(g39,g42)
    c: InternalAlignment(g40,g42)
    c: InternalAlignment(g41,g42)
    c: InternalAlignment(g43,g42)
    c: InternalAlignment(g44,g42)
    c: Block(g42)
FEATURE [Part::Extrusion] Extrude064  label="bottom016"
  Base = -> Sketch073
  Dir = (0,0,1)
  DirMode = 2
  FaceMakerClass = Part::FaceMakerBullseye
  LengthFwd = 71.4
  LengthRev = 0
  Placement = pos=(0,0,0.3) rot=(0,0,1;0rad)
  Solid = true
  Symmetric = false
FEATURE [Part::Revolution] Revolve157  label="removeToCreateScrewAndThreadedInsertHole063"
  Angle = 360
  Axis = (0,1,0)
  Base = (0,0,0)
  FaceMakerClass = Part::FaceMakerBullseye
  Placement = pos=(12.5,0,10) rot=(0,0,1;0rad)
  Solid = false
  Source = -> Face141
  Symmetric = false
FEATURE [Sketcher::SketchObject] Sketch074
  FullyConstrained = true
  Placement = pos=(117,19,0) rot=(0.57735,0.57735,0.57735;2.0944rad)
  sketch-geometry (48):
    g0: LineSegment StartX=-49.19 StartY=69.25 StartZ=0 EndX=-49.19 EndY=66.25 EndZ=0
    g1: LineSegment StartX=-49.19 StartY=63.5 StartZ=0 EndX=-49.19 EndY=60.5 EndZ=0
    g2: LineSegment StartX=-49.19 StartY=57.75 StartZ=0 EndX=-49.19 EndY=54.75 EndZ=0
    g3: LineSegment StartX=-49.19 StartY=52 StartZ=0 EndX=-49.19 EndY=49 EndZ=0
    g4: LineSegment StartX=-49.19 StartY=46.25 StartZ=0 EndX=-49.19 EndY=43.25 EndZ=0
    g5: LineSegment StartX=-49.19 StartY=40.5 StartZ=0 EndX=-49.19 EndY=37.5 EndZ=0
    g6: LineSegment StartX=-49.19 StartY=34.5 StartZ=0 EndX=-49.19 EndY=31.5 EndZ=0
    g7: LineSegment StartX=-49.19 StartY=28.75 StartZ=0 EndX=-49.19 EndY=25.75 EndZ=0
    g8: LineSegment StartX=-49.19 StartY=23 StartZ=0 EndX=-49.19 EndY=20 EndZ=0
    g9: LineSegment StartX=-49.19 StartY=17.25 StartZ=0 EndX=-49.19 EndY=14.25 EndZ=0
    g10: LineSegment StartX=-49.19 StartY=11.5 StartZ=0 EndX=-49.19 EndY=8.5 EndZ=0
    g11: LineSegment StartX=-49.19 StartY=5.75 StartZ=0 EndX=-49.19 EndY=2.75 EndZ=0
    g12: ArcOfCircle CenterX=-1.5 CenterY=67.75 CenterZ=0 NormalX=0 NormalY=0 NormalZ=1 AngleXU=0 Radius=1.5 StartAngle=4.71239 EndAngle=7.85398
    g13: ArcOfCircle CenterX=-1.5 CenterY=62 CenterZ=0 NormalX=0 NormalY=0 NormalZ=1 AngleXU=0 Radius=1.5 StartAngle=4.71239 EndAngle=7.85398
    g14: ArcOfCircle CenterX=-1.5 CenterY=56.25 CenterZ=0 NormalX=0 NormalY=0 NormalZ=1 AngleXU=0 Radius=1.5 StartAngle=4.71239 EndAngle=7.85398
    g15: ArcOfCircle CenterX=-11.49 CenterY=50.5 CenterZ=0 NormalX=0 NormalY=0 NormalZ=1 AngleXU=0 Radius=1.5 StartAngle=4.71239 EndAngle=7.85398
    g16: ArcOfCircle CenterX=-16.28 CenterY=44.75 CenterZ=0 NormalX=0 NormalY=0 NormalZ=1 AngleXU=0 Radius=1.5 StartAngle=4.71239 EndAngle=7.85398
    g17: ArcOfCircle CenterX=-18.2337 CenterY=39 CenterZ=0 NormalX=0 NormalY=0 NormalZ=1 AngleXU=0 Radius=1.5 StartAngle=4.71485 EndAngle=7.85398
    g18: ArcOfCircle CenterX=-16.2837 CenterY=27.25 CenterZ=0 NormalX=0 NormalY=0 NormalZ=1 AngleXU=0 Radius=1.5 StartAngle=4.71485 EndAngle=7.85398
    g19: ArcOfCircle CenterX=-18.2337 CenterY=33 CenterZ=0 NormalX=0 NormalY=0 NormalZ=1 AngleXU=0 Radius=1.5 StartAngle=4.71485 EndAngle=7.85398
    g20: ArcOfCircle CenterX=-11.49 CenterY=21.5 CenterZ=0 NormalX=0 NormalY=0 NormalZ=1 AngleXU=0 Radius=1.5 StartAngle=4.71239 EndAngle=7.85398
    g21: ArcOfCircle CenterX=-1.5 CenterY=4.25 CenterZ=0 NormalX=0 NormalY=0 NormalZ=1 AngleXU=0 Radius=1.5 StartAngle=4.71239 EndAngle=7.85398
    g22: ArcOfCircle CenterX=-1.5 CenterY=10 CenterZ=0 NormalX=0 NormalY=0 NormalZ=1 AngleXU=0 Radius=1.5 StartAngle=4.71239 EndAngle=7.85398
    g23: ArcOfCircle CenterX=-1.5 CenterY=15.75 CenterZ=0 NormalX=0 NormalY=0 NormalZ=1 AngleXU=0 Radius=1.5 StartAngle=4.71239 EndAngle=7.85398
    g24: LineSegment StartX=-49.19 StartY=69.25 StartZ=0 EndX=-1.5 EndY=69.25 EndZ=0
    g25: LineSegment StartX=-49.19 StartY=66.25 StartZ=0 EndX=-1.5 EndY=66.25 EndZ=0
    g26: LineSegment StartX=-49.19 StartY=63.5 StartZ=0 EndX=-1.5 EndY=63.5 EndZ=0
    g27: LineSegment StartX=-49.19 StartY=60.5 StartZ=0 EndX=-1.5 EndY=60.5 EndZ=0
    g28: LineSegment StartX=-49.19 StartY=57.75 StartZ=0 EndX=-1.5 EndY=57.75 EndZ=0
    g29: LineSegment StartX=-49.19 StartY=54.75 StartZ=0 EndX=-1.5 EndY=54.75 EndZ=0
    g30: LineSegment StartX=-49.19 StartY=52 StartZ=0 EndX=-11.49 EndY=52 EndZ=0
    g31: LineSegment StartX=-49.19 StartY=49 StartZ=0 EndX=-11.49 EndY=49 EndZ=0
    g32: LineSegment StartX=-49.19 StartY=46.25 StartZ=0 EndX=-16.28 EndY=46.25 EndZ=0
    g33: LineSegment StartX=-49.19 StartY=43.25 StartZ=0 EndX=-16.28 EndY=43.25 EndZ=0
    g34: LineSegment StartX=-49.19 StartY=40.5 StartZ=0 EndX=-18.2337 EndY=40.5 EndZ=0
    g35: LineSegment StartX=-49.19 StartY=37.5 StartZ=0 EndX=-18.23 EndY=37.5 EndZ=0
    g36: LineSegment StartX=-49.19 StartY=34.5 StartZ=0 EndX=-18.2337 EndY=34.5 EndZ=0
    g37: LineSegment StartX=-49.19 StartY=31.5 StartZ=0 EndX=-18.23 EndY=31.5 EndZ=0
    g38: LineSegment StartX=-49.19 StartY=28.75 StartZ=0 EndX=-16.2837 EndY=28.75 EndZ=0
    g39: LineSegment StartX=-49.19 StartY=25.75 StartZ=0 EndX=-16.28 EndY=25.75 EndZ=0
    g40: LineSegment StartX=-49.19 StartY=23 StartZ=0 EndX=-11.49 EndY=23 EndZ=0
    g41: LineSegment StartX=-49.19 StartY=20 StartZ=0 EndX=-11.49 EndY=20 EndZ=0
    g42: LineSegment StartX=-49.19 StartY=17.25 StartZ=0 EndX=-1.5 EndY=17.25 EndZ=0
    g43: LineSegment StartX=-49.19 StartY=14.25 StartZ=0 EndX=-1.5 EndY=14.25 EndZ=0
    g44: LineSegment StartX=-49.19 StartY=11.5 StartZ=0 EndX=-1.5 EndY=11.5 EndZ=0
    g45: LineSegment StartX=-49.19 StartY=8.5 StartZ=0 EndX=-1.5 EndY=8.5 EndZ=0
    g46: LineSegment StartX=-49.19 StartY=5.75 StartZ=0 EndX=-1.5 EndY=5.75 EndZ=0
    g47: LineSegment StartX=-49.19 StartY=2.75 StartZ=0 EndX=-1.5 EndY=2.75 EndZ=0
  constraints (120):
    c: Vertical(g0)
    c: Distance(g0) = 3
    c: Block(g0)
    c: Vertical(g1)
    c: Distance(g1) = 3
    c: Vertical(g2)
    c: Equal(g0,g2) = 3
    c: Block(g2)
    c: Vertical(g3)
    c: Equal(g1,g3) = 3
    c: Vertical(g4)
    c: Equal(g0,g4) = 3
    c: Block(g4)
    c: Vertical(g5)
    c: Equal(g1,g5) = 3
    c: Vertical(g6)
    c: Equal(g0,g6) = 3
    c: Block(g6)
    c: Vertical(g7)
    c: Equal(g1,g7) = 3
    c: Vertical(g8)
    c: Equal(g0,g8) = 3
    c: Block(g8)
    c: Vertical(g9)
    c: Equal(g1,g9) = 3
    c: Vertical(g10)
    c: Equal(g0,g10) = 3
    c: Block(g10)
    c: Vertical(g11)
    c: Equal(g1,g11) = 3
    c: Block(g12)
    c: Block(g13)
    c: Block(g14)
    c: Block(g15)
    c: Block(g16)
    c: Block(g17)
    c: Block(g18)
    c: Block(g19)
    c: Block(g20)
    c: Block(g21)
    c: Block(g22)
    c: Block(g23)
    c: Block(g11)
    c: Block(g9)
    c: Block(g7)
    c: Block(g5)
    c: Block(g3)
    c: Block(g1)
    c: Coincident(g24,g0)
    c: Coincident(g24,g12)
    c: Horizontal(g24)
    c: Coincident(g25,g0)
    c: Coincident(g25,g12)
    c: Horizontal(g25)
    c: Coincident(g26,g1)
    c: Coincident(g26,g13)
    c: Horizontal(g26)
    c: Coincident(g27,g1)
    c: Coincident(g27,g13)
    c: Horizontal(g27)
    c: Coincident(g28,g2)
    c: Coincident(g28,g14)
    c: Horizontal(g28)
    c: Coincident(g29,g2)
    c: Coincident(g29,g14)
    c: Horizontal(g29)
    c: Coincident(g30,g3)
    c: Coincident(g30,g15)
    c: Horizontal(g30)
    c: Coincident(g31,g3)
    c: Coincident(g31,g15)
    c: Horizontal(g31)
    c: Coincident(g32,g4)
    c: Coincident(g32,g16)
    c: Horizontal(g32)
    c: Coincident(g33,g4)
    c: Coincident(g33,g16)
    c: Horizontal(g33)
    c: Coincident(g34,g5)
    c: Coincident(g34,g17)
    c: Horizontal(g34)
    c: Coincident(g35,g5)
    c: Coincident(g35,g17)
    c: Horizontal(g35)
    c: Coincident(g36,g6)
    c: Coincident(g36,g19)
    c: Horizontal(g36)
    c: Coincident(g37,g6)
    c: Coincident(g37,g19)
    c: Horizontal(g37)
    c: Coincident(g38,g7)
    c: Coincident(g38,g18)
    c: Horizontal(g38)
    c: Coincident(g39,g7)
    c: Coincident(g39,g18)
    c: Horizontal(g39)
    c: Coincident(g40,g8)
    c: Coincident(g40,g20)
    c: Horizontal(g40)
    c: Coincident(g41,g8)
    c: Coincident(g41,g20)
    c: Horizontal(g41)
    c: Coincident(g42,g9)
    c: Coincident(g42,g23)
    c: Horizontal(g42)
    c: Coincident(g43,g9)
    c: Coincident(g43,g23)
    c: Horizontal(g43)
    c: Coincident(g44,g10)
    c: Coincident(g44,g22)
    c: Horizontal(g44)
    c: Coincident(g45,g10)
    c: Coincident(g45,g22)
    c: Horizontal(g45)
    c: Coincident(g46,g11)
    c: Coincident(g46,g21)
    c: Horizontal(g46)
    c: Coincident(g47,g11)
    c: Coincident(g47,g21)
    c: Horizontal(g47)
FEATURE [Part::Extrusion] Extrude065
  Base = -> Sketch074
  Dir = (1,0,0)
  DirMode = 2
  FaceMakerClass = Part::FaceMakerBullseye
  LengthFwd = 23
  LengthRev = 0
  Placement = pos=(-19,0,0) rot=(0,0,1;0rad)
  Solid = true
  Symmetric = false
FEATURE [Part::Fillet] Fillet056  label="removeToCreateVentalationHoles003"
  Base = -> Extrude065
  Edges = <same value as first occurrence — deduplicated (x6 in doc)>
  Placement = pos=(7,0.02,0) rot=(0,0,1;0rad)
FEATURE [Part::Revolution] Revolve158  label="removeToCreateScrewAndThreadedInsertHole065"
  Angle = 360
  Axis = (0,1,0)
  Base = (0,0,0)
  FaceMakerClass = Part::FaceMakerBullseye
  Placement = pos=(12.5,0,62) rot=(0,0,1;0rad)
  Solid = false
  Source = -> Face146
  Symmetric = false
FEATURE [Part::Revolution] Revolve159  label="removeToCreateScrewAndThreadedInsertHole066"
  Angle = 360
  Axis = (0,1,0)
  Base = (0,0,0)
  FaceMakerClass = Part::FaceMakerBullseye
  Placement = pos=(89.5,0,68.5) rot=(0,0,1;0rad)
  Solid = false
  Source = -> Face143
  Symmetric = false
FEATURE [Part::Revolution] Revolve160  label="removeToCreateScrewAndThreadedInsertHole067"
  Angle = 360
  Axis = (0,1,0)
  Base = (0,0,0)
  FaceMakerClass = Part::FaceMakerBullseye
  Placement = pos=(89.5,0,3.5) rot=(0,0,1;0rad)
  Solid = false
  Source = -> Face142
  Symmetric = false
FEATURE [Part::Revolution] Revolve161  label="removeToCreateScrewAndThreadedInsertHole068"
  Angle = 360
  Axis = (0,1,0)
  Base = (0,0,0)
  FaceMakerClass = Part::FaceMakerBullseye
  Placement = pos=(109.5,4.7,3.5) rot=(0,0,1;0rad)
  Solid = false
  Source = -> Face145
  Symmetric = false
FEATURE [Part::Revolution] Revolve162  label="removeToCreateScrewAndThreadedInsertHole069"
  Angle = 360
  Axis = (0,1,0)
  Base = (0,0,0)
  FaceMakerClass = Part::FaceMakerBullseye
  Placement = pos=(109.5,4.7,68.5) rot=(0,0,1;0rad)
  Solid = false
  Source = -> Face144
  Symmetric = false
FEATURE [Part::MultiFuse] Fusion141  label="removeToCreateScrewAndThreadedInsertHole064"
  Shapes = -> [Revolve162,Revolve161,Revolve160,Revolve159,Revolve158,Revolve157]
FEATURE [Part::Cylinder] Cylinder062
  Angle = 360
  AttacherType = Attacher::AttachEngine3D
  Height = 20
  Placement = pos=(0,0,36.15) rot=(0,0,1;0rad)
  Radius = 14
FEATURE [Part::Cylinder] Cylinder063
  Angle = 360
  AttacherType = Attacher::AttachEngine3D
  Height = 10
  Placement = pos=(0,0,36.15) rot=(0,0,1;0rad)
  Radius = 4
FEATURE [Part::MultiFuse] Fusion139  label="removeToCreteHoleForPlugHousing052"
  Placement = pos=(70,19,36) rot=(0,1,0;1.5708rad)
  Shapes = -> [Cylinder062,Cylinder063]
FEATURE [Part::Cut] Cut060  label="bottom017"
  Base = -> Extrude064
  Tool = -> Fusion139
FEATURE [Part::Cut] Cut061  label="bottom019"
  Base = -> Cut060
  Tool = -> Fusion141
FEATURE [Part::MultiFuse] Fusion140  label="bottom018"
  Shapes = -> [Cut061,Cut058]
FEATURE [Part::Cut] Cut059  label="bottom020"
  Base = -> Fusion140
  Tool = -> Fillet056
FEATURE [Part::Box] Box036  label="Cube021"
  AttacherType = Attacher::AttachEngine3D
  Height = 80
  Length = 26
  Placement = pos=(0,-1,-5) rot=(0,0,1;0rad)
  Width = 11
FEATURE [Part::Cut] Cut062  label="removeFromBottom002"
  Base = -> Cut057
  Tool = -> Box036
FEATURE [Part::Cut] Cut063
  Base = -> Cut059
  Tool = -> Cut062
FEATURE [Part::Cut] Cut064  label="pcbStands"
  Base = -> Fusion095
  Tool = -> Fusion127
FEATURE [Sketcher::SketchObject] Sketch075  label="topSketch022"
  FullyConstrained = true
  sketch-geometry (6):
    g0: LineSegment StartX=19 StartY=38 StartZ=0 EndX=117 EndY=38 EndZ=0
    g1: ArcOfCircle CenterX=19 CenterY=19 CenterZ=0 NormalX=0 NormalY=0 NormalZ=1 AngleXU=0 Radius=19 StartAngle=1.5708 EndAngle=3.14159
    g2: LineSegment StartX=117 StartY=38 StartZ=0 EndX=117 EndY=19 EndZ=0
    g3: LineSegment StartX=98 StartY=1.0161e-12 StartZ=0 EndX=5.22862e-06 EndY=1.0161e-12 EndZ=0
    g4: LineSegment StartX=5.22862e-06 StartY=19 StartZ=0 EndX=5.22862e-06 EndY=1.0161e-12 EndZ=0
    g5: ArcOfCircle CenterX=98 CenterY=19 CenterZ=0 NormalX=0 NormalY=0 NormalZ=1 AngleXU=0 Radius=19 StartAngle=4.71239 EndAngle=6.28319
  constraints (16):
    c: Horizontal(g0)
    c: Distance(g0) = 98
    c: Coincident(g1,g0)
    c: Block(g1)
    c: Coincident(g2,g0)
    c: Vertical(g2)
    c: Distance(g2) = 19
    c: Horizontal(g3)
    c: Coincident(g4,g1)
    c: Vertical(g4)
    c: Coincident(g3,g4)
    c: Block(g3)
    c: Coincident(g5,g2)
    c: Coincident(g5,g3)
    c: Block(g0)
    c: Block(g5)
FEATURE [Part::Extrusion] Extrude067  label="sideB003"
  Base = -> Sketch075
  Dir = (0,0,1)
  DirMode = 2
  FaceMakerClass = Part::FaceMakerBullseye
  LengthFwd = 3
  LengthRev = 0
  Placement = pos=(0,0,71.7) rot=(0,0,1;0rad)
  Solid = true
  Symmetric = false
FEATURE [Sketcher::SketchObject] Sketch076  label="topSketch023"
  FullyConstrained = true
  sketch-geometry (6):
    g0: LineSegment StartX=19 StartY=38 StartZ=0 EndX=117 EndY=38 EndZ=0
    g1: ArcOfCircle CenterX=19 CenterY=19 CenterZ=0 NormalX=0 NormalY=0 NormalZ=1 AngleXU=0 Radius=19 StartAngle=1.5708 EndAngle=3.14159
    g2: LineSegment StartX=117 StartY=38 StartZ=0 EndX=117 EndY=19 EndZ=0
    g3: LineSegment StartX=98 StartY=1.0161e-12 StartZ=0 EndX=5.22862e-06 EndY=1.0161e-12 EndZ=0
    g4: LineSegment StartX=5.22862e-06 StartY=19 StartZ=0 EndX=5.22862e-06 EndY=1.0161e-12 EndZ=0
    g5: ArcOfCircle CenterX=98 CenterY=19 CenterZ=0 NormalX=0 NormalY=0 NormalZ=1 AngleXU=0 Radius=19 StartAngle=4.71239 EndAngle=6.28319
  constraints (16):
    c: Horizontal(g0)
    c: Distance(g0) = 98
    c: Coincident(g1,g0)
    c: Block(g1)
    c: Coincident(g2,g0)
    c: Vertical(g2)
    c: Distance(g2) = 19
    c: Horizontal(g3)
    c: Coincident(g4,g1)
    c: Vertical(g4)
    c: Coincident(g3,g4)
    c: Block(g3)
    c: Coincident(g5,g2)
    c: Coincident(g5,g3)
    c: Block(g0)
    c: Block(g5)
FEATURE [Part::Extrusion] Extrude066  label="sideA003"
  Base = -> Sketch076
  Dir = (0,0,1)
  DirMode = 2
  FaceMakerClass = Part::FaceMakerBullseye
  LengthFwd = 3
  LengthRev = 0
  Placement = pos=(0,0,-2.7) rot=(0,0,1;0rad)
  Solid = true
  Symmetric = false
FEATURE [Part::MultiFuse] Fusion142  label="removeFromBottom003"
  Placement = pos=(2,0,0) rot=(0,0,1;0rad)
  Shapes = -> [Extrude066,Extrude067]
FEATURE [Part::Cut] Cut065  label="screwRetainers002"
  Base = -> Fusion096
  Tool = -> Fusion142
FEATURE [Sketcher::SketchObject] Sketch077
  FullyConstrained = true
  Placement = pos=(117,19,0) rot=(0.57735,0.57735,0.57735;2.0944rad)
  sketch-geometry (8):
    g0: LineSegment StartX=-49.19 StartY=63.5 StartZ=0 EndX=-49.19 EndY=60.5 EndZ=0
    g1: LineSegment StartX=-49.19 StartY=11.5 StartZ=0 EndX=-49.19 EndY=8.5 EndZ=0
    g2: ArcOfCircle CenterX=-1.5 CenterY=62 CenterZ=0 NormalX=0 NormalY=0 NormalZ=1 AngleXU=0 Radius=1.5 StartAngle=4.71239 EndAngle=7.85398
    g3: ArcOfCircle CenterX=-1.5 CenterY=10 CenterZ=0 NormalX=0 NormalY=0 NormalZ=1 AngleXU=0 Radius=1.5 StartAngle=4.71239 EndAngle=7.85398
    g4: LineSegment StartX=-49.19 StartY=63.5 StartZ=0 EndX=-1.5 EndY=63.5 EndZ=0
    g5: LineSegment StartX=-49.19 StartY=60.5 StartZ=0 EndX=-1.5 EndY=60.5 EndZ=0
    g6: LineSegment StartX=-49.19 StartY=11.5 StartZ=0 EndX=-1.5 EndY=11.5 EndZ=0
    g7: LineSegment StartX=-49.19 StartY=8.5 StartZ=0 EndX=-1.5 EndY=8.5 EndZ=0
  constraints (19):
    c: Vertical(g0)
    c: Distance(g0) = 3
    c: Vertical(g1)
    c: Block(g1)
    c: Block(g2)
    c: Block(g3)
    c: Block(g0)
    c: Coincident(g4,g0)
    c: Coincident(g4,g2)
    c: Horizontal(g4)
    c: Coincident(g5,g0)
    c: Coincident(g5,g2)
    c: Horizontal(g5)
    c: Coincident(g6,g1)
    c: Coincident(g6,g3)
    c: Horizontal(g6)
    c: Coincident(g7,g1)
    c: Coincident(g7,g3)
    c: Horizontal(g7)
FEATURE [Part::Extrusion] Extrude068
  Base = -> Sketch077
  Dir = (1,0,0)
  DirMode = 2
  FaceMakerClass = Part::FaceMakerBullseye
  LengthFwd = 10
  LengthRev = 0
  Solid = true
  Symmetric = false
FEATURE [Part::Fillet] Fillet057  label="removeFromtMoreFrontCaseScrewRetainers002"
  Base = -> Extrude068
  Edges = 4 edges r=1.49: [Edge6,Edge11,Edge18,Edge23]
  Placement = pos=(-12,0,0) rot=(0,0,1;0rad)
FEATURE [Sketcher::SketchObject] Sketch078
  FullyConstrained = true
  Placement = pos=(117,19,0) rot=(0.57735,0.57735,0.57735;2.0944rad)
  sketch-geometry (8):
    g0: LineSegment StartX=-49.19 StartY=69.25 StartZ=0 EndX=-49.19 EndY=66.25 EndZ=0
    g1: LineSegment StartX=-49.19 StartY=5.75 StartZ=0 EndX=-49.19 EndY=2.75 EndZ=0
    g2: ArcOfCircle CenterX=-1.5 CenterY=67.75 CenterZ=0 NormalX=0 NormalY=0 NormalZ=1 AngleXU=0 Radius=1.5 StartAngle=4.71239 EndAngle=7.85398
    g3: ArcOfCircle CenterX=-1.5 CenterY=4.25 CenterZ=0 NormalX=0 NormalY=0 NormalZ=1 AngleXU=0 Radius=1.5 StartAngle=4.71239 EndAngle=7.85398
    g4: LineSegment StartX=-49.19 StartY=69.25 StartZ=0 EndX=-1.5 EndY=69.25 EndZ=0
    g5: LineSegment StartX=-49.19 StartY=66.25 StartZ=0 EndX=-1.5 EndY=66.25 EndZ=0
    g6: LineSegment StartX=-49.19 StartY=5.75 StartZ=0 EndX=-1.5 EndY=5.75 EndZ=0
    g7: LineSegment StartX=-49.19 StartY=2.75 StartZ=0 EndX=-1.5 EndY=2.75 EndZ=0
  constraints (19):
    c: Vertical(g0)
    c: Distance(g0) = 3
    c: Block(g0)
    c: Vertical(g1)
    c: Block(g2)
    c: Block(g3)
    c: Block(g1)
    c: Coincident(g4,g0)
    c: Coincident(g4,g2)
    c: Horizontal(g4)
    c: Coincident(g5,g0)
    c: Coincident(g5,g2)
    c: Horizontal(g5)
    c: Coincident(g6,g1)
    c: Coincident(g6,g3)
    c: Horizontal(g6)
    c: Coincident(g7,g1)
    c: Coincident(g7,g3)
    c: Horizontal(g7)
FEATURE [Part::Extrusion] Extrude069
  Base = -> Sketch078
  Dir = (1,0,0)
  DirMode = 2
  FaceMakerClass = Part::FaceMakerBullseye
  LengthFwd = 10
  LengthRev = 0
  Solid = true
  Symmetric = false
FEATURE [Part::Fillet] Fillet058  label="removeFromtMoreFrontCaseScrewRetainers003"
  Base = -> Extrude069
  Edges = 4 edges r=1.49: [Edge6,Edge11,Edge18,Edge23]
  Placement = pos=(-4,0,0) rot=(0,0,1;0rad)
FEATURE [Part::Cut] Cut066
  Base = -> Cut065
  Tool = -> Fillet058
FEATURE [Part::Cut] Cut067  label="screwPillars"
  Base = -> Cut066
  Tool = -> Fillet057
FEATURE [Part::MultiFuse] Fusion143  label="bottom021"
  Shapes = -> [Cut031,Cut063]
FEATURE [Part::Cylinder] Cylinder
  Angle = 360
  AttacherType = Attacher::AttachEngine3D
  Height = 10
  Placement = pos=(20.65,12,4.68) rot=(1,0,0;1.5708rad)
  Radius = 2
FEATURE [Part::Cylinder] Cylinder064
  Angle = 360
  AttacherType = Attacher::AttachEngine3D
  Height = 10
  Placement = pos=(20.65,12,67.38) rot=(1,0,0;1.5708rad)
  Radius = 2
FEATURE [Part::Cylinder] Cylinder065
  Angle = 360
  AttacherType = Attacher::AttachEngine3D
  Height = 10
  Placement = pos=(77.15,12,67.38) rot=(1,0,0;1.5708rad)
  Radius = 2
FEATURE [Part::Cylinder] Cylinder066
  Angle = 360
  AttacherType = Attacher::AttachEngine3D
  Height = 10
  Placement = pos=(77.15,12,4.68) rot=(1,0,0;1.5708rad)
  Radius = 2
FEATURE [Part::MultiFuse] Fusion144  label="removeFromThreadedInsertHousing"
  Shapes = -> [Cylinder065,Cylinder064,Cylinder,Cylinder066]
FEATURE [Part::Cut] Cut068  label="pcbStands001"
  Base = -> Cut064
  Tool = -> Fusion144
FEATURE [Part::MultiFuse] Fusion145
  Shapes = -> [Cut068,Fusion143]
FEATURE [Part::MultiFuse] Fusion146
  Shapes = -> [Fusion145]
FEATURE [Part::MultiFuse] Fusion147  label="bottom022"
  Shapes = -> [Cut067,Fusion146]
FEATURE [Part::MultiFuse] Fusion148  label="casePillars005"
  Shapes = -> [Cut047,Fusion092]
FEATURE [Part::MultiFuse] Fusion149  label="bottom023"
  Shapes = -> [Fusion124,Fusion113,Fusion147]
FEATURE [Part::MultiFuse] Fusion150  label="topBits"
  Shapes = -> [Cut025,Fusion148,Cut030,Fillet034]
FEATURE [Part::Feature] Face149 .. Face152  x4 (patterned run collapsed; names and placements below)
  shape: bbox 3.2 x 1.5 x 2e-07 mm, 1 faces, 0 solids (baked)
FEATURE [Part::Feature] Face153
  shape: bbox 3.6 x 3.2 x 2e-07 mm, 1 faces, 0 solids (baked)
FEATURE [Part::Feature] Face154
  shape: bbox 3.6 x 3.2 x 2e-07 mm, 1 faces, 0 solids (baked)
FEATURE [Sketcher::SketchObject] Sketch079  label="topSketch024"
  FullyConstrained = true
  sketch-geometry (6):
    g0: LineSegment StartX=19 StartY=38 StartZ=0 EndX=117 EndY=38 EndZ=0
    g1: ArcOfCircle CenterX=19 CenterY=19 CenterZ=0 NormalX=0 NormalY=0 NormalZ=1 AngleXU=0 Radius=19 StartAngle=1.5708 EndAngle=3.14159
    g2: LineSegment StartX=117 StartY=38 StartZ=0 EndX=117 EndY=19 EndZ=0
    g3: LineSegment StartX=98 StartY=1.0161e-12 StartZ=0 EndX=5.22862e-06 EndY=1.0161e-12 EndZ=0
    g4: LineSegment StartX=5.22862e-06 StartY=19 StartZ=0 EndX=5.22862e-06 EndY=1.0161e-12 EndZ=0
    g5: ArcOfCircle CenterX=98 CenterY=19 CenterZ=0 NormalX=0 NormalY=0 NormalZ=1 AngleXU=0 Radius=19 StartAngle=4.71239 EndAngle=6.28319
  constraints (16):
    c: Horizontal(g0)
    c: Distance(g0) = 98
    c: Coincident(g1,g0)
    c: Block(g1)
    c: Coincident(g2,g0)
    c: Vertical(g2)
    c: Distance(g2) = 19
    c: Horizontal(g3)
    c: Coincident(g4,g1)
    c: Vertical(g4)
    c: Coincident(g3,g4)
    c: Block(g3)
    c: Coincident(g5,g2)
    c: Coincident(g5,g3)
    c: Block(g0)
    c: Block(g5)
FEATURE [Sketcher::SketchObject] Sketch080  label="topSketch025"
  FullyConstrained = true
  sketch-geometry (6):
    g0: LineSegment StartX=19 StartY=38 StartZ=0 EndX=117 EndY=38 EndZ=0
    g1: ArcOfCircle CenterX=19 CenterY=19 CenterZ=0 NormalX=0 NormalY=0 NormalZ=1 AngleXU=0 Radius=19 StartAngle=1.5708 EndAngle=3.14159
    g2: LineSegment StartX=117 StartY=38 StartZ=0 EndX=117 EndY=19 EndZ=0
    g3: LineSegment StartX=98 StartY=1.0161e-12 StartZ=0 EndX=5.22862e-06 EndY=1.0161e-12 EndZ=0
    g4: LineSegment StartX=5.22862e-06 StartY=19 StartZ=0 EndX=5.22862e-06 EndY=1.0161e-12 EndZ=0
    g5: ArcOfCircle CenterX=98 CenterY=19 CenterZ=0 NormalX=0 NormalY=0 NormalZ=1 AngleXU=0 Radius=19 StartAngle=4.71239 EndAngle=6.28319
  constraints (16):
    c: Horizontal(g0)
    c: Distance(g0) = 98
    c: Coincident(g1,g0)
    c: Block(g1)
    c: Coincident(g2,g0)
    c: Vertical(g2)
    c: Distance(g2) = 19
    c: Horizontal(g3)
    c: Coincident(g4,g1)
    c: Vertical(g4)
    c: Coincident(g3,g4)
    c: Block(g3)
    c: Coincident(g5,g2)
    c: Coincident(g5,g3)
    c: Block(g0)
    c: Block(g5)
FEATURE [Part::Extrusion] Extrude070  label="sideA004"
  Base = -> Sketch080
  Dir = (0,0,1)
  DirMode = 2
  FaceMakerClass = Part::FaceMakerBullseye
  LengthFwd = 3
  LengthRev = 0
  Placement = pos=(0,0,-2.7) rot=(0,0,1;0rad)
  Solid = true
  Symmetric = false
FEATURE [Sketcher::SketchObject] Sketch081
  FullyConstrained = true
  Placement = pos=(117,19,0) rot=(0.57735,0.57735,0.57735;2.0944rad)
  sketch-geometry (8):
    g0: LineSegment StartX=-49.19 StartY=63.5 StartZ=0 EndX=-49.19 EndY=60.5 EndZ=0
    g1: LineSegment StartX=-49.19 StartY=11.5 StartZ=0 EndX=-49.19 EndY=8.5 EndZ=0
    g2: ArcOfCircle CenterX=-1.5 CenterY=62 CenterZ=0 NormalX=0 NormalY=0 NormalZ=1 AngleXU=0 Radius=1.5 StartAngle=4.71239 EndAngle=7.85398
    g3: ArcOfCircle CenterX=-1.5 CenterY=10 CenterZ=0 NormalX=0 NormalY=0 NormalZ=1 AngleXU=0 Radius=1.5 StartAngle=4.71239 EndAngle=7.85398
    g4: LineSegment StartX=-49.19 StartY=63.5 StartZ=0 EndX=-1.5 EndY=63.5 EndZ=0
    g5: LineSegment StartX=-49.19 StartY=60.5 StartZ=0 EndX=-1.5 EndY=60.5 EndZ=0
    g6: LineSegment StartX=-49.19 StartY=11.5 StartZ=0 EndX=-1.5 EndY=11.5 EndZ=0
    g7: LineSegment StartX=-49.19 StartY=8.5 StartZ=0 EndX=-1.5 EndY=8.5 EndZ=0
  constraints (19):
    c: Vertical(g0)
    c: Distance(g0) = 3
    c: Vertical(g1)
    c: Block(g1)
    c: Block(g2)
    c: Block(g3)
    c: Block(g0)
    c: Coincident(g4,g0)
    c: Coincident(g4,g2)
    c: Horizontal(g4)
    c: Coincident(g5,g0)
    c: Coincident(g5,g2)
    c: Horizontal(g5)
    c: Coincident(g6,g1)
    c: Coincident(g6,g3)
    c: Horizontal(g6)
    c: Coincident(g7,g1)
    c: Coincident(g7,g3)
    c: Horizontal(g7)
FEATURE [Part::Extrusion] Extrude071  label="sideB004"
  Base = -> Sketch079
  Dir = (0,0,1)
  DirMode = 2
  FaceMakerClass = Part::FaceMakerBullseye
  LengthFwd = 3
  LengthRev = 0
  Placement = pos=(0,0,71.7) rot=(0,0,1;0rad)
  Solid = true
  Symmetric = false
FEATURE [Part::MultiFuse] Fusion152  label="removeFromBottom004"
  Placement = pos=(2,0,0) rot=(0,0,1;0rad)
  Shapes = -> [Extrude070,Extrude071]
FEATURE [Part::Extrusion] Extrude072
  Base = -> Sketch081
  Dir = (1,0,0)
  DirMode = 2
  FaceMakerClass = Part::FaceMakerBullseye
  LengthFwd = 10
  LengthRev = 0
  Solid = true
  Symmetric = false
FEATURE [Part::Fillet] Fillet059  label="removeFromtMoreFrontCaseScrewRetainers004"
  Base = -> Extrude072
  Edges = 4 edges r=1.49: [Edge6,Edge11,Edge18,Edge23]
  Placement = pos=(-12,0,0) rot=(0,0,1;0rad)
FEATURE [Sketcher::SketchObject] Sketch082
  FullyConstrained = true
  Placement = pos=(117,19,0) rot=(0.57735,0.57735,0.57735;2.0944rad)
  sketch-geometry (8):
    g0: LineSegment StartX=-49.19 StartY=69.25 StartZ=0 EndX=-49.19 EndY=66.25 EndZ=0
    g1: LineSegment StartX=-49.19 StartY=5.75 StartZ=0 EndX=-49.19 EndY=2.75 EndZ=0
    g2: ArcOfCircle CenterX=-1.5 CenterY=67.75 CenterZ=0 NormalX=0 NormalY=0 NormalZ=1 AngleXU=0 Radius=1.5 StartAngle=4.71239 EndAngle=7.85398
    g3: ArcOfCircle CenterX=-1.5 CenterY=4.25 CenterZ=0 NormalX=0 NormalY=0 NormalZ=1 AngleXU=0 Radius=1.5 StartAngle=4.71239 EndAngle=7.85398
    g4: LineSegment StartX=-49.19 StartY=69.25 StartZ=0 EndX=-1.5 EndY=69.25 EndZ=0
    g5: LineSegment StartX=-49.19 StartY=66.25 StartZ=0 EndX=-1.5 EndY=66.25 EndZ=0
    g6: LineSegment StartX=-49.19 StartY=5.75 StartZ=0 EndX=-1.5 EndY=5.75 EndZ=0
    g7: LineSegment StartX=-49.19 StartY=2.75 StartZ=0 EndX=-1.5 EndY=2.75 EndZ=0
  constraints (19):
    c: Vertical(g0)
    c: Distance(g0) = 3
    c: Block(g0)
    c: Vertical(g1)
    c: Block(g2)
    c: Block(g3)
    c: Block(g1)
    c: Coincident(g4,g0)
    c: Coincident(g4,g2)
    c: Horizontal(g4)
    c: Coincident(g5,g0)
    c: Coincident(g5,g2)
    c: Horizontal(g5)
    c: Coincident(g6,g1)
    c: Coincident(g6,g3)
    c: Horizontal(g6)
    c: Coincident(g7,g1)
    c: Coincident(g7,g3)
    c: Horizontal(g7)
FEATURE [Part::Extrusion] Extrude073
  Base = -> Sketch082
  Dir = (1,0,0)
  DirMode = 2
  FaceMakerClass = Part::FaceMakerBullseye
  LengthFwd = 10
  LengthRev = 0
  Solid = true
  Symmetric = false
FEATURE [Part::Fillet] Fillet060  label="removeFromtMoreFrontCaseScrewRetainers005"
  Base = -> Extrude073
  Edges = 4 edges r=1.49: [Edge6,Edge11,Edge18,Edge23]
  Placement = pos=(-4,0,0) rot=(0,0,1;0rad)
FEATURE [Part::Revolution] Revolve163  label="backCaseScrewRetainer004"
  Angle = 360
  Axis = (0,1,0)
  Base = (0,0,0)
  FaceMakerClass = Part::FaceMakerBullseye
  Placement = pos=(12.5,3,62) rot=(0,0,1;0rad)
  Solid = false
  Source = -> Face149
  Symmetric = false
FEATURE [Part::Revolution] Revolve164  label="frontCaseScrewRetainer006"
  Angle = 360
  Axis = (0,1,0)
  Base = (0,0,0)
  FaceMakerClass = Part::FaceMakerBullseye
  Placement = pos=(89.5,3,68.5) rot=(0,0,1;0rad)
  Solid = false
  Source = -> Face151
  Symmetric = false
FEATURE [Part::Revolution] Revolve165  label="frontCaseScrewRetainer007"
  Angle = 360
  Axis = (0,1,0)
  Base = (0,0,0)
  FaceMakerClass = Part::FaceMakerBullseye
  Placement = pos=(89.5,3,3.5) rot=(0,0,1;0rad)
  Solid = false
  Source = -> Face152
  Symmetric = false
FEATURE [Part::Revolution] Revolve166  label="backCaseScrewRetainer005"
  Angle = 360
  Axis = (0,1,0)
  Base = (0,0,0)
  FaceMakerClass = Part::FaceMakerBullseye
  Placement = pos=(12.5,3,10) rot=(0,0,1;0rad)
  Solid = false
  Source = -> Face150
  Symmetric = false
FEATURE [Part::Revolution] Revolve167  label="moreFrontCaseScrewRetainer006"
  Angle = 360
  Axis = (0,1,0)
  Base = (0,0,0)
  FaceMakerClass = Part::FaceMakerBullseye
  Placement = pos=(109.5,4.5,68.5) rot=(0,0,1;0rad)
  Solid = false
  Source = -> Face153
  Symmetric = false
FEATURE [Part::Revolution] Revolve168  label="moreFrontCaseScrewRetainer007"
  Angle = 360
  Axis = (0,1,0)
  Base = (0,0,0)
  FaceMakerClass = Part::FaceMakerBullseye
  Placement = pos=(109.5,4.5,3.5) rot=(0,0,1;0rad)
  Solid = false
  Source = -> Face154
  Symmetric = false
FEATURE [Part::MultiFuse] Fusion151  label="screwRetainers003"
  Shapes = -> [Revolve168,Revolve167,Revolve166,Revolve165,Revolve164,Revolve163]
FEATURE [Part::Cut] Cut069  label="screwRetainers004"
  Base = -> Fusion151
  Tool = -> Fusion152
FEATURE [Part::Cut] Cut070
  Base = -> Cut069
  Tool = -> Fillet060
FEATURE [Part::Cut] Cut071  label="screwPillars001"
  Base = -> Cut070
  Tool = -> Fillet059
FEATURE [Part::MultiFuse] Fusion153  label="bottom024"
  Shapes = -> [Fusion149,Cut071]
FEATURE [Part::Cylinder] Cylinder067
  Angle = 360
  AttacherType = Attacher::AttachEngine3D
  Height = 10
  Placement = pos=(20.65,12,4.68) rot=(1,0,0;1.5708rad)
  Radius = 2
FEATURE [Part::Cylinder] Cylinder068
  Angle = 360
  AttacherType = Attacher::AttachEngine3D
  Height = 10
  Placement = pos=(20.65,12,67.38) rot=(1,0,0;1.5708rad)
  Radius = 2
FEATURE [Part::Cylinder] Cylinder069
  Angle = 360
  AttacherType = Attacher::AttachEngine3D
  Height = 10
  Placement = pos=(77.15,12,67.38) rot=(1,0,0;1.5708rad)
  Radius = 2
FEATURE [Part::Cylinder] Cylinder070
  Angle = 360
  AttacherType = Attacher::AttachEngine3D
  Height = 10
  Placement = pos=(77.15,12,4.68) rot=(1,0,0;1.5708rad)
  Radius = 2
FEATURE [Part::MultiFuse] Fusion154  label="removeFromThreadedInsertHousing001"
  Shapes = -> [Cylinder069,Cylinder068,Cylinder067,Cylinder070]
FEATURE [Part::Cut] Cut072  label="bottom025"
  Base = -> Fusion153
  Tool = -> Fusion154
FEATURE [Image::ImagePlane] ImagePlane
  XSize = 339
  YSize = 72
FEATURE [Sketcher::SketchObject] Sketch083
  FullyConstrained = true
  MapMode = 5
  Support = -> [XY_Plane]
  sketch-geometry (338):
    g0: LineSegment StartX=-151.619 StartY=28.8932 StartZ=0 EndX=-140.819 EndY=28.8932 EndZ=0
    g1: LineSegment StartX=-151.619 StartY=24.0313 StartZ=0 EndX=-151.619 EndY=28.8932 EndZ=0
    g2: LineSegment StartX=-140.819 StartY=17.7713 StartZ=0 EndX=-151.619 EndY=17.7713 EndZ=0
    g3: LineSegment StartX=-151.619 StartY=17.7713 StartZ=0 EndX=-151.619 EndY=22.6313 EndZ=0
    g4: LineSegment StartX=-151.619 StartY=22.6313 StartZ=0 EndX=-145.128 EndY=22.6313 EndZ=0
    g5: LineSegment StartX=-145.128 StartY=24.0313 StartZ=0 EndX=-140.819 EndY=28.8932 EndZ=0
    g6: LineSegment StartX=-145.128 StartY=22.6313 StartZ=0 EndX=-140.819 EndY=17.7713 EndZ=0
    g7: ArcOfCircle CenterX=-155.157 CenterY=23.3323 CenterZ=0 NormalX=0 NormalY=0 NormalZ=1 AngleXU=0 Radius=6.92354 StartAngle=1.03434 EndAngle=5.24885
    g8: ArcOfCircle CenterX=-155.157 CenterY=23.3323 CenterZ=0 NormalX=0 NormalY=0 NormalZ=1 AngleXU=0 Radius=12.6269 StartAngle=1.28675 EndAngle=4.99643
    g9: LineSegment StartX=-151.619 StartY=35.4532 StartZ=0 EndX=-151.619 EndY=29.2832 EndZ=0
    g10: LineSegment StartX=-151.619 StartY=17.3813 StartZ=0 EndX=-151.619 EndY=11.2113 EndZ=0
    g11-g21: Circle x11 (B-spline internal-alignment scaffolding for g22; pole/knot coordinates omitted)
    g22: BSplineCurve PolesCount=11 KnotsCount=9 Degree=3 IsPeriodic=0
    g23-g31: GeomPoint x9 (B-spline internal-alignment scaffolding for g22; pole/knot coordinates omitted)
    g32-g49: Circle x18 (B-spline internal-alignment scaffolding for g50; pole/knot coordinates omitted)
    g50: BSplineCurve PolesCount=18 KnotsCount=16 Degree=3 IsPeriodic=0
    g51-g66: GeomPoint x16 (B-spline internal-alignment scaffolding for g50; pole/knot coordinates omitted)
    g67: LineSegment StartX=-117.124 StartY=30.093 StartZ=0 EndX=-117.603 EndY=26.5272 EndZ=0
    g68: LineSegment StartX=-117.603 StartY=17.8472 StartZ=0 EndX=-117.124 EndY=14.2659 EndZ=0
    g69: Ellipse CenterX=-109.671 CenterY=20.025 CenterZ=0 NormalX=0 NormalY=0 NormalZ=1 MajorRadius=3.34798 MinorRadius=2.71052 AngleXU=-1.56793
    g70: GeomPoint X=-109.666 Y=18.0598 Z=0
    g71: GeomPoint X=-109.677 Y=21.9902 Z=0
    g72: Ellipse CenterX=-109.671 CenterY=20.0123 CenterZ=0 NormalX=0 NormalY=0 NormalZ=1 MajorRadius=6.93002 MinorRadius=6.36273 AngleXU=-3.13976
    g73: GeomPoint X=-112.417 Y=20.0073 Z=0
    g74: GeomPoint X=-106.925 Y=20.0173 Z=0
    g75: Ellipse CenterX=-51.7682 CenterY=20.1463 CenterZ=0 NormalX=0 NormalY=0 NormalZ=1 MajorRadius=3.19279 MinorRadius=2.71052 AngleXU=-1.52774
    g76: GeomPoint X=-51.6955 Y=18.4606 Z=0
    g77: GeomPoint X=-51.8408 Y=21.832 Z=0
    g78: GeomPoint X=-54.5142 Y=20.1413 Z=0
    g79: GeomPoint X=-49.0221 Y=20.1513 Z=0
    g80: Ellipse CenterX=-51.7682 CenterY=20.1463 CenterZ=0 NormalX=0 NormalY=0 NormalZ=1 MajorRadius=6.93002 MinorRadius=6.36273 AngleXU=-3.13976
    g81: Ellipse CenterX=-22.8436 CenterY=20.1783 CenterZ=0 NormalX=0 NormalY=0 NormalZ=1 MajorRadius=3.31512 MinorRadius=2.71052 AngleXU=-1.60214
    g82: GeomPoint X=-22.9034 Y=18.2706 Z=0
    g83: GeomPoint X=-22.7838 Y=22.0861 Z=0
    g84: GeomPoint X=-25.5897 Y=20.1733 Z=0
    g85: GeomPoint X=-20.0976 Y=20.1833 Z=0
    g86: Ellipse CenterX=-22.8436 CenterY=20.1783 CenterZ=0 NormalX=0 NormalY=0 NormalZ=1 MajorRadius=6.93002 MinorRadius=6.36273 AngleXU=-3.13976
    g87: LineSegment StartX=-101.889 StartY=14.1107 StartZ=0 EndX=-97.7455 EndY=14.1107 EndZ=0
    g88: LineSegment StartX=-93.8155 StartY=14.1107 StartZ=0 EndX=-89.6755 EndY=14.1107 EndZ=0
    g89: LineSegment StartX=-85.7455 StartY=14.1107 StartZ=0 EndX=-81.6055 EndY=14.1107 EndZ=0
    g90: LineSegment StartX=-101.889 StartY=14.1107 StartZ=0 EndX=-101.889 EndY=25.9907 EndZ=0
    g91: LineSegment StartX=-101.889 StartY=25.9907 StartZ=0 EndX=-97.8594 EndY=25.9907 EndZ=0
    g92: LineSegment StartX=-97.8594 StartY=25.9907 StartZ=0 EndX=-97.8594 EndY=24.0907 EndZ=0
    g93: LineSegment StartX=-97.7455 StartY=14.1107 StartZ=0 EndX=-97.7455 EndY=19.9107 EndZ=0
    g94: LineSegment StartX=-89.6755 StartY=14.1107 StartZ=0 EndX=-89.6755 EndY=19.9107 EndZ=0
    g95: LineSegment StartX=-93.8155 StartY=14.1107 StartZ=0 EndX=-93.8155 EndY=21.0107 EndZ=0
    g96-g106: Circle x11 (B-spline internal-alignment scaffolding for g107; pole/knot coordinates omitted)
    g107: BSplineCurve PolesCount=11 KnotsCount=9 Degree=3 IsPeriodic=0
    g108-g116: GeomPoint x9 (B-spline internal-alignment scaffolding for g107; pole/knot coordinates omitted)
    g117: BSplineCurve PolesCount=11 KnotsCount=9 Degree=3 IsPeriodic=0
    g118-g125: Circle x8 (B-spline internal-alignment scaffolding for g126; pole/knot coordinates omitted)
    g126: BSplineCurve PolesCount=8 KnotsCount=6 Degree=3 IsPeriodic=0
    g127-g132: GeomPoint x6 (B-spline internal-alignment scaffolding for g126; pole/knot coordinates omitted)
    g133: BSplineCurve PolesCount=8 KnotsCount=6 Degree=3 IsPeriodic=0
    g134: LineSegment StartX=-85.7455 StartY=21.0107 StartZ=0 EndX=-85.7455 EndY=14.1107 EndZ=0
    g135: LineSegment StartX=-80.0879 StartY=14.1107 StartZ=0 EndX=-75.944 EndY=14.1107 EndZ=0
    g136: LineSegment StartX=-72.014 StartY=14.1107 StartZ=0 EndX=-67.874 EndY=14.1107 EndZ=0
    g137: LineSegment StartX=-63.944 StartY=14.1107 StartZ=0 EndX=-59.804 EndY=14.1107 EndZ=0
    g138: LineSegment StartX=-80.0879 StartY=14.1107 StartZ=0 EndX=-80.0879 EndY=25.9907 EndZ=0
    g139: LineSegment StartX=-80.0879 StartY=25.9907 StartZ=0 EndX=-76.0579 EndY=25.9907 EndZ=0
    g140: LineSegment StartX=-76.0579 StartY=25.9907 StartZ=0 EndX=-76.0579 EndY=24.0907 EndZ=0
    g141: LineSegment StartX=-75.944 StartY=14.1107 StartZ=0 EndX=-75.944 EndY=19.9107 EndZ=0
    g142: LineSegment StartX=-67.874 StartY=14.1107 StartZ=0 EndX=-67.874 EndY=19.9107 EndZ=0
    g143: LineSegment StartX=-72.014 StartY=14.1107 StartZ=0 EndX=-72.014 EndY=21.0107 EndZ=0
    g144-g148: Circle x5 (B-spline internal-alignment scaffolding for g149; pole/knot coordinates omitted)
    g149: BSplineCurve PolesCount=11 KnotsCount=9 Degree=3 IsPeriodic=0
    g150-g158: GeomPoint x9 (B-spline internal-alignment scaffolding for g149; pole/knot coordinates omitted)
    g159: BSplineCurve PolesCount=11 KnotsCount=9 Degree=3 IsPeriodic=0
    g160-g167: Circle x8 (B-spline internal-alignment scaffolding for g168; pole/knot coordinates omitted)
    g168: BSplineCurve PolesCount=8 KnotsCount=6 Degree=3 IsPeriodic=0
    g169-g174: GeomPoint x6 (B-spline internal-alignment scaffolding for g168; pole/knot coordinates omitted)
    g175: BSplineCurve PolesCount=8 KnotsCount=6 Degree=3 IsPeriodic=0
    g176: LineSegment StartX=-63.944 StartY=21.0107 StartZ=0 EndX=-63.944 EndY=14.1107 EndZ=0
    g177: LineSegment StartX=-59.804 StartY=14.1107 StartZ=0 EndX=-59.804 EndY=21.5868 EndZ=0
    g178: BSplineCurve PolesCount=4 KnotsCount=2 Degree=3 IsPeriodic=0
    g179: GeomPoint X=-59.804 Y=21.5868 Z=0
    g180: GeomPoint X=-60.2379 Y=24.0907 Z=0
    g181: LineSegment StartX=-81.6055 StartY=14.1107 StartZ=0 EndX=-81.6055 EndY=21.5868 EndZ=0
    g182: LineSegment StartX=-151.619 StartY=24.0313 StartZ=0 EndX=-145.128 EndY=24.0313 EndZ=0
    g183: Circle CenterX=-82.0394 CenterY=24.0907 CenterZ=0 NormalX=0 NormalY=0 NormalZ=1 AngleXU=0 Radius=1
    g184: Circle CenterX=-81.7131 CenterY=23.2736 CenterZ=0 NormalX=0 NormalY=0 NormalZ=1 AngleXU=0 Radius=1
    g185: Circle CenterX=-81.6055 CenterY=21.5868 CenterZ=0 NormalX=0 NormalY=0 NormalZ=1 AngleXU=0 Radius=1
    g186: BSplineCurve PolesCount=3 KnotsCount=2 Degree=2 IsPeriodic=0
    g187: GeomPoint X=-82.0394 Y=24.0907 Z=0
    g188: GeomPoint X=-81.6055 Y=21.5868 Z=0
    g189: Ellipse CenterX=-37.3522 CenterY=19.9515 CenterZ=0 NormalX=0 NormalY=0 NormalZ=1 MajorRadius=2.99755 MinorRadius=2.49 AngleXU=1.5708
    g190: GeomPoint X=-37.3522 Y=21.6203 Z=0
    g191: GeomPoint X=-37.3522 Y=18.2826 Z=0
    g192: ArcOfEllipse CenterX=-38.7647 CenterY=20.06 CenterZ=0 NormalX=0 NormalY=0 NormalZ=1 MajorRadius=6.30025 MinorRadius=5.3849 AngleXU=1.57276 StartAngle=5.50632 EndAngle=10.3035
    g193: GeomPoint X=-38.7711 Y=23.3304 Z=0
    g194: GeomPoint X=-38.7583 Y=16.7895 Z=0
    g195: LineSegment StartX=-34.6109 StartY=14.1107 StartZ=0 EndX=-30.8984 EndY=14.1107 EndZ=0
    g196: LineSegment StartX=-30.8984 StartY=14.1107 StartZ=0 EndX=-30.8984 EndY=31.1784 EndZ=0
    g197: LineSegment StartX=-30.8984 StartY=31.1784 StartZ=0 EndX=-34.9984 EndY=31.1784 EndZ=0
    g198: LineSegment StartX=-34.9984 StartY=24.5602 StartZ=0 EndX=-34.9984 EndY=31.1784 EndZ=0
    g199: LineSegment StartX=-34.6109 StartY=16.0476 StartZ=0 EndX=-34.6109 EndY=14.1107 EndZ=0
    g200: LineSegment StartX=-14.8781 StartY=14.1107 StartZ=0 EndX=-10.5106 EndY=14.1107 EndZ=0
    g201: LineSegment StartX=-14.8781 StartY=14.1107 StartZ=0 EndX=-14.8781 EndY=25.8504 EndZ=0
    g202: LineSegment StartX=-14.8781 StartY=25.8504 StartZ=0 EndX=-10.8534 EndY=25.8504 EndZ=0
    g203: LineSegment StartX=-10.8534 StartY=25.8504 StartZ=0 EndX=-10.8534 EndY=24.0923 EndZ=0
    g204: LineSegment StartX=-10.5106 StartY=14.1107 StartZ=0 EndX=-10.5106 EndY=19.7752 EndZ=0
    g205: LineSegment StartX=-5.96397 StartY=25.9304 StartZ=0 EndX=-5.96397 EndY=22.574 EndZ=0
    g206-g214: Circle x9 (B-spline internal-alignment scaffolding for g215; pole/knot coordinates omitted)
    g215: BSplineCurve PolesCount=9 KnotsCount=7 Degree=3 IsPeriodic=0
    g216-g222: GeomPoint x7 (B-spline internal-alignment scaffolding for g215; pole/knot coordinates omitted)
    g223-g232: Circle x10 (B-spline internal-alignment scaffolding for g233; pole/knot coordinates omitted)
    g233: BSplineCurve PolesCount=10 KnotsCount=8 Degree=3 IsPeriodic=0
    g234-g241: GeomPoint x8 (B-spline internal-alignment scaffolding for g233; pole/knot coordinates omitted)
    g242: LineSegment StartX=-1.58923 StartY=21.0696 StartZ=0 EndX=2.62034 EndY=21.0696 EndZ=0
    g243: LineSegment StartX=-1.55856 StartY=18.7342 StartZ=0 EndX=6.45946 EndY=18.7342 EndZ=0
    g244: LineSegment StartX=5.29231 StartY=17.386 StartZ=0 EndX=5.29231 EndY=14.3674 EndZ=0
    g245-g269: Circle x25 (B-spline internal-alignment scaffolding for g270; pole/knot coordinates omitted)
    g270: BSplineCurve PolesCount=25 KnotsCount=23 Degree=3 IsPeriodic=0
    g271-g293: GeomPoint x23 (B-spline internal-alignment scaffolding for g270; pole/knot coordinates omitted)
    g294-g304: Circle x11 (B-spline internal-alignment scaffolding for g305; pole/knot coordinates omitted)
    g305: BSplineCurve PolesCount=11 KnotsCount=9 Degree=3 IsPeriodic=0
    g306-g314: GeomPoint x9 (B-spline internal-alignment scaffolding for g305; pole/knot coordinates omitted)
    g315-g326: Circle x12 (B-spline internal-alignment scaffolding for g327; pole/knot coordinates omitted)
    g327: BSplineCurve PolesCount=12 KnotsCount=10 Degree=3 IsPeriodic=0
    g328-g337: GeomPoint x10 (B-spline internal-alignment scaffolding for g327; pole/knot coordinates omitted)
  constraints (252):
    c: Coincident(g1,g0)
    c: Horizontal(g0)
    c: Vertical(g1)
    c: Coincident(g2,g3)
    c: Coincident(g3,g4)
    c: Horizontal(g4)
    c: Horizontal(g2)
    c: Vertical(g3)
    c: Block(g1)
    c: Distance(g3) = 4.86
    c: Block(g4)
    c: Distance(g0) = 10.8
    c: Distance(g2) = 10.8
    c: Coincident(g5,g0)
    c: Coincident(g6,g4)
    c: Coincident(g6,g2)
    c: Block(g8)
    c: Block(g7)
    c: Coincident(g9,g8)
    c: Coincident(g9,g7)
    c: Vertical(g9)
    c: Coincident(g10,g7)
    c: Coincident(g10,g8)
    c: Vertical(g10)
    c: Weight(g11) = 1
    c: Equal(g11, g12-g21) x10
    c: InternalAlignment(g11-g21 -> g22) x11
    c: InternalAlignment(g23-g31 -> g22) x9
    c: Block(g22)
    c: Weight(g32) = 1
    c: Equal(g32, g33-g49) x17
    c: InternalAlignment(g32-g49 -> g50) x18
    c: InternalAlignment(g51-g66 -> g50) x16
    c: Block(g50)
    c: Coincident(g67,g50)
    c: Coincident(g67,g22)
    c: Coincident(g68,g22)
    c: Coincident(g68,g50)
    c: InternalAlignment(g70,g69)
    c: InternalAlignment(g71,g69)
    c: Block(g69)
    c: InternalAlignment(g73,g72)
    c: InternalAlignment(g74,g72)
    c: Block(g72)
    c: InternalAlignment(g76,g75)
    c: InternalAlignment(g77,g75)
    c: InternalAlignment(g78,g80)
    c: InternalAlignment(g79,g80)
    c: Block(g80)
    c: Coincident(g75,g80)
    c: Block(g75)
    c: InternalAlignment(g82,g81)
    c: InternalAlignment(g83,g81)
    c: InternalAlignment(g84,g86)
    c: InternalAlignment(g85,g86)
    c: Block(g86)
    c: Coincident(g81,g86)
    c: Block(g81)
    c: Horizontal(g87)
    c: Block(g87)
    c: Horizontal(g88)
    c: Distance(g88) = 4.14
    c: Horizontal(g89)
    c: Equal(g88,g89) = 4.14
    c: Block(g89)
    c: Block(g88)
    c: Coincident(g90,g87)
    c: Vertical(g90)
    c: Distance(g90) = 11.88
    c: Coincident(g91,g90)
    c: Horizontal(g91)
    c: Coincident(g92,g91)
    c: Vertical(g92)
    c: Distance(g91) = 4.03
    c: Distance(g92) = 1.9
    c: Coincident(g93,g87)
    c: Vertical(g93)
    c: Vertical(g94)
    c: Coincident(g94,g88)
    c: Distance(g93) = 5.8
    c: Distance(g94) = 5.8
    c: Vertical(g95)
    c: Coincident(g95,g88)
    c: Distance(g95) = 6.9
    c: Coincident(g107,g92)
    c: Weight(g96) = 1
    c: Equal(g96, g97-g106) x10
    c: InternalAlignment(g96-g106 -> g107) x11
    c: InternalAlignment(g108-g116 -> g107) x9
    c: Block(g107)
    c: Block(g117)
    c: Coincident(g126,g93)
    c: Weight(g118) = 1
    c: Equal(g118, g119-g125) x7
    c: Coincident(g126,g95)
    c: InternalAlignment(g118-g125 -> g126) x8
    c: InternalAlignment(g127-g132 -> g126) x6
    c: Coincident(g133,g94)
    c: Block(g126)
    c: Block(g133)
    c: Coincident(g134,g133)
    c: Coincident(g134,g89)
    c: Vertical(g134)
    c: Horizontal(g135)
    c: Block(g135)
    c: Horizontal(g136)
    c: Equal(g88,g136) = 4.14
    c: Horizontal(g137)
    c: Equal(g136,g137) = 4.14
    c: Block(g137)
    c: Block(g136)
    c: Coincident(g138,g135)
    c: Vertical(g138)
    c: Equal(g90,g138) = 11.88
    c: Coincident(g139,g138)
    c: Horizontal(g139)
    c: Coincident(g140,g139)
    c: Vertical(g140)
    c: Equal(g91,g139) = 4.03
    c: Equal(g92,g140) = 1.9
    c: Coincident(g141,g135)
    c: Vertical(g141)
    c: Vertical(g142)
    c: Coincident(g142,g136)
    c: Equal(g93,g141) = 5.8
    c: Equal(g94,g142) = 5.8
    c: Vertical(g143)
    c: Coincident(g143,g136)
    c: Equal(g95,g143) = 6.9
    c: Coincident(g149,g140)
    c: Equal(g96,g144) = 1
    c: Equal(g144, g145-g148) x4
    c: InternalAlignment(g144-g148 -> g149) x5
    c: InternalAlignment(g150-g158 -> g149) x9
    c: Block(g149)
    c: Block(g159)
    c: Coincident(g168,g141)
    c: Equal(g118,g160) = 1
    c: Equal(g160, g161-g167) x7
    c: Coincident(g168,g143)
    c: InternalAlignment(g160-g167 -> g168) x8
    c: InternalAlignment(g169-g174 -> g168) x6
    c: Coincident(g175,g142)
    c: Block(g168)
    c: Block(g175)
    c: Coincident(g176,g175)
    c: Coincident(g176,g137)
    c: Vertical(g176)
    c: Coincident(g177,g137)
    c: Vertical(g177)
    c: Coincident(g178,g177)
    c: Coincident(g178,g159)
    c: InternalAlignment(g179,g178)
    c: InternalAlignment(g180,g178)
    c: Block(g178)
    c: Vertical(g181)
    c: Coincident(g181,g89)
    c: Block(g5)
    c: Coincident(g182,g1)
    c: Coincident(g182,g5)
    c: Horizontal(g182)
    c: Coincident(g186,g117)
    c: Weight(g183) = 1
    c: Equal(g183,g184)
    c: Equal(g183,g185)
    c: Coincident(g186,g181)
    c: InternalAlignment(g183,g186)
    c: InternalAlignment(g184,g186)
    c: InternalAlignment(g185,g186)
    c: InternalAlignment(g187,g186)
    c: InternalAlignment(g188,g186)
    c: Block(g186)
    c: InternalAlignment(g190,g189)
    c: InternalAlignment(g191,g189)
    c: Block(g189)
    c: InternalAlignment(g193,g192)
    c: InternalAlignment(g194,g192)
    c: Block(g192)
    c: Horizontal(g195)
    c: Block(g195)
    c: Coincident(g196,g195)
    c: Vertical(g196)
    c: Block(g196)
    c: Distance(g195) = 3.71244
    c: Coincident(g197,g196)
    c: Horizontal(g197)
    c: Distance(g197) = 4.1
    c: Coincident(g198,g192)
    c: Coincident(g198,g197)
    c: Vertical(g198)
    c: Block(g198)
    c: Coincident(g199,g192)
    c: Coincident(g199,g195)
    c: Vertical(g199)
    c: Block(g199)
    c: Horizontal(g200)
    c: Block(g200)
    c: Coincident(g201,g200)
    c: Vertical(g201)
    c: Block(g201)
    c: Coincident(g202,g201)
    c: Horizontal(g202)
    c: Block(g202)
    c: Coincident(g203,g202)
    c: Vertical(g203)
    c: Block(g203)
    c: Coincident(g204,g200)
    c: Vertical(g204)
    c: Block(g204)
    c: Coincident(g215,g203)
    c: Weight(g206) = 1
    c: Equal(g206, g207-g214) x8
    c: Coincident(g215,g205)
    c: InternalAlignment(g206-g214 -> g215) x9
    c: InternalAlignment(g216-g222 -> g215) x7
    c: Coincident(g233,g204)
    c: Weight(g223) = 1
    c: Equal(g223, g224-g232) x9
    c: Coincident(g233,g205)
    c: InternalAlignment(g223-g232 -> g233) x10
    c: InternalAlignment(g234-g241 -> g233) x8
    c: Vertical(g205)
    c: Block(g205)
    c: Block(g215)
    c: Block(g233)
    c: Horizontal(g242)
    c: Horizontal(g243)
    c: Block(g242)
    c: Block(g243)
    c: Vertical(g244)
    c: Block(g244)
    c: Coincident(g270,g243)
    c: Weight(g245) = 1
    c: Equal(g245, g246-g269) x24
    c: Coincident(g270,g244)
    c: InternalAlignment(g245-g269 -> g270) x25
    c: InternalAlignment(g271-g293 -> g270) x23
    c: Coincident(g305,g242)
    c: Weight(g294) = 1
    c: Equal(g294, g295-g304) x10
    c: Coincident(g305,g242)
    c: InternalAlignment(g294-g304 -> g305) x11
    c: InternalAlignment(g306-g314 -> g305) x9
    c: Block(g305)
    c: Coincident(g327,g243)
    c: Weight(g315) = 1
    c: Equal(g315, g316-g326) x11
    c: Coincident(g327,g244)
    c: InternalAlignment(g315-g326 -> g327) x12
    c: InternalAlignment(g328-g337 -> g327) x10
    c: Block(g327)
    c: Block(g270)
FEATURE [PartDesign::Body] Body  label="CommodoreLogoAndText"
  Group = -> [Sketch083]
  Origin = -> Origin
FEATURE [Part::Extrusion] Extrude074  label="CommodoreLogoAndText001"
  Base = -> Sketch083
  Dir = (0,0,1)
  DirMode = 2
  FaceMakerClass = Part::FaceMakerBullseye
  LengthFwd = 10
  LengthRev = 0
  Solid = true
  Symmetric = false
FEATURE [Part::FeaturePython] Clone  label="CommodoreLogoAndTextScale"  # Draft clone (typed FeaturePython)
  AttacherType = Attacher::AttachEngine3D
  Fuse = false
  Objects = -> [Extrude074]
  Placement = pos=(111,5.37,-11.6) rot=(0,0,1;0rad)
  Scale = (0.62,0.62,1)
FEATURE [Part::Mirroring] Part__Mirroring  label="CommodoreLogoAndTextScale (Mirror #1)"
  Base = (0,0,0)
  Normal = (1,0,0)
  Placement = pos=(123.576,0,0) rot=(0,0,1;0rad)
  Source = -> Clone
FEATURE [Sketcher::SketchObject] Sketch084
  FullyConstrained = true
  MapMode = 5
  Support = -> [XY_Plane001]
  sketch-geometry (338):
    g0: LineSegment StartX=-151.619 StartY=28.8932 StartZ=0 EndX=-140.819 EndY=28.8932 EndZ=0
    g1: LineSegment StartX=-151.619 StartY=24.0313 StartZ=0 EndX=-151.619 EndY=28.8932 EndZ=0
    g2: LineSegment StartX=-140.819 StartY=17.7713 StartZ=0 EndX=-151.619 EndY=17.7713 EndZ=0
    g3: LineSegment StartX=-151.619 StartY=17.7713 StartZ=0 EndX=-151.619 EndY=22.6313 EndZ=0
    g4: LineSegment StartX=-151.619 StartY=22.6313 StartZ=0 EndX=-145.128 EndY=22.6313 EndZ=0
    g5: LineSegment StartX=-145.128 StartY=24.0313 StartZ=0 EndX=-140.819 EndY=28.8932 EndZ=0
    g6: LineSegment StartX=-145.128 StartY=22.6313 StartZ=0 EndX=-140.819 EndY=17.7713 EndZ=0
    g7: ArcOfCircle CenterX=-155.157 CenterY=23.3323 CenterZ=0 NormalX=0 NormalY=0 NormalZ=1 AngleXU=0 Radius=6.92354 StartAngle=1.03434 EndAngle=5.24885
    g8: ArcOfCircle CenterX=-155.157 CenterY=23.3323 CenterZ=0 NormalX=0 NormalY=0 NormalZ=1 AngleXU=0 Radius=12.6269 StartAngle=1.28675 EndAngle=4.99643
    g9: LineSegment StartX=-151.619 StartY=35.4532 StartZ=0 EndX=-151.619 EndY=29.2832 EndZ=0
    g10: LineSegment StartX=-151.619 StartY=17.3813 StartZ=0 EndX=-151.619 EndY=11.2113 EndZ=0
    g11-g21: Circle x11 (B-spline internal-alignment scaffolding for g22; pole/knot coordinates omitted)
    g22: BSplineCurve PolesCount=11 KnotsCount=9 Degree=3 IsPeriodic=0
    g23-g31: GeomPoint x9 (B-spline internal-alignment scaffolding for g22; pole/knot coordinates omitted)
    g32-g49: Circle x18 (B-spline internal-alignment scaffolding for g50; pole/knot coordinates omitted)
    g50: BSplineCurve PolesCount=18 KnotsCount=16 Degree=3 IsPeriodic=0
    g51-g66: GeomPoint x16 (B-spline internal-alignment scaffolding for g50; pole/knot coordinates omitted)
    g67: LineSegment StartX=-117.124 StartY=30.093 StartZ=0 EndX=-117.603 EndY=26.5272 EndZ=0
    g68: LineSegment StartX=-117.603 StartY=17.8472 StartZ=0 EndX=-117.124 EndY=14.2659 EndZ=0
    g69: Ellipse CenterX=-109.671 CenterY=20.025 CenterZ=0 NormalX=0 NormalY=0 NormalZ=1 MajorRadius=3.34798 MinorRadius=2.71052 AngleXU=-1.56793
    g70: GeomPoint X=-109.666 Y=18.0598 Z=0
    g71: GeomPoint X=-109.677 Y=21.9902 Z=0
    g72: Ellipse CenterX=-109.671 CenterY=20.0123 CenterZ=0 NormalX=0 NormalY=0 NormalZ=1 MajorRadius=6.93002 MinorRadius=6.36273 AngleXU=-3.13976
    g73: GeomPoint X=-112.417 Y=20.0073 Z=0
    g74: GeomPoint X=-106.925 Y=20.0173 Z=0
    g75: Ellipse CenterX=-51.7682 CenterY=20.1463 CenterZ=0 NormalX=0 NormalY=0 NormalZ=1 MajorRadius=3.19279 MinorRadius=2.71052 AngleXU=-1.52774
    g76: GeomPoint X=-51.6955 Y=18.4606 Z=0
    g77: GeomPoint X=-51.8408 Y=21.832 Z=0
    g78: GeomPoint X=-54.5142 Y=20.1413 Z=0
    g79: GeomPoint X=-49.0221 Y=20.1513 Z=0
    g80: Ellipse CenterX=-51.7682 CenterY=20.1463 CenterZ=0 NormalX=0 NormalY=0 NormalZ=1 MajorRadius=6.93002 MinorRadius=6.36273 AngleXU=-3.13976
    g81: Ellipse CenterX=-22.8436 CenterY=20.1783 CenterZ=0 NormalX=0 NormalY=0 NormalZ=1 MajorRadius=3.31512 MinorRadius=2.71052 AngleXU=-1.60214
    g82: GeomPoint X=-22.9034 Y=18.2706 Z=0
    g83: GeomPoint X=-22.7838 Y=22.0861 Z=0
    g84: GeomPoint X=-25.5897 Y=20.1733 Z=0
    g85: GeomPoint X=-20.0976 Y=20.1833 Z=0
    g86: Ellipse CenterX=-22.8436 CenterY=20.1783 CenterZ=0 NormalX=0 NormalY=0 NormalZ=1 MajorRadius=6.93002 MinorRadius=6.36273 AngleXU=-3.13976
    g87: LineSegment StartX=-101.889 StartY=14.1107 StartZ=0 EndX=-97.7455 EndY=14.1107 EndZ=0
    g88: LineSegment StartX=-93.8155 StartY=14.1107 StartZ=0 EndX=-89.6755 EndY=14.1107 EndZ=0
    g89: LineSegment StartX=-85.7455 StartY=14.1107 StartZ=0 EndX=-81.6055 EndY=14.1107 EndZ=0
    g90: LineSegment StartX=-101.889 StartY=14.1107 StartZ=0 EndX=-101.889 EndY=25.9907 EndZ=0
    g91: LineSegment StartX=-101.889 StartY=25.9907 StartZ=0 EndX=-97.8594 EndY=25.9907 EndZ=0
    g92: LineSegment StartX=-97.8594 StartY=25.9907 StartZ=0 EndX=-97.8594 EndY=24.0907 EndZ=0
    g93: LineSegment StartX=-97.7455 StartY=14.1107 StartZ=0 EndX=-97.7455 EndY=19.9107 EndZ=0
    g94: LineSegment StartX=-89.6755 StartY=14.1107 StartZ=0 EndX=-89.6755 EndY=19.9107 EndZ=0
    g95: LineSegment StartX=-93.8155 StartY=14.1107 StartZ=0 EndX=-93.8155 EndY=21.0107 EndZ=0
    g96-g106: Circle x11 (B-spline internal-alignment scaffolding for g107; pole/knot coordinates omitted)
    g107: BSplineCurve PolesCount=11 KnotsCount=9 Degree=3 IsPeriodic=0
    g108-g116: GeomPoint x9 (B-spline internal-alignment scaffolding for g107; pole/knot coordinates omitted)
    g117: BSplineCurve PolesCount=11 KnotsCount=9 Degree=3 IsPeriodic=0
    g118-g125: Circle x8 (B-spline internal-alignment scaffolding for g126; pole/knot coordinates omitted)
    g126: BSplineCurve PolesCount=8 KnotsCount=6 Degree=3 IsPeriodic=0
    g127-g132: GeomPoint x6 (B-spline internal-alignment scaffolding for g126; pole/knot coordinates omitted)
    g133: BSplineCurve PolesCount=8 KnotsCount=6 Degree=3 IsPeriodic=0
    g134: LineSegment StartX=-85.7455 StartY=21.0107 StartZ=0 EndX=-85.7455 EndY=14.1107 EndZ=0
    g135: LineSegment StartX=-80.0879 StartY=14.1107 StartZ=0 EndX=-75.944 EndY=14.1107 EndZ=0
    g136: LineSegment StartX=-72.014 StartY=14.1107 StartZ=0 EndX=-67.874 EndY=14.1107 EndZ=0
    g137: LineSegment StartX=-63.944 StartY=14.1107 StartZ=0 EndX=-59.804 EndY=14.1107 EndZ=0
    g138: LineSegment StartX=-80.0879 StartY=14.1107 StartZ=0 EndX=-80.0879 EndY=25.9907 EndZ=0
    g139: LineSegment StartX=-80.0879 StartY=25.9907 StartZ=0 EndX=-76.0579 EndY=25.9907 EndZ=0
    g140: LineSegment StartX=-76.0579 StartY=25.9907 StartZ=0 EndX=-76.0579 EndY=24.0907 EndZ=0
    g141: LineSegment StartX=-75.944 StartY=14.1107 StartZ=0 EndX=-75.944 EndY=19.9107 EndZ=0
    g142: LineSegment StartX=-67.874 StartY=14.1107 StartZ=0 EndX=-67.874 EndY=19.9107 EndZ=0
    g143: LineSegment StartX=-72.014 StartY=14.1107 StartZ=0 EndX=-72.014 EndY=21.0107 EndZ=0
    g144-g148: Circle x5 (B-spline internal-alignment scaffolding for g149; pole/knot coordinates omitted)
    g149: BSplineCurve PolesCount=11 KnotsCount=9 Degree=3 IsPeriodic=0
    g150-g158: GeomPoint x9 (B-spline internal-alignment scaffolding for g149; pole/knot coordinates omitted)
    g159: BSplineCurve PolesCount=11 KnotsCount=9 Degree=3 IsPeriodic=0
    g160-g167: Circle x8 (B-spline internal-alignment scaffolding for g168; pole/knot coordinates omitted)
    g168: BSplineCurve PolesCount=8 KnotsCount=6 Degree=3 IsPeriodic=0
    g169-g174: GeomPoint x6 (B-spline internal-alignment scaffolding for g168; pole/knot coordinates omitted)
    g175: BSplineCurve PolesCount=8 KnotsCount=6 Degree=3 IsPeriodic=0
    g176: LineSegment StartX=-63.944 StartY=21.0107 StartZ=0 EndX=-63.944 EndY=14.1107 EndZ=0
    g177: LineSegment StartX=-59.804 StartY=14.1107 StartZ=0 EndX=-59.804 EndY=21.5868 EndZ=0
    g178: BSplineCurve PolesCount=4 KnotsCount=2 Degree=3 IsPeriodic=0
    g179: GeomPoint X=-59.804 Y=21.5868 Z=0
    g180: GeomPoint X=-60.2379 Y=24.0907 Z=0
    g181: LineSegment StartX=-81.6055 StartY=14.1107 StartZ=0 EndX=-81.6055 EndY=21.5868 EndZ=0
    g182: LineSegment StartX=-151.619 StartY=24.0313 StartZ=0 EndX=-145.128 EndY=24.0313 EndZ=0
    g183: Circle CenterX=-82.0394 CenterY=24.0907 CenterZ=0 NormalX=0 NormalY=0 NormalZ=1 AngleXU=0 Radius=1
    g184: Circle CenterX=-81.7131 CenterY=23.2736 CenterZ=0 NormalX=0 NormalY=0 NormalZ=1 AngleXU=0 Radius=1
    g185: Circle CenterX=-81.6055 CenterY=21.5868 CenterZ=0 NormalX=0 NormalY=0 NormalZ=1 AngleXU=0 Radius=1
    g186: BSplineCurve PolesCount=3 KnotsCount=2 Degree=2 IsPeriodic=0
    g187: GeomPoint X=-82.0394 Y=24.0907 Z=0
    g188: GeomPoint X=-81.6055 Y=21.5868 Z=0
    g189: Ellipse CenterX=-37.3522 CenterY=19.9515 CenterZ=0 NormalX=0 NormalY=0 NormalZ=1 MajorRadius=2.99755 MinorRadius=2.49 AngleXU=1.5708
    g190: GeomPoint X=-37.3522 Y=21.6203 Z=0
    g191: GeomPoint X=-37.3522 Y=18.2826 Z=0
    g192: ArcOfEllipse CenterX=-38.7647 CenterY=20.06 CenterZ=0 NormalX=0 NormalY=0 NormalZ=1 MajorRadius=6.30025 MinorRadius=5.3849 AngleXU=1.57276 StartAngle=5.50632 EndAngle=10.3035
    g193: GeomPoint X=-38.7711 Y=23.3304 Z=0
    g194: GeomPoint X=-38.7583 Y=16.7895 Z=0
    g195: LineSegment StartX=-34.6109 StartY=14.1107 StartZ=0 EndX=-30.8984 EndY=14.1107 EndZ=0
    g196: LineSegment StartX=-30.8984 StartY=14.1107 StartZ=0 EndX=-30.8984 EndY=31.1784 EndZ=0
    g197: LineSegment StartX=-30.8984 StartY=31.1784 StartZ=0 EndX=-34.9984 EndY=31.1784 EndZ=0
    g198: LineSegment StartX=-34.9984 StartY=24.5602 StartZ=0 EndX=-34.9984 EndY=31.1784 EndZ=0
    g199: LineSegment StartX=-34.6109 StartY=16.0476 StartZ=0 EndX=-34.6109 EndY=14.1107 EndZ=0
    g200: LineSegment StartX=-14.8781 StartY=14.1107 StartZ=0 EndX=-10.5106 EndY=14.1107 EndZ=0
    g201: LineSegment StartX=-14.8781 StartY=14.1107 StartZ=0 EndX=-14.8781 EndY=25.8504 EndZ=0
    g202: LineSegment StartX=-14.8781 StartY=25.8504 StartZ=0 EndX=-10.8534 EndY=25.8504 EndZ=0
    g203: LineSegment StartX=-10.8534 StartY=25.8504 StartZ=0 EndX=-10.8534 EndY=24.0923 EndZ=0
    g204: LineSegment StartX=-10.5106 StartY=14.1107 StartZ=0 EndX=-10.5106 EndY=19.7752 EndZ=0
    g205: LineSegment StartX=-5.96397 StartY=25.9304 StartZ=0 EndX=-5.96397 EndY=22.574 EndZ=0
    g206-g214: Circle x9 (B-spline internal-alignment scaffolding for g215; pole/knot coordinates omitted)
    g215: BSplineCurve PolesCount=9 KnotsCount=7 Degree=3 IsPeriodic=0
    g216-g222: GeomPoint x7 (B-spline internal-alignment scaffolding for g215; pole/knot coordinates omitted)
    g223-g232: Circle x10 (B-spline internal-alignment scaffolding for g233; pole/knot coordinates omitted)
    g233: BSplineCurve PolesCount=10 KnotsCount=8 Degree=3 IsPeriodic=0
    g234-g241: GeomPoint x8 (B-spline internal-alignment scaffolding for g233; pole/knot coordinates omitted)
    g242: LineSegment StartX=-1.58923 StartY=21.0696 StartZ=0 EndX=2.62034 EndY=21.0696 EndZ=0
    g243: LineSegment StartX=-1.55856 StartY=18.7342 StartZ=0 EndX=6.45946 EndY=18.7342 EndZ=0
    g244: LineSegment StartX=5.29231 StartY=17.386 StartZ=0 EndX=5.29231 EndY=14.3674 EndZ=0
    g245-g269: Circle x25 (B-spline internal-alignment scaffolding for g270; pole/knot coordinates omitted)
    g270: BSplineCurve PolesCount=25 KnotsCount=23 Degree=3 IsPeriodic=0
    g271-g293: GeomPoint x23 (B-spline internal-alignment scaffolding for g270; pole/knot coordinates omitted)
    g294-g304: Circle x11 (B-spline internal-alignment scaffolding for g305; pole/knot coordinates omitted)
    g305: BSplineCurve PolesCount=11 KnotsCount=9 Degree=3 IsPeriodic=0
    g306-g314: GeomPoint x9 (B-spline internal-alignment scaffolding for g305; pole/knot coordinates omitted)
    g315-g326: Circle x12 (B-spline internal-alignment scaffolding for g327; pole/knot coordinates omitted)
    g327: BSplineCurve PolesCount=12 KnotsCount=10 Degree=3 IsPeriodic=0
    g328-g337: GeomPoint x10 (B-spline internal-alignment scaffolding for g327; pole/knot coordinates omitted)
  constraints (252):
    c: Coincident(g1,g0)
    c: Horizontal(g0)
    c: Vertical(g1)
    c: Coincident(g2,g3)
    c: Coincident(g3,g4)
    c: Horizontal(g4)
    c: Horizontal(g2)
    c: Vertical(g3)
    c: Block(g1)
    c: Distance(g3) = 4.86
    c: Block(g4)
    c: Distance(g0) = 10.8
    c: Distance(g2) = 10.8
    c: Coincident(g5,g0)
    c: Coincident(g6,g4)
    c: Coincident(g6,g2)
    c: Block(g8)
    c: Block(g7)
    c: Coincident(g9,g8)
    c: Coincident(g9,g7)
    c: Vertical(g9)
    c: Coincident(g10,g7)
    c: Coincident(g10,g8)
    c: Vertical(g10)
    c: Weight(g11) = 1
    c: Equal(g11, g12-g21) x10
    c: InternalAlignment(g11-g21 -> g22) x11
    c: InternalAlignment(g23-g31 -> g22) x9
    c: Block(g22)
    c: Weight(g32) = 1
    c: Equal(g32, g33-g49) x17
    c: InternalAlignment(g32-g49 -> g50) x18
    c: InternalAlignment(g51-g66 -> g50) x16
    c: Block(g50)
    c: Coincident(g67,g50)
    c: Coincident(g67,g22)
    c: Coincident(g68,g22)
    c: Coincident(g68,g50)
    c: InternalAlignment(g70,g69)
    c: InternalAlignment(g71,g69)
    c: Block(g69)
    c: InternalAlignment(g73,g72)
    c: InternalAlignment(g74,g72)
    c: Block(g72)
    c: InternalAlignment(g76,g75)
    c: InternalAlignment(g77,g75)
    c: InternalAlignment(g78,g80)
    c: InternalAlignment(g79,g80)
    c: Block(g80)
    c: Coincident(g75,g80)
    c: Block(g75)
    c: InternalAlignment(g82,g81)
    c: InternalAlignment(g83,g81)
    c: InternalAlignment(g84,g86)
    c: InternalAlignment(g85,g86)
    c: Block(g86)
    c: Coincident(g81,g86)
    c: Block(g81)
    c: Horizontal(g87)
    c: Block(g87)
    c: Horizontal(g88)
    c: Distance(g88) = 4.14
    c: Horizontal(g89)
    c: Equal(g88,g89) = 4.14
    c: Block(g89)
    c: Block(g88)
    c: Coincident(g90,g87)
    c: Vertical(g90)
    c: Distance(g90) = 11.88
    c: Coincident(g91,g90)
    c: Horizontal(g91)
    c: Coincident(g92,g91)
    c: Vertical(g92)
    c: Distance(g91) = 4.03
    c: Distance(g92) = 1.9
    c: Coincident(g93,g87)
    c: Vertical(g93)
    c: Vertical(g94)
    c: Coincident(g94,g88)
    c: Distance(g93) = 5.8
    c: Distance(g94) = 5.8
    c: Vertical(g95)
    c: Coincident(g95,g88)
    c: Distance(g95) = 6.9
    c: Coincident(g107,g92)
    c: Weight(g96) = 1
    c: Equal(g96, g97-g106) x10
    c: InternalAlignment(g96-g106 -> g107) x11
    c: InternalAlignment(g108-g116 -> g107) x9
    c: Block(g107)
    c: Block(g117)
    c: Coincident(g126,g93)
    c: Weight(g118) = 1
    c: Equal(g118, g119-g125) x7
    c: Coincident(g126,g95)
    c: InternalAlignment(g118-g125 -> g126) x8
    c: InternalAlignment(g127-g132 -> g126) x6
    c: Coincident(g133,g94)
    c: Block(g126)
    c: Block(g133)
    c: Coincident(g134,g133)
    c: Coincident(g134,g89)
    c: Vertical(g134)
    c: Horizontal(g135)
    c: Block(g135)
    c: Horizontal(g136)
    c: Equal(g88,g136) = 4.14
    c: Horizontal(g137)
    c: Equal(g136,g137) = 4.14
    c: Block(g137)
    c: Block(g136)
    c: Coincident(g138,g135)
    c: Vertical(g138)
    c: Equal(g90,g138) = 11.88
    c: Coincident(g139,g138)
    c: Horizontal(g139)
    c: Coincident(g140,g139)
    c: Vertical(g140)
    c: Equal(g91,g139) = 4.03
    c: Equal(g92,g140) = 1.9
    c: Coincident(g141,g135)
    c: Vertical(g141)
    c: Vertical(g142)
    c: Coincident(g142,g136)
    c: Equal(g93,g141) = 5.8
    c: Equal(g94,g142) = 5.8
    c: Vertical(g143)
    c: Coincident(g143,g136)
    c: Equal(g95,g143) = 6.9
    c: Coincident(g149,g140)
    c: Equal(g96,g144) = 1
    c: Equal(g144, g145-g148) x4
    c: InternalAlignment(g144-g148 -> g149) x5
    c: InternalAlignment(g150-g158 -> g149) x9
    c: Block(g149)
    c: Block(g159)
    c: Coincident(g168,g141)
    c: Equal(g118,g160) = 1
    c: Equal(g160, g161-g167) x7
    c: Coincident(g168,g143)
    c: InternalAlignment(g160-g167 -> g168) x8
    c: InternalAlignment(g169-g174 -> g168) x6
    c: Coincident(g175,g142)
    c: Block(g168)
    c: Block(g175)
    c: Coincident(g176,g175)
    c: Coincident(g176,g137)
    c: Vertical(g176)
    c: Coincident(g177,g137)
    c: Vertical(g177)
    c: Coincident(g178,g177)
    c: Coincident(g178,g159)
    c: InternalAlignment(g179,g178)
    c: InternalAlignment(g180,g178)
    c: Block(g178)
    c: Vertical(g181)
    c: Coincident(g181,g89)
    c: Block(g5)
    c: Coincident(g182,g1)
    c: Coincident(g182,g5)
    c: Horizontal(g182)
    c: Coincident(g186,g117)
    c: Weight(g183) = 1
    c: Equal(g183,g184)
    c: Equal(g183,g185)
    c: Coincident(g186,g181)
    c: InternalAlignment(g183,g186)
    c: InternalAlignment(g184,g186)
    c: InternalAlignment(g185,g186)
    c: InternalAlignment(g187,g186)
    c: InternalAlignment(g188,g186)
    c: Block(g186)
    c: InternalAlignment(g190,g189)
    c: InternalAlignment(g191,g189)
    c: Block(g189)
    c: InternalAlignment(g193,g192)
    c: InternalAlignment(g194,g192)
    c: Block(g192)
    c: Horizontal(g195)
    c: Block(g195)
    c: Coincident(g196,g195)
    c: Vertical(g196)
    c: Block(g196)
    c: Distance(g195) = 3.71244
    c: Coincident(g197,g196)
    c: Horizontal(g197)
    c: Distance(g197) = 4.1
    c: Coincident(g198,g192)
    c: Coincident(g198,g197)
    c: Vertical(g198)
    c: Block(g198)
    c: Coincident(g199,g192)
    c: Coincident(g199,g195)
    c: Vertical(g199)
    c: Block(g199)
    c: Horizontal(g200)
    c: Block(g200)
    c: Coincident(g201,g200)
    c: Vertical(g201)
    c: Block(g201)
    c: Coincident(g202,g201)
    c: Horizontal(g202)
    c: Block(g202)
    c: Coincident(g203,g202)
    c: Vertical(g203)
    c: Block(g203)
    c: Coincident(g204,g200)
    c: Vertical(g204)
    c: Block(g204)
    c: Coincident(g215,g203)
    c: Weight(g206) = 1
    c: Equal(g206, g207-g214) x8
    c: Coincident(g215,g205)
    c: InternalAlignment(g206-g214 -> g215) x9
    c: InternalAlignment(g216-g222 -> g215) x7
    c: Coincident(g233,g204)
    c: Weight(g223) = 1
    c: Equal(g223, g224-g232) x9
    c: Coincident(g233,g205)
    c: InternalAlignment(g223-g232 -> g233) x10
    c: InternalAlignment(g234-g241 -> g233) x8
    c: Vertical(g205)
    c: Block(g205)
    c: Block(g215)
    c: Block(g233)
    c: Horizontal(g242)
    c: Horizontal(g243)
    c: Block(g242)
    c: Block(g243)
    c: Vertical(g244)
    c: Block(g244)
    c: Coincident(g270,g243)
    c: Weight(g245) = 1
    c: Equal(g245, g246-g269) x24
    c: Coincident(g270,g244)
    c: InternalAlignment(g245-g269 -> g270) x25
    c: InternalAlignment(g271-g293 -> g270) x23
    c: Coincident(g305,g242)
    c: Weight(g294) = 1
    c: Equal(g294, g295-g304) x10
    c: Coincident(g305,g242)
    c: InternalAlignment(g294-g304 -> g305) x11
    c: InternalAlignment(g306-g314 -> g305) x9
    c: Block(g305)
    c: Coincident(g327,g243)
    c: Weight(g315) = 1
    c: Equal(g315, g316-g326) x11
    c: Coincident(g327,g244)
    c: InternalAlignment(g315-g326 -> g327) x12
    c: InternalAlignment(g328-g337 -> g327) x10
    c: Block(g327)
    c: Block(g270)
FEATURE [Part::Extrusion] Extrude075  label="CommodoreLogoAndText002"
  Base = -> Sketch084
  Dir = (0,0,1)
  DirMode = 2
  FaceMakerClass = Part::FaceMakerBullseye
  LengthFwd = 10
  LengthRev = 0
  Solid = true
  Symmetric = false
FEATURE [Part::FeaturePython] Clone001  label="CommodoreLogoAndTextScale001"  # Draft clone (typed FeaturePython)
  AttacherType = Attacher::AttachEngine3D
  Fuse = false
  Objects = -> [Extrude075]
  Placement = pos=(112.566,5.37,73.6) rot=(0,0,1;0rad)
  Scale = (0.62,0.62,1)
FEATURE [Part::Cut] Cut073  label="sideA005"
  Base = -> Extrude002
  Tool = -> Part__Mirroring
FEATURE [Part::Cut] Cut074  label="sideB005"
  Base = -> Extrude028
  Tool = -> Clone001
FEATURE [Sketcher::SketchObject] Sketch085
  FullyConstrained = true
  Placement = pos=(0,0,0) rot=(-1,0,0;4.71239rad)
  sketch-geometry (10):
    g0: LineSegment StartX=0 StartY=0 StartZ=0 EndX=-7 EndY=0 EndZ=0
    g1: LineSegment StartX=-7 StartY=10 StartZ=0 EndX=-6.5 EndY=10 EndZ=0
    g2: LineSegment StartX=0 StartY=10 StartZ=0 EndX=-0.5 EndY=10 EndZ=0
    g3: ArcOfCircle CenterX=-3.5 CenterY=10 CenterZ=0 NormalX=0 NormalY=0 NormalZ=1 AngleXU=0 Radius=3 StartAngle=3.14159 EndAngle=6.28319
    g4: LineSegment StartX=-7 StartY=0 StartZ=0 EndX=-10.5 EndY=0 EndZ=0
    g5: LineSegment StartX=0 StartY=0 StartZ=0 EndX=3.5 EndY=0 EndZ=0
    g6: ArcOfCircle CenterX=-10.5 CenterY=3.5 CenterZ=0 NormalX=0 NormalY=0 NormalZ=1 AngleXU=0 Radius=3.5 StartAngle=4.71239 EndAngle=6.28319
    g7: ArcOfCircle CenterX=3.5 CenterY=3.5 CenterZ=0 NormalX=0 NormalY=0 NormalZ=1 AngleXU=0 Radius=3.5 StartAngle=3.14159 EndAngle=4.71239
    g8: LineSegment StartX=-7 StartY=3.5 StartZ=0 EndX=-7 EndY=10 EndZ=0
    g9: LineSegment StartX=0 StartY=10 StartZ=0 EndX=0 EndY=3.5 EndZ=0
  constraints (26):
    c: Coincident(g0,g-1)
    c: Horizontal(g0)
    c: Distance(g0) = 7
    c: Horizontal(g1)
    c: Distance(g1) = 0.5
    c: Horizontal(g2)
    c: Distance(g2) = 0.5
    c: Coincident(g3,g1)
    c: Coincident(g3,g2)
    c: Block(g3)
    c: Coincident(g4,g0)
    c: Horizontal(g4)
    c: Distance(g4) = 3.5
    c: Coincident(g5,g0)
    c: Distance(g5) = 3.5
    c: Horizontal(g5)
    c: Coincident(g6,g4)
    c: Block(g6)
    c: Coincident(g7,g5)
    c: Block(g7)
    c: Coincident(g8,g6)
    c: Coincident(g8,g1)
    c: Vertical(g8)
    c: Coincident(g9,g2)
    c: Coincident(g9,g7)
    c: Vertical(g9)
FEATURE [Part::Extrusion] Extrude076  label="backRightCasePillarSideBracket"
  Base = -> Sketch085
  Dir = (0,-1,3e-16)
  DirMode = 2
  FaceMakerClass = Part::FaceMakerBullseye
  LengthFwd = 6.7
  LengthRev = 0
  Placement = pos=(16,11.5,0) rot=(0,0,1;0rad)
  Solid = true
  Symmetric = false
FEATURE [Sketcher::SketchObject] Sketch086
  FullyConstrained = true
  Placement = pos=(0,0,0) rot=(1,0,0;1.5708rad)
  sketch-geometry (10):
    g0: LineSegment StartX=0 StartY=0 StartZ=0 EndX=-7 EndY=0 EndZ=0
    g1: LineSegment StartX=-7 StartY=10 StartZ=0 EndX=-6.5 EndY=10 EndZ=0
    g2: LineSegment StartX=0 StartY=10 StartZ=0 EndX=-0.5 EndY=10 EndZ=0
    g3: ArcOfCircle CenterX=-3.5 CenterY=10 CenterZ=0 NormalX=0 NormalY=0 NormalZ=1 AngleXU=0 Radius=3 StartAngle=3.14159 EndAngle=6.28319
    g4: LineSegment StartX=-7 StartY=0 StartZ=0 EndX=-10.5 EndY=0 EndZ=0
    g5: LineSegment StartX=0 StartY=0 StartZ=0 EndX=3.5 EndY=0 EndZ=0
    g6: ArcOfCircle CenterX=-10.5 CenterY=3.5 CenterZ=0 NormalX=0 NormalY=0 NormalZ=1 AngleXU=0 Radius=3.5 StartAngle=4.71239 EndAngle=6.28319
    g7: ArcOfCircle CenterX=3.5 CenterY=3.5 CenterZ=0 NormalX=0 NormalY=0 NormalZ=1 AngleXU=0 Radius=3.5 StartAngle=3.14159 EndAngle=4.71239
    g8: LineSegment StartX=-7 StartY=3.5 StartZ=0 EndX=-7 EndY=10 EndZ=0
    g9: LineSegment StartX=0 StartY=10 StartZ=0 EndX=0 EndY=3.5 EndZ=0
  constraints (26):
    c: Coincident(g0,g-1)
    c: Horizontal(g0)
    c: Distance(g0) = 7
    c: Horizontal(g1)
    c: Distance(g1) = 0.5
    c: Horizontal(g2)
    c: Distance(g2) = 0.5
    c: Coincident(g3,g1)
    c: Coincident(g3,g2)
    c: Block(g3)
    c: Coincident(g4,g0)
    c: Horizontal(g4)
    c: Distance(g4) = 3.5
    c: Coincident(g5,g0)
    c: Distance(g5) = 3.5
    c: Horizontal(g5)
    c: Coincident(g6,g4)
    c: Block(g6)
    c: Coincident(g7,g5)
    c: Block(g7)
    c: Coincident(g8,g6)
    c: Coincident(g8,g1)
    c: Vertical(g8)
    c: Coincident(g9,g2)
    c: Coincident(g9,g7)
    c: Vertical(g9)
FEATURE [Part::Extrusion] Extrude077  label="backLeftCasePillarSideBracket001"
  Base = -> Sketch086
  Dir = (0,-1,3e-16)
  DirMode = 2
  FaceMakerClass = Part::FaceMakerBullseye
  LengthFwd = 6.7
  LengthRev = 0
  Placement = pos=(9,11.5,72) rot=(0,1,0;3.14159rad)
  Solid = true
  Symmetric = false
FEATURE [Sketcher::SketchObject] Sketch087
  FullyConstrained = true
  Placement = pos=(0,0,0) rot=(1,0,0;1.5708rad)
  sketch-geometry (8):
    g0: LineSegment StartX=0 StartY=4e-16 StartZ=0 EndX=-7 EndY=4e-16 EndZ=0
    g1: LineSegment StartX=-7 StartY=4e-16 StartZ=0 EndX=-10.5 EndY=4e-16 EndZ=0
    g2: LineSegment StartX=0 StartY=4e-16 StartZ=0 EndX=3.5 EndY=4e-16 EndZ=0
    g3: ArcOfCircle CenterX=-10.5 CenterY=3.5 CenterZ=0 NormalX=0 NormalY=0 NormalZ=1 AngleXU=0 Radius=3.5 StartAngle=4.71239 EndAngle=6.28319
    g4: ArcOfCircle CenterX=3.5 CenterY=3.5 CenterZ=0 NormalX=0 NormalY=0 NormalZ=1 AngleXU=0 Radius=3.5 StartAngle=3.14159 EndAngle=4.71239
    g5: ArcOfCircle CenterX=-3.5 CenterY=3.5 CenterZ=0 NormalX=0 NormalY=0 NormalZ=1 AngleXU=0 Radius=3 StartAngle=3.14159 EndAngle=6.28319
    g6: LineSegment StartX=-7 StartY=3.5 StartZ=0 EndX=-6.5 EndY=3.5 EndZ=0
    g7: LineSegment StartX=-0.5 StartY=3.5 StartZ=0 EndX=0 EndY=3.5 EndZ=0
  constraints (20):
    c: Coincident(g0,g-1)
    c: Horizontal(g0)
    c: Distance(g0) = 7
    c: Coincident(g1,g0)
    c: Horizontal(g1)
    c: Distance(g1) = 3.5
    c: Coincident(g2,g0)
    c: Distance(g2) = 3.5
    c: Horizontal(g2)
    c: Coincident(g3,g1)
    c: Block(g3)
    c: Coincident(g4,g2)
    c: Block(g4)
    c: Horizontal(g6)
    c: Coincident(g5,g6)
    c: Block(g5)
    c: Coincident(g6,g3)
    c: Coincident(g7,g5)
    c: Coincident(g7,g4)
    c: Horizontal(g7)
FEATURE [Part::Extrusion] Extrude078  label="frontBackLeftCasePillarSideBracket001"
  Base = -> Sketch087
  Dir = (0,-1,2e-16)
  DirMode = 2
  FaceMakerClass = Part::FaceMakerBullseye
  LengthFwd = 6.7
  LengthRev = 0
  Placement = pos=(93,11.5,0) rot=(0,0,1;0rad)
  Solid = true
  Symmetric = false
FEATURE [Sketcher::SketchObject] Sketch088
  FullyConstrained = true
  Placement = pos=(0,0,0) rot=(1,0,0;1.5708rad)
  sketch-geometry (8):
    g0: LineSegment StartX=0 StartY=4e-16 StartZ=0 EndX=-7 EndY=4e-16 EndZ=0
    g1: LineSegment StartX=-7 StartY=4e-16 StartZ=0 EndX=-10.5 EndY=4e-16 EndZ=0
    g2: LineSegment StartX=0 StartY=4e-16 StartZ=0 EndX=3.5 EndY=4e-16 EndZ=0
    g3: ArcOfCircle CenterX=-10.5 CenterY=3.5 CenterZ=0 NormalX=0 NormalY=0 NormalZ=1 AngleXU=0 Radius=3.5 StartAngle=4.71239 EndAngle=6.28319
    g4: ArcOfCircle CenterX=3.5 CenterY=3.5 CenterZ=0 NormalX=0 NormalY=0 NormalZ=1 AngleXU=0 Radius=3.5 StartAngle=3.14159 EndAngle=4.71239
    g5: ArcOfCircle CenterX=-3.5 CenterY=3.5 CenterZ=0 NormalX=0 NormalY=0 NormalZ=1 AngleXU=0 Radius=3 StartAngle=3.14159 EndAngle=6.28319
    g6: LineSegment StartX=-7 StartY=3.5 StartZ=0 EndX=-6.5 EndY=3.5 EndZ=0
    g7: LineSegment StartX=-0.5 StartY=3.5 StartZ=0 EndX=0 EndY=3.5 EndZ=0
  constraints (20):
    c: Coincident(g0,g-1)
    c: Horizontal(g0)
    c: Distance(g0) = 7
    c: Coincident(g1,g0)
    c: Horizontal(g1)
    c: Distance(g1) = 3.5
    c: Coincident(g2,g0)
    c: Distance(g2) = 3.5
    c: Horizontal(g2)
    c: Coincident(g3,g1)
    c: Block(g3)
    c: Coincident(g4,g2)
    c: Block(g4)
    c: Horizontal(g6)
    c: Coincident(g5,g6)
    c: Block(g5)
    c: Coincident(g6,g3)
    c: Coincident(g7,g5)
    c: Coincident(g7,g4)
    c: Horizontal(g7)
FEATURE [Part::Extrusion] Extrude079  label="frontFrontLeftCasePillarSideBracket002"
  Base = -> Sketch088
  Dir = (0,-1,2e-16)
  DirMode = 2
  FaceMakerClass = Part::FaceMakerBullseye
  LengthFwd = 2
  LengthRev = 0
  Placement = pos=(113,11.5,0) rot=(0,0,1;0rad)
  Solid = true
  Symmetric = false
